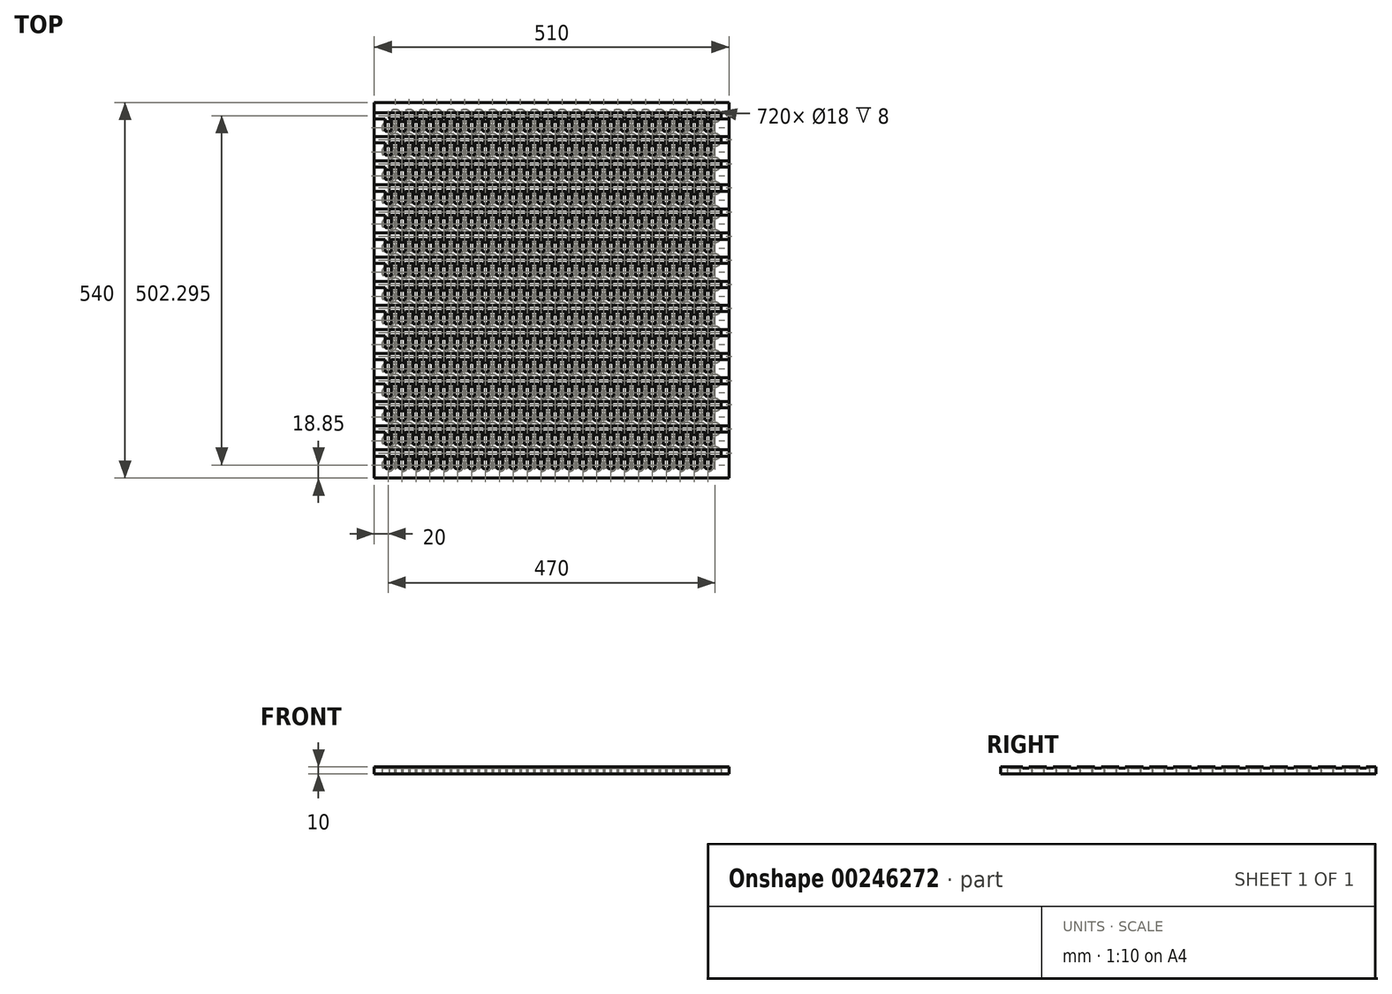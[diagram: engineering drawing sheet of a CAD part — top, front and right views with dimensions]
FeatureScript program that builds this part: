
annotation { "Feature Type Name" : "Feature", "Feature Type Description" : "" }
export const myFeature = defineFeature(function(context is Context, id is Id, definition is map)
    precondition{}
    {
        {
            var Q0;
            Q0=qCreatedBy(makeId("Top.planeOp"),FACE);
            var sketch = newSketch(context, id + "F0", { "sketchPlane" : qUnion([Q0])});
            skCircle(sketch, "E0", {"center": v(0, 0) * mm, "radius": 9 * mm});
            skCircle(sketch, "E1.1.0.0", {"center": v(20, 0) * mm, "radius": 9 * mm});
            skCircle(sketch, "E1.2.0.0", {"center": v(40, 0) * mm, "radius": 9 * mm});
            skCircle(sketch, "E1.3.0.0", {"center": v(60, 0) * mm, "radius": 9 * mm});
            skCircle(sketch, "E1.4.0.0", {"center": v(80, 0) * mm, "radius": 9 * mm});
            skCircle(sketch, "E1.5.0.0", {"center": v(100, 0) * mm, "radius": 9 * mm});
            skCircle(sketch, "E1.6.0.0", {"center": v(120, 0) * mm, "radius": 9 * mm});
            skCircle(sketch, "E1.7.0.0", {"center": v(140, 0) * mm, "radius": 9 * mm});
            skCircle(sketch, "E1.8.0.0", {"center": v(160, 0) * mm, "radius": 9 * mm});
            skCircle(sketch, "E1.9.0.0", {"center": v(180, 0) * mm, "radius": 9 * mm});
            skCircle(sketch, "E1.10.0.0", {"center": v(200, 0) * mm, "radius": 9 * mm});
            skCircle(sketch, "E1.11.0.0", {"center": v(220, 0) * mm, "radius": 9 * mm});
            skCircle(sketch, "E1.12.0.0", {"center": v(240, 0) * mm, "radius": 9 * mm});
            skCircle(sketch, "E1.13.0.0", {"center": v(260, 0) * mm, "radius": 9 * mm});
            skCircle(sketch, "E1.14.0.0", {"center": v(280, 0) * mm, "radius": 9 * mm});
            skCircle(sketch, "E1.15.0.0", {"center": v(300, 0) * mm, "radius": 9 * mm});
            skCircle(sketch, "E1.16.0.0", {"center": v(320, 0) * mm, "radius": 9 * mm});
            skCircle(sketch, "E1.17.0.0", {"center": v(340, 0) * mm, "radius": 9 * mm});
            skCircle(sketch, "E1.18.0.0", {"center": v(360, 0) * mm, "radius": 9 * mm});
            skCircle(sketch, "E1.19.0.0", {"center": v(380, 0) * mm, "radius": 9 * mm});
            skCircle(sketch, "E1.20.0.0", {"center": v(400, 0) * mm, "radius": 9 * mm});
            skCircle(sketch, "E1.21.0.0", {"center": v(420, 0) * mm, "radius": 9 * mm});
            skCircle(sketch, "E1.22.0.0", {"center": v(440, 0) * mm, "radius": 9 * mm});
            skCircle(sketch, "E1.23.0.0", {"center": v(460, 0) * mm, "radius": 9 * mm});
            skLineSegment(sketch, "E1.direction1", {"start": v(0, 0) * mm, "end": v(20, 0) * mm, "construction": true});
            skCircle(sketch, "E2", {"center": v(10, 17.32) * mm, "radius": 9 * mm});
            skCircle(sketch, "E3.1.0.0", {"center": v(30, 17.32) * mm, "radius": 9 * mm});
            skCircle(sketch, "E3.2.0.0", {"center": v(50, 17.32) * mm, "radius": 9 * mm});
            skCircle(sketch, "E3.3.0.0", {"center": v(70, 17.32) * mm, "radius": 9 * mm});
            skCircle(sketch, "E3.4.0.0", {"center": v(90, 17.32) * mm, "radius": 9 * mm});
            skCircle(sketch, "E3.5.0.0", {"center": v(110, 17.32) * mm, "radius": 9 * mm});
            skCircle(sketch, "E3.6.0.0", {"center": v(130, 17.32) * mm, "radius": 9 * mm});
            skCircle(sketch, "E3.7.0.0", {"center": v(150, 17.32) * mm, "radius": 9 * mm});
            skCircle(sketch, "E3.8.0.0", {"center": v(170, 17.32) * mm, "radius": 9 * mm});
            skCircle(sketch, "E3.9.0.0", {"center": v(190, 17.32) * mm, "radius": 9 * mm});
            skCircle(sketch, "E3.10.0.0", {"center": v(210, 17.32) * mm, "radius": 9 * mm});
            skCircle(sketch, "E3.11.0.0", {"center": v(230, 17.32) * mm, "radius": 9 * mm});
            skCircle(sketch, "E3.12.0.0", {"center": v(250, 17.32) * mm, "radius": 9 * mm});
            skCircle(sketch, "E3.13.0.0", {"center": v(270, 17.32) * mm, "radius": 9 * mm});
            skCircle(sketch, "E3.14.0.0", {"center": v(290, 17.32) * mm, "radius": 9 * mm});
            skCircle(sketch, "E3.15.0.0", {"center": v(310, 17.32) * mm, "radius": 9 * mm});
            skCircle(sketch, "E3.16.0.0", {"center": v(330, 17.32) * mm, "radius": 9 * mm});
            skCircle(sketch, "E3.17.0.0", {"center": v(350, 17.32) * mm, "radius": 9 * mm});
            skCircle(sketch, "E3.18.0.0", {"center": v(370, 17.32) * mm, "radius": 9 * mm});
            skCircle(sketch, "E3.19.0.0", {"center": v(390, 17.32) * mm, "radius": 9 * mm});
            skCircle(sketch, "E3.20.0.0", {"center": v(410, 17.32) * mm, "radius": 9 * mm});
            skCircle(sketch, "E3.21.0.0", {"center": v(430, 17.32) * mm, "radius": 9 * mm});
            skCircle(sketch, "E3.22.0.0", {"center": v(450, 17.32) * mm, "radius": 9 * mm});
            skCircle(sketch, "E3.23.0.0", {"center": v(470, 17.32) * mm, "radius": 9 * mm});
            skLineSegment(sketch, "E3.direction1", {"start": v(10, 17.32) * mm, "end": v(30, 17.32) * mm, "construction": true});
            skCircle(sketch, "E4.0.1.0", {"center": v(280, 34.64) * mm, "radius": 9 * mm});
            skCircle(sketch, "E4.0.1.1", {"center": v(260, 34.64) * mm, "radius": 9 * mm});
            skCircle(sketch, "E4.0.1.2", {"center": v(130, 51.96) * mm, "radius": 9 * mm});
            skCircle(sketch, "E4.0.1.3", {"center": v(60, 34.64) * mm, "radius": 9 * mm});
            skCircle(sketch, "E4.0.1.4", {"center": v(80, 34.64) * mm, "radius": 9 * mm});
            skCircle(sketch, "E4.0.1.5", {"center": v(100, 34.64) * mm, "radius": 9 * mm});
            skCircle(sketch, "E4.0.1.6", {"center": v(350, 51.96) * mm, "radius": 9 * mm});
            skCircle(sketch, "E4.0.1.7", {"center": v(0, 34.64) * mm, "radius": 9 * mm});
            skCircle(sketch, "E4.0.1.8", {"center": v(120, 34.64) * mm, "radius": 9 * mm});
            skCircle(sketch, "E4.0.1.9", {"center": v(30, 51.96) * mm, "radius": 9 * mm});
            skCircle(sketch, "E4.0.1.10", {"center": v(380, 34.64) * mm, "radius": 9 * mm});
            skCircle(sketch, "E4.0.1.11", {"center": v(140, 34.64) * mm, "radius": 9 * mm});
            skCircle(sketch, "E4.0.1.12", {"center": v(450, 51.96) * mm, "radius": 9 * mm});
            skCircle(sketch, "E4.0.1.13", {"center": v(160, 34.64) * mm, "radius": 9 * mm});
            skCircle(sketch, "E4.0.1.14", {"center": v(300, 34.64) * mm, "radius": 9 * mm});
            skCircle(sketch, "E4.0.1.15", {"center": v(40, 34.64) * mm, "radius": 9 * mm});
            skCircle(sketch, "E4.0.1.16", {"center": v(210, 51.96) * mm, "radius": 9 * mm});
            skCircle(sketch, "E4.0.1.17", {"center": v(330, 51.96) * mm, "radius": 9 * mm});
            skCircle(sketch, "E4.0.1.18", {"center": v(270, 51.96) * mm, "radius": 9 * mm});
            skCircle(sketch, "E4.0.1.19", {"center": v(440, 34.64) * mm, "radius": 9 * mm});
            skCircle(sketch, "E4.0.1.20", {"center": v(110, 51.96) * mm, "radius": 9 * mm});
            skCircle(sketch, "E4.0.1.21", {"center": v(250, 51.96) * mm, "radius": 9 * mm});
            skCircle(sketch, "E4.0.1.22", {"center": v(180, 34.64) * mm, "radius": 9 * mm});
            skCircle(sketch, "E4.0.1.23", {"center": v(430, 51.96) * mm, "radius": 9 * mm});
            skCircle(sketch, "E4.0.1.24", {"center": v(200, 34.64) * mm, "radius": 9 * mm});
            skCircle(sketch, "E4.0.1.25", {"center": v(420, 34.64) * mm, "radius": 9 * mm});
            skCircle(sketch, "E4.0.1.26", {"center": v(70, 51.96) * mm, "radius": 9 * mm});
            skCircle(sketch, "E4.0.1.27", {"center": v(390, 51.96) * mm, "radius": 9 * mm});
            skCircle(sketch, "E4.0.1.28", {"center": v(220, 34.64) * mm, "radius": 9 * mm});
            skCircle(sketch, "E4.0.1.29", {"center": v(190, 51.96) * mm, "radius": 9 * mm});
            skCircle(sketch, "E4.0.1.30", {"center": v(90, 51.96) * mm, "radius": 9 * mm});
            skCircle(sketch, "E4.0.1.31", {"center": v(230, 51.96) * mm, "radius": 9 * mm});
            skCircle(sketch, "E4.0.1.32", {"center": v(150, 51.96) * mm, "radius": 9 * mm});
            skCircle(sketch, "E4.0.1.33", {"center": v(470, 51.96) * mm, "radius": 9 * mm});
            skCircle(sketch, "E4.0.1.34", {"center": v(410, 51.96) * mm, "radius": 9 * mm});
            skCircle(sketch, "E4.0.1.35", {"center": v(50, 51.96) * mm, "radius": 9 * mm});
            skCircle(sketch, "E4.0.1.36", {"center": v(400, 34.64) * mm, "radius": 9 * mm});
            skCircle(sketch, "E4.0.1.37", {"center": v(240, 34.64) * mm, "radius": 9 * mm});
            skCircle(sketch, "E4.0.1.38", {"center": v(320, 34.64) * mm, "radius": 9 * mm});
            skCircle(sketch, "E4.0.1.39", {"center": v(370, 51.96) * mm, "radius": 9 * mm});
            skCircle(sketch, "E4.0.1.40", {"center": v(10, 51.96) * mm, "radius": 9 * mm});
            skCircle(sketch, "E4.0.1.41", {"center": v(290, 51.96) * mm, "radius": 9 * mm});
            skCircle(sketch, "E4.0.1.42", {"center": v(360, 34.64) * mm, "radius": 9 * mm});
            skCircle(sketch, "E4.0.1.43", {"center": v(460, 34.64) * mm, "radius": 9 * mm});
            skCircle(sketch, "E4.0.1.44", {"center": v(310, 51.96) * mm, "radius": 9 * mm});
            skCircle(sketch, "E4.0.1.45", {"center": v(340, 34.64) * mm, "radius": 9 * mm});
            skCircle(sketch, "E4.0.1.46", {"center": v(170, 51.96) * mm, "radius": 9 * mm});
            skCircle(sketch, "E4.0.1.47", {"center": v(20, 34.64) * mm, "radius": 9 * mm});
            skLineSegment(sketch, "E4.0.1.48", {"start": v(0, 34.64) * mm, "end": v(20, 34.64) * mm, "construction": true});
            skLineSegment(sketch, "E4.0.1.49", {"start": v(10, 51.96) * mm, "end": v(30, 51.96) * mm, "construction": true});
            skCircle(sketch, "E4.0.2.0", {"center": v(280, 69.28) * mm, "radius": 9 * mm});
            skCircle(sketch, "E4.0.2.1", {"center": v(260, 69.28) * mm, "radius": 9 * mm});
            skCircle(sketch, "E4.0.2.2", {"center": v(130, 86.6) * mm, "radius": 9 * mm});
            skCircle(sketch, "E4.0.2.3", {"center": v(60, 69.28) * mm, "radius": 9 * mm});
            skCircle(sketch, "E4.0.2.4", {"center": v(80, 69.28) * mm, "radius": 9 * mm});
            skCircle(sketch, "E4.0.2.5", {"center": v(100, 69.28) * mm, "radius": 9 * mm});
            skCircle(sketch, "E4.0.2.6", {"center": v(350, 86.6) * mm, "radius": 9 * mm});
            skCircle(sketch, "E4.0.2.7", {"center": v(0, 69.28) * mm, "radius": 9 * mm});
            skCircle(sketch, "E4.0.2.8", {"center": v(120, 69.28) * mm, "radius": 9 * mm});
            skCircle(sketch, "E4.0.2.9", {"center": v(30, 86.6) * mm, "radius": 9 * mm});
            skCircle(sketch, "E4.0.2.10", {"center": v(380, 69.28) * mm, "radius": 9 * mm});
            skCircle(sketch, "E4.0.2.11", {"center": v(140, 69.28) * mm, "radius": 9 * mm});
            skCircle(sketch, "E4.0.2.12", {"center": v(450, 86.6) * mm, "radius": 9 * mm});
            skCircle(sketch, "E4.0.2.13", {"center": v(160, 69.28) * mm, "radius": 9 * mm});
            skCircle(sketch, "E4.0.2.14", {"center": v(300, 69.28) * mm, "radius": 9 * mm});
            skCircle(sketch, "E4.0.2.15", {"center": v(40, 69.28) * mm, "radius": 9 * mm});
            skCircle(sketch, "E4.0.2.16", {"center": v(210, 86.6) * mm, "radius": 9 * mm});
            skCircle(sketch, "E4.0.2.17", {"center": v(330, 86.6) * mm, "radius": 9 * mm});
            skCircle(sketch, "E4.0.2.18", {"center": v(270, 86.6) * mm, "radius": 9 * mm});
            skCircle(sketch, "E4.0.2.19", {"center": v(440, 69.28) * mm, "radius": 9 * mm});
            skCircle(sketch, "E4.0.2.20", {"center": v(110, 86.6) * mm, "radius": 9 * mm});
            skCircle(sketch, "E4.0.2.21", {"center": v(250, 86.6) * mm, "radius": 9 * mm});
            skCircle(sketch, "E4.0.2.22", {"center": v(180, 69.28) * mm, "radius": 9 * mm});
            skCircle(sketch, "E4.0.2.23", {"center": v(430, 86.6) * mm, "radius": 9 * mm});
            skCircle(sketch, "E4.0.2.24", {"center": v(200, 69.28) * mm, "radius": 9 * mm});
            skCircle(sketch, "E4.0.2.25", {"center": v(420, 69.28) * mm, "radius": 9 * mm});
            skCircle(sketch, "E4.0.2.26", {"center": v(70, 86.6) * mm, "radius": 9 * mm});
            skCircle(sketch, "E4.0.2.27", {"center": v(390, 86.6) * mm, "radius": 9 * mm});
            skCircle(sketch, "E4.0.2.28", {"center": v(220, 69.28) * mm, "radius": 9 * mm});
            skCircle(sketch, "E4.0.2.29", {"center": v(190, 86.6) * mm, "radius": 9 * mm});
            skCircle(sketch, "E4.0.2.30", {"center": v(90, 86.6) * mm, "radius": 9 * mm});
            skCircle(sketch, "E4.0.2.31", {"center": v(230, 86.6) * mm, "radius": 9 * mm});
            skCircle(sketch, "E4.0.2.32", {"center": v(150, 86.6) * mm, "radius": 9 * mm});
            skCircle(sketch, "E4.0.2.33", {"center": v(470, 86.6) * mm, "radius": 9 * mm});
            skCircle(sketch, "E4.0.2.34", {"center": v(410, 86.6) * mm, "radius": 9 * mm});
            skCircle(sketch, "E4.0.2.35", {"center": v(50, 86.6) * mm, "radius": 9 * mm});
            skCircle(sketch, "E4.0.2.36", {"center": v(400, 69.28) * mm, "radius": 9 * mm});
            skCircle(sketch, "E4.0.2.37", {"center": v(240, 69.28) * mm, "radius": 9 * mm});
            skCircle(sketch, "E4.0.2.38", {"center": v(320, 69.28) * mm, "radius": 9 * mm});
            skCircle(sketch, "E4.0.2.39", {"center": v(370, 86.6) * mm, "radius": 9 * mm});
            skCircle(sketch, "E4.0.2.40", {"center": v(10, 86.6) * mm, "radius": 9 * mm});
            skCircle(sketch, "E4.0.2.41", {"center": v(290, 86.6) * mm, "radius": 9 * mm});
            skCircle(sketch, "E4.0.2.42", {"center": v(360, 69.28) * mm, "radius": 9 * mm});
            skCircle(sketch, "E4.0.2.43", {"center": v(460, 69.28) * mm, "radius": 9 * mm});
            skCircle(sketch, "E4.0.2.44", {"center": v(310, 86.6) * mm, "radius": 9 * mm});
            skCircle(sketch, "E4.0.2.45", {"center": v(340, 69.28) * mm, "radius": 9 * mm});
            skCircle(sketch, "E4.0.2.46", {"center": v(170, 86.6) * mm, "radius": 9 * mm});
            skCircle(sketch, "E4.0.2.47", {"center": v(20, 69.28) * mm, "radius": 9 * mm});
            skLineSegment(sketch, "E4.0.2.48", {"start": v(0, 69.28) * mm, "end": v(20, 69.28) * mm, "construction": true});
            skLineSegment(sketch, "E4.0.2.49", {"start": v(10, 86.6) * mm, "end": v(30, 86.6) * mm, "construction": true});
            skCircle(sketch, "E4.0.3.0", {"center": v(280, 103.92) * mm, "radius": 9 * mm});
            skCircle(sketch, "E4.0.3.1", {"center": v(260, 103.92) * mm, "radius": 9 * mm});
            skCircle(sketch, "E4.0.3.2", {"center": v(130, 121.24) * mm, "radius": 9 * mm});
            skCircle(sketch, "E4.0.3.3", {"center": v(60, 103.92) * mm, "radius": 9 * mm});
            skCircle(sketch, "E4.0.3.4", {"center": v(80, 103.92) * mm, "radius": 9 * mm});
            skCircle(sketch, "E4.0.3.5", {"center": v(100, 103.92) * mm, "radius": 9 * mm});
            skCircle(sketch, "E4.0.3.6", {"center": v(350, 121.24) * mm, "radius": 9 * mm});
            skCircle(sketch, "E4.0.3.7", {"center": v(0, 103.92) * mm, "radius": 9 * mm});
            skCircle(sketch, "E4.0.3.8", {"center": v(120, 103.92) * mm, "radius": 9 * mm});
            skCircle(sketch, "E4.0.3.9", {"center": v(30, 121.24) * mm, "radius": 9 * mm});
            skCircle(sketch, "E4.0.3.10", {"center": v(380, 103.92) * mm, "radius": 9 * mm});
            skCircle(sketch, "E4.0.3.11", {"center": v(140, 103.92) * mm, "radius": 9 * mm});
            skCircle(sketch, "E4.0.3.12", {"center": v(450, 121.24) * mm, "radius": 9 * mm});
            skCircle(sketch, "E4.0.3.13", {"center": v(160, 103.92) * mm, "radius": 9 * mm});
            skCircle(sketch, "E4.0.3.14", {"center": v(300, 103.92) * mm, "radius": 9 * mm});
            skCircle(sketch, "E4.0.3.15", {"center": v(40, 103.92) * mm, "radius": 9 * mm});
            skCircle(sketch, "E4.0.3.16", {"center": v(210, 121.24) * mm, "radius": 9 * mm});
            skCircle(sketch, "E4.0.3.17", {"center": v(330, 121.24) * mm, "radius": 9 * mm});
            skCircle(sketch, "E4.0.3.18", {"center": v(270, 121.24) * mm, "radius": 9 * mm});
            skCircle(sketch, "E4.0.3.19", {"center": v(440, 103.92) * mm, "radius": 9 * mm});
            skCircle(sketch, "E4.0.3.20", {"center": v(110, 121.24) * mm, "radius": 9 * mm});
            skCircle(sketch, "E4.0.3.21", {"center": v(250, 121.24) * mm, "radius": 9 * mm});
            skCircle(sketch, "E4.0.3.22", {"center": v(180, 103.92) * mm, "radius": 9 * mm});
            skCircle(sketch, "E4.0.3.23", {"center": v(430, 121.24) * mm, "radius": 9 * mm});
            skCircle(sketch, "E4.0.3.24", {"center": v(200, 103.92) * mm, "radius": 9 * mm});
            skCircle(sketch, "E4.0.3.25", {"center": v(420, 103.92) * mm, "radius": 9 * mm});
            skCircle(sketch, "E4.0.3.26", {"center": v(70, 121.24) * mm, "radius": 9 * mm});
            skCircle(sketch, "E4.0.3.27", {"center": v(390, 121.24) * mm, "radius": 9 * mm});
            skCircle(sketch, "E4.0.3.28", {"center": v(220, 103.92) * mm, "radius": 9 * mm});
            skCircle(sketch, "E4.0.3.29", {"center": v(190, 121.24) * mm, "radius": 9 * mm});
            skCircle(sketch, "E4.0.3.30", {"center": v(90, 121.24) * mm, "radius": 9 * mm});
            skCircle(sketch, "E4.0.3.31", {"center": v(230, 121.24) * mm, "radius": 9 * mm});
            skCircle(sketch, "E4.0.3.32", {"center": v(150, 121.24) * mm, "radius": 9 * mm});
            skCircle(sketch, "E4.0.3.33", {"center": v(470, 121.24) * mm, "radius": 9 * mm});
            skCircle(sketch, "E4.0.3.34", {"center": v(410, 121.24) * mm, "radius": 9 * mm});
            skCircle(sketch, "E4.0.3.35", {"center": v(50, 121.24) * mm, "radius": 9 * mm});
            skCircle(sketch, "E4.0.3.36", {"center": v(400, 103.92) * mm, "radius": 9 * mm});
            skCircle(sketch, "E4.0.3.37", {"center": v(240, 103.92) * mm, "radius": 9 * mm});
            skCircle(sketch, "E4.0.3.38", {"center": v(320, 103.92) * mm, "radius": 9 * mm});
            skCircle(sketch, "E4.0.3.39", {"center": v(370, 121.24) * mm, "radius": 9 * mm});
            skCircle(sketch, "E4.0.3.40", {"center": v(10, 121.24) * mm, "radius": 9 * mm});
            skCircle(sketch, "E4.0.3.41", {"center": v(290, 121.24) * mm, "radius": 9 * mm});
            skCircle(sketch, "E4.0.3.42", {"center": v(360, 103.92) * mm, "radius": 9 * mm});
            skCircle(sketch, "E4.0.3.43", {"center": v(460, 103.92) * mm, "radius": 9 * mm});
            skCircle(sketch, "E4.0.3.44", {"center": v(310, 121.24) * mm, "radius": 9 * mm});
            skCircle(sketch, "E4.0.3.45", {"center": v(340, 103.92) * mm, "radius": 9 * mm});
            skCircle(sketch, "E4.0.3.46", {"center": v(170, 121.24) * mm, "radius": 9 * mm});
            skCircle(sketch, "E4.0.3.47", {"center": v(20, 103.92) * mm, "radius": 9 * mm});
            skLineSegment(sketch, "E4.0.3.48", {"start": v(0, 103.92) * mm, "end": v(20, 103.92) * mm, "construction": true});
            skLineSegment(sketch, "E4.0.3.49", {"start": v(10, 121.24) * mm, "end": v(30, 121.24) * mm, "construction": true});
            skCircle(sketch, "E4.0.4.0", {"center": v(280, 138.56) * mm, "radius": 9 * mm});
            skCircle(sketch, "E4.0.4.1", {"center": v(260, 138.56) * mm, "radius": 9 * mm});
            skCircle(sketch, "E4.0.4.2", {"center": v(130, 155.88) * mm, "radius": 9 * mm});
            skCircle(sketch, "E4.0.4.3", {"center": v(60, 138.56) * mm, "radius": 9 * mm});
            skCircle(sketch, "E4.0.4.4", {"center": v(80, 138.56) * mm, "radius": 9 * mm});
            skCircle(sketch, "E4.0.4.5", {"center": v(100, 138.56) * mm, "radius": 9 * mm});
            skCircle(sketch, "E4.0.4.6", {"center": v(350, 155.88) * mm, "radius": 9 * mm});
            skCircle(sketch, "E4.0.4.7", {"center": v(0, 138.56) * mm, "radius": 9 * mm});
            skCircle(sketch, "E4.0.4.8", {"center": v(120, 138.56) * mm, "radius": 9 * mm});
            skCircle(sketch, "E4.0.4.9", {"center": v(30, 155.88) * mm, "radius": 9 * mm});
            skCircle(sketch, "E4.0.4.10", {"center": v(380, 138.56) * mm, "radius": 9 * mm});
            skCircle(sketch, "E4.0.4.11", {"center": v(140, 138.56) * mm, "radius": 9 * mm});
            skCircle(sketch, "E4.0.4.12", {"center": v(450, 155.88) * mm, "radius": 9 * mm});
            skCircle(sketch, "E4.0.4.13", {"center": v(160, 138.56) * mm, "radius": 9 * mm});
            skCircle(sketch, "E4.0.4.14", {"center": v(300, 138.56) * mm, "radius": 9 * mm});
            skCircle(sketch, "E4.0.4.15", {"center": v(40, 138.56) * mm, "radius": 9 * mm});
            skCircle(sketch, "E4.0.4.16", {"center": v(210, 155.88) * mm, "radius": 9 * mm});
            skCircle(sketch, "E4.0.4.17", {"center": v(330, 155.88) * mm, "radius": 9 * mm});
            skCircle(sketch, "E4.0.4.18", {"center": v(270, 155.88) * mm, "radius": 9 * mm});
            skCircle(sketch, "E4.0.4.19", {"center": v(440, 138.56) * mm, "radius": 9 * mm});
            skCircle(sketch, "E4.0.4.20", {"center": v(110, 155.88) * mm, "radius": 9 * mm});
            skCircle(sketch, "E4.0.4.21", {"center": v(250, 155.88) * mm, "radius": 9 * mm});
            skCircle(sketch, "E4.0.4.22", {"center": v(180, 138.56) * mm, "radius": 9 * mm});
            skCircle(sketch, "E4.0.4.23", {"center": v(430, 155.88) * mm, "radius": 9 * mm});
            skCircle(sketch, "E4.0.4.24", {"center": v(200, 138.56) * mm, "radius": 9 * mm});
            skCircle(sketch, "E4.0.4.25", {"center": v(420, 138.56) * mm, "radius": 9 * mm});
            skCircle(sketch, "E4.0.4.26", {"center": v(70, 155.88) * mm, "radius": 9 * mm});
            skCircle(sketch, "E4.0.4.27", {"center": v(390, 155.88) * mm, "radius": 9 * mm});
            skCircle(sketch, "E4.0.4.28", {"center": v(220, 138.56) * mm, "radius": 9 * mm});
            skCircle(sketch, "E4.0.4.29", {"center": v(190, 155.88) * mm, "radius": 9 * mm});
            skCircle(sketch, "E4.0.4.30", {"center": v(90, 155.88) * mm, "radius": 9 * mm});
            skCircle(sketch, "E4.0.4.31", {"center": v(230, 155.88) * mm, "radius": 9 * mm});
            skCircle(sketch, "E4.0.4.32", {"center": v(150, 155.88) * mm, "radius": 9 * mm});
            skCircle(sketch, "E4.0.4.33", {"center": v(470, 155.88) * mm, "radius": 9 * mm});
            skCircle(sketch, "E4.0.4.34", {"center": v(410, 155.88) * mm, "radius": 9 * mm});
            skCircle(sketch, "E4.0.4.35", {"center": v(50, 155.88) * mm, "radius": 9 * mm});
            skCircle(sketch, "E4.0.4.36", {"center": v(400, 138.56) * mm, "radius": 9 * mm});
            skCircle(sketch, "E4.0.4.37", {"center": v(240, 138.56) * mm, "radius": 9 * mm});
            skCircle(sketch, "E4.0.4.38", {"center": v(320, 138.56) * mm, "radius": 9 * mm});
            skCircle(sketch, "E4.0.4.39", {"center": v(370, 155.88) * mm, "radius": 9 * mm});
            skCircle(sketch, "E4.0.4.40", {"center": v(10, 155.88) * mm, "radius": 9 * mm});
            skCircle(sketch, "E4.0.4.41", {"center": v(290, 155.88) * mm, "radius": 9 * mm});
            skCircle(sketch, "E4.0.4.42", {"center": v(360, 138.56) * mm, "radius": 9 * mm});
            skCircle(sketch, "E4.0.4.43", {"center": v(460, 138.56) * mm, "radius": 9 * mm});
            skCircle(sketch, "E4.0.4.44", {"center": v(310, 155.88) * mm, "radius": 9 * mm});
            skCircle(sketch, "E4.0.4.45", {"center": v(340, 138.56) * mm, "radius": 9 * mm});
            skCircle(sketch, "E4.0.4.46", {"center": v(170, 155.88) * mm, "radius": 9 * mm});
            skCircle(sketch, "E4.0.4.47", {"center": v(20, 138.56) * mm, "radius": 9 * mm});
            skLineSegment(sketch, "E4.0.4.48", {"start": v(0, 138.56) * mm, "end": v(20, 138.56) * mm, "construction": true});
            skLineSegment(sketch, "E4.0.4.49", {"start": v(10, 155.88) * mm, "end": v(30, 155.88) * mm, "construction": true});
            skCircle(sketch, "E4.0.5.0", {"center": v(280, 173.2) * mm, "radius": 9 * mm});
            skCircle(sketch, "E4.0.5.1", {"center": v(260, 173.2) * mm, "radius": 9 * mm});
            skCircle(sketch, "E4.0.5.2", {"center": v(130, 190.53) * mm, "radius": 9 * mm});
            skCircle(sketch, "E4.0.5.3", {"center": v(60, 173.2) * mm, "radius": 9 * mm});
            skCircle(sketch, "E4.0.5.4", {"center": v(80, 173.2) * mm, "radius": 9 * mm});
            skCircle(sketch, "E4.0.5.5", {"center": v(100, 173.2) * mm, "radius": 9 * mm});
            skCircle(sketch, "E4.0.5.6", {"center": v(350, 190.53) * mm, "radius": 9 * mm});
            skCircle(sketch, "E4.0.5.7", {"center": v(0, 173.2) * mm, "radius": 9 * mm});
            skCircle(sketch, "E4.0.5.8", {"center": v(120, 173.2) * mm, "radius": 9 * mm});
            skCircle(sketch, "E4.0.5.9", {"center": v(30, 190.53) * mm, "radius": 9 * mm});
            skCircle(sketch, "E4.0.5.10", {"center": v(380, 173.2) * mm, "radius": 9 * mm});
            skCircle(sketch, "E4.0.5.11", {"center": v(140, 173.2) * mm, "radius": 9 * mm});
            skCircle(sketch, "E4.0.5.12", {"center": v(450, 190.53) * mm, "radius": 9 * mm});
            skCircle(sketch, "E4.0.5.13", {"center": v(160, 173.2) * mm, "radius": 9 * mm});
            skCircle(sketch, "E4.0.5.14", {"center": v(300, 173.2) * mm, "radius": 9 * mm});
            skCircle(sketch, "E4.0.5.15", {"center": v(40, 173.2) * mm, "radius": 9 * mm});
            skCircle(sketch, "E4.0.5.16", {"center": v(210, 190.53) * mm, "radius": 9 * mm});
            skCircle(sketch, "E4.0.5.17", {"center": v(330, 190.53) * mm, "radius": 9 * mm});
            skCircle(sketch, "E4.0.5.18", {"center": v(270, 190.53) * mm, "radius": 9 * mm});
            skCircle(sketch, "E4.0.5.19", {"center": v(440, 173.2) * mm, "radius": 9 * mm});
            skCircle(sketch, "E4.0.5.20", {"center": v(110, 190.53) * mm, "radius": 9 * mm});
            skCircle(sketch, "E4.0.5.21", {"center": v(250, 190.53) * mm, "radius": 9 * mm});
            skCircle(sketch, "E4.0.5.22", {"center": v(180, 173.2) * mm, "radius": 9 * mm});
            skCircle(sketch, "E4.0.5.23", {"center": v(430, 190.53) * mm, "radius": 9 * mm});
            skCircle(sketch, "E4.0.5.24", {"center": v(200, 173.2) * mm, "radius": 9 * mm});
            skCircle(sketch, "E4.0.5.25", {"center": v(420, 173.2) * mm, "radius": 9 * mm});
            skCircle(sketch, "E4.0.5.26", {"center": v(70, 190.53) * mm, "radius": 9 * mm});
            skCircle(sketch, "E4.0.5.27", {"center": v(390, 190.53) * mm, "radius": 9 * mm});
            skCircle(sketch, "E4.0.5.28", {"center": v(220, 173.2) * mm, "radius": 9 * mm});
            skCircle(sketch, "E4.0.5.29", {"center": v(190, 190.53) * mm, "radius": 9 * mm});
            skCircle(sketch, "E4.0.5.30", {"center": v(90, 190.53) * mm, "radius": 9 * mm});
            skCircle(sketch, "E4.0.5.31", {"center": v(230, 190.53) * mm, "radius": 9 * mm});
            skCircle(sketch, "E4.0.5.32", {"center": v(150, 190.53) * mm, "radius": 9 * mm});
            skCircle(sketch, "E4.0.5.33", {"center": v(470, 190.53) * mm, "radius": 9 * mm});
            skCircle(sketch, "E4.0.5.34", {"center": v(410, 190.53) * mm, "radius": 9 * mm});
            skCircle(sketch, "E4.0.5.35", {"center": v(50, 190.53) * mm, "radius": 9 * mm});
            skCircle(sketch, "E4.0.5.36", {"center": v(400, 173.2) * mm, "radius": 9 * mm});
            skCircle(sketch, "E4.0.5.37", {"center": v(240, 173.2) * mm, "radius": 9 * mm});
            skCircle(sketch, "E4.0.5.38", {"center": v(320, 173.2) * mm, "radius": 9 * mm});
            skCircle(sketch, "E4.0.5.39", {"center": v(370, 190.53) * mm, "radius": 9 * mm});
            skCircle(sketch, "E4.0.5.40", {"center": v(10, 190.53) * mm, "radius": 9 * mm});
            skCircle(sketch, "E4.0.5.41", {"center": v(290, 190.53) * mm, "radius": 9 * mm});
            skCircle(sketch, "E4.0.5.42", {"center": v(360, 173.2) * mm, "radius": 9 * mm});
            skCircle(sketch, "E4.0.5.43", {"center": v(460, 173.2) * mm, "radius": 9 * mm});
            skCircle(sketch, "E4.0.5.44", {"center": v(310, 190.53) * mm, "radius": 9 * mm});
            skCircle(sketch, "E4.0.5.45", {"center": v(340, 173.2) * mm, "radius": 9 * mm});
            skCircle(sketch, "E4.0.5.46", {"center": v(170, 190.53) * mm, "radius": 9 * mm});
            skCircle(sketch, "E4.0.5.47", {"center": v(20, 173.2) * mm, "radius": 9 * mm});
            skLineSegment(sketch, "E4.0.5.48", {"start": v(0, 173.2) * mm, "end": v(20, 173.2) * mm, "construction": true});
            skLineSegment(sketch, "E4.0.5.49", {"start": v(10, 190.53) * mm, "end": v(30, 190.53) * mm, "construction": true});
            skCircle(sketch, "E4.0.6.0", {"center": v(280, 207.85) * mm, "radius": 9 * mm});
            skCircle(sketch, "E4.0.6.1", {"center": v(260, 207.85) * mm, "radius": 9 * mm});
            skCircle(sketch, "E4.0.6.2", {"center": v(130, 225.17) * mm, "radius": 9 * mm});
            skCircle(sketch, "E4.0.6.3", {"center": v(60, 207.85) * mm, "radius": 9 * mm});
            skCircle(sketch, "E4.0.6.4", {"center": v(80, 207.85) * mm, "radius": 9 * mm});
            skCircle(sketch, "E4.0.6.5", {"center": v(100, 207.85) * mm, "radius": 9 * mm});
            skCircle(sketch, "E4.0.6.6", {"center": v(350, 225.17) * mm, "radius": 9 * mm});
            skCircle(sketch, "E4.0.6.7", {"center": v(0, 207.85) * mm, "radius": 9 * mm});
            skCircle(sketch, "E4.0.6.8", {"center": v(120, 207.85) * mm, "radius": 9 * mm});
            skCircle(sketch, "E4.0.6.9", {"center": v(30, 225.17) * mm, "radius": 9 * mm});
            skCircle(sketch, "E4.0.6.10", {"center": v(380, 207.85) * mm, "radius": 9 * mm});
            skCircle(sketch, "E4.0.6.11", {"center": v(140, 207.85) * mm, "radius": 9 * mm});
            skCircle(sketch, "E4.0.6.12", {"center": v(450, 225.17) * mm, "radius": 9 * mm});
            skCircle(sketch, "E4.0.6.13", {"center": v(160, 207.85) * mm, "radius": 9 * mm});
            skCircle(sketch, "E4.0.6.14", {"center": v(300, 207.85) * mm, "radius": 9 * mm});
            skCircle(sketch, "E4.0.6.15", {"center": v(40, 207.85) * mm, "radius": 9 * mm});
            skCircle(sketch, "E4.0.6.16", {"center": v(210, 225.17) * mm, "radius": 9 * mm});
            skCircle(sketch, "E4.0.6.17", {"center": v(330, 225.17) * mm, "radius": 9 * mm});
            skCircle(sketch, "E4.0.6.18", {"center": v(270, 225.17) * mm, "radius": 9 * mm});
            skCircle(sketch, "E4.0.6.19", {"center": v(440, 207.85) * mm, "radius": 9 * mm});
            skCircle(sketch, "E4.0.6.20", {"center": v(110, 225.17) * mm, "radius": 9 * mm});
            skCircle(sketch, "E4.0.6.21", {"center": v(250, 225.17) * mm, "radius": 9 * mm});
            skCircle(sketch, "E4.0.6.22", {"center": v(180, 207.85) * mm, "radius": 9 * mm});
            skCircle(sketch, "E4.0.6.23", {"center": v(430, 225.17) * mm, "radius": 9 * mm});
            skCircle(sketch, "E4.0.6.24", {"center": v(200, 207.85) * mm, "radius": 9 * mm});
            skCircle(sketch, "E4.0.6.25", {"center": v(420, 207.85) * mm, "radius": 9 * mm});
            skCircle(sketch, "E4.0.6.26", {"center": v(70, 225.17) * mm, "radius": 9 * mm});
            skCircle(sketch, "E4.0.6.27", {"center": v(390, 225.17) * mm, "radius": 9 * mm});
            skCircle(sketch, "E4.0.6.28", {"center": v(220, 207.85) * mm, "radius": 9 * mm});
            skCircle(sketch, "E4.0.6.29", {"center": v(190, 225.17) * mm, "radius": 9 * mm});
            skCircle(sketch, "E4.0.6.30", {"center": v(90, 225.17) * mm, "radius": 9 * mm});
            skCircle(sketch, "E4.0.6.31", {"center": v(230, 225.17) * mm, "radius": 9 * mm});
            skCircle(sketch, "E4.0.6.32", {"center": v(150, 225.17) * mm, "radius": 9 * mm});
            skCircle(sketch, "E4.0.6.33", {"center": v(470, 225.17) * mm, "radius": 9 * mm});
            skCircle(sketch, "E4.0.6.34", {"center": v(410, 225.17) * mm, "radius": 9 * mm});
            skCircle(sketch, "E4.0.6.35", {"center": v(50, 225.17) * mm, "radius": 9 * mm});
            skCircle(sketch, "E4.0.6.36", {"center": v(400, 207.85) * mm, "radius": 9 * mm});
            skCircle(sketch, "E4.0.6.37", {"center": v(240, 207.85) * mm, "radius": 9 * mm});
            skCircle(sketch, "E4.0.6.38", {"center": v(320, 207.85) * mm, "radius": 9 * mm});
            skCircle(sketch, "E4.0.6.39", {"center": v(370, 225.17) * mm, "radius": 9 * mm});
            skCircle(sketch, "E4.0.6.40", {"center": v(10, 225.17) * mm, "radius": 9 * mm});
            skCircle(sketch, "E4.0.6.41", {"center": v(290, 225.17) * mm, "radius": 9 * mm});
            skCircle(sketch, "E4.0.6.42", {"center": v(360, 207.85) * mm, "radius": 9 * mm});
            skCircle(sketch, "E4.0.6.43", {"center": v(460, 207.85) * mm, "radius": 9 * mm});
            skCircle(sketch, "E4.0.6.44", {"center": v(310, 225.17) * mm, "radius": 9 * mm});
            skCircle(sketch, "E4.0.6.45", {"center": v(340, 207.85) * mm, "radius": 9 * mm});
            skCircle(sketch, "E4.0.6.46", {"center": v(170, 225.17) * mm, "radius": 9 * mm});
            skCircle(sketch, "E4.0.6.47", {"center": v(20, 207.85) * mm, "radius": 9 * mm});
            skLineSegment(sketch, "E4.0.6.48", {"start": v(0, 207.85) * mm, "end": v(20, 207.85) * mm, "construction": true});
            skLineSegment(sketch, "E4.0.6.49", {"start": v(10, 225.17) * mm, "end": v(30, 225.17) * mm, "construction": true});
            skCircle(sketch, "E4.0.7.0", {"center": v(280, 242.49) * mm, "radius": 9 * mm});
            skCircle(sketch, "E4.0.7.1", {"center": v(260, 242.49) * mm, "radius": 9 * mm});
            skCircle(sketch, "E4.0.7.2", {"center": v(130, 259.8) * mm, "radius": 9 * mm});
            skCircle(sketch, "E4.0.7.3", {"center": v(60, 242.49) * mm, "radius": 9 * mm});
            skCircle(sketch, "E4.0.7.4", {"center": v(80, 242.49) * mm, "radius": 9 * mm});
            skCircle(sketch, "E4.0.7.5", {"center": v(100, 242.49) * mm, "radius": 9 * mm});
            skCircle(sketch, "E4.0.7.6", {"center": v(350, 259.8) * mm, "radius": 9 * mm});
            skCircle(sketch, "E4.0.7.7", {"center": v(0, 242.49) * mm, "radius": 9 * mm});
            skCircle(sketch, "E4.0.7.8", {"center": v(120, 242.49) * mm, "radius": 9 * mm});
            skCircle(sketch, "E4.0.7.9", {"center": v(30, 259.8) * mm, "radius": 9 * mm});
            skCircle(sketch, "E4.0.7.10", {"center": v(380, 242.49) * mm, "radius": 9 * mm});
            skCircle(sketch, "E4.0.7.11", {"center": v(140, 242.49) * mm, "radius": 9 * mm});
            skCircle(sketch, "E4.0.7.12", {"center": v(450, 259.8) * mm, "radius": 9 * mm});
            skCircle(sketch, "E4.0.7.13", {"center": v(160, 242.49) * mm, "radius": 9 * mm});
            skCircle(sketch, "E4.0.7.14", {"center": v(300, 242.49) * mm, "radius": 9 * mm});
            skCircle(sketch, "E4.0.7.15", {"center": v(40, 242.49) * mm, "radius": 9 * mm});
            skCircle(sketch, "E4.0.7.16", {"center": v(210, 259.8) * mm, "radius": 9 * mm});
            skCircle(sketch, "E4.0.7.17", {"center": v(330, 259.8) * mm, "radius": 9 * mm});
            skCircle(sketch, "E4.0.7.18", {"center": v(270, 259.8) * mm, "radius": 9 * mm});
            skCircle(sketch, "E4.0.7.19", {"center": v(440, 242.49) * mm, "radius": 9 * mm});
            skCircle(sketch, "E4.0.7.20", {"center": v(110, 259.8) * mm, "radius": 9 * mm});
            skCircle(sketch, "E4.0.7.21", {"center": v(250, 259.8) * mm, "radius": 9 * mm});
            skCircle(sketch, "E4.0.7.22", {"center": v(180, 242.49) * mm, "radius": 9 * mm});
            skCircle(sketch, "E4.0.7.23", {"center": v(430, 259.8) * mm, "radius": 9 * mm});
            skCircle(sketch, "E4.0.7.24", {"center": v(200, 242.49) * mm, "radius": 9 * mm});
            skCircle(sketch, "E4.0.7.25", {"center": v(420, 242.49) * mm, "radius": 9 * mm});
            skCircle(sketch, "E4.0.7.26", {"center": v(70, 259.8) * mm, "radius": 9 * mm});
            skCircle(sketch, "E4.0.7.27", {"center": v(390, 259.8) * mm, "radius": 9 * mm});
            skCircle(sketch, "E4.0.7.28", {"center": v(220, 242.49) * mm, "radius": 9 * mm});
            skCircle(sketch, "E4.0.7.29", {"center": v(190, 259.8) * mm, "radius": 9 * mm});
            skCircle(sketch, "E4.0.7.30", {"center": v(90, 259.8) * mm, "radius": 9 * mm});
            skCircle(sketch, "E4.0.7.31", {"center": v(230, 259.8) * mm, "radius": 9 * mm});
            skCircle(sketch, "E4.0.7.32", {"center": v(150, 259.8) * mm, "radius": 9 * mm});
            skCircle(sketch, "E4.0.7.33", {"center": v(470, 259.8) * mm, "radius": 9 * mm});
            skCircle(sketch, "E4.0.7.34", {"center": v(410, 259.8) * mm, "radius": 9 * mm});
            skCircle(sketch, "E4.0.7.35", {"center": v(50, 259.8) * mm, "radius": 9 * mm});
            skCircle(sketch, "E4.0.7.36", {"center": v(400, 242.49) * mm, "radius": 9 * mm});
            skCircle(sketch, "E4.0.7.37", {"center": v(240, 242.49) * mm, "radius": 9 * mm});
            skCircle(sketch, "E4.0.7.38", {"center": v(320, 242.49) * mm, "radius": 9 * mm});
            skCircle(sketch, "E4.0.7.39", {"center": v(370, 259.8) * mm, "radius": 9 * mm});
            skCircle(sketch, "E4.0.7.40", {"center": v(10, 259.8) * mm, "radius": 9 * mm});
            skCircle(sketch, "E4.0.7.41", {"center": v(290, 259.8) * mm, "radius": 9 * mm});
            skCircle(sketch, "E4.0.7.42", {"center": v(360, 242.49) * mm, "radius": 9 * mm});
            skCircle(sketch, "E4.0.7.43", {"center": v(460, 242.49) * mm, "radius": 9 * mm});
            skCircle(sketch, "E4.0.7.44", {"center": v(310, 259.8) * mm, "radius": 9 * mm});
            skCircle(sketch, "E4.0.7.45", {"center": v(340, 242.49) * mm, "radius": 9 * mm});
            skCircle(sketch, "E4.0.7.46", {"center": v(170, 259.8) * mm, "radius": 9 * mm});
            skCircle(sketch, "E4.0.7.47", {"center": v(20, 242.49) * mm, "radius": 9 * mm});
            skLineSegment(sketch, "E4.0.7.48", {"start": v(0, 242.49) * mm, "end": v(20, 242.49) * mm, "construction": true});
            skLineSegment(sketch, "E4.0.7.49", {"start": v(10, 259.8) * mm, "end": v(30, 259.8) * mm, "construction": true});
            skCircle(sketch, "E4.0.8.0", {"center": v(280, 277.13) * mm, "radius": 9 * mm});
            skCircle(sketch, "E4.0.8.1", {"center": v(260, 277.13) * mm, "radius": 9 * mm});
            skCircle(sketch, "E4.0.8.2", {"center": v(130, 294.45) * mm, "radius": 9 * mm});
            skCircle(sketch, "E4.0.8.3", {"center": v(60, 277.13) * mm, "radius": 9 * mm});
            skCircle(sketch, "E4.0.8.4", {"center": v(80, 277.13) * mm, "radius": 9 * mm});
            skCircle(sketch, "E4.0.8.5", {"center": v(100, 277.13) * mm, "radius": 9 * mm});
            skCircle(sketch, "E4.0.8.6", {"center": v(350, 294.45) * mm, "radius": 9 * mm});
            skCircle(sketch, "E4.0.8.7", {"center": v(0, 277.13) * mm, "radius": 9 * mm});
            skCircle(sketch, "E4.0.8.8", {"center": v(120, 277.13) * mm, "radius": 9 * mm});
            skCircle(sketch, "E4.0.8.9", {"center": v(30, 294.45) * mm, "radius": 9 * mm});
            skCircle(sketch, "E4.0.8.10", {"center": v(380, 277.13) * mm, "radius": 9 * mm});
            skCircle(sketch, "E4.0.8.11", {"center": v(140, 277.13) * mm, "radius": 9 * mm});
            skCircle(sketch, "E4.0.8.12", {"center": v(450, 294.45) * mm, "radius": 9 * mm});
            skCircle(sketch, "E4.0.8.13", {"center": v(160, 277.13) * mm, "radius": 9 * mm});
            skCircle(sketch, "E4.0.8.14", {"center": v(300, 277.13) * mm, "radius": 9 * mm});
            skCircle(sketch, "E4.0.8.15", {"center": v(40, 277.13) * mm, "radius": 9 * mm});
            skCircle(sketch, "E4.0.8.16", {"center": v(210, 294.45) * mm, "radius": 9 * mm});
            skCircle(sketch, "E4.0.8.17", {"center": v(330, 294.45) * mm, "radius": 9 * mm});
            skCircle(sketch, "E4.0.8.18", {"center": v(270, 294.45) * mm, "radius": 9 * mm});
            skCircle(sketch, "E4.0.8.19", {"center": v(440, 277.13) * mm, "radius": 9 * mm});
            skCircle(sketch, "E4.0.8.20", {"center": v(110, 294.45) * mm, "radius": 9 * mm});
            skCircle(sketch, "E4.0.8.21", {"center": v(250, 294.45) * mm, "radius": 9 * mm});
            skCircle(sketch, "E4.0.8.22", {"center": v(180, 277.13) * mm, "radius": 9 * mm});
            skCircle(sketch, "E4.0.8.23", {"center": v(430, 294.45) * mm, "radius": 9 * mm});
            skCircle(sketch, "E4.0.8.24", {"center": v(200, 277.13) * mm, "radius": 9 * mm});
            skCircle(sketch, "E4.0.8.25", {"center": v(420, 277.13) * mm, "radius": 9 * mm});
            skCircle(sketch, "E4.0.8.26", {"center": v(70, 294.45) * mm, "radius": 9 * mm});
            skCircle(sketch, "E4.0.8.27", {"center": v(390, 294.45) * mm, "radius": 9 * mm});
            skCircle(sketch, "E4.0.8.28", {"center": v(220, 277.13) * mm, "radius": 9 * mm});
            skCircle(sketch, "E4.0.8.29", {"center": v(190, 294.45) * mm, "radius": 9 * mm});
            skCircle(sketch, "E4.0.8.30", {"center": v(90, 294.45) * mm, "radius": 9 * mm});
            skCircle(sketch, "E4.0.8.31", {"center": v(230, 294.45) * mm, "radius": 9 * mm});
            skCircle(sketch, "E4.0.8.32", {"center": v(150, 294.45) * mm, "radius": 9 * mm});
            skCircle(sketch, "E4.0.8.33", {"center": v(470, 294.45) * mm, "radius": 9 * mm});
            skCircle(sketch, "E4.0.8.34", {"center": v(410, 294.45) * mm, "radius": 9 * mm});
            skCircle(sketch, "E4.0.8.35", {"center": v(50, 294.45) * mm, "radius": 9 * mm});
            skCircle(sketch, "E4.0.8.36", {"center": v(400, 277.13) * mm, "radius": 9 * mm});
            skCircle(sketch, "E4.0.8.37", {"center": v(240, 277.13) * mm, "radius": 9 * mm});
            skCircle(sketch, "E4.0.8.38", {"center": v(320, 277.13) * mm, "radius": 9 * mm});
            skCircle(sketch, "E4.0.8.39", {"center": v(370, 294.45) * mm, "radius": 9 * mm});
            skCircle(sketch, "E4.0.8.40", {"center": v(10, 294.45) * mm, "radius": 9 * mm});
            skCircle(sketch, "E4.0.8.41", {"center": v(290, 294.45) * mm, "radius": 9 * mm});
            skCircle(sketch, "E4.0.8.42", {"center": v(360, 277.13) * mm, "radius": 9 * mm});
            skCircle(sketch, "E4.0.8.43", {"center": v(460, 277.13) * mm, "radius": 9 * mm});
            skCircle(sketch, "E4.0.8.44", {"center": v(310, 294.45) * mm, "radius": 9 * mm});
            skCircle(sketch, "E4.0.8.45", {"center": v(340, 277.13) * mm, "radius": 9 * mm});
            skCircle(sketch, "E4.0.8.46", {"center": v(170, 294.45) * mm, "radius": 9 * mm});
            skCircle(sketch, "E4.0.8.47", {"center": v(20, 277.13) * mm, "radius": 9 * mm});
            skLineSegment(sketch, "E4.0.8.48", {"start": v(0, 277.13) * mm, "end": v(20, 277.13) * mm, "construction": true});
            skLineSegment(sketch, "E4.0.8.49", {"start": v(10, 294.45) * mm, "end": v(30, 294.45) * mm, "construction": true});
            skCircle(sketch, "E4.0.9.0", {"center": v(280, 311.77) * mm, "radius": 9 * mm});
            skCircle(sketch, "E4.0.9.1", {"center": v(260, 311.77) * mm, "radius": 9 * mm});
            skCircle(sketch, "E4.0.9.2", {"center": v(130, 329.09) * mm, "radius": 9 * mm});
            skCircle(sketch, "E4.0.9.3", {"center": v(60, 311.77) * mm, "radius": 9 * mm});
            skCircle(sketch, "E4.0.9.4", {"center": v(80, 311.77) * mm, "radius": 9 * mm});
            skCircle(sketch, "E4.0.9.5", {"center": v(100, 311.77) * mm, "radius": 9 * mm});
            skCircle(sketch, "E4.0.9.6", {"center": v(350, 329.09) * mm, "radius": 9 * mm});
            skCircle(sketch, "E4.0.9.7", {"center": v(0, 311.77) * mm, "radius": 9 * mm});
            skCircle(sketch, "E4.0.9.8", {"center": v(120, 311.77) * mm, "radius": 9 * mm});
            skCircle(sketch, "E4.0.9.9", {"center": v(30, 329.09) * mm, "radius": 9 * mm});
            skCircle(sketch, "E4.0.9.10", {"center": v(380, 311.77) * mm, "radius": 9 * mm});
            skCircle(sketch, "E4.0.9.11", {"center": v(140, 311.77) * mm, "radius": 9 * mm});
            skCircle(sketch, "E4.0.9.12", {"center": v(450, 329.09) * mm, "radius": 9 * mm});
            skCircle(sketch, "E4.0.9.13", {"center": v(160, 311.77) * mm, "radius": 9 * mm});
            skCircle(sketch, "E4.0.9.14", {"center": v(300, 311.77) * mm, "radius": 9 * mm});
            skCircle(sketch, "E4.0.9.15", {"center": v(40, 311.77) * mm, "radius": 9 * mm});
            skCircle(sketch, "E4.0.9.16", {"center": v(210, 329.09) * mm, "radius": 9 * mm});
            skCircle(sketch, "E4.0.9.17", {"center": v(330, 329.09) * mm, "radius": 9 * mm});
            skCircle(sketch, "E4.0.9.18", {"center": v(270, 329.09) * mm, "radius": 9 * mm});
            skCircle(sketch, "E4.0.9.19", {"center": v(440, 311.77) * mm, "radius": 9 * mm});
            skCircle(sketch, "E4.0.9.20", {"center": v(110, 329.09) * mm, "radius": 9 * mm});
            skCircle(sketch, "E4.0.9.21", {"center": v(250, 329.09) * mm, "radius": 9 * mm});
            skCircle(sketch, "E4.0.9.22", {"center": v(180, 311.77) * mm, "radius": 9 * mm});
            skCircle(sketch, "E4.0.9.23", {"center": v(430, 329.09) * mm, "radius": 9 * mm});
            skCircle(sketch, "E4.0.9.24", {"center": v(200, 311.77) * mm, "radius": 9 * mm});
            skCircle(sketch, "E4.0.9.25", {"center": v(420, 311.77) * mm, "radius": 9 * mm});
            skCircle(sketch, "E4.0.9.26", {"center": v(70, 329.09) * mm, "radius": 9 * mm});
            skCircle(sketch, "E4.0.9.27", {"center": v(390, 329.09) * mm, "radius": 9 * mm});
            skCircle(sketch, "E4.0.9.28", {"center": v(220, 311.77) * mm, "radius": 9 * mm});
            skCircle(sketch, "E4.0.9.29", {"center": v(190, 329.09) * mm, "radius": 9 * mm});
            skCircle(sketch, "E4.0.9.30", {"center": v(90, 329.09) * mm, "radius": 9 * mm});
            skCircle(sketch, "E4.0.9.31", {"center": v(230, 329.09) * mm, "radius": 9 * mm});
            skCircle(sketch, "E4.0.9.32", {"center": v(150, 329.09) * mm, "radius": 9 * mm});
            skCircle(sketch, "E4.0.9.33", {"center": v(470, 329.09) * mm, "radius": 9 * mm});
            skCircle(sketch, "E4.0.9.34", {"center": v(410, 329.09) * mm, "radius": 9 * mm});
            skCircle(sketch, "E4.0.9.35", {"center": v(50, 329.09) * mm, "radius": 9 * mm});
            skCircle(sketch, "E4.0.9.36", {"center": v(400, 311.77) * mm, "radius": 9 * mm});
            skCircle(sketch, "E4.0.9.37", {"center": v(240, 311.77) * mm, "radius": 9 * mm});
            skCircle(sketch, "E4.0.9.38", {"center": v(320, 311.77) * mm, "radius": 9 * mm});
            skCircle(sketch, "E4.0.9.39", {"center": v(370, 329.09) * mm, "radius": 9 * mm});
            skCircle(sketch, "E4.0.9.40", {"center": v(10, 329.09) * mm, "radius": 9 * mm});
            skCircle(sketch, "E4.0.9.41", {"center": v(290, 329.09) * mm, "radius": 9 * mm});
            skCircle(sketch, "E4.0.9.42", {"center": v(360, 311.77) * mm, "radius": 9 * mm});
            skCircle(sketch, "E4.0.9.43", {"center": v(460, 311.77) * mm, "radius": 9 * mm});
            skCircle(sketch, "E4.0.9.44", {"center": v(310, 329.09) * mm, "radius": 9 * mm});
            skCircle(sketch, "E4.0.9.45", {"center": v(340, 311.77) * mm, "radius": 9 * mm});
            skCircle(sketch, "E4.0.9.46", {"center": v(170, 329.09) * mm, "radius": 9 * mm});
            skCircle(sketch, "E4.0.9.47", {"center": v(20, 311.77) * mm, "radius": 9 * mm});
            skLineSegment(sketch, "E4.0.9.48", {"start": v(0, 311.77) * mm, "end": v(20, 311.77) * mm, "construction": true});
            skLineSegment(sketch, "E4.0.9.49", {"start": v(10, 329.09) * mm, "end": v(30, 329.09) * mm, "construction": true});
            skCircle(sketch, "E4.0.10.0", {"center": v(280, 346.41) * mm, "radius": 9 * mm});
            skCircle(sketch, "E4.0.10.1", {"center": v(260, 346.41) * mm, "radius": 9 * mm});
            skCircle(sketch, "E4.0.10.2", {"center": v(130, 363.73) * mm, "radius": 9 * mm});
            skCircle(sketch, "E4.0.10.3", {"center": v(60, 346.41) * mm, "radius": 9 * mm});
            skCircle(sketch, "E4.0.10.4", {"center": v(80, 346.41) * mm, "radius": 9 * mm});
            skCircle(sketch, "E4.0.10.5", {"center": v(100, 346.41) * mm, "radius": 9 * mm});
            skCircle(sketch, "E4.0.10.6", {"center": v(350, 363.73) * mm, "radius": 9 * mm});
            skCircle(sketch, "E4.0.10.7", {"center": v(0, 346.41) * mm, "radius": 9 * mm});
            skCircle(sketch, "E4.0.10.8", {"center": v(120, 346.41) * mm, "radius": 9 * mm});
            skCircle(sketch, "E4.0.10.9", {"center": v(30, 363.73) * mm, "radius": 9 * mm});
            skCircle(sketch, "E4.0.10.10", {"center": v(380, 346.41) * mm, "radius": 9 * mm});
            skCircle(sketch, "E4.0.10.11", {"center": v(140, 346.41) * mm, "radius": 9 * mm});
            skCircle(sketch, "E4.0.10.12", {"center": v(450, 363.73) * mm, "radius": 9 * mm});
            skCircle(sketch, "E4.0.10.13", {"center": v(160, 346.41) * mm, "radius": 9 * mm});
            skCircle(sketch, "E4.0.10.14", {"center": v(300, 346.41) * mm, "radius": 9 * mm});
            skCircle(sketch, "E4.0.10.15", {"center": v(40, 346.41) * mm, "radius": 9 * mm});
            skCircle(sketch, "E4.0.10.16", {"center": v(210, 363.73) * mm, "radius": 9 * mm});
            skCircle(sketch, "E4.0.10.17", {"center": v(330, 363.73) * mm, "radius": 9 * mm});
            skCircle(sketch, "E4.0.10.18", {"center": v(270, 363.73) * mm, "radius": 9 * mm});
            skCircle(sketch, "E4.0.10.19", {"center": v(440, 346.41) * mm, "radius": 9 * mm});
            skCircle(sketch, "E4.0.10.20", {"center": v(110, 363.73) * mm, "radius": 9 * mm});
            skCircle(sketch, "E4.0.10.21", {"center": v(250, 363.73) * mm, "radius": 9 * mm});
            skCircle(sketch, "E4.0.10.22", {"center": v(180, 346.41) * mm, "radius": 9 * mm});
            skCircle(sketch, "E4.0.10.23", {"center": v(430, 363.73) * mm, "radius": 9 * mm});
            skCircle(sketch, "E4.0.10.24", {"center": v(200, 346.41) * mm, "radius": 9 * mm});
            skCircle(sketch, "E4.0.10.25", {"center": v(420, 346.41) * mm, "radius": 9 * mm});
            skCircle(sketch, "E4.0.10.26", {"center": v(70, 363.73) * mm, "radius": 9 * mm});
            skCircle(sketch, "E4.0.10.27", {"center": v(390, 363.73) * mm, "radius": 9 * mm});
            skCircle(sketch, "E4.0.10.28", {"center": v(220, 346.41) * mm, "radius": 9 * mm});
            skCircle(sketch, "E4.0.10.29", {"center": v(190, 363.73) * mm, "radius": 9 * mm});
            skCircle(sketch, "E4.0.10.30", {"center": v(90, 363.73) * mm, "radius": 9 * mm});
            skCircle(sketch, "E4.0.10.31", {"center": v(230, 363.73) * mm, "radius": 9 * mm});
            skCircle(sketch, "E4.0.10.32", {"center": v(150, 363.73) * mm, "radius": 9 * mm});
            skCircle(sketch, "E4.0.10.33", {"center": v(470, 363.73) * mm, "radius": 9 * mm});
            skCircle(sketch, "E4.0.10.34", {"center": v(410, 363.73) * mm, "radius": 9 * mm});
            skCircle(sketch, "E4.0.10.35", {"center": v(50, 363.73) * mm, "radius": 9 * mm});
            skCircle(sketch, "E4.0.10.36", {"center": v(400, 346.41) * mm, "radius": 9 * mm});
            skCircle(sketch, "E4.0.10.37", {"center": v(240, 346.41) * mm, "radius": 9 * mm});
            skCircle(sketch, "E4.0.10.38", {"center": v(320, 346.41) * mm, "radius": 9 * mm});
            skCircle(sketch, "E4.0.10.39", {"center": v(370, 363.73) * mm, "radius": 9 * mm});
            skCircle(sketch, "E4.0.10.40", {"center": v(10, 363.73) * mm, "radius": 9 * mm});
            skCircle(sketch, "E4.0.10.41", {"center": v(290, 363.73) * mm, "radius": 9 * mm});
            skCircle(sketch, "E4.0.10.42", {"center": v(360, 346.41) * mm, "radius": 9 * mm});
            skCircle(sketch, "E4.0.10.43", {"center": v(460, 346.41) * mm, "radius": 9 * mm});
            skCircle(sketch, "E4.0.10.44", {"center": v(310, 363.73) * mm, "radius": 9 * mm});
            skCircle(sketch, "E4.0.10.45", {"center": v(340, 346.41) * mm, "radius": 9 * mm});
            skCircle(sketch, "E4.0.10.46", {"center": v(170, 363.73) * mm, "radius": 9 * mm});
            skCircle(sketch, "E4.0.10.47", {"center": v(20, 346.41) * mm, "radius": 9 * mm});
            skLineSegment(sketch, "E4.0.10.48", {"start": v(0, 346.41) * mm, "end": v(20, 346.41) * mm, "construction": true});
            skLineSegment(sketch, "E4.0.10.49", {"start": v(10, 363.73) * mm, "end": v(30, 363.73) * mm, "construction": true});
            skCircle(sketch, "E4.0.11.0", {"center": v(280, 381.05) * mm, "radius": 9 * mm});
            skCircle(sketch, "E4.0.11.1", {"center": v(260, 381.05) * mm, "radius": 9 * mm});
            skCircle(sketch, "E4.0.11.2", {"center": v(130, 398.37) * mm, "radius": 9 * mm});
            skCircle(sketch, "E4.0.11.3", {"center": v(60, 381.05) * mm, "radius": 9 * mm});
            skCircle(sketch, "E4.0.11.4", {"center": v(80, 381.05) * mm, "radius": 9 * mm});
            skCircle(sketch, "E4.0.11.5", {"center": v(100, 381.05) * mm, "radius": 9 * mm});
            skCircle(sketch, "E4.0.11.6", {"center": v(350, 398.37) * mm, "radius": 9 * mm});
            skCircle(sketch, "E4.0.11.7", {"center": v(0, 381.05) * mm, "radius": 9 * mm});
            skCircle(sketch, "E4.0.11.8", {"center": v(120, 381.05) * mm, "radius": 9 * mm});
            skCircle(sketch, "E4.0.11.9", {"center": v(30, 398.37) * mm, "radius": 9 * mm});
            skCircle(sketch, "E4.0.11.10", {"center": v(380, 381.05) * mm, "radius": 9 * mm});
            skCircle(sketch, "E4.0.11.11", {"center": v(140, 381.05) * mm, "radius": 9 * mm});
            skCircle(sketch, "E4.0.11.12", {"center": v(450, 398.37) * mm, "radius": 9 * mm});
            skCircle(sketch, "E4.0.11.13", {"center": v(160, 381.05) * mm, "radius": 9 * mm});
            skCircle(sketch, "E4.0.11.14", {"center": v(300, 381.05) * mm, "radius": 9 * mm});
            skCircle(sketch, "E4.0.11.15", {"center": v(40, 381.05) * mm, "radius": 9 * mm});
            skCircle(sketch, "E4.0.11.16", {"center": v(210, 398.37) * mm, "radius": 9 * mm});
            skCircle(sketch, "E4.0.11.17", {"center": v(330, 398.37) * mm, "radius": 9 * mm});
            skCircle(sketch, "E4.0.11.18", {"center": v(270, 398.37) * mm, "radius": 9 * mm});
            skCircle(sketch, "E4.0.11.19", {"center": v(440, 381.05) * mm, "radius": 9 * mm});
            skCircle(sketch, "E4.0.11.20", {"center": v(110, 398.37) * mm, "radius": 9 * mm});
            skCircle(sketch, "E4.0.11.21", {"center": v(250, 398.37) * mm, "radius": 9 * mm});
            skCircle(sketch, "E4.0.11.22", {"center": v(180, 381.05) * mm, "radius": 9 * mm});
            skCircle(sketch, "E4.0.11.23", {"center": v(430, 398.37) * mm, "radius": 9 * mm});
            skCircle(sketch, "E4.0.11.24", {"center": v(200, 381.05) * mm, "radius": 9 * mm});
            skCircle(sketch, "E4.0.11.25", {"center": v(420, 381.05) * mm, "radius": 9 * mm});
            skCircle(sketch, "E4.0.11.26", {"center": v(70, 398.37) * mm, "radius": 9 * mm});
            skCircle(sketch, "E4.0.11.27", {"center": v(390, 398.37) * mm, "radius": 9 * mm});
            skCircle(sketch, "E4.0.11.28", {"center": v(220, 381.05) * mm, "radius": 9 * mm});
            skCircle(sketch, "E4.0.11.29", {"center": v(190, 398.37) * mm, "radius": 9 * mm});
            skCircle(sketch, "E4.0.11.30", {"center": v(90, 398.37) * mm, "radius": 9 * mm});
            skCircle(sketch, "E4.0.11.31", {"center": v(230, 398.37) * mm, "radius": 9 * mm});
            skCircle(sketch, "E4.0.11.32", {"center": v(150, 398.37) * mm, "radius": 9 * mm});
            skCircle(sketch, "E4.0.11.33", {"center": v(470, 398.37) * mm, "radius": 9 * mm});
            skCircle(sketch, "E4.0.11.34", {"center": v(410, 398.37) * mm, "radius": 9 * mm});
            skCircle(sketch, "E4.0.11.35", {"center": v(50, 398.37) * mm, "radius": 9 * mm});
            skCircle(sketch, "E4.0.11.36", {"center": v(400, 381.05) * mm, "radius": 9 * mm});
            skCircle(sketch, "E4.0.11.37", {"center": v(240, 381.05) * mm, "radius": 9 * mm});
            skCircle(sketch, "E4.0.11.38", {"center": v(320, 381.05) * mm, "radius": 9 * mm});
            skCircle(sketch, "E4.0.11.39", {"center": v(370, 398.37) * mm, "radius": 9 * mm});
            skCircle(sketch, "E4.0.11.40", {"center": v(10, 398.37) * mm, "radius": 9 * mm});
            skCircle(sketch, "E4.0.11.41", {"center": v(290, 398.37) * mm, "radius": 9 * mm});
            skCircle(sketch, "E4.0.11.42", {"center": v(360, 381.05) * mm, "radius": 9 * mm});
            skCircle(sketch, "E4.0.11.43", {"center": v(460, 381.05) * mm, "radius": 9 * mm});
            skCircle(sketch, "E4.0.11.44", {"center": v(310, 398.37) * mm, "radius": 9 * mm});
            skCircle(sketch, "E4.0.11.45", {"center": v(340, 381.05) * mm, "radius": 9 * mm});
            skCircle(sketch, "E4.0.11.46", {"center": v(170, 398.37) * mm, "radius": 9 * mm});
            skCircle(sketch, "E4.0.11.47", {"center": v(20, 381.05) * mm, "radius": 9 * mm});
            skLineSegment(sketch, "E4.0.11.48", {"start": v(0, 381.05) * mm, "end": v(20, 381.05) * mm, "construction": true});
            skLineSegment(sketch, "E4.0.11.49", {"start": v(10, 398.37) * mm, "end": v(30, 398.37) * mm, "construction": true});
            skCircle(sketch, "E4.0.12.0", {"center": v(280, 415.7) * mm, "radius": 9 * mm});
            skCircle(sketch, "E4.0.12.1", {"center": v(260, 415.7) * mm, "radius": 9 * mm});
            skCircle(sketch, "E4.0.12.2", {"center": v(130, 433.01) * mm, "radius": 9 * mm});
            skCircle(sketch, "E4.0.12.3", {"center": v(60, 415.7) * mm, "radius": 9 * mm});
            skCircle(sketch, "E4.0.12.4", {"center": v(80, 415.7) * mm, "radius": 9 * mm});
            skCircle(sketch, "E4.0.12.5", {"center": v(100, 415.7) * mm, "radius": 9 * mm});
            skCircle(sketch, "E4.0.12.6", {"center": v(350, 433.01) * mm, "radius": 9 * mm});
            skCircle(sketch, "E4.0.12.7", {"center": v(0, 415.7) * mm, "radius": 9 * mm});
            skCircle(sketch, "E4.0.12.8", {"center": v(120, 415.7) * mm, "radius": 9 * mm});
            skCircle(sketch, "E4.0.12.9", {"center": v(30, 433.01) * mm, "radius": 9 * mm});
            skCircle(sketch, "E4.0.12.10", {"center": v(380, 415.7) * mm, "radius": 9 * mm});
            skCircle(sketch, "E4.0.12.11", {"center": v(140, 415.7) * mm, "radius": 9 * mm});
            skCircle(sketch, "E4.0.12.12", {"center": v(450, 433.01) * mm, "radius": 9 * mm});
            skCircle(sketch, "E4.0.12.13", {"center": v(160, 415.7) * mm, "radius": 9 * mm});
            skCircle(sketch, "E4.0.12.14", {"center": v(300, 415.7) * mm, "radius": 9 * mm});
            skCircle(sketch, "E4.0.12.15", {"center": v(40, 415.7) * mm, "radius": 9 * mm});
            skCircle(sketch, "E4.0.12.16", {"center": v(210, 433.01) * mm, "radius": 9 * mm});
            skCircle(sketch, "E4.0.12.17", {"center": v(330, 433.01) * mm, "radius": 9 * mm});
            skCircle(sketch, "E4.0.12.18", {"center": v(270, 433.01) * mm, "radius": 9 * mm});
            skCircle(sketch, "E4.0.12.19", {"center": v(440, 415.7) * mm, "radius": 9 * mm});
            skCircle(sketch, "E4.0.12.20", {"center": v(110, 433.01) * mm, "radius": 9 * mm});
            skCircle(sketch, "E4.0.12.21", {"center": v(250, 433.01) * mm, "radius": 9 * mm});
            skCircle(sketch, "E4.0.12.22", {"center": v(180, 415.7) * mm, "radius": 9 * mm});
            skCircle(sketch, "E4.0.12.23", {"center": v(430, 433.01) * mm, "radius": 9 * mm});
            skCircle(sketch, "E4.0.12.24", {"center": v(200, 415.7) * mm, "radius": 9 * mm});
            skCircle(sketch, "E4.0.12.25", {"center": v(420, 415.7) * mm, "radius": 9 * mm});
            skCircle(sketch, "E4.0.12.26", {"center": v(70, 433.01) * mm, "radius": 9 * mm});
            skCircle(sketch, "E4.0.12.27", {"center": v(390, 433.01) * mm, "radius": 9 * mm});
            skCircle(sketch, "E4.0.12.28", {"center": v(220, 415.7) * mm, "radius": 9 * mm});
            skCircle(sketch, "E4.0.12.29", {"center": v(190, 433.01) * mm, "radius": 9 * mm});
            skCircle(sketch, "E4.0.12.30", {"center": v(90, 433.01) * mm, "radius": 9 * mm});
            skCircle(sketch, "E4.0.12.31", {"center": v(230, 433.01) * mm, "radius": 9 * mm});
            skCircle(sketch, "E4.0.12.32", {"center": v(150, 433.01) * mm, "radius": 9 * mm});
            skCircle(sketch, "E4.0.12.33", {"center": v(470, 433.01) * mm, "radius": 9 * mm});
            skCircle(sketch, "E4.0.12.34", {"center": v(410, 433.01) * mm, "radius": 9 * mm});
            skCircle(sketch, "E4.0.12.35", {"center": v(50, 433.01) * mm, "radius": 9 * mm});
            skCircle(sketch, "E4.0.12.36", {"center": v(400, 415.7) * mm, "radius": 9 * mm});
            skCircle(sketch, "E4.0.12.37", {"center": v(240, 415.7) * mm, "radius": 9 * mm});
            skCircle(sketch, "E4.0.12.38", {"center": v(320, 415.7) * mm, "radius": 9 * mm});
            skCircle(sketch, "E4.0.12.39", {"center": v(370, 433.01) * mm, "radius": 9 * mm});
            skCircle(sketch, "E4.0.12.40", {"center": v(10, 433.01) * mm, "radius": 9 * mm});
            skCircle(sketch, "E4.0.12.41", {"center": v(290, 433.01) * mm, "radius": 9 * mm});
            skCircle(sketch, "E4.0.12.42", {"center": v(360, 415.7) * mm, "radius": 9 * mm});
            skCircle(sketch, "E4.0.12.43", {"center": v(460, 415.7) * mm, "radius": 9 * mm});
            skCircle(sketch, "E4.0.12.44", {"center": v(310, 433.01) * mm, "radius": 9 * mm});
            skCircle(sketch, "E4.0.12.45", {"center": v(340, 415.7) * mm, "radius": 9 * mm});
            skCircle(sketch, "E4.0.12.46", {"center": v(170, 433.01) * mm, "radius": 9 * mm});
            skCircle(sketch, "E4.0.12.47", {"center": v(20, 415.7) * mm, "radius": 9 * mm});
            skLineSegment(sketch, "E4.0.12.48", {"start": v(0, 415.7) * mm, "end": v(20, 415.7) * mm, "construction": true});
            skLineSegment(sketch, "E4.0.12.49", {"start": v(10, 433.01) * mm, "end": v(30, 433.01) * mm, "construction": true});
            skCircle(sketch, "E4.0.13.0", {"center": v(280, 450.33) * mm, "radius": 9 * mm});
            skCircle(sketch, "E4.0.13.1", {"center": v(260, 450.33) * mm, "radius": 9 * mm});
            skCircle(sketch, "E4.0.13.2", {"center": v(130, 467.65) * mm, "radius": 9 * mm});
            skCircle(sketch, "E4.0.13.3", {"center": v(60, 450.33) * mm, "radius": 9 * mm});
            skCircle(sketch, "E4.0.13.4", {"center": v(80, 450.33) * mm, "radius": 9 * mm});
            skCircle(sketch, "E4.0.13.5", {"center": v(100, 450.33) * mm, "radius": 9 * mm});
            skCircle(sketch, "E4.0.13.6", {"center": v(350, 467.65) * mm, "radius": 9 * mm});
            skCircle(sketch, "E4.0.13.7", {"center": v(0, 450.33) * mm, "radius": 9 * mm});
            skCircle(sketch, "E4.0.13.8", {"center": v(120, 450.33) * mm, "radius": 9 * mm});
            skCircle(sketch, "E4.0.13.9", {"center": v(30, 467.65) * mm, "radius": 9 * mm});
            skCircle(sketch, "E4.0.13.10", {"center": v(380, 450.33) * mm, "radius": 9 * mm});
            skCircle(sketch, "E4.0.13.11", {"center": v(140, 450.33) * mm, "radius": 9 * mm});
            skCircle(sketch, "E4.0.13.12", {"center": v(450, 467.65) * mm, "radius": 9 * mm});
            skCircle(sketch, "E4.0.13.13", {"center": v(160, 450.33) * mm, "radius": 9 * mm});
            skCircle(sketch, "E4.0.13.14", {"center": v(300, 450.33) * mm, "radius": 9 * mm});
            skCircle(sketch, "E4.0.13.15", {"center": v(40, 450.33) * mm, "radius": 9 * mm});
            skCircle(sketch, "E4.0.13.16", {"center": v(210, 467.65) * mm, "radius": 9 * mm});
            skCircle(sketch, "E4.0.13.17", {"center": v(330, 467.65) * mm, "radius": 9 * mm});
            skCircle(sketch, "E4.0.13.18", {"center": v(270, 467.65) * mm, "radius": 9 * mm});
            skCircle(sketch, "E4.0.13.19", {"center": v(440, 450.33) * mm, "radius": 9 * mm});
            skCircle(sketch, "E4.0.13.20", {"center": v(110, 467.65) * mm, "radius": 9 * mm});
            skCircle(sketch, "E4.0.13.21", {"center": v(250, 467.65) * mm, "radius": 9 * mm});
            skCircle(sketch, "E4.0.13.22", {"center": v(180, 450.33) * mm, "radius": 9 * mm});
            skCircle(sketch, "E4.0.13.23", {"center": v(430, 467.65) * mm, "radius": 9 * mm});
            skCircle(sketch, "E4.0.13.24", {"center": v(200, 450.33) * mm, "radius": 9 * mm});
            skCircle(sketch, "E4.0.13.25", {"center": v(420, 450.33) * mm, "radius": 9 * mm});
            skCircle(sketch, "E4.0.13.26", {"center": v(70, 467.65) * mm, "radius": 9 * mm});
            skCircle(sketch, "E4.0.13.27", {"center": v(390, 467.65) * mm, "radius": 9 * mm});
            skCircle(sketch, "E4.0.13.28", {"center": v(220, 450.33) * mm, "radius": 9 * mm});
            skCircle(sketch, "E4.0.13.29", {"center": v(190, 467.65) * mm, "radius": 9 * mm});
            skCircle(sketch, "E4.0.13.30", {"center": v(90, 467.65) * mm, "radius": 9 * mm});
            skCircle(sketch, "E4.0.13.31", {"center": v(230, 467.65) * mm, "radius": 9 * mm});
            skCircle(sketch, "E4.0.13.32", {"center": v(150, 467.65) * mm, "radius": 9 * mm});
            skCircle(sketch, "E4.0.13.33", {"center": v(470, 467.65) * mm, "radius": 9 * mm});
            skCircle(sketch, "E4.0.13.34", {"center": v(410, 467.65) * mm, "radius": 9 * mm});
            skCircle(sketch, "E4.0.13.35", {"center": v(50, 467.65) * mm, "radius": 9 * mm});
            skCircle(sketch, "E4.0.13.36", {"center": v(400, 450.33) * mm, "radius": 9 * mm});
            skCircle(sketch, "E4.0.13.37", {"center": v(240, 450.33) * mm, "radius": 9 * mm});
            skCircle(sketch, "E4.0.13.38", {"center": v(320, 450.33) * mm, "radius": 9 * mm});
            skCircle(sketch, "E4.0.13.39", {"center": v(370, 467.65) * mm, "radius": 9 * mm});
            skCircle(sketch, "E4.0.13.40", {"center": v(10, 467.65) * mm, "radius": 9 * mm});
            skCircle(sketch, "E4.0.13.41", {"center": v(290, 467.65) * mm, "radius": 9 * mm});
            skCircle(sketch, "E4.0.13.42", {"center": v(360, 450.33) * mm, "radius": 9 * mm});
            skCircle(sketch, "E4.0.13.43", {"center": v(460, 450.33) * mm, "radius": 9 * mm});
            skCircle(sketch, "E4.0.13.44", {"center": v(310, 467.65) * mm, "radius": 9 * mm});
            skCircle(sketch, "E4.0.13.45", {"center": v(340, 450.33) * mm, "radius": 9 * mm});
            skCircle(sketch, "E4.0.13.46", {"center": v(170, 467.65) * mm, "radius": 9 * mm});
            skCircle(sketch, "E4.0.13.47", {"center": v(20, 450.33) * mm, "radius": 9 * mm});
            skLineSegment(sketch, "E4.0.13.48", {"start": v(0, 450.33) * mm, "end": v(20, 450.33) * mm, "construction": true});
            skLineSegment(sketch, "E4.0.13.49", {"start": v(10, 467.65) * mm, "end": v(30, 467.65) * mm, "construction": true});
            skCircle(sketch, "E4.0.14.0", {"center": v(280, 484.97) * mm, "radius": 9 * mm});
            skCircle(sketch, "E4.0.14.1", {"center": v(260, 484.97) * mm, "radius": 9 * mm});
            skCircle(sketch, "E4.0.14.2", {"center": v(130, 502.3) * mm, "radius": 9 * mm});
            skCircle(sketch, "E4.0.14.3", {"center": v(60, 484.97) * mm, "radius": 9 * mm});
            skCircle(sketch, "E4.0.14.4", {"center": v(80, 484.97) * mm, "radius": 9 * mm});
            skCircle(sketch, "E4.0.14.5", {"center": v(100, 484.97) * mm, "radius": 9 * mm});
            skCircle(sketch, "E4.0.14.6", {"center": v(350, 502.3) * mm, "radius": 9 * mm});
            skCircle(sketch, "E4.0.14.7", {"center": v(0, 484.97) * mm, "radius": 9 * mm});
            skCircle(sketch, "E4.0.14.8", {"center": v(120, 484.97) * mm, "radius": 9 * mm});
            skCircle(sketch, "E4.0.14.9", {"center": v(30, 502.3) * mm, "radius": 9 * mm});
            skCircle(sketch, "E4.0.14.10", {"center": v(380, 484.97) * mm, "radius": 9 * mm});
            skCircle(sketch, "E4.0.14.11", {"center": v(140, 484.97) * mm, "radius": 9 * mm});
            skCircle(sketch, "E4.0.14.12", {"center": v(450, 502.3) * mm, "radius": 9 * mm});
            skCircle(sketch, "E4.0.14.13", {"center": v(160, 484.97) * mm, "radius": 9 * mm});
            skCircle(sketch, "E4.0.14.14", {"center": v(300, 484.97) * mm, "radius": 9 * mm});
            skCircle(sketch, "E4.0.14.15", {"center": v(40, 484.97) * mm, "radius": 9 * mm});
            skCircle(sketch, "E4.0.14.16", {"center": v(210, 502.3) * mm, "radius": 9 * mm});
            skCircle(sketch, "E4.0.14.17", {"center": v(330, 502.3) * mm, "radius": 9 * mm});
            skCircle(sketch, "E4.0.14.18", {"center": v(270, 502.3) * mm, "radius": 9 * mm});
            skCircle(sketch, "E4.0.14.19", {"center": v(440, 484.97) * mm, "radius": 9 * mm});
            skCircle(sketch, "E4.0.14.20", {"center": v(110, 502.3) * mm, "radius": 9 * mm});
            skCircle(sketch, "E4.0.14.21", {"center": v(250, 502.3) * mm, "radius": 9 * mm});
            skCircle(sketch, "E4.0.14.22", {"center": v(180, 484.97) * mm, "radius": 9 * mm});
            skCircle(sketch, "E4.0.14.23", {"center": v(430, 502.3) * mm, "radius": 9 * mm});
            skCircle(sketch, "E4.0.14.24", {"center": v(200, 484.97) * mm, "radius": 9 * mm});
            skCircle(sketch, "E4.0.14.25", {"center": v(420, 484.97) * mm, "radius": 9 * mm});
            skCircle(sketch, "E4.0.14.26", {"center": v(70, 502.3) * mm, "radius": 9 * mm});
            skCircle(sketch, "E4.0.14.27", {"center": v(390, 502.3) * mm, "radius": 9 * mm});
            skCircle(sketch, "E4.0.14.28", {"center": v(220, 484.97) * mm, "radius": 9 * mm});
            skCircle(sketch, "E4.0.14.29", {"center": v(190, 502.3) * mm, "radius": 9 * mm});
            skCircle(sketch, "E4.0.14.30", {"center": v(90, 502.3) * mm, "radius": 9 * mm});
            skCircle(sketch, "E4.0.14.31", {"center": v(230, 502.3) * mm, "radius": 9 * mm});
            skCircle(sketch, "E4.0.14.32", {"center": v(150, 502.3) * mm, "radius": 9 * mm});
            skCircle(sketch, "E4.0.14.33", {"center": v(470, 502.3) * mm, "radius": 9 * mm});
            skCircle(sketch, "E4.0.14.34", {"center": v(410, 502.3) * mm, "radius": 9 * mm});
            skCircle(sketch, "E4.0.14.35", {"center": v(50, 502.3) * mm, "radius": 9 * mm});
            skCircle(sketch, "E4.0.14.36", {"center": v(400, 484.97) * mm, "radius": 9 * mm});
            skCircle(sketch, "E4.0.14.37", {"center": v(240, 484.97) * mm, "radius": 9 * mm});
            skCircle(sketch, "E4.0.14.38", {"center": v(320, 484.97) * mm, "radius": 9 * mm});
            skCircle(sketch, "E4.0.14.39", {"center": v(370, 502.3) * mm, "radius": 9 * mm});
            skCircle(sketch, "E4.0.14.40", {"center": v(10, 502.3) * mm, "radius": 9 * mm});
            skCircle(sketch, "E4.0.14.41", {"center": v(290, 502.3) * mm, "radius": 9 * mm});
            skCircle(sketch, "E4.0.14.42", {"center": v(360, 484.97) * mm, "radius": 9 * mm});
            skCircle(sketch, "E4.0.14.43", {"center": v(460, 484.97) * mm, "radius": 9 * mm});
            skCircle(sketch, "E4.0.14.44", {"center": v(310, 502.3) * mm, "radius": 9 * mm});
            skCircle(sketch, "E4.0.14.45", {"center": v(340, 484.97) * mm, "radius": 9 * mm});
            skCircle(sketch, "E4.0.14.46", {"center": v(170, 502.3) * mm, "radius": 9 * mm});
            skCircle(sketch, "E4.0.14.47", {"center": v(20, 484.97) * mm, "radius": 9 * mm});
            skLineSegment(sketch, "E4.0.14.48", {"start": v(0, 484.97) * mm, "end": v(20, 484.97) * mm, "construction": true});
            skLineSegment(sketch, "E4.0.14.49", {"start": v(10, 502.3) * mm, "end": v(30, 502.3) * mm, "construction": true});
            skLineSegment(sketch, "E4.direction1", {"start": v(0, 0) * mm, "end": v(25, 0) * mm, "construction": true});
            skLineSegment(sketch, "E4.direction2", {"start": v(0, 0) * mm, "end": v(0, 34.64) * mm, "construction": true});
            skLineSegment(sketch, "E5.bottom", {"start": v(470, 502.3) * mm, "end": v(0, 502.3) * mm, "construction": true});
            skLineSegment(sketch, "E5.top", {"start": v(470, 0) * mm, "end": v(0, 0) * mm, "construction": true});
            skLineSegment(sketch, "E5.left", {"start": v(470, 502.3) * mm, "end": v(470, 0) * mm, "construction": true});
            skLineSegment(sketch, "E5.right", {"start": v(0, 502.3) * mm, "end": v(0, 0) * mm, "construction": true});
            skLineSegment(sketch, "E6", {"start": v(0, 0) * mm, "end": v(470, 502.3) * mm, "construction": true});
            skLineSegment(sketch, "E7", {"start": v(0, 502.3) * mm, "end": v(470, 0) * mm, "construction": true});
            skPoint(sketch, "E8", {"position": v(235, 251.15) * mm});
            skSolve(sketch);
        }
        {
            var Q0;
            Q0=qCreatedBy(makeId("Top.planeOp"),FACE);
            var sketch = newSketch(context, id + "F1", { "sketchPlane" : qUnion([Q0])});
            skLineSegment(sketch, "E9.bottom", {"start": v(-20, 521.15) * mm, "end": v(490, 521.15) * mm});
            skLineSegment(sketch, "E9.top", {"start": v(-20, -18.85) * mm, "end": v(490, -18.85) * mm});
            skLineSegment(sketch, "E9.left", {"start": v(-20, 521.15) * mm, "end": v(-20, -18.85) * mm});
            skLineSegment(sketch, "E9.right", {"start": v(490, 521.15) * mm, "end": v(490, -18.85) * mm});
            skLineSegment(sketch, "E10", {"start": v(-20, 521.15) * mm, "end": v(490, -18.85) * mm, "construction": true});
            skLineSegment(sketch, "E11", {"start": v(490, 521.15) * mm, "end": v(-20, -18.85) * mm, "construction": true});
            skPoint(sketch, "E12", {"position": v(235, 251.15) * mm});
            skSolve(sketch);
        }
        {
            var Q0;
            Q0 = qSketchRegion(id + "F1", true);
            extrude(context, id + "F2", {"entities" : qUnion([Q0]), "depth" : 10 * mm});
        }
        {
            var Q0;
            Q0 = qSketchRegion(id + "F0", true);
            extrude(context, id + "F3", {"entities" : qUnion([Q0]), "operationType" : NewBodyOperationType.REMOVE, "depth" : 8 * mm});
        }
        {
            var Q0;
            Q0=makeQuery(id+"F2.opExtrude","CAP_FACE",FACE,{"disambiguationData":[OSD([sQuery(id+"F1.wireOp",EDGE,"E9.bottom"),sQuery(id+"F1.wireOp",EDGE,"E9.top"),sQuery(id+"F1.wireOp",EDGE,"E9.left"),sQuery(id+"F1.wireOp",EDGE,"E9.right")])],"isStart":false});
            var sketch = newSketch(context, id + "F4", { "sketchPlane" : qUnion([Q0])});
            skLineSegment(sketch, "E13.bottom", {"start": v(490, 506.8) * mm, "end": v(-20, 506.8) * mm});
            skLineSegment(sketch, "E13.top", {"start": v(490, 497.8) * mm, "end": v(-20, 497.8) * mm});
            skLineSegment(sketch, "E13.left", {"start": v(490, 506.8) * mm, "end": v(490, 497.8) * mm});
            skLineSegment(sketch, "E13.right", {"start": v(-20, 506.8) * mm, "end": v(-20, 497.8) * mm});
            skLineSegment(sketch, "E14.0.1.0", {"start": v(490, 472.15) * mm, "end": v(-20, 472.15) * mm});
            skLineSegment(sketch, "E14.0.1.1", {"start": v(490, 463.15) * mm, "end": v(-20, 463.15) * mm});
            skLineSegment(sketch, "E14.0.1.2", {"start": v(490, 472.15) * mm, "end": v(490, 463.15) * mm});
            skLineSegment(sketch, "E14.0.1.3", {"start": v(-20, 472.15) * mm, "end": v(-20, 463.15) * mm});
            skLineSegment(sketch, "E14.0.2.0", {"start": v(490, 437.51) * mm, "end": v(-20, 437.51) * mm});
            skLineSegment(sketch, "E14.0.2.1", {"start": v(490, 428.51) * mm, "end": v(-20, 428.51) * mm});
            skLineSegment(sketch, "E14.0.2.2", {"start": v(490, 437.51) * mm, "end": v(490, 428.51) * mm});
            skLineSegment(sketch, "E14.0.2.3", {"start": v(-20, 437.51) * mm, "end": v(-20, 428.51) * mm});
            skLineSegment(sketch, "E14.0.3.0", {"start": v(490, 402.87) * mm, "end": v(-20, 402.87) * mm});
            skLineSegment(sketch, "E14.0.3.1", {"start": v(490, 393.87) * mm, "end": v(-20, 393.87) * mm});
            skLineSegment(sketch, "E14.0.3.2", {"start": v(490, 402.87) * mm, "end": v(490, 393.87) * mm});
            skLineSegment(sketch, "E14.0.3.3", {"start": v(-20, 402.87) * mm, "end": v(-20, 393.87) * mm});
            skLineSegment(sketch, "E14.0.4.0", {"start": v(490, 368.23) * mm, "end": v(-20, 368.23) * mm});
            skLineSegment(sketch, "E14.0.4.1", {"start": v(490, 359.23) * mm, "end": v(-20, 359.23) * mm});
            skLineSegment(sketch, "E14.0.4.2", {"start": v(490, 368.23) * mm, "end": v(490, 359.23) * mm});
            skLineSegment(sketch, "E14.0.4.3", {"start": v(-20, 368.23) * mm, "end": v(-20, 359.23) * mm});
            skLineSegment(sketch, "E14.0.5.0", {"start": v(490, 333.59) * mm, "end": v(-20, 333.59) * mm});
            skLineSegment(sketch, "E14.0.5.1", {"start": v(490, 324.59) * mm, "end": v(-20, 324.59) * mm});
            skLineSegment(sketch, "E14.0.5.2", {"start": v(490, 333.59) * mm, "end": v(490, 324.59) * mm});
            skLineSegment(sketch, "E14.0.5.3", {"start": v(-20, 333.59) * mm, "end": v(-20, 324.59) * mm});
            skLineSegment(sketch, "E14.0.6.0", {"start": v(490, 298.95) * mm, "end": v(-20, 298.95) * mm});
            skLineSegment(sketch, "E14.0.6.1", {"start": v(490, 289.95) * mm, "end": v(-20, 289.95) * mm});
            skLineSegment(sketch, "E14.0.6.2", {"start": v(490, 298.95) * mm, "end": v(490, 289.95) * mm});
            skLineSegment(sketch, "E14.0.6.3", {"start": v(-20, 298.95) * mm, "end": v(-20, 289.95) * mm});
            skLineSegment(sketch, "E14.0.7.0", {"start": v(490, 264.3) * mm, "end": v(-20, 264.3) * mm});
            skLineSegment(sketch, "E14.0.7.1", {"start": v(490, 255.3) * mm, "end": v(-20, 255.3) * mm});
            skLineSegment(sketch, "E14.0.7.2", {"start": v(490, 264.3) * mm, "end": v(490, 255.3) * mm});
            skLineSegment(sketch, "E14.0.7.3", {"start": v(-20, 264.3) * mm, "end": v(-20, 255.3) * mm});
            skLineSegment(sketch, "E14.0.8.0", {"start": v(490, 229.67) * mm, "end": v(-20, 229.67) * mm});
            skLineSegment(sketch, "E14.0.8.1", {"start": v(490, 220.67) * mm, "end": v(-20, 220.67) * mm});
            skLineSegment(sketch, "E14.0.8.2", {"start": v(490, 229.67) * mm, "end": v(490, 220.67) * mm});
            skLineSegment(sketch, "E14.0.8.3", {"start": v(-20, 229.67) * mm, "end": v(-20, 220.67) * mm});
            skLineSegment(sketch, "E14.0.9.0", {"start": v(490, 195.03) * mm, "end": v(-20, 195.03) * mm});
            skLineSegment(sketch, "E14.0.9.1", {"start": v(490, 186.03) * mm, "end": v(-20, 186.03) * mm});
            skLineSegment(sketch, "E14.0.9.2", {"start": v(490, 195.03) * mm, "end": v(490, 186.03) * mm});
            skLineSegment(sketch, "E14.0.9.3", {"start": v(-20, 195.03) * mm, "end": v(-20, 186.03) * mm});
            skLineSegment(sketch, "E14.0.10.0", {"start": v(490, 160.38) * mm, "end": v(-20, 160.38) * mm});
            skLineSegment(sketch, "E14.0.10.1", {"start": v(490, 151.38) * mm, "end": v(-20, 151.38) * mm});
            skLineSegment(sketch, "E14.0.10.2", {"start": v(490, 160.38) * mm, "end": v(490, 151.38) * mm});
            skLineSegment(sketch, "E14.0.10.3", {"start": v(-20, 160.38) * mm, "end": v(-20, 151.38) * mm});
            skLineSegment(sketch, "E14.0.11.0", {"start": v(490, 125.74) * mm, "end": v(-20, 125.74) * mm});
            skLineSegment(sketch, "E14.0.11.1", {"start": v(490, 116.74) * mm, "end": v(-20, 116.74) * mm});
            skLineSegment(sketch, "E14.0.11.2", {"start": v(490, 125.74) * mm, "end": v(490, 116.74) * mm});
            skLineSegment(sketch, "E14.0.11.3", {"start": v(-20, 125.74) * mm, "end": v(-20, 116.74) * mm});
            skLineSegment(sketch, "E14.0.12.0", {"start": v(490, 91.1) * mm, "end": v(-20, 91.1) * mm});
            skLineSegment(sketch, "E14.0.12.1", {"start": v(490, 82.1) * mm, "end": v(-20, 82.1) * mm});
            skLineSegment(sketch, "E14.0.12.2", {"start": v(490, 91.1) * mm, "end": v(490, 82.1) * mm});
            skLineSegment(sketch, "E14.0.12.3", {"start": v(-20, 91.1) * mm, "end": v(-20, 82.1) * mm});
            skLineSegment(sketch, "E14.0.13.0", {"start": v(490, 56.46) * mm, "end": v(-20, 56.46) * mm});
            skLineSegment(sketch, "E14.0.13.1", {"start": v(490, 47.46) * mm, "end": v(-20, 47.46) * mm});
            skLineSegment(sketch, "E14.0.13.2", {"start": v(490, 56.46) * mm, "end": v(490, 47.46) * mm});
            skLineSegment(sketch, "E14.0.13.3", {"start": v(-20, 56.46) * mm, "end": v(-20, 47.46) * mm});
            skLineSegment(sketch, "E14.0.14.0", {"start": v(490, 21.82) * mm, "end": v(-20, 21.82) * mm});
            skLineSegment(sketch, "E14.0.14.1", {"start": v(490, 12.82) * mm, "end": v(-20, 12.82) * mm});
            skLineSegment(sketch, "E14.0.14.2", {"start": v(490, 21.82) * mm, "end": v(490, 12.82) * mm});
            skLineSegment(sketch, "E14.0.14.3", {"start": v(-20, 21.82) * mm, "end": v(-20, 12.82) * mm});
            skLineSegment(sketch, "E14.direction1", {"start": v(-20, 497.8) * mm, "end": v(5, 497.8) * mm, "construction": true});
            skLineSegment(sketch, "E14.direction2", {"start": v(-20, 497.8) * mm, "end": v(-20, 463.15) * mm, "construction": true});
            skSolve(sketch);
        }
        {
            var Q0;
            Q0 = qSketchRegion(id + "F4", true);
            extrude(context, id + "F5", {"entities" : qUnion([Q0]), "operationType" : NewBodyOperationType.REMOVE, "oppositeDirection" : true, "depth" : 2 * mm});
        }
        {
            var Q0;
            {var subQ0=sQuery(id+"F1.wireOp",EDGE,"E9.left");var subQ1=sQuery(id+"F1.wireOp",EDGE,"E9.right");Q0=makeQuery(id+"F5.boolean.opBoolean","SPLIT",FACE,{"disambiguationData":[TD([makeQuery(id+"F5.opExtrude","SWEPT_FACE",FACE,{"disambiguationData":[OSD([sQuery(id+"F4.wireOp",EDGE,"E13.top")])]})])],"derivedFrom":makeQuery(id+"F2.opExtrude","CAP_FACE",FACE,{"disambiguationData":[OSD([sQuery(id+"F1.wireOp",EDGE,"E9.bottom"),sQuery(id+"F1.wireOp",EDGE,"E9.top"),subQ0,subQ1])],"isStart":false})});}
            var sketch = newSketch(context, id + "F6", { "sketchPlane" : qUnion([Q0])});
            skLineSegment(sketch, "E15.bottom", {"start": v(-2.5, 479.97) * mm, "end": v(2.5, 479.97) * mm});
            skLineSegment(sketch, "E15.top", {"start": v(-4.5, 497.8) * mm, "end": v(4.5, 497.8) * mm});
            skLineSegment(sketch, "E15.left", {"start": v(-4.5, 481.97) * mm, "end": v(-4.5, 497.8) * mm});
            skLineSegment(sketch, "E15.right", {"start": v(4.5, 481.97) * mm, "end": v(4.5, 497.8) * mm});
            skPoint(sketch, "E16.visualSharp", {"position": v(-4.5, 479.97) * mm});
            skArc(sketch, "E16.filletArc", {"start": v(-4.5, 481.97) * mm, "mid": v(-3.91, 480.56) * mm, "end": v(-2.5, 479.97) * mm});
            skPoint(sketch, "E17.visualSharp", {"position": v(4.5, 479.97) * mm});
            skArc(sketch, "E17.filletArc", {"start": v(2.5, 479.97) * mm, "mid": v(3.91, 480.56) * mm, "end": v(4.5, 481.97) * mm});
            skLineSegment(sketch, "E18.0.1.0", {"start": v(-4.5, 447.33) * mm, "end": v(-4.5, 463.15) * mm});
            skLineSegment(sketch, "E18.0.1.1", {"start": v(4.5, 447.33) * mm, "end": v(4.5, 463.15) * mm});
            skPoint(sketch, "E18.0.1.2", {"position": v(4.5, 445.33) * mm});
            skPoint(sketch, "E18.0.1.3", {"position": v(-4.5, 445.33) * mm});
            skLineSegment(sketch, "E18.0.1.4", {"start": v(-4.5, 463.15) * mm, "end": v(4.5, 463.15) * mm});
            skArc(sketch, "E18.0.1.5", {"start": v(-4.5, 447.33) * mm, "mid": v(-3.91, 445.92) * mm, "end": v(-2.5, 445.33) * mm});
            skLineSegment(sketch, "E18.0.1.6", {"start": v(-2.5, 445.33) * mm, "end": v(2.5, 445.33) * mm});
            skArc(sketch, "E18.0.1.7", {"start": v(2.5, 445.33) * mm, "mid": v(3.91, 445.92) * mm, "end": v(4.5, 447.33) * mm});
            skLineSegment(sketch, "E18.0.2.0", {"start": v(-4.5, 412.7) * mm, "end": v(-4.5, 428.51) * mm});
            skLineSegment(sketch, "E18.0.2.1", {"start": v(4.5, 412.7) * mm, "end": v(4.5, 428.51) * mm});
            skPoint(sketch, "E18.0.2.2", {"position": v(4.5, 410.7) * mm});
            skPoint(sketch, "E18.0.2.3", {"position": v(-4.5, 410.7) * mm});
            skLineSegment(sketch, "E18.0.2.4", {"start": v(-4.5, 428.51) * mm, "end": v(4.5, 428.51) * mm});
            skArc(sketch, "E18.0.2.5", {"start": v(-4.5, 412.7) * mm, "mid": v(-3.91, 411.28) * mm, "end": v(-2.5, 410.7) * mm});
            skLineSegment(sketch, "E18.0.2.6", {"start": v(-2.5, 410.7) * mm, "end": v(2.5, 410.7) * mm});
            skArc(sketch, "E18.0.2.7", {"start": v(2.5, 410.7) * mm, "mid": v(3.91, 411.28) * mm, "end": v(4.5, 412.7) * mm});
            skLineSegment(sketch, "E18.0.3.0", {"start": v(-4.5, 378.05) * mm, "end": v(-4.5, 393.87) * mm});
            skLineSegment(sketch, "E18.0.3.1", {"start": v(4.5, 378.05) * mm, "end": v(4.5, 393.87) * mm});
            skPoint(sketch, "E18.0.3.2", {"position": v(4.5, 376.05) * mm});
            skPoint(sketch, "E18.0.3.3", {"position": v(-4.5, 376.05) * mm});
            skLineSegment(sketch, "E18.0.3.4", {"start": v(-4.5, 393.87) * mm, "end": v(4.5, 393.87) * mm});
            skArc(sketch, "E18.0.3.5", {"start": v(-4.5, 378.05) * mm, "mid": v(-3.91, 376.64) * mm, "end": v(-2.5, 376.05) * mm});
            skLineSegment(sketch, "E18.0.3.6", {"start": v(-2.5, 376.05) * mm, "end": v(2.5, 376.05) * mm});
            skArc(sketch, "E18.0.3.7", {"start": v(2.5, 376.05) * mm, "mid": v(3.91, 376.64) * mm, "end": v(4.5, 378.05) * mm});
            skLineSegment(sketch, "E18.0.4.0", {"start": v(-4.5, 343.41) * mm, "end": v(-4.5, 359.23) * mm});
            skLineSegment(sketch, "E18.0.4.1", {"start": v(4.5, 343.41) * mm, "end": v(4.5, 359.23) * mm});
            skPoint(sketch, "E18.0.4.2", {"position": v(4.5, 341.41) * mm});
            skPoint(sketch, "E18.0.4.3", {"position": v(-4.5, 341.41) * mm});
            skLineSegment(sketch, "E18.0.4.4", {"start": v(-4.5, 359.23) * mm, "end": v(4.5, 359.23) * mm});
            skArc(sketch, "E18.0.4.5", {"start": v(-4.5, 343.41) * mm, "mid": v(-3.91, 342) * mm, "end": v(-2.5, 341.41) * mm});
            skLineSegment(sketch, "E18.0.4.6", {"start": v(-2.5, 341.41) * mm, "end": v(2.5, 341.41) * mm});
            skArc(sketch, "E18.0.4.7", {"start": v(2.5, 341.41) * mm, "mid": v(3.91, 342) * mm, "end": v(4.5, 343.41) * mm});
            skLineSegment(sketch, "E18.0.5.0", {"start": v(-4.5, 308.77) * mm, "end": v(-4.5, 324.59) * mm});
            skLineSegment(sketch, "E18.0.5.1", {"start": v(4.5, 308.77) * mm, "end": v(4.5, 324.59) * mm});
            skPoint(sketch, "E18.0.5.2", {"position": v(4.5, 306.77) * mm});
            skPoint(sketch, "E18.0.5.3", {"position": v(-4.5, 306.77) * mm});
            skLineSegment(sketch, "E18.0.5.4", {"start": v(-4.5, 324.59) * mm, "end": v(4.5, 324.59) * mm});
            skArc(sketch, "E18.0.5.5", {"start": v(-4.5, 308.77) * mm, "mid": v(-3.91, 307.35) * mm, "end": v(-2.5, 306.77) * mm});
            skLineSegment(sketch, "E18.0.5.6", {"start": v(-2.5, 306.77) * mm, "end": v(2.5, 306.77) * mm});
            skArc(sketch, "E18.0.5.7", {"start": v(2.5, 306.77) * mm, "mid": v(3.91, 307.35) * mm, "end": v(4.5, 308.77) * mm});
            skLineSegment(sketch, "E18.0.6.0", {"start": v(-4.5, 274.13) * mm, "end": v(-4.5, 289.95) * mm});
            skLineSegment(sketch, "E18.0.6.1", {"start": v(4.5, 274.13) * mm, "end": v(4.5, 289.95) * mm});
            skPoint(sketch, "E18.0.6.2", {"position": v(4.5, 272.13) * mm});
            skPoint(sketch, "E18.0.6.3", {"position": v(-4.5, 272.13) * mm});
            skLineSegment(sketch, "E18.0.6.4", {"start": v(-4.5, 289.95) * mm, "end": v(4.5, 289.95) * mm});
            skArc(sketch, "E18.0.6.5", {"start": v(-4.5, 274.13) * mm, "mid": v(-3.91, 272.71) * mm, "end": v(-2.5, 272.13) * mm});
            skLineSegment(sketch, "E18.0.6.6", {"start": v(-2.5, 272.13) * mm, "end": v(2.5, 272.13) * mm});
            skArc(sketch, "E18.0.6.7", {"start": v(2.5, 272.13) * mm, "mid": v(3.91, 272.71) * mm, "end": v(4.5, 274.13) * mm});
            skLineSegment(sketch, "E18.0.7.0", {"start": v(-4.5, 239.49) * mm, "end": v(-4.5, 255.3) * mm});
            skLineSegment(sketch, "E18.0.7.1", {"start": v(4.5, 239.49) * mm, "end": v(4.5, 255.3) * mm});
            skPoint(sketch, "E18.0.7.2", {"position": v(4.5, 237.49) * mm});
            skPoint(sketch, "E18.0.7.3", {"position": v(-4.5, 237.49) * mm});
            skLineSegment(sketch, "E18.0.7.4", {"start": v(-4.5, 255.3) * mm, "end": v(4.5, 255.3) * mm});
            skArc(sketch, "E18.0.7.5", {"start": v(-4.5, 239.49) * mm, "mid": v(-3.91, 238.07) * mm, "end": v(-2.5, 237.49) * mm});
            skLineSegment(sketch, "E18.0.7.6", {"start": v(-2.5, 237.49) * mm, "end": v(2.5, 237.49) * mm});
            skArc(sketch, "E18.0.7.7", {"start": v(2.5, 237.49) * mm, "mid": v(3.91, 238.07) * mm, "end": v(4.5, 239.49) * mm});
            skLineSegment(sketch, "E18.0.8.0", {"start": v(-4.5, 204.85) * mm, "end": v(-4.5, 220.67) * mm});
            skLineSegment(sketch, "E18.0.8.1", {"start": v(4.5, 204.85) * mm, "end": v(4.5, 220.67) * mm});
            skPoint(sketch, "E18.0.8.2", {"position": v(4.5, 202.85) * mm});
            skPoint(sketch, "E18.0.8.3", {"position": v(-4.5, 202.85) * mm});
            skLineSegment(sketch, "E18.0.8.4", {"start": v(-4.5, 220.67) * mm, "end": v(4.5, 220.67) * mm});
            skArc(sketch, "E18.0.8.5", {"start": v(-4.5, 204.85) * mm, "mid": v(-3.91, 203.43) * mm, "end": v(-2.5, 202.85) * mm});
            skLineSegment(sketch, "E18.0.8.6", {"start": v(-2.5, 202.85) * mm, "end": v(2.5, 202.85) * mm});
            skArc(sketch, "E18.0.8.7", {"start": v(2.5, 202.85) * mm, "mid": v(3.91, 203.43) * mm, "end": v(4.5, 204.85) * mm});
            skLineSegment(sketch, "E18.0.9.0", {"start": v(-4.5, 170.2) * mm, "end": v(-4.5, 186.03) * mm});
            skLineSegment(sketch, "E18.0.9.1", {"start": v(4.5, 170.2) * mm, "end": v(4.5, 186.03) * mm});
            skPoint(sketch, "E18.0.9.2", {"position": v(4.5, 168.2) * mm});
            skPoint(sketch, "E18.0.9.3", {"position": v(-4.5, 168.2) * mm});
            skLineSegment(sketch, "E18.0.9.4", {"start": v(-4.5, 186.03) * mm, "end": v(4.5, 186.03) * mm});
            skArc(sketch, "E18.0.9.5", {"start": v(-4.5, 170.2) * mm, "mid": v(-3.91, 168.8) * mm, "end": v(-2.5, 168.2) * mm});
            skLineSegment(sketch, "E18.0.9.6", {"start": v(-2.5, 168.2) * mm, "end": v(2.5, 168.2) * mm});
            skArc(sketch, "E18.0.9.7", {"start": v(2.5, 168.2) * mm, "mid": v(3.91, 168.8) * mm, "end": v(4.5, 170.2) * mm});
            skLineSegment(sketch, "E18.0.10.0", {"start": v(-4.5, 135.56) * mm, "end": v(-4.5, 151.38) * mm});
            skLineSegment(sketch, "E18.0.10.1", {"start": v(4.5, 135.56) * mm, "end": v(4.5, 151.38) * mm});
            skPoint(sketch, "E18.0.10.2", {"position": v(4.5, 133.56) * mm});
            skPoint(sketch, "E18.0.10.3", {"position": v(-4.5, 133.56) * mm});
            skLineSegment(sketch, "E18.0.10.4", {"start": v(-4.5, 151.38) * mm, "end": v(4.5, 151.38) * mm});
            skArc(sketch, "E18.0.10.5", {"start": v(-4.5, 135.56) * mm, "mid": v(-3.91, 134.15) * mm, "end": v(-2.5, 133.56) * mm});
            skLineSegment(sketch, "E18.0.10.6", {"start": v(-2.5, 133.56) * mm, "end": v(2.5, 133.56) * mm});
            skArc(sketch, "E18.0.10.7", {"start": v(2.5, 133.56) * mm, "mid": v(3.91, 134.15) * mm, "end": v(4.5, 135.56) * mm});
            skLineSegment(sketch, "E18.0.11.0", {"start": v(-4.5, 100.92) * mm, "end": v(-4.5, 116.74) * mm});
            skLineSegment(sketch, "E18.0.11.1", {"start": v(4.5, 100.92) * mm, "end": v(4.5, 116.74) * mm});
            skPoint(sketch, "E18.0.11.2", {"position": v(4.5, 98.92) * mm});
            skPoint(sketch, "E18.0.11.3", {"position": v(-4.5, 98.92) * mm});
            skLineSegment(sketch, "E18.0.11.4", {"start": v(-4.5, 116.74) * mm, "end": v(4.5, 116.74) * mm});
            skArc(sketch, "E18.0.11.5", {"start": v(-4.5, 100.92) * mm, "mid": v(-3.91, 99.5) * mm, "end": v(-2.5, 98.92) * mm});
            skLineSegment(sketch, "E18.0.11.6", {"start": v(-2.5, 98.92) * mm, "end": v(2.5, 98.92) * mm});
            skArc(sketch, "E18.0.11.7", {"start": v(2.5, 98.92) * mm, "mid": v(3.91, 99.5) * mm, "end": v(4.5, 100.92) * mm});
            skLineSegment(sketch, "E18.0.12.0", {"start": v(-4.5, 66.28) * mm, "end": v(-4.5, 82.1) * mm});
            skLineSegment(sketch, "E18.0.12.1", {"start": v(4.5, 66.28) * mm, "end": v(4.5, 82.1) * mm});
            skPoint(sketch, "E18.0.12.2", {"position": v(4.5, 64.28) * mm});
            skPoint(sketch, "E18.0.12.3", {"position": v(-4.5, 64.28) * mm});
            skLineSegment(sketch, "E18.0.12.4", {"start": v(-4.5, 82.1) * mm, "end": v(4.5, 82.1) * mm});
            skArc(sketch, "E18.0.12.5", {"start": v(-4.5, 66.28) * mm, "mid": v(-3.91, 64.87) * mm, "end": v(-2.5, 64.28) * mm});
            skLineSegment(sketch, "E18.0.12.6", {"start": v(-2.5, 64.28) * mm, "end": v(2.5, 64.28) * mm});
            skArc(sketch, "E18.0.12.7", {"start": v(2.5, 64.28) * mm, "mid": v(3.91, 64.87) * mm, "end": v(4.5, 66.28) * mm});
            skLineSegment(sketch, "E18.0.13.0", {"start": v(-4.5, 31.64) * mm, "end": v(-4.5, 47.46) * mm});
            skLineSegment(sketch, "E18.0.13.1", {"start": v(4.5, 31.64) * mm, "end": v(4.5, 47.46) * mm});
            skPoint(sketch, "E18.0.13.2", {"position": v(4.5, 29.64) * mm});
            skPoint(sketch, "E18.0.13.3", {"position": v(-4.5, 29.64) * mm});
            skLineSegment(sketch, "E18.0.13.4", {"start": v(-4.5, 47.46) * mm, "end": v(4.5, 47.46) * mm});
            skArc(sketch, "E18.0.13.5", {"start": v(-4.5, 31.64) * mm, "mid": v(-3.91, 30.23) * mm, "end": v(-2.5, 29.64) * mm});
            skLineSegment(sketch, "E18.0.13.6", {"start": v(-2.5, 29.64) * mm, "end": v(2.5, 29.64) * mm});
            skArc(sketch, "E18.0.13.7", {"start": v(2.5, 29.64) * mm, "mid": v(3.91, 30.23) * mm, "end": v(4.5, 31.64) * mm});
            skLineSegment(sketch, "E18.0.14.0", {"start": v(-4.5, -3) * mm, "end": v(-4.5, 12.82) * mm});
            skLineSegment(sketch, "E18.0.14.1", {"start": v(4.5, -3) * mm, "end": v(4.5, 12.82) * mm});
            skPoint(sketch, "E18.0.14.2", {"position": v(4.5, -5) * mm});
            skPoint(sketch, "E18.0.14.3", {"position": v(-4.5, -5) * mm});
            skLineSegment(sketch, "E18.0.14.4", {"start": v(-4.5, 12.82) * mm, "end": v(4.5, 12.82) * mm});
            skArc(sketch, "E18.0.14.5", {"start": v(-4.5, -3) * mm, "mid": v(-3.91, -4.41) * mm, "end": v(-2.5, -5) * mm});
            skLineSegment(sketch, "E18.0.14.6", {"start": v(-2.5, -5) * mm, "end": v(2.5, -5) * mm});
            skArc(sketch, "E18.0.14.7", {"start": v(2.5, -5) * mm, "mid": v(3.91, -4.41) * mm, "end": v(4.5, -3) * mm});
            skLineSegment(sketch, "E18.1.0.0", {"start": v(15.5, 481.97) * mm, "end": v(15.5, 497.8) * mm});
            skLineSegment(sketch, "E18.1.0.1", {"start": v(24.5, 481.97) * mm, "end": v(24.5, 497.8) * mm});
            skPoint(sketch, "E18.1.0.2", {"position": v(24.5, 479.97) * mm});
            skPoint(sketch, "E18.1.0.3", {"position": v(15.5, 479.97) * mm});
            skLineSegment(sketch, "E18.1.0.4", {"start": v(15.5, 497.8) * mm, "end": v(24.5, 497.8) * mm});
            skArc(sketch, "E18.1.0.5", {"start": v(15.5, 481.97) * mm, "mid": v(16.09, 480.56) * mm, "end": v(17.5, 479.97) * mm});
            skLineSegment(sketch, "E18.1.0.6", {"start": v(17.5, 479.97) * mm, "end": v(22.5, 479.97) * mm});
            skArc(sketch, "E18.1.0.7", {"start": v(22.5, 479.97) * mm, "mid": v(23.91, 480.56) * mm, "end": v(24.5, 481.97) * mm});
            skLineSegment(sketch, "E18.1.1.0", {"start": v(15.5, 447.33) * mm, "end": v(15.5, 463.15) * mm});
            skLineSegment(sketch, "E18.1.1.1", {"start": v(24.5, 447.33) * mm, "end": v(24.5, 463.15) * mm});
            skPoint(sketch, "E18.1.1.2", {"position": v(24.5, 445.33) * mm});
            skPoint(sketch, "E18.1.1.3", {"position": v(15.5, 445.33) * mm});
            skLineSegment(sketch, "E18.1.1.4", {"start": v(15.5, 463.15) * mm, "end": v(24.5, 463.15) * mm});
            skArc(sketch, "E18.1.1.5", {"start": v(15.5, 447.33) * mm, "mid": v(16.09, 445.92) * mm, "end": v(17.5, 445.33) * mm});
            skLineSegment(sketch, "E18.1.1.6", {"start": v(17.5, 445.33) * mm, "end": v(22.5, 445.33) * mm});
            skArc(sketch, "E18.1.1.7", {"start": v(22.5, 445.33) * mm, "mid": v(23.91, 445.92) * mm, "end": v(24.5, 447.33) * mm});
            skLineSegment(sketch, "E18.1.2.0", {"start": v(15.5, 412.7) * mm, "end": v(15.5, 428.51) * mm});
            skLineSegment(sketch, "E18.1.2.1", {"start": v(24.5, 412.7) * mm, "end": v(24.5, 428.51) * mm});
            skPoint(sketch, "E18.1.2.2", {"position": v(24.5, 410.7) * mm});
            skPoint(sketch, "E18.1.2.3", {"position": v(15.5, 410.7) * mm});
            skLineSegment(sketch, "E18.1.2.4", {"start": v(15.5, 428.51) * mm, "end": v(24.5, 428.51) * mm});
            skArc(sketch, "E18.1.2.5", {"start": v(15.5, 412.7) * mm, "mid": v(16.09, 411.28) * mm, "end": v(17.5, 410.7) * mm});
            skLineSegment(sketch, "E18.1.2.6", {"start": v(17.5, 410.7) * mm, "end": v(22.5, 410.7) * mm});
            skArc(sketch, "E18.1.2.7", {"start": v(22.5, 410.7) * mm, "mid": v(23.91, 411.28) * mm, "end": v(24.5, 412.7) * mm});
            skLineSegment(sketch, "E18.1.3.0", {"start": v(15.5, 378.05) * mm, "end": v(15.5, 393.87) * mm});
            skLineSegment(sketch, "E18.1.3.1", {"start": v(24.5, 378.05) * mm, "end": v(24.5, 393.87) * mm});
            skPoint(sketch, "E18.1.3.2", {"position": v(24.5, 376.05) * mm});
            skPoint(sketch, "E18.1.3.3", {"position": v(15.5, 376.05) * mm});
            skLineSegment(sketch, "E18.1.3.4", {"start": v(15.5, 393.87) * mm, "end": v(24.5, 393.87) * mm});
            skArc(sketch, "E18.1.3.5", {"start": v(15.5, 378.05) * mm, "mid": v(16.09, 376.64) * mm, "end": v(17.5, 376.05) * mm});
            skLineSegment(sketch, "E18.1.3.6", {"start": v(17.5, 376.05) * mm, "end": v(22.5, 376.05) * mm});
            skArc(sketch, "E18.1.3.7", {"start": v(22.5, 376.05) * mm, "mid": v(23.91, 376.64) * mm, "end": v(24.5, 378.05) * mm});
            skLineSegment(sketch, "E18.1.4.0", {"start": v(15.5, 343.41) * mm, "end": v(15.5, 359.23) * mm});
            skLineSegment(sketch, "E18.1.4.1", {"start": v(24.5, 343.41) * mm, "end": v(24.5, 359.23) * mm});
            skPoint(sketch, "E18.1.4.2", {"position": v(24.5, 341.41) * mm});
            skPoint(sketch, "E18.1.4.3", {"position": v(15.5, 341.41) * mm});
            skLineSegment(sketch, "E18.1.4.4", {"start": v(15.5, 359.23) * mm, "end": v(24.5, 359.23) * mm});
            skArc(sketch, "E18.1.4.5", {"start": v(15.5, 343.41) * mm, "mid": v(16.09, 342) * mm, "end": v(17.5, 341.41) * mm});
            skLineSegment(sketch, "E18.1.4.6", {"start": v(17.5, 341.41) * mm, "end": v(22.5, 341.41) * mm});
            skArc(sketch, "E18.1.4.7", {"start": v(22.5, 341.41) * mm, "mid": v(23.91, 342) * mm, "end": v(24.5, 343.41) * mm});
            skLineSegment(sketch, "E18.1.5.0", {"start": v(15.5, 308.77) * mm, "end": v(15.5, 324.59) * mm});
            skLineSegment(sketch, "E18.1.5.1", {"start": v(24.5, 308.77) * mm, "end": v(24.5, 324.59) * mm});
            skPoint(sketch, "E18.1.5.2", {"position": v(24.5, 306.77) * mm});
            skPoint(sketch, "E18.1.5.3", {"position": v(15.5, 306.77) * mm});
            skLineSegment(sketch, "E18.1.5.4", {"start": v(15.5, 324.59) * mm, "end": v(24.5, 324.59) * mm});
            skArc(sketch, "E18.1.5.5", {"start": v(15.5, 308.77) * mm, "mid": v(16.09, 307.35) * mm, "end": v(17.5, 306.77) * mm});
            skLineSegment(sketch, "E18.1.5.6", {"start": v(17.5, 306.77) * mm, "end": v(22.5, 306.77) * mm});
            skArc(sketch, "E18.1.5.7", {"start": v(22.5, 306.77) * mm, "mid": v(23.91, 307.35) * mm, "end": v(24.5, 308.77) * mm});
            skLineSegment(sketch, "E18.1.6.0", {"start": v(15.5, 274.13) * mm, "end": v(15.5, 289.95) * mm});
            skLineSegment(sketch, "E18.1.6.1", {"start": v(24.5, 274.13) * mm, "end": v(24.5, 289.95) * mm});
            skPoint(sketch, "E18.1.6.2", {"position": v(24.5, 272.13) * mm});
            skPoint(sketch, "E18.1.6.3", {"position": v(15.5, 272.13) * mm});
            skLineSegment(sketch, "E18.1.6.4", {"start": v(15.5, 289.95) * mm, "end": v(24.5, 289.95) * mm});
            skArc(sketch, "E18.1.6.5", {"start": v(15.5, 274.13) * mm, "mid": v(16.09, 272.71) * mm, "end": v(17.5, 272.13) * mm});
            skLineSegment(sketch, "E18.1.6.6", {"start": v(17.5, 272.13) * mm, "end": v(22.5, 272.13) * mm});
            skArc(sketch, "E18.1.6.7", {"start": v(22.5, 272.13) * mm, "mid": v(23.91, 272.71) * mm, "end": v(24.5, 274.13) * mm});
            skLineSegment(sketch, "E18.1.7.0", {"start": v(15.5, 239.49) * mm, "end": v(15.5, 255.3) * mm});
            skLineSegment(sketch, "E18.1.7.1", {"start": v(24.5, 239.49) * mm, "end": v(24.5, 255.3) * mm});
            skPoint(sketch, "E18.1.7.2", {"position": v(24.5, 237.49) * mm});
            skPoint(sketch, "E18.1.7.3", {"position": v(15.5, 237.49) * mm});
            skLineSegment(sketch, "E18.1.7.4", {"start": v(15.5, 255.3) * mm, "end": v(24.5, 255.3) * mm});
            skArc(sketch, "E18.1.7.5", {"start": v(15.5, 239.49) * mm, "mid": v(16.09, 238.07) * mm, "end": v(17.5, 237.49) * mm});
            skLineSegment(sketch, "E18.1.7.6", {"start": v(17.5, 237.49) * mm, "end": v(22.5, 237.49) * mm});
            skArc(sketch, "E18.1.7.7", {"start": v(22.5, 237.49) * mm, "mid": v(23.91, 238.07) * mm, "end": v(24.5, 239.49) * mm});
            skLineSegment(sketch, "E18.1.8.0", {"start": v(15.5, 204.85) * mm, "end": v(15.5, 220.67) * mm});
            skLineSegment(sketch, "E18.1.8.1", {"start": v(24.5, 204.85) * mm, "end": v(24.5, 220.67) * mm});
            skPoint(sketch, "E18.1.8.2", {"position": v(24.5, 202.85) * mm});
            skPoint(sketch, "E18.1.8.3", {"position": v(15.5, 202.85) * mm});
            skLineSegment(sketch, "E18.1.8.4", {"start": v(15.5, 220.67) * mm, "end": v(24.5, 220.67) * mm});
            skArc(sketch, "E18.1.8.5", {"start": v(15.5, 204.85) * mm, "mid": v(16.09, 203.43) * mm, "end": v(17.5, 202.85) * mm});
            skLineSegment(sketch, "E18.1.8.6", {"start": v(17.5, 202.85) * mm, "end": v(22.5, 202.85) * mm});
            skArc(sketch, "E18.1.8.7", {"start": v(22.5, 202.85) * mm, "mid": v(23.91, 203.43) * mm, "end": v(24.5, 204.85) * mm});
            skLineSegment(sketch, "E18.1.9.0", {"start": v(15.5, 170.2) * mm, "end": v(15.5, 186.03) * mm});
            skLineSegment(sketch, "E18.1.9.1", {"start": v(24.5, 170.2) * mm, "end": v(24.5, 186.03) * mm});
            skPoint(sketch, "E18.1.9.2", {"position": v(24.5, 168.2) * mm});
            skPoint(sketch, "E18.1.9.3", {"position": v(15.5, 168.2) * mm});
            skLineSegment(sketch, "E18.1.9.4", {"start": v(15.5, 186.03) * mm, "end": v(24.5, 186.03) * mm});
            skArc(sketch, "E18.1.9.5", {"start": v(15.5, 170.2) * mm, "mid": v(16.09, 168.8) * mm, "end": v(17.5, 168.2) * mm});
            skLineSegment(sketch, "E18.1.9.6", {"start": v(17.5, 168.2) * mm, "end": v(22.5, 168.2) * mm});
            skArc(sketch, "E18.1.9.7", {"start": v(22.5, 168.2) * mm, "mid": v(23.91, 168.8) * mm, "end": v(24.5, 170.2) * mm});
            skLineSegment(sketch, "E18.1.10.0", {"start": v(15.5, 135.56) * mm, "end": v(15.5, 151.38) * mm});
            skLineSegment(sketch, "E18.1.10.1", {"start": v(24.5, 135.56) * mm, "end": v(24.5, 151.38) * mm});
            skPoint(sketch, "E18.1.10.2", {"position": v(24.5, 133.56) * mm});
            skPoint(sketch, "E18.1.10.3", {"position": v(15.5, 133.56) * mm});
            skLineSegment(sketch, "E18.1.10.4", {"start": v(15.5, 151.38) * mm, "end": v(24.5, 151.38) * mm});
            skArc(sketch, "E18.1.10.5", {"start": v(15.5, 135.56) * mm, "mid": v(16.09, 134.15) * mm, "end": v(17.5, 133.56) * mm});
            skLineSegment(sketch, "E18.1.10.6", {"start": v(17.5, 133.56) * mm, "end": v(22.5, 133.56) * mm});
            skArc(sketch, "E18.1.10.7", {"start": v(22.5, 133.56) * mm, "mid": v(23.91, 134.15) * mm, "end": v(24.5, 135.56) * mm});
            skLineSegment(sketch, "E18.1.11.0", {"start": v(15.5, 100.92) * mm, "end": v(15.5, 116.74) * mm});
            skLineSegment(sketch, "E18.1.11.1", {"start": v(24.5, 100.92) * mm, "end": v(24.5, 116.74) * mm});
            skPoint(sketch, "E18.1.11.2", {"position": v(24.5, 98.92) * mm});
            skPoint(sketch, "E18.1.11.3", {"position": v(15.5, 98.92) * mm});
            skLineSegment(sketch, "E18.1.11.4", {"start": v(15.5, 116.74) * mm, "end": v(24.5, 116.74) * mm});
            skArc(sketch, "E18.1.11.5", {"start": v(15.5, 100.92) * mm, "mid": v(16.09, 99.5) * mm, "end": v(17.5, 98.92) * mm});
            skLineSegment(sketch, "E18.1.11.6", {"start": v(17.5, 98.92) * mm, "end": v(22.5, 98.92) * mm});
            skArc(sketch, "E18.1.11.7", {"start": v(22.5, 98.92) * mm, "mid": v(23.91, 99.5) * mm, "end": v(24.5, 100.92) * mm});
            skLineSegment(sketch, "E18.1.12.0", {"start": v(15.5, 66.28) * mm, "end": v(15.5, 82.1) * mm});
            skLineSegment(sketch, "E18.1.12.1", {"start": v(24.5, 66.28) * mm, "end": v(24.5, 82.1) * mm});
            skPoint(sketch, "E18.1.12.2", {"position": v(24.5, 64.28) * mm});
            skPoint(sketch, "E18.1.12.3", {"position": v(15.5, 64.28) * mm});
            skLineSegment(sketch, "E18.1.12.4", {"start": v(15.5, 82.1) * mm, "end": v(24.5, 82.1) * mm});
            skArc(sketch, "E18.1.12.5", {"start": v(15.5, 66.28) * mm, "mid": v(16.09, 64.87) * mm, "end": v(17.5, 64.28) * mm});
            skLineSegment(sketch, "E18.1.12.6", {"start": v(17.5, 64.28) * mm, "end": v(22.5, 64.28) * mm});
            skArc(sketch, "E18.1.12.7", {"start": v(22.5, 64.28) * mm, "mid": v(23.91, 64.87) * mm, "end": v(24.5, 66.28) * mm});
            skLineSegment(sketch, "E18.1.13.0", {"start": v(15.5, 31.64) * mm, "end": v(15.5, 47.46) * mm});
            skLineSegment(sketch, "E18.1.13.1", {"start": v(24.5, 31.64) * mm, "end": v(24.5, 47.46) * mm});
            skPoint(sketch, "E18.1.13.2", {"position": v(24.5, 29.64) * mm});
            skPoint(sketch, "E18.1.13.3", {"position": v(15.5, 29.64) * mm});
            skLineSegment(sketch, "E18.1.13.4", {"start": v(15.5, 47.46) * mm, "end": v(24.5, 47.46) * mm});
            skArc(sketch, "E18.1.13.5", {"start": v(15.5, 31.64) * mm, "mid": v(16.09, 30.23) * mm, "end": v(17.5, 29.64) * mm});
            skLineSegment(sketch, "E18.1.13.6", {"start": v(17.5, 29.64) * mm, "end": v(22.5, 29.64) * mm});
            skArc(sketch, "E18.1.13.7", {"start": v(22.5, 29.64) * mm, "mid": v(23.91, 30.23) * mm, "end": v(24.5, 31.64) * mm});
            skLineSegment(sketch, "E18.1.14.0", {"start": v(15.5, -3) * mm, "end": v(15.5, 12.82) * mm});
            skLineSegment(sketch, "E18.1.14.1", {"start": v(24.5, -3) * mm, "end": v(24.5, 12.82) * mm});
            skPoint(sketch, "E18.1.14.2", {"position": v(24.5, -5) * mm});
            skPoint(sketch, "E18.1.14.3", {"position": v(15.5, -5) * mm});
            skLineSegment(sketch, "E18.1.14.4", {"start": v(15.5, 12.82) * mm, "end": v(24.5, 12.82) * mm});
            skArc(sketch, "E18.1.14.5", {"start": v(15.5, -3) * mm, "mid": v(16.09, -4.41) * mm, "end": v(17.5, -5) * mm});
            skLineSegment(sketch, "E18.1.14.6", {"start": v(17.5, -5) * mm, "end": v(22.5, -5) * mm});
            skArc(sketch, "E18.1.14.7", {"start": v(22.5, -5) * mm, "mid": v(23.91, -4.41) * mm, "end": v(24.5, -3) * mm});
            skLineSegment(sketch, "E18.2.0.0", {"start": v(35.5, 481.97) * mm, "end": v(35.5, 497.8) * mm});
            skLineSegment(sketch, "E18.2.0.1", {"start": v(44.5, 481.97) * mm, "end": v(44.5, 497.8) * mm});
            skPoint(sketch, "E18.2.0.2", {"position": v(44.5, 479.97) * mm});
            skPoint(sketch, "E18.2.0.3", {"position": v(35.5, 479.97) * mm});
            skLineSegment(sketch, "E18.2.0.4", {"start": v(35.5, 497.8) * mm, "end": v(44.5, 497.8) * mm});
            skArc(sketch, "E18.2.0.5", {"start": v(35.5, 481.97) * mm, "mid": v(36.09, 480.56) * mm, "end": v(37.5, 479.97) * mm});
            skLineSegment(sketch, "E18.2.0.6", {"start": v(37.5, 479.97) * mm, "end": v(42.5, 479.97) * mm});
            skArc(sketch, "E18.2.0.7", {"start": v(42.5, 479.97) * mm, "mid": v(43.91, 480.56) * mm, "end": v(44.5, 481.97) * mm});
            skLineSegment(sketch, "E18.2.1.0", {"start": v(35.5, 447.33) * mm, "end": v(35.5, 463.15) * mm});
            skLineSegment(sketch, "E18.2.1.1", {"start": v(44.5, 447.33) * mm, "end": v(44.5, 463.15) * mm});
            skPoint(sketch, "E18.2.1.2", {"position": v(44.5, 445.33) * mm});
            skPoint(sketch, "E18.2.1.3", {"position": v(35.5, 445.33) * mm});
            skLineSegment(sketch, "E18.2.1.4", {"start": v(35.5, 463.15) * mm, "end": v(44.5, 463.15) * mm});
            skArc(sketch, "E18.2.1.5", {"start": v(35.5, 447.33) * mm, "mid": v(36.09, 445.92) * mm, "end": v(37.5, 445.33) * mm});
            skLineSegment(sketch, "E18.2.1.6", {"start": v(37.5, 445.33) * mm, "end": v(42.5, 445.33) * mm});
            skArc(sketch, "E18.2.1.7", {"start": v(42.5, 445.33) * mm, "mid": v(43.91, 445.92) * mm, "end": v(44.5, 447.33) * mm});
            skLineSegment(sketch, "E18.2.2.0", {"start": v(35.5, 412.7) * mm, "end": v(35.5, 428.51) * mm});
            skLineSegment(sketch, "E18.2.2.1", {"start": v(44.5, 412.7) * mm, "end": v(44.5, 428.51) * mm});
            skPoint(sketch, "E18.2.2.2", {"position": v(44.5, 410.7) * mm});
            skPoint(sketch, "E18.2.2.3", {"position": v(35.5, 410.7) * mm});
            skLineSegment(sketch, "E18.2.2.4", {"start": v(35.5, 428.51) * mm, "end": v(44.5, 428.51) * mm});
            skArc(sketch, "E18.2.2.5", {"start": v(35.5, 412.7) * mm, "mid": v(36.09, 411.28) * mm, "end": v(37.5, 410.7) * mm});
            skLineSegment(sketch, "E18.2.2.6", {"start": v(37.5, 410.7) * mm, "end": v(42.5, 410.7) * mm});
            skArc(sketch, "E18.2.2.7", {"start": v(42.5, 410.7) * mm, "mid": v(43.91, 411.28) * mm, "end": v(44.5, 412.7) * mm});
            skLineSegment(sketch, "E18.2.3.0", {"start": v(35.5, 378.05) * mm, "end": v(35.5, 393.87) * mm});
            skLineSegment(sketch, "E18.2.3.1", {"start": v(44.5, 378.05) * mm, "end": v(44.5, 393.87) * mm});
            skPoint(sketch, "E18.2.3.2", {"position": v(44.5, 376.05) * mm});
            skPoint(sketch, "E18.2.3.3", {"position": v(35.5, 376.05) * mm});
            skLineSegment(sketch, "E18.2.3.4", {"start": v(35.5, 393.87) * mm, "end": v(44.5, 393.87) * mm});
            skArc(sketch, "E18.2.3.5", {"start": v(35.5, 378.05) * mm, "mid": v(36.09, 376.64) * mm, "end": v(37.5, 376.05) * mm});
            skLineSegment(sketch, "E18.2.3.6", {"start": v(37.5, 376.05) * mm, "end": v(42.5, 376.05) * mm});
            skArc(sketch, "E18.2.3.7", {"start": v(42.5, 376.05) * mm, "mid": v(43.91, 376.64) * mm, "end": v(44.5, 378.05) * mm});
            skLineSegment(sketch, "E18.2.4.0", {"start": v(35.5, 343.41) * mm, "end": v(35.5, 359.23) * mm});
            skLineSegment(sketch, "E18.2.4.1", {"start": v(44.5, 343.41) * mm, "end": v(44.5, 359.23) * mm});
            skPoint(sketch, "E18.2.4.2", {"position": v(44.5, 341.41) * mm});
            skPoint(sketch, "E18.2.4.3", {"position": v(35.5, 341.41) * mm});
            skLineSegment(sketch, "E18.2.4.4", {"start": v(35.5, 359.23) * mm, "end": v(44.5, 359.23) * mm});
            skArc(sketch, "E18.2.4.5", {"start": v(35.5, 343.41) * mm, "mid": v(36.09, 342) * mm, "end": v(37.5, 341.41) * mm});
            skLineSegment(sketch, "E18.2.4.6", {"start": v(37.5, 341.41) * mm, "end": v(42.5, 341.41) * mm});
            skArc(sketch, "E18.2.4.7", {"start": v(42.5, 341.41) * mm, "mid": v(43.91, 342) * mm, "end": v(44.5, 343.41) * mm});
            skLineSegment(sketch, "E18.2.5.0", {"start": v(35.5, 308.77) * mm, "end": v(35.5, 324.59) * mm});
            skLineSegment(sketch, "E18.2.5.1", {"start": v(44.5, 308.77) * mm, "end": v(44.5, 324.59) * mm});
            skPoint(sketch, "E18.2.5.2", {"position": v(44.5, 306.77) * mm});
            skPoint(sketch, "E18.2.5.3", {"position": v(35.5, 306.77) * mm});
            skLineSegment(sketch, "E18.2.5.4", {"start": v(35.5, 324.59) * mm, "end": v(44.5, 324.59) * mm});
            skArc(sketch, "E18.2.5.5", {"start": v(35.5, 308.77) * mm, "mid": v(36.09, 307.35) * mm, "end": v(37.5, 306.77) * mm});
            skLineSegment(sketch, "E18.2.5.6", {"start": v(37.5, 306.77) * mm, "end": v(42.5, 306.77) * mm});
            skArc(sketch, "E18.2.5.7", {"start": v(42.5, 306.77) * mm, "mid": v(43.91, 307.35) * mm, "end": v(44.5, 308.77) * mm});
            skLineSegment(sketch, "E18.2.6.0", {"start": v(35.5, 274.13) * mm, "end": v(35.5, 289.95) * mm});
            skLineSegment(sketch, "E18.2.6.1", {"start": v(44.5, 274.13) * mm, "end": v(44.5, 289.95) * mm});
            skPoint(sketch, "E18.2.6.2", {"position": v(44.5, 272.13) * mm});
            skPoint(sketch, "E18.2.6.3", {"position": v(35.5, 272.13) * mm});
            skLineSegment(sketch, "E18.2.6.4", {"start": v(35.5, 289.95) * mm, "end": v(44.5, 289.95) * mm});
            skArc(sketch, "E18.2.6.5", {"start": v(35.5, 274.13) * mm, "mid": v(36.09, 272.71) * mm, "end": v(37.5, 272.13) * mm});
            skLineSegment(sketch, "E18.2.6.6", {"start": v(37.5, 272.13) * mm, "end": v(42.5, 272.13) * mm});
            skArc(sketch, "E18.2.6.7", {"start": v(42.5, 272.13) * mm, "mid": v(43.91, 272.71) * mm, "end": v(44.5, 274.13) * mm});
            skLineSegment(sketch, "E18.2.7.0", {"start": v(35.5, 239.49) * mm, "end": v(35.5, 255.3) * mm});
            skLineSegment(sketch, "E18.2.7.1", {"start": v(44.5, 239.49) * mm, "end": v(44.5, 255.3) * mm});
            skPoint(sketch, "E18.2.7.2", {"position": v(44.5, 237.49) * mm});
            skPoint(sketch, "E18.2.7.3", {"position": v(35.5, 237.49) * mm});
            skLineSegment(sketch, "E18.2.7.4", {"start": v(35.5, 255.3) * mm, "end": v(44.5, 255.3) * mm});
            skArc(sketch, "E18.2.7.5", {"start": v(35.5, 239.49) * mm, "mid": v(36.09, 238.07) * mm, "end": v(37.5, 237.49) * mm});
            skLineSegment(sketch, "E18.2.7.6", {"start": v(37.5, 237.49) * mm, "end": v(42.5, 237.49) * mm});
            skArc(sketch, "E18.2.7.7", {"start": v(42.5, 237.49) * mm, "mid": v(43.91, 238.07) * mm, "end": v(44.5, 239.49) * mm});
            skLineSegment(sketch, "E18.2.8.0", {"start": v(35.5, 204.85) * mm, "end": v(35.5, 220.67) * mm});
            skLineSegment(sketch, "E18.2.8.1", {"start": v(44.5, 204.85) * mm, "end": v(44.5, 220.67) * mm});
            skPoint(sketch, "E18.2.8.2", {"position": v(44.5, 202.85) * mm});
            skPoint(sketch, "E18.2.8.3", {"position": v(35.5, 202.85) * mm});
            skLineSegment(sketch, "E18.2.8.4", {"start": v(35.5, 220.67) * mm, "end": v(44.5, 220.67) * mm});
            skArc(sketch, "E18.2.8.5", {"start": v(35.5, 204.85) * mm, "mid": v(36.09, 203.43) * mm, "end": v(37.5, 202.85) * mm});
            skLineSegment(sketch, "E18.2.8.6", {"start": v(37.5, 202.85) * mm, "end": v(42.5, 202.85) * mm});
            skArc(sketch, "E18.2.8.7", {"start": v(42.5, 202.85) * mm, "mid": v(43.91, 203.43) * mm, "end": v(44.5, 204.85) * mm});
            skLineSegment(sketch, "E18.2.9.0", {"start": v(35.5, 170.2) * mm, "end": v(35.5, 186.03) * mm});
            skLineSegment(sketch, "E18.2.9.1", {"start": v(44.5, 170.2) * mm, "end": v(44.5, 186.03) * mm});
            skPoint(sketch, "E18.2.9.2", {"position": v(44.5, 168.2) * mm});
            skPoint(sketch, "E18.2.9.3", {"position": v(35.5, 168.2) * mm});
            skLineSegment(sketch, "E18.2.9.4", {"start": v(35.5, 186.03) * mm, "end": v(44.5, 186.03) * mm});
            skArc(sketch, "E18.2.9.5", {"start": v(35.5, 170.2) * mm, "mid": v(36.09, 168.8) * mm, "end": v(37.5, 168.2) * mm});
            skLineSegment(sketch, "E18.2.9.6", {"start": v(37.5, 168.2) * mm, "end": v(42.5, 168.2) * mm});
            skArc(sketch, "E18.2.9.7", {"start": v(42.5, 168.2) * mm, "mid": v(43.91, 168.8) * mm, "end": v(44.5, 170.2) * mm});
            skLineSegment(sketch, "E18.2.10.0", {"start": v(35.5, 135.56) * mm, "end": v(35.5, 151.38) * mm});
            skLineSegment(sketch, "E18.2.10.1", {"start": v(44.5, 135.56) * mm, "end": v(44.5, 151.38) * mm});
            skPoint(sketch, "E18.2.10.2", {"position": v(44.5, 133.56) * mm});
            skPoint(sketch, "E18.2.10.3", {"position": v(35.5, 133.56) * mm});
            skLineSegment(sketch, "E18.2.10.4", {"start": v(35.5, 151.38) * mm, "end": v(44.5, 151.38) * mm});
            skArc(sketch, "E18.2.10.5", {"start": v(35.5, 135.56) * mm, "mid": v(36.09, 134.15) * mm, "end": v(37.5, 133.56) * mm});
            skLineSegment(sketch, "E18.2.10.6", {"start": v(37.5, 133.56) * mm, "end": v(42.5, 133.56) * mm});
            skArc(sketch, "E18.2.10.7", {"start": v(42.5, 133.56) * mm, "mid": v(43.91, 134.15) * mm, "end": v(44.5, 135.56) * mm});
            skLineSegment(sketch, "E18.2.11.0", {"start": v(35.5, 100.92) * mm, "end": v(35.5, 116.74) * mm});
            skLineSegment(sketch, "E18.2.11.1", {"start": v(44.5, 100.92) * mm, "end": v(44.5, 116.74) * mm});
            skPoint(sketch, "E18.2.11.2", {"position": v(44.5, 98.92) * mm});
            skPoint(sketch, "E18.2.11.3", {"position": v(35.5, 98.92) * mm});
            skLineSegment(sketch, "E18.2.11.4", {"start": v(35.5, 116.74) * mm, "end": v(44.5, 116.74) * mm});
            skArc(sketch, "E18.2.11.5", {"start": v(35.5, 100.92) * mm, "mid": v(36.09, 99.5) * mm, "end": v(37.5, 98.92) * mm});
            skLineSegment(sketch, "E18.2.11.6", {"start": v(37.5, 98.92) * mm, "end": v(42.5, 98.92) * mm});
            skArc(sketch, "E18.2.11.7", {"start": v(42.5, 98.92) * mm, "mid": v(43.91, 99.5) * mm, "end": v(44.5, 100.92) * mm});
            skLineSegment(sketch, "E18.2.12.0", {"start": v(35.5, 66.28) * mm, "end": v(35.5, 82.1) * mm});
            skLineSegment(sketch, "E18.2.12.1", {"start": v(44.5, 66.28) * mm, "end": v(44.5, 82.1) * mm});
            skPoint(sketch, "E18.2.12.2", {"position": v(44.5, 64.28) * mm});
            skPoint(sketch, "E18.2.12.3", {"position": v(35.5, 64.28) * mm});
            skLineSegment(sketch, "E18.2.12.4", {"start": v(35.5, 82.1) * mm, "end": v(44.5, 82.1) * mm});
            skArc(sketch, "E18.2.12.5", {"start": v(35.5, 66.28) * mm, "mid": v(36.09, 64.87) * mm, "end": v(37.5, 64.28) * mm});
            skLineSegment(sketch, "E18.2.12.6", {"start": v(37.5, 64.28) * mm, "end": v(42.5, 64.28) * mm});
            skArc(sketch, "E18.2.12.7", {"start": v(42.5, 64.28) * mm, "mid": v(43.91, 64.87) * mm, "end": v(44.5, 66.28) * mm});
            skLineSegment(sketch, "E18.2.13.0", {"start": v(35.5, 31.64) * mm, "end": v(35.5, 47.46) * mm});
            skLineSegment(sketch, "E18.2.13.1", {"start": v(44.5, 31.64) * mm, "end": v(44.5, 47.46) * mm});
            skPoint(sketch, "E18.2.13.2", {"position": v(44.5, 29.64) * mm});
            skPoint(sketch, "E18.2.13.3", {"position": v(35.5, 29.64) * mm});
            skLineSegment(sketch, "E18.2.13.4", {"start": v(35.5, 47.46) * mm, "end": v(44.5, 47.46) * mm});
            skArc(sketch, "E18.2.13.5", {"start": v(35.5, 31.64) * mm, "mid": v(36.09, 30.23) * mm, "end": v(37.5, 29.64) * mm});
            skLineSegment(sketch, "E18.2.13.6", {"start": v(37.5, 29.64) * mm, "end": v(42.5, 29.64) * mm});
            skArc(sketch, "E18.2.13.7", {"start": v(42.5, 29.64) * mm, "mid": v(43.91, 30.23) * mm, "end": v(44.5, 31.64) * mm});
            skLineSegment(sketch, "E18.2.14.0", {"start": v(35.5, -3) * mm, "end": v(35.5, 12.82) * mm});
            skLineSegment(sketch, "E18.2.14.1", {"start": v(44.5, -3) * mm, "end": v(44.5, 12.82) * mm});
            skPoint(sketch, "E18.2.14.2", {"position": v(44.5, -5) * mm});
            skPoint(sketch, "E18.2.14.3", {"position": v(35.5, -5) * mm});
            skLineSegment(sketch, "E18.2.14.4", {"start": v(35.5, 12.82) * mm, "end": v(44.5, 12.82) * mm});
            skArc(sketch, "E18.2.14.5", {"start": v(35.5, -3) * mm, "mid": v(36.09, -4.41) * mm, "end": v(37.5, -5) * mm});
            skLineSegment(sketch, "E18.2.14.6", {"start": v(37.5, -5) * mm, "end": v(42.5, -5) * mm});
            skArc(sketch, "E18.2.14.7", {"start": v(42.5, -5) * mm, "mid": v(43.91, -4.41) * mm, "end": v(44.5, -3) * mm});
            skLineSegment(sketch, "E18.3.0.0", {"start": v(55.5, 481.97) * mm, "end": v(55.5, 497.8) * mm});
            skLineSegment(sketch, "E18.3.0.1", {"start": v(64.5, 481.97) * mm, "end": v(64.5, 497.8) * mm});
            skPoint(sketch, "E18.3.0.2", {"position": v(64.5, 479.97) * mm});
            skPoint(sketch, "E18.3.0.3", {"position": v(55.5, 479.97) * mm});
            skLineSegment(sketch, "E18.3.0.4", {"start": v(55.5, 497.8) * mm, "end": v(64.5, 497.8) * mm});
            skArc(sketch, "E18.3.0.5", {"start": v(55.5, 481.97) * mm, "mid": v(56.09, 480.56) * mm, "end": v(57.5, 479.97) * mm});
            skLineSegment(sketch, "E18.3.0.6", {"start": v(57.5, 479.97) * mm, "end": v(62.5, 479.97) * mm});
            skArc(sketch, "E18.3.0.7", {"start": v(62.5, 479.97) * mm, "mid": v(63.91, 480.56) * mm, "end": v(64.5, 481.97) * mm});
            skLineSegment(sketch, "E18.3.1.0", {"start": v(55.5, 447.33) * mm, "end": v(55.5, 463.15) * mm});
            skLineSegment(sketch, "E18.3.1.1", {"start": v(64.5, 447.33) * mm, "end": v(64.5, 463.15) * mm});
            skPoint(sketch, "E18.3.1.2", {"position": v(64.5, 445.33) * mm});
            skPoint(sketch, "E18.3.1.3", {"position": v(55.5, 445.33) * mm});
            skLineSegment(sketch, "E18.3.1.4", {"start": v(55.5, 463.15) * mm, "end": v(64.5, 463.15) * mm});
            skArc(sketch, "E18.3.1.5", {"start": v(55.5, 447.33) * mm, "mid": v(56.09, 445.92) * mm, "end": v(57.5, 445.33) * mm});
            skLineSegment(sketch, "E18.3.1.6", {"start": v(57.5, 445.33) * mm, "end": v(62.5, 445.33) * mm});
            skArc(sketch, "E18.3.1.7", {"start": v(62.5, 445.33) * mm, "mid": v(63.91, 445.92) * mm, "end": v(64.5, 447.33) * mm});
            skLineSegment(sketch, "E18.3.2.0", {"start": v(55.5, 412.7) * mm, "end": v(55.5, 428.51) * mm});
            skLineSegment(sketch, "E18.3.2.1", {"start": v(64.5, 412.7) * mm, "end": v(64.5, 428.51) * mm});
            skPoint(sketch, "E18.3.2.2", {"position": v(64.5, 410.7) * mm});
            skPoint(sketch, "E18.3.2.3", {"position": v(55.5, 410.7) * mm});
            skLineSegment(sketch, "E18.3.2.4", {"start": v(55.5, 428.51) * mm, "end": v(64.5, 428.51) * mm});
            skArc(sketch, "E18.3.2.5", {"start": v(55.5, 412.7) * mm, "mid": v(56.09, 411.28) * mm, "end": v(57.5, 410.7) * mm});
            skLineSegment(sketch, "E18.3.2.6", {"start": v(57.5, 410.7) * mm, "end": v(62.5, 410.7) * mm});
            skArc(sketch, "E18.3.2.7", {"start": v(62.5, 410.7) * mm, "mid": v(63.91, 411.28) * mm, "end": v(64.5, 412.7) * mm});
            skLineSegment(sketch, "E18.3.3.0", {"start": v(55.5, 378.05) * mm, "end": v(55.5, 393.87) * mm});
            skLineSegment(sketch, "E18.3.3.1", {"start": v(64.5, 378.05) * mm, "end": v(64.5, 393.87) * mm});
            skPoint(sketch, "E18.3.3.2", {"position": v(64.5, 376.05) * mm});
            skPoint(sketch, "E18.3.3.3", {"position": v(55.5, 376.05) * mm});
            skLineSegment(sketch, "E18.3.3.4", {"start": v(55.5, 393.87) * mm, "end": v(64.5, 393.87) * mm});
            skArc(sketch, "E18.3.3.5", {"start": v(55.5, 378.05) * mm, "mid": v(56.09, 376.64) * mm, "end": v(57.5, 376.05) * mm});
            skLineSegment(sketch, "E18.3.3.6", {"start": v(57.5, 376.05) * mm, "end": v(62.5, 376.05) * mm});
            skArc(sketch, "E18.3.3.7", {"start": v(62.5, 376.05) * mm, "mid": v(63.91, 376.64) * mm, "end": v(64.5, 378.05) * mm});
            skLineSegment(sketch, "E18.3.4.0", {"start": v(55.5, 343.41) * mm, "end": v(55.5, 359.23) * mm});
            skLineSegment(sketch, "E18.3.4.1", {"start": v(64.5, 343.41) * mm, "end": v(64.5, 359.23) * mm});
            skPoint(sketch, "E18.3.4.2", {"position": v(64.5, 341.41) * mm});
            skPoint(sketch, "E18.3.4.3", {"position": v(55.5, 341.41) * mm});
            skLineSegment(sketch, "E18.3.4.4", {"start": v(55.5, 359.23) * mm, "end": v(64.5, 359.23) * mm});
            skArc(sketch, "E18.3.4.5", {"start": v(55.5, 343.41) * mm, "mid": v(56.09, 342) * mm, "end": v(57.5, 341.41) * mm});
            skLineSegment(sketch, "E18.3.4.6", {"start": v(57.5, 341.41) * mm, "end": v(62.5, 341.41) * mm});
            skArc(sketch, "E18.3.4.7", {"start": v(62.5, 341.41) * mm, "mid": v(63.91, 342) * mm, "end": v(64.5, 343.41) * mm});
            skLineSegment(sketch, "E18.3.5.0", {"start": v(55.5, 308.77) * mm, "end": v(55.5, 324.59) * mm});
            skLineSegment(sketch, "E18.3.5.1", {"start": v(64.5, 308.77) * mm, "end": v(64.5, 324.59) * mm});
            skPoint(sketch, "E18.3.5.2", {"position": v(64.5, 306.77) * mm});
            skPoint(sketch, "E18.3.5.3", {"position": v(55.5, 306.77) * mm});
            skLineSegment(sketch, "E18.3.5.4", {"start": v(55.5, 324.59) * mm, "end": v(64.5, 324.59) * mm});
            skArc(sketch, "E18.3.5.5", {"start": v(55.5, 308.77) * mm, "mid": v(56.09, 307.35) * mm, "end": v(57.5, 306.77) * mm});
            skLineSegment(sketch, "E18.3.5.6", {"start": v(57.5, 306.77) * mm, "end": v(62.5, 306.77) * mm});
            skArc(sketch, "E18.3.5.7", {"start": v(62.5, 306.77) * mm, "mid": v(63.91, 307.35) * mm, "end": v(64.5, 308.77) * mm});
            skLineSegment(sketch, "E18.3.6.0", {"start": v(55.5, 274.13) * mm, "end": v(55.5, 289.95) * mm});
            skLineSegment(sketch, "E18.3.6.1", {"start": v(64.5, 274.13) * mm, "end": v(64.5, 289.95) * mm});
            skPoint(sketch, "E18.3.6.2", {"position": v(64.5, 272.13) * mm});
            skPoint(sketch, "E18.3.6.3", {"position": v(55.5, 272.13) * mm});
            skLineSegment(sketch, "E18.3.6.4", {"start": v(55.5, 289.95) * mm, "end": v(64.5, 289.95) * mm});
            skArc(sketch, "E18.3.6.5", {"start": v(55.5, 274.13) * mm, "mid": v(56.09, 272.71) * mm, "end": v(57.5, 272.13) * mm});
            skLineSegment(sketch, "E18.3.6.6", {"start": v(57.5, 272.13) * mm, "end": v(62.5, 272.13) * mm});
            skArc(sketch, "E18.3.6.7", {"start": v(62.5, 272.13) * mm, "mid": v(63.91, 272.71) * mm, "end": v(64.5, 274.13) * mm});
            skLineSegment(sketch, "E18.3.7.0", {"start": v(55.5, 239.49) * mm, "end": v(55.5, 255.3) * mm});
            skLineSegment(sketch, "E18.3.7.1", {"start": v(64.5, 239.49) * mm, "end": v(64.5, 255.3) * mm});
            skPoint(sketch, "E18.3.7.2", {"position": v(64.5, 237.49) * mm});
            skPoint(sketch, "E18.3.7.3", {"position": v(55.5, 237.49) * mm});
            skLineSegment(sketch, "E18.3.7.4", {"start": v(55.5, 255.3) * mm, "end": v(64.5, 255.3) * mm});
            skArc(sketch, "E18.3.7.5", {"start": v(55.5, 239.49) * mm, "mid": v(56.09, 238.07) * mm, "end": v(57.5, 237.49) * mm});
            skLineSegment(sketch, "E18.3.7.6", {"start": v(57.5, 237.49) * mm, "end": v(62.5, 237.49) * mm});
            skArc(sketch, "E18.3.7.7", {"start": v(62.5, 237.49) * mm, "mid": v(63.91, 238.07) * mm, "end": v(64.5, 239.49) * mm});
            skLineSegment(sketch, "E18.3.8.0", {"start": v(55.5, 204.85) * mm, "end": v(55.5, 220.67) * mm});
            skLineSegment(sketch, "E18.3.8.1", {"start": v(64.5, 204.85) * mm, "end": v(64.5, 220.67) * mm});
            skPoint(sketch, "E18.3.8.2", {"position": v(64.5, 202.85) * mm});
            skPoint(sketch, "E18.3.8.3", {"position": v(55.5, 202.85) * mm});
            skLineSegment(sketch, "E18.3.8.4", {"start": v(55.5, 220.67) * mm, "end": v(64.5, 220.67) * mm});
            skArc(sketch, "E18.3.8.5", {"start": v(55.5, 204.85) * mm, "mid": v(56.09, 203.43) * mm, "end": v(57.5, 202.85) * mm});
            skLineSegment(sketch, "E18.3.8.6", {"start": v(57.5, 202.85) * mm, "end": v(62.5, 202.85) * mm});
            skArc(sketch, "E18.3.8.7", {"start": v(62.5, 202.85) * mm, "mid": v(63.91, 203.43) * mm, "end": v(64.5, 204.85) * mm});
            skLineSegment(sketch, "E18.3.9.0", {"start": v(55.5, 170.2) * mm, "end": v(55.5, 186.03) * mm});
            skLineSegment(sketch, "E18.3.9.1", {"start": v(64.5, 170.2) * mm, "end": v(64.5, 186.03) * mm});
            skPoint(sketch, "E18.3.9.2", {"position": v(64.5, 168.2) * mm});
            skPoint(sketch, "E18.3.9.3", {"position": v(55.5, 168.2) * mm});
            skLineSegment(sketch, "E18.3.9.4", {"start": v(55.5, 186.03) * mm, "end": v(64.5, 186.03) * mm});
            skArc(sketch, "E18.3.9.5", {"start": v(55.5, 170.2) * mm, "mid": v(56.09, 168.8) * mm, "end": v(57.5, 168.2) * mm});
            skLineSegment(sketch, "E18.3.9.6", {"start": v(57.5, 168.2) * mm, "end": v(62.5, 168.2) * mm});
            skArc(sketch, "E18.3.9.7", {"start": v(62.5, 168.2) * mm, "mid": v(63.91, 168.8) * mm, "end": v(64.5, 170.2) * mm});
            skLineSegment(sketch, "E18.3.10.0", {"start": v(55.5, 135.56) * mm, "end": v(55.5, 151.38) * mm});
            skLineSegment(sketch, "E18.3.10.1", {"start": v(64.5, 135.56) * mm, "end": v(64.5, 151.38) * mm});
            skPoint(sketch, "E18.3.10.2", {"position": v(64.5, 133.56) * mm});
            skPoint(sketch, "E18.3.10.3", {"position": v(55.5, 133.56) * mm});
            skLineSegment(sketch, "E18.3.10.4", {"start": v(55.5, 151.38) * mm, "end": v(64.5, 151.38) * mm});
            skArc(sketch, "E18.3.10.5", {"start": v(55.5, 135.56) * mm, "mid": v(56.09, 134.15) * mm, "end": v(57.5, 133.56) * mm});
            skLineSegment(sketch, "E18.3.10.6", {"start": v(57.5, 133.56) * mm, "end": v(62.5, 133.56) * mm});
            skArc(sketch, "E18.3.10.7", {"start": v(62.5, 133.56) * mm, "mid": v(63.91, 134.15) * mm, "end": v(64.5, 135.56) * mm});
            skLineSegment(sketch, "E18.3.11.0", {"start": v(55.5, 100.92) * mm, "end": v(55.5, 116.74) * mm});
            skLineSegment(sketch, "E18.3.11.1", {"start": v(64.5, 100.92) * mm, "end": v(64.5, 116.74) * mm});
            skPoint(sketch, "E18.3.11.2", {"position": v(64.5, 98.92) * mm});
            skPoint(sketch, "E18.3.11.3", {"position": v(55.5, 98.92) * mm});
            skLineSegment(sketch, "E18.3.11.4", {"start": v(55.5, 116.74) * mm, "end": v(64.5, 116.74) * mm});
            skArc(sketch, "E18.3.11.5", {"start": v(55.5, 100.92) * mm, "mid": v(56.09, 99.5) * mm, "end": v(57.5, 98.92) * mm});
            skLineSegment(sketch, "E18.3.11.6", {"start": v(57.5, 98.92) * mm, "end": v(62.5, 98.92) * mm});
            skArc(sketch, "E18.3.11.7", {"start": v(62.5, 98.92) * mm, "mid": v(63.91, 99.5) * mm, "end": v(64.5, 100.92) * mm});
            skLineSegment(sketch, "E18.3.12.0", {"start": v(55.5, 66.28) * mm, "end": v(55.5, 82.1) * mm});
            skLineSegment(sketch, "E18.3.12.1", {"start": v(64.5, 66.28) * mm, "end": v(64.5, 82.1) * mm});
            skPoint(sketch, "E18.3.12.2", {"position": v(64.5, 64.28) * mm});
            skPoint(sketch, "E18.3.12.3", {"position": v(55.5, 64.28) * mm});
            skLineSegment(sketch, "E18.3.12.4", {"start": v(55.5, 82.1) * mm, "end": v(64.5, 82.1) * mm});
            skArc(sketch, "E18.3.12.5", {"start": v(55.5, 66.28) * mm, "mid": v(56.09, 64.87) * mm, "end": v(57.5, 64.28) * mm});
            skLineSegment(sketch, "E18.3.12.6", {"start": v(57.5, 64.28) * mm, "end": v(62.5, 64.28) * mm});
            skArc(sketch, "E18.3.12.7", {"start": v(62.5, 64.28) * mm, "mid": v(63.91, 64.87) * mm, "end": v(64.5, 66.28) * mm});
            skLineSegment(sketch, "E18.3.13.0", {"start": v(55.5, 31.64) * mm, "end": v(55.5, 47.46) * mm});
            skLineSegment(sketch, "E18.3.13.1", {"start": v(64.5, 31.64) * mm, "end": v(64.5, 47.46) * mm});
            skPoint(sketch, "E18.3.13.2", {"position": v(64.5, 29.64) * mm});
            skPoint(sketch, "E18.3.13.3", {"position": v(55.5, 29.64) * mm});
            skLineSegment(sketch, "E18.3.13.4", {"start": v(55.5, 47.46) * mm, "end": v(64.5, 47.46) * mm});
            skArc(sketch, "E18.3.13.5", {"start": v(55.5, 31.64) * mm, "mid": v(56.09, 30.23) * mm, "end": v(57.5, 29.64) * mm});
            skLineSegment(sketch, "E18.3.13.6", {"start": v(57.5, 29.64) * mm, "end": v(62.5, 29.64) * mm});
            skArc(sketch, "E18.3.13.7", {"start": v(62.5, 29.64) * mm, "mid": v(63.91, 30.23) * mm, "end": v(64.5, 31.64) * mm});
            skLineSegment(sketch, "E18.3.14.0", {"start": v(55.5, -3) * mm, "end": v(55.5, 12.82) * mm});
            skLineSegment(sketch, "E18.3.14.1", {"start": v(64.5, -3) * mm, "end": v(64.5, 12.82) * mm});
            skPoint(sketch, "E18.3.14.2", {"position": v(64.5, -5) * mm});
            skPoint(sketch, "E18.3.14.3", {"position": v(55.5, -5) * mm});
            skLineSegment(sketch, "E18.3.14.4", {"start": v(55.5, 12.82) * mm, "end": v(64.5, 12.82) * mm});
            skArc(sketch, "E18.3.14.5", {"start": v(55.5, -3) * mm, "mid": v(56.09, -4.41) * mm, "end": v(57.5, -5) * mm});
            skLineSegment(sketch, "E18.3.14.6", {"start": v(57.5, -5) * mm, "end": v(62.5, -5) * mm});
            skArc(sketch, "E18.3.14.7", {"start": v(62.5, -5) * mm, "mid": v(63.91, -4.41) * mm, "end": v(64.5, -3) * mm});
            skLineSegment(sketch, "E18.4.0.0", {"start": v(75.5, 481.97) * mm, "end": v(75.5, 497.8) * mm});
            skLineSegment(sketch, "E18.4.0.1", {"start": v(84.5, 481.97) * mm, "end": v(84.5, 497.8) * mm});
            skPoint(sketch, "E18.4.0.2", {"position": v(84.5, 479.97) * mm});
            skPoint(sketch, "E18.4.0.3", {"position": v(75.5, 479.97) * mm});
            skLineSegment(sketch, "E18.4.0.4", {"start": v(75.5, 497.8) * mm, "end": v(84.5, 497.8) * mm});
            skArc(sketch, "E18.4.0.5", {"start": v(75.5, 481.97) * mm, "mid": v(76.09, 480.56) * mm, "end": v(77.5, 479.97) * mm});
            skLineSegment(sketch, "E18.4.0.6", {"start": v(77.5, 479.97) * mm, "end": v(82.5, 479.97) * mm});
            skArc(sketch, "E18.4.0.7", {"start": v(82.5, 479.97) * mm, "mid": v(83.91, 480.56) * mm, "end": v(84.5, 481.97) * mm});
            skLineSegment(sketch, "E18.4.1.0", {"start": v(75.5, 447.33) * mm, "end": v(75.5, 463.15) * mm});
            skLineSegment(sketch, "E18.4.1.1", {"start": v(84.5, 447.33) * mm, "end": v(84.5, 463.15) * mm});
            skPoint(sketch, "E18.4.1.2", {"position": v(84.5, 445.33) * mm});
            skPoint(sketch, "E18.4.1.3", {"position": v(75.5, 445.33) * mm});
            skLineSegment(sketch, "E18.4.1.4", {"start": v(75.5, 463.15) * mm, "end": v(84.5, 463.15) * mm});
            skArc(sketch, "E18.4.1.5", {"start": v(75.5, 447.33) * mm, "mid": v(76.09, 445.92) * mm, "end": v(77.5, 445.33) * mm});
            skLineSegment(sketch, "E18.4.1.6", {"start": v(77.5, 445.33) * mm, "end": v(82.5, 445.33) * mm});
            skArc(sketch, "E18.4.1.7", {"start": v(82.5, 445.33) * mm, "mid": v(83.91, 445.92) * mm, "end": v(84.5, 447.33) * mm});
            skLineSegment(sketch, "E18.4.2.0", {"start": v(75.5, 412.7) * mm, "end": v(75.5, 428.51) * mm});
            skLineSegment(sketch, "E18.4.2.1", {"start": v(84.5, 412.7) * mm, "end": v(84.5, 428.51) * mm});
            skPoint(sketch, "E18.4.2.2", {"position": v(84.5, 410.7) * mm});
            skPoint(sketch, "E18.4.2.3", {"position": v(75.5, 410.7) * mm});
            skLineSegment(sketch, "E18.4.2.4", {"start": v(75.5, 428.51) * mm, "end": v(84.5, 428.51) * mm});
            skArc(sketch, "E18.4.2.5", {"start": v(75.5, 412.7) * mm, "mid": v(76.09, 411.28) * mm, "end": v(77.5, 410.7) * mm});
            skLineSegment(sketch, "E18.4.2.6", {"start": v(77.5, 410.7) * mm, "end": v(82.5, 410.7) * mm});
            skArc(sketch, "E18.4.2.7", {"start": v(82.5, 410.7) * mm, "mid": v(83.91, 411.28) * mm, "end": v(84.5, 412.7) * mm});
            skLineSegment(sketch, "E18.4.3.0", {"start": v(75.5, 378.05) * mm, "end": v(75.5, 393.87) * mm});
            skLineSegment(sketch, "E18.4.3.1", {"start": v(84.5, 378.05) * mm, "end": v(84.5, 393.87) * mm});
            skPoint(sketch, "E18.4.3.2", {"position": v(84.5, 376.05) * mm});
            skPoint(sketch, "E18.4.3.3", {"position": v(75.5, 376.05) * mm});
            skLineSegment(sketch, "E18.4.3.4", {"start": v(75.5, 393.87) * mm, "end": v(84.5, 393.87) * mm});
            skArc(sketch, "E18.4.3.5", {"start": v(75.5, 378.05) * mm, "mid": v(76.09, 376.64) * mm, "end": v(77.5, 376.05) * mm});
            skLineSegment(sketch, "E18.4.3.6", {"start": v(77.5, 376.05) * mm, "end": v(82.5, 376.05) * mm});
            skArc(sketch, "E18.4.3.7", {"start": v(82.5, 376.05) * mm, "mid": v(83.91, 376.64) * mm, "end": v(84.5, 378.05) * mm});
            skLineSegment(sketch, "E18.4.4.0", {"start": v(75.5, 343.41) * mm, "end": v(75.5, 359.23) * mm});
            skLineSegment(sketch, "E18.4.4.1", {"start": v(84.5, 343.41) * mm, "end": v(84.5, 359.23) * mm});
            skPoint(sketch, "E18.4.4.2", {"position": v(84.5, 341.41) * mm});
            skPoint(sketch, "E18.4.4.3", {"position": v(75.5, 341.41) * mm});
            skLineSegment(sketch, "E18.4.4.4", {"start": v(75.5, 359.23) * mm, "end": v(84.5, 359.23) * mm});
            skArc(sketch, "E18.4.4.5", {"start": v(75.5, 343.41) * mm, "mid": v(76.09, 342) * mm, "end": v(77.5, 341.41) * mm});
            skLineSegment(sketch, "E18.4.4.6", {"start": v(77.5, 341.41) * mm, "end": v(82.5, 341.41) * mm});
            skArc(sketch, "E18.4.4.7", {"start": v(82.5, 341.41) * mm, "mid": v(83.91, 342) * mm, "end": v(84.5, 343.41) * mm});
            skLineSegment(sketch, "E18.4.5.0", {"start": v(75.5, 308.77) * mm, "end": v(75.5, 324.59) * mm});
            skLineSegment(sketch, "E18.4.5.1", {"start": v(84.5, 308.77) * mm, "end": v(84.5, 324.59) * mm});
            skPoint(sketch, "E18.4.5.2", {"position": v(84.5, 306.77) * mm});
            skPoint(sketch, "E18.4.5.3", {"position": v(75.5, 306.77) * mm});
            skLineSegment(sketch, "E18.4.5.4", {"start": v(75.5, 324.59) * mm, "end": v(84.5, 324.59) * mm});
            skArc(sketch, "E18.4.5.5", {"start": v(75.5, 308.77) * mm, "mid": v(76.09, 307.35) * mm, "end": v(77.5, 306.77) * mm});
            skLineSegment(sketch, "E18.4.5.6", {"start": v(77.5, 306.77) * mm, "end": v(82.5, 306.77) * mm});
            skArc(sketch, "E18.4.5.7", {"start": v(82.5, 306.77) * mm, "mid": v(83.91, 307.35) * mm, "end": v(84.5, 308.77) * mm});
            skLineSegment(sketch, "E18.4.6.0", {"start": v(75.5, 274.13) * mm, "end": v(75.5, 289.95) * mm});
            skLineSegment(sketch, "E18.4.6.1", {"start": v(84.5, 274.13) * mm, "end": v(84.5, 289.95) * mm});
            skPoint(sketch, "E18.4.6.2", {"position": v(84.5, 272.13) * mm});
            skPoint(sketch, "E18.4.6.3", {"position": v(75.5, 272.13) * mm});
            skLineSegment(sketch, "E18.4.6.4", {"start": v(75.5, 289.95) * mm, "end": v(84.5, 289.95) * mm});
            skArc(sketch, "E18.4.6.5", {"start": v(75.5, 274.13) * mm, "mid": v(76.09, 272.71) * mm, "end": v(77.5, 272.13) * mm});
            skLineSegment(sketch, "E18.4.6.6", {"start": v(77.5, 272.13) * mm, "end": v(82.5, 272.13) * mm});
            skArc(sketch, "E18.4.6.7", {"start": v(82.5, 272.13) * mm, "mid": v(83.91, 272.71) * mm, "end": v(84.5, 274.13) * mm});
            skLineSegment(sketch, "E18.4.7.0", {"start": v(75.5, 239.49) * mm, "end": v(75.5, 255.3) * mm});
            skLineSegment(sketch, "E18.4.7.1", {"start": v(84.5, 239.49) * mm, "end": v(84.5, 255.3) * mm});
            skPoint(sketch, "E18.4.7.2", {"position": v(84.5, 237.49) * mm});
            skPoint(sketch, "E18.4.7.3", {"position": v(75.5, 237.49) * mm});
            skLineSegment(sketch, "E18.4.7.4", {"start": v(75.5, 255.3) * mm, "end": v(84.5, 255.3) * mm});
            skArc(sketch, "E18.4.7.5", {"start": v(75.5, 239.49) * mm, "mid": v(76.09, 238.07) * mm, "end": v(77.5, 237.49) * mm});
            skLineSegment(sketch, "E18.4.7.6", {"start": v(77.5, 237.49) * mm, "end": v(82.5, 237.49) * mm});
            skArc(sketch, "E18.4.7.7", {"start": v(82.5, 237.49) * mm, "mid": v(83.91, 238.07) * mm, "end": v(84.5, 239.49) * mm});
            skLineSegment(sketch, "E18.4.8.0", {"start": v(75.5, 204.85) * mm, "end": v(75.5, 220.67) * mm});
            skLineSegment(sketch, "E18.4.8.1", {"start": v(84.5, 204.85) * mm, "end": v(84.5, 220.67) * mm});
            skPoint(sketch, "E18.4.8.2", {"position": v(84.5, 202.85) * mm});
            skPoint(sketch, "E18.4.8.3", {"position": v(75.5, 202.85) * mm});
            skLineSegment(sketch, "E18.4.8.4", {"start": v(75.5, 220.67) * mm, "end": v(84.5, 220.67) * mm});
            skArc(sketch, "E18.4.8.5", {"start": v(75.5, 204.85) * mm, "mid": v(76.09, 203.43) * mm, "end": v(77.5, 202.85) * mm});
            skLineSegment(sketch, "E18.4.8.6", {"start": v(77.5, 202.85) * mm, "end": v(82.5, 202.85) * mm});
            skArc(sketch, "E18.4.8.7", {"start": v(82.5, 202.85) * mm, "mid": v(83.91, 203.43) * mm, "end": v(84.5, 204.85) * mm});
            skLineSegment(sketch, "E18.4.9.0", {"start": v(75.5, 170.2) * mm, "end": v(75.5, 186.03) * mm});
            skLineSegment(sketch, "E18.4.9.1", {"start": v(84.5, 170.2) * mm, "end": v(84.5, 186.03) * mm});
            skPoint(sketch, "E18.4.9.2", {"position": v(84.5, 168.2) * mm});
            skPoint(sketch, "E18.4.9.3", {"position": v(75.5, 168.2) * mm});
            skLineSegment(sketch, "E18.4.9.4", {"start": v(75.5, 186.03) * mm, "end": v(84.5, 186.03) * mm});
            skArc(sketch, "E18.4.9.5", {"start": v(75.5, 170.2) * mm, "mid": v(76.09, 168.8) * mm, "end": v(77.5, 168.2) * mm});
            skLineSegment(sketch, "E18.4.9.6", {"start": v(77.5, 168.2) * mm, "end": v(82.5, 168.2) * mm});
            skArc(sketch, "E18.4.9.7", {"start": v(82.5, 168.2) * mm, "mid": v(83.91, 168.8) * mm, "end": v(84.5, 170.2) * mm});
            skLineSegment(sketch, "E18.4.10.0", {"start": v(75.5, 135.56) * mm, "end": v(75.5, 151.38) * mm});
            skLineSegment(sketch, "E18.4.10.1", {"start": v(84.5, 135.56) * mm, "end": v(84.5, 151.38) * mm});
            skPoint(sketch, "E18.4.10.2", {"position": v(84.5, 133.56) * mm});
            skPoint(sketch, "E18.4.10.3", {"position": v(75.5, 133.56) * mm});
            skLineSegment(sketch, "E18.4.10.4", {"start": v(75.5, 151.38) * mm, "end": v(84.5, 151.38) * mm});
            skArc(sketch, "E18.4.10.5", {"start": v(75.5, 135.56) * mm, "mid": v(76.09, 134.15) * mm, "end": v(77.5, 133.56) * mm});
            skLineSegment(sketch, "E18.4.10.6", {"start": v(77.5, 133.56) * mm, "end": v(82.5, 133.56) * mm});
            skArc(sketch, "E18.4.10.7", {"start": v(82.5, 133.56) * mm, "mid": v(83.91, 134.15) * mm, "end": v(84.5, 135.56) * mm});
            skLineSegment(sketch, "E18.4.11.0", {"start": v(75.5, 100.92) * mm, "end": v(75.5, 116.74) * mm});
            skLineSegment(sketch, "E18.4.11.1", {"start": v(84.5, 100.92) * mm, "end": v(84.5, 116.74) * mm});
            skPoint(sketch, "E18.4.11.2", {"position": v(84.5, 98.92) * mm});
            skPoint(sketch, "E18.4.11.3", {"position": v(75.5, 98.92) * mm});
            skLineSegment(sketch, "E18.4.11.4", {"start": v(75.5, 116.74) * mm, "end": v(84.5, 116.74) * mm});
            skArc(sketch, "E18.4.11.5", {"start": v(75.5, 100.92) * mm, "mid": v(76.09, 99.5) * mm, "end": v(77.5, 98.92) * mm});
            skLineSegment(sketch, "E18.4.11.6", {"start": v(77.5, 98.92) * mm, "end": v(82.5, 98.92) * mm});
            skArc(sketch, "E18.4.11.7", {"start": v(82.5, 98.92) * mm, "mid": v(83.91, 99.5) * mm, "end": v(84.5, 100.92) * mm});
            skLineSegment(sketch, "E18.4.12.0", {"start": v(75.5, 66.28) * mm, "end": v(75.5, 82.1) * mm});
            skLineSegment(sketch, "E18.4.12.1", {"start": v(84.5, 66.28) * mm, "end": v(84.5, 82.1) * mm});
            skPoint(sketch, "E18.4.12.2", {"position": v(84.5, 64.28) * mm});
            skPoint(sketch, "E18.4.12.3", {"position": v(75.5, 64.28) * mm});
            skLineSegment(sketch, "E18.4.12.4", {"start": v(75.5, 82.1) * mm, "end": v(84.5, 82.1) * mm});
            skArc(sketch, "E18.4.12.5", {"start": v(75.5, 66.28) * mm, "mid": v(76.09, 64.87) * mm, "end": v(77.5, 64.28) * mm});
            skLineSegment(sketch, "E18.4.12.6", {"start": v(77.5, 64.28) * mm, "end": v(82.5, 64.28) * mm});
            skArc(sketch, "E18.4.12.7", {"start": v(82.5, 64.28) * mm, "mid": v(83.91, 64.87) * mm, "end": v(84.5, 66.28) * mm});
            skLineSegment(sketch, "E18.4.13.0", {"start": v(75.5, 31.64) * mm, "end": v(75.5, 47.46) * mm});
            skLineSegment(sketch, "E18.4.13.1", {"start": v(84.5, 31.64) * mm, "end": v(84.5, 47.46) * mm});
            skPoint(sketch, "E18.4.13.2", {"position": v(84.5, 29.64) * mm});
            skPoint(sketch, "E18.4.13.3", {"position": v(75.5, 29.64) * mm});
            skLineSegment(sketch, "E18.4.13.4", {"start": v(75.5, 47.46) * mm, "end": v(84.5, 47.46) * mm});
            skArc(sketch, "E18.4.13.5", {"start": v(75.5, 31.64) * mm, "mid": v(76.09, 30.23) * mm, "end": v(77.5, 29.64) * mm});
            skLineSegment(sketch, "E18.4.13.6", {"start": v(77.5, 29.64) * mm, "end": v(82.5, 29.64) * mm});
            skArc(sketch, "E18.4.13.7", {"start": v(82.5, 29.64) * mm, "mid": v(83.91, 30.23) * mm, "end": v(84.5, 31.64) * mm});
            skLineSegment(sketch, "E18.4.14.0", {"start": v(75.5, -3) * mm, "end": v(75.5, 12.82) * mm});
            skLineSegment(sketch, "E18.4.14.1", {"start": v(84.5, -3) * mm, "end": v(84.5, 12.82) * mm});
            skPoint(sketch, "E18.4.14.2", {"position": v(84.5, -5) * mm});
            skPoint(sketch, "E18.4.14.3", {"position": v(75.5, -5) * mm});
            skLineSegment(sketch, "E18.4.14.4", {"start": v(75.5, 12.82) * mm, "end": v(84.5, 12.82) * mm});
            skArc(sketch, "E18.4.14.5", {"start": v(75.5, -3) * mm, "mid": v(76.09, -4.41) * mm, "end": v(77.5, -5) * mm});
            skLineSegment(sketch, "E18.4.14.6", {"start": v(77.5, -5) * mm, "end": v(82.5, -5) * mm});
            skArc(sketch, "E18.4.14.7", {"start": v(82.5, -5) * mm, "mid": v(83.91, -4.41) * mm, "end": v(84.5, -3) * mm});
            skLineSegment(sketch, "E18.5.0.0", {"start": v(95.5, 481.97) * mm, "end": v(95.5, 497.8) * mm});
            skLineSegment(sketch, "E18.5.0.1", {"start": v(104.5, 481.97) * mm, "end": v(104.5, 497.8) * mm});
            skPoint(sketch, "E18.5.0.2", {"position": v(104.5, 479.97) * mm});
            skPoint(sketch, "E18.5.0.3", {"position": v(95.5, 479.97) * mm});
            skLineSegment(sketch, "E18.5.0.4", {"start": v(95.5, 497.8) * mm, "end": v(104.5, 497.8) * mm});
            skArc(sketch, "E18.5.0.5", {"start": v(95.5, 481.97) * mm, "mid": v(96.09, 480.56) * mm, "end": v(97.5, 479.97) * mm});
            skLineSegment(sketch, "E18.5.0.6", {"start": v(97.5, 479.97) * mm, "end": v(102.5, 479.97) * mm});
            skArc(sketch, "E18.5.0.7", {"start": v(102.5, 479.97) * mm, "mid": v(103.91, 480.56) * mm, "end": v(104.5, 481.97) * mm});
            skLineSegment(sketch, "E18.5.1.0", {"start": v(95.5, 447.33) * mm, "end": v(95.5, 463.15) * mm});
            skLineSegment(sketch, "E18.5.1.1", {"start": v(104.5, 447.33) * mm, "end": v(104.5, 463.15) * mm});
            skPoint(sketch, "E18.5.1.2", {"position": v(104.5, 445.33) * mm});
            skPoint(sketch, "E18.5.1.3", {"position": v(95.5, 445.33) * mm});
            skLineSegment(sketch, "E18.5.1.4", {"start": v(95.5, 463.15) * mm, "end": v(104.5, 463.15) * mm});
            skArc(sketch, "E18.5.1.5", {"start": v(95.5, 447.33) * mm, "mid": v(96.09, 445.92) * mm, "end": v(97.5, 445.33) * mm});
            skLineSegment(sketch, "E18.5.1.6", {"start": v(97.5, 445.33) * mm, "end": v(102.5, 445.33) * mm});
            skArc(sketch, "E18.5.1.7", {"start": v(102.5, 445.33) * mm, "mid": v(103.91, 445.92) * mm, "end": v(104.5, 447.33) * mm});
            skLineSegment(sketch, "E18.5.2.0", {"start": v(95.5, 412.7) * mm, "end": v(95.5, 428.51) * mm});
            skLineSegment(sketch, "E18.5.2.1", {"start": v(104.5, 412.7) * mm, "end": v(104.5, 428.51) * mm});
            skPoint(sketch, "E18.5.2.2", {"position": v(104.5, 410.7) * mm});
            skPoint(sketch, "E18.5.2.3", {"position": v(95.5, 410.7) * mm});
            skLineSegment(sketch, "E18.5.2.4", {"start": v(95.5, 428.51) * mm, "end": v(104.5, 428.51) * mm});
            skArc(sketch, "E18.5.2.5", {"start": v(95.5, 412.7) * mm, "mid": v(96.09, 411.28) * mm, "end": v(97.5, 410.7) * mm});
            skLineSegment(sketch, "E18.5.2.6", {"start": v(97.5, 410.7) * mm, "end": v(102.5, 410.7) * mm});
            skArc(sketch, "E18.5.2.7", {"start": v(102.5, 410.7) * mm, "mid": v(103.91, 411.28) * mm, "end": v(104.5, 412.7) * mm});
            skLineSegment(sketch, "E18.5.3.0", {"start": v(95.5, 378.05) * mm, "end": v(95.5, 393.87) * mm});
            skLineSegment(sketch, "E18.5.3.1", {"start": v(104.5, 378.05) * mm, "end": v(104.5, 393.87) * mm});
            skPoint(sketch, "E18.5.3.2", {"position": v(104.5, 376.05) * mm});
            skPoint(sketch, "E18.5.3.3", {"position": v(95.5, 376.05) * mm});
            skLineSegment(sketch, "E18.5.3.4", {"start": v(95.5, 393.87) * mm, "end": v(104.5, 393.87) * mm});
            skArc(sketch, "E18.5.3.5", {"start": v(95.5, 378.05) * mm, "mid": v(96.09, 376.64) * mm, "end": v(97.5, 376.05) * mm});
            skLineSegment(sketch, "E18.5.3.6", {"start": v(97.5, 376.05) * mm, "end": v(102.5, 376.05) * mm});
            skArc(sketch, "E18.5.3.7", {"start": v(102.5, 376.05) * mm, "mid": v(103.91, 376.64) * mm, "end": v(104.5, 378.05) * mm});
            skLineSegment(sketch, "E18.5.4.0", {"start": v(95.5, 343.41) * mm, "end": v(95.5, 359.23) * mm});
            skLineSegment(sketch, "E18.5.4.1", {"start": v(104.5, 343.41) * mm, "end": v(104.5, 359.23) * mm});
            skPoint(sketch, "E18.5.4.2", {"position": v(104.5, 341.41) * mm});
            skPoint(sketch, "E18.5.4.3", {"position": v(95.5, 341.41) * mm});
            skLineSegment(sketch, "E18.5.4.4", {"start": v(95.5, 359.23) * mm, "end": v(104.5, 359.23) * mm});
            skArc(sketch, "E18.5.4.5", {"start": v(95.5, 343.41) * mm, "mid": v(96.09, 342) * mm, "end": v(97.5, 341.41) * mm});
            skLineSegment(sketch, "E18.5.4.6", {"start": v(97.5, 341.41) * mm, "end": v(102.5, 341.41) * mm});
            skArc(sketch, "E18.5.4.7", {"start": v(102.5, 341.41) * mm, "mid": v(103.91, 342) * mm, "end": v(104.5, 343.41) * mm});
            skLineSegment(sketch, "E18.5.5.0", {"start": v(95.5, 308.77) * mm, "end": v(95.5, 324.59) * mm});
            skLineSegment(sketch, "E18.5.5.1", {"start": v(104.5, 308.77) * mm, "end": v(104.5, 324.59) * mm});
            skPoint(sketch, "E18.5.5.2", {"position": v(104.5, 306.77) * mm});
            skPoint(sketch, "E18.5.5.3", {"position": v(95.5, 306.77) * mm});
            skLineSegment(sketch, "E18.5.5.4", {"start": v(95.5, 324.59) * mm, "end": v(104.5, 324.59) * mm});
            skArc(sketch, "E18.5.5.5", {"start": v(95.5, 308.77) * mm, "mid": v(96.09, 307.35) * mm, "end": v(97.5, 306.77) * mm});
            skLineSegment(sketch, "E18.5.5.6", {"start": v(97.5, 306.77) * mm, "end": v(102.5, 306.77) * mm});
            skArc(sketch, "E18.5.5.7", {"start": v(102.5, 306.77) * mm, "mid": v(103.91, 307.35) * mm, "end": v(104.5, 308.77) * mm});
            skLineSegment(sketch, "E18.5.6.0", {"start": v(95.5, 274.13) * mm, "end": v(95.5, 289.95) * mm});
            skLineSegment(sketch, "E18.5.6.1", {"start": v(104.5, 274.13) * mm, "end": v(104.5, 289.95) * mm});
            skPoint(sketch, "E18.5.6.2", {"position": v(104.5, 272.13) * mm});
            skPoint(sketch, "E18.5.6.3", {"position": v(95.5, 272.13) * mm});
            skLineSegment(sketch, "E18.5.6.4", {"start": v(95.5, 289.95) * mm, "end": v(104.5, 289.95) * mm});
            skArc(sketch, "E18.5.6.5", {"start": v(95.5, 274.13) * mm, "mid": v(96.09, 272.71) * mm, "end": v(97.5, 272.13) * mm});
            skLineSegment(sketch, "E18.5.6.6", {"start": v(97.5, 272.13) * mm, "end": v(102.5, 272.13) * mm});
            skArc(sketch, "E18.5.6.7", {"start": v(102.5, 272.13) * mm, "mid": v(103.91, 272.71) * mm, "end": v(104.5, 274.13) * mm});
            skLineSegment(sketch, "E18.5.7.0", {"start": v(95.5, 239.49) * mm, "end": v(95.5, 255.3) * mm});
            skLineSegment(sketch, "E18.5.7.1", {"start": v(104.5, 239.49) * mm, "end": v(104.5, 255.3) * mm});
            skPoint(sketch, "E18.5.7.2", {"position": v(104.5, 237.49) * mm});
            skPoint(sketch, "E18.5.7.3", {"position": v(95.5, 237.49) * mm});
            skLineSegment(sketch, "E18.5.7.4", {"start": v(95.5, 255.3) * mm, "end": v(104.5, 255.3) * mm});
            skArc(sketch, "E18.5.7.5", {"start": v(95.5, 239.49) * mm, "mid": v(96.09, 238.07) * mm, "end": v(97.5, 237.49) * mm});
            skLineSegment(sketch, "E18.5.7.6", {"start": v(97.5, 237.49) * mm, "end": v(102.5, 237.49) * mm});
            skArc(sketch, "E18.5.7.7", {"start": v(102.5, 237.49) * mm, "mid": v(103.91, 238.07) * mm, "end": v(104.5, 239.49) * mm});
            skLineSegment(sketch, "E18.5.8.0", {"start": v(95.5, 204.85) * mm, "end": v(95.5, 220.67) * mm});
            skLineSegment(sketch, "E18.5.8.1", {"start": v(104.5, 204.85) * mm, "end": v(104.5, 220.67) * mm});
            skPoint(sketch, "E18.5.8.2", {"position": v(104.5, 202.85) * mm});
            skPoint(sketch, "E18.5.8.3", {"position": v(95.5, 202.85) * mm});
            skLineSegment(sketch, "E18.5.8.4", {"start": v(95.5, 220.67) * mm, "end": v(104.5, 220.67) * mm});
            skArc(sketch, "E18.5.8.5", {"start": v(95.5, 204.85) * mm, "mid": v(96.09, 203.43) * mm, "end": v(97.5, 202.85) * mm});
            skLineSegment(sketch, "E18.5.8.6", {"start": v(97.5, 202.85) * mm, "end": v(102.5, 202.85) * mm});
            skArc(sketch, "E18.5.8.7", {"start": v(102.5, 202.85) * mm, "mid": v(103.91, 203.43) * mm, "end": v(104.5, 204.85) * mm});
            skLineSegment(sketch, "E18.5.9.0", {"start": v(95.5, 170.2) * mm, "end": v(95.5, 186.03) * mm});
            skLineSegment(sketch, "E18.5.9.1", {"start": v(104.5, 170.2) * mm, "end": v(104.5, 186.03) * mm});
            skPoint(sketch, "E18.5.9.2", {"position": v(104.5, 168.2) * mm});
            skPoint(sketch, "E18.5.9.3", {"position": v(95.5, 168.2) * mm});
            skLineSegment(sketch, "E18.5.9.4", {"start": v(95.5, 186.03) * mm, "end": v(104.5, 186.03) * mm});
            skArc(sketch, "E18.5.9.5", {"start": v(95.5, 170.2) * mm, "mid": v(96.09, 168.8) * mm, "end": v(97.5, 168.2) * mm});
            skLineSegment(sketch, "E18.5.9.6", {"start": v(97.5, 168.2) * mm, "end": v(102.5, 168.2) * mm});
            skArc(sketch, "E18.5.9.7", {"start": v(102.5, 168.2) * mm, "mid": v(103.91, 168.8) * mm, "end": v(104.5, 170.2) * mm});
            skLineSegment(sketch, "E18.5.10.0", {"start": v(95.5, 135.56) * mm, "end": v(95.5, 151.38) * mm});
            skLineSegment(sketch, "E18.5.10.1", {"start": v(104.5, 135.56) * mm, "end": v(104.5, 151.38) * mm});
            skPoint(sketch, "E18.5.10.2", {"position": v(104.5, 133.56) * mm});
            skPoint(sketch, "E18.5.10.3", {"position": v(95.5, 133.56) * mm});
            skLineSegment(sketch, "E18.5.10.4", {"start": v(95.5, 151.38) * mm, "end": v(104.5, 151.38) * mm});
            skArc(sketch, "E18.5.10.5", {"start": v(95.5, 135.56) * mm, "mid": v(96.09, 134.15) * mm, "end": v(97.5, 133.56) * mm});
            skLineSegment(sketch, "E18.5.10.6", {"start": v(97.5, 133.56) * mm, "end": v(102.5, 133.56) * mm});
            skArc(sketch, "E18.5.10.7", {"start": v(102.5, 133.56) * mm, "mid": v(103.91, 134.15) * mm, "end": v(104.5, 135.56) * mm});
            skLineSegment(sketch, "E18.5.11.0", {"start": v(95.5, 100.92) * mm, "end": v(95.5, 116.74) * mm});
            skLineSegment(sketch, "E18.5.11.1", {"start": v(104.5, 100.92) * mm, "end": v(104.5, 116.74) * mm});
            skPoint(sketch, "E18.5.11.2", {"position": v(104.5, 98.92) * mm});
            skPoint(sketch, "E18.5.11.3", {"position": v(95.5, 98.92) * mm});
            skLineSegment(sketch, "E18.5.11.4", {"start": v(95.5, 116.74) * mm, "end": v(104.5, 116.74) * mm});
            skArc(sketch, "E18.5.11.5", {"start": v(95.5, 100.92) * mm, "mid": v(96.09, 99.5) * mm, "end": v(97.5, 98.92) * mm});
            skLineSegment(sketch, "E18.5.11.6", {"start": v(97.5, 98.92) * mm, "end": v(102.5, 98.92) * mm});
            skArc(sketch, "E18.5.11.7", {"start": v(102.5, 98.92) * mm, "mid": v(103.91, 99.5) * mm, "end": v(104.5, 100.92) * mm});
            skLineSegment(sketch, "E18.5.12.0", {"start": v(95.5, 66.28) * mm, "end": v(95.5, 82.1) * mm});
            skLineSegment(sketch, "E18.5.12.1", {"start": v(104.5, 66.28) * mm, "end": v(104.5, 82.1) * mm});
            skPoint(sketch, "E18.5.12.2", {"position": v(104.5, 64.28) * mm});
            skPoint(sketch, "E18.5.12.3", {"position": v(95.5, 64.28) * mm});
            skLineSegment(sketch, "E18.5.12.4", {"start": v(95.5, 82.1) * mm, "end": v(104.5, 82.1) * mm});
            skArc(sketch, "E18.5.12.5", {"start": v(95.5, 66.28) * mm, "mid": v(96.09, 64.87) * mm, "end": v(97.5, 64.28) * mm});
            skLineSegment(sketch, "E18.5.12.6", {"start": v(97.5, 64.28) * mm, "end": v(102.5, 64.28) * mm});
            skArc(sketch, "E18.5.12.7", {"start": v(102.5, 64.28) * mm, "mid": v(103.91, 64.87) * mm, "end": v(104.5, 66.28) * mm});
            skLineSegment(sketch, "E18.5.13.0", {"start": v(95.5, 31.64) * mm, "end": v(95.5, 47.46) * mm});
            skLineSegment(sketch, "E18.5.13.1", {"start": v(104.5, 31.64) * mm, "end": v(104.5, 47.46) * mm});
            skPoint(sketch, "E18.5.13.2", {"position": v(104.5, 29.64) * mm});
            skPoint(sketch, "E18.5.13.3", {"position": v(95.5, 29.64) * mm});
            skLineSegment(sketch, "E18.5.13.4", {"start": v(95.5, 47.46) * mm, "end": v(104.5, 47.46) * mm});
            skArc(sketch, "E18.5.13.5", {"start": v(95.5, 31.64) * mm, "mid": v(96.09, 30.23) * mm, "end": v(97.5, 29.64) * mm});
            skLineSegment(sketch, "E18.5.13.6", {"start": v(97.5, 29.64) * mm, "end": v(102.5, 29.64) * mm});
            skArc(sketch, "E18.5.13.7", {"start": v(102.5, 29.64) * mm, "mid": v(103.91, 30.23) * mm, "end": v(104.5, 31.64) * mm});
            skLineSegment(sketch, "E18.5.14.0", {"start": v(95.5, -3) * mm, "end": v(95.5, 12.82) * mm});
            skLineSegment(sketch, "E18.5.14.1", {"start": v(104.5, -3) * mm, "end": v(104.5, 12.82) * mm});
            skPoint(sketch, "E18.5.14.2", {"position": v(104.5, -5) * mm});
            skPoint(sketch, "E18.5.14.3", {"position": v(95.5, -5) * mm});
            skLineSegment(sketch, "E18.5.14.4", {"start": v(95.5, 12.82) * mm, "end": v(104.5, 12.82) * mm});
            skArc(sketch, "E18.5.14.5", {"start": v(95.5, -3) * mm, "mid": v(96.09, -4.41) * mm, "end": v(97.5, -5) * mm});
            skLineSegment(sketch, "E18.5.14.6", {"start": v(97.5, -5) * mm, "end": v(102.5, -5) * mm});
            skArc(sketch, "E18.5.14.7", {"start": v(102.5, -5) * mm, "mid": v(103.91, -4.41) * mm, "end": v(104.5, -3) * mm});
            skLineSegment(sketch, "E18.6.0.0", {"start": v(115.5, 481.97) * mm, "end": v(115.5, 497.8) * mm});
            skLineSegment(sketch, "E18.6.0.1", {"start": v(124.5, 481.97) * mm, "end": v(124.5, 497.8) * mm});
            skPoint(sketch, "E18.6.0.2", {"position": v(124.5, 479.97) * mm});
            skPoint(sketch, "E18.6.0.3", {"position": v(115.5, 479.97) * mm});
            skLineSegment(sketch, "E18.6.0.4", {"start": v(115.5, 497.8) * mm, "end": v(124.5, 497.8) * mm});
            skArc(sketch, "E18.6.0.5", {"start": v(115.5, 481.97) * mm, "mid": v(116.09, 480.56) * mm, "end": v(117.5, 479.97) * mm});
            skLineSegment(sketch, "E18.6.0.6", {"start": v(117.5, 479.97) * mm, "end": v(122.5, 479.97) * mm});
            skArc(sketch, "E18.6.0.7", {"start": v(122.5, 479.97) * mm, "mid": v(123.91, 480.56) * mm, "end": v(124.5, 481.97) * mm});
            skLineSegment(sketch, "E18.6.1.0", {"start": v(115.5, 447.33) * mm, "end": v(115.5, 463.15) * mm});
            skLineSegment(sketch, "E18.6.1.1", {"start": v(124.5, 447.33) * mm, "end": v(124.5, 463.15) * mm});
            skPoint(sketch, "E18.6.1.2", {"position": v(124.5, 445.33) * mm});
            skPoint(sketch, "E18.6.1.3", {"position": v(115.5, 445.33) * mm});
            skLineSegment(sketch, "E18.6.1.4", {"start": v(115.5, 463.15) * mm, "end": v(124.5, 463.15) * mm});
            skArc(sketch, "E18.6.1.5", {"start": v(115.5, 447.33) * mm, "mid": v(116.09, 445.92) * mm, "end": v(117.5, 445.33) * mm});
            skLineSegment(sketch, "E18.6.1.6", {"start": v(117.5, 445.33) * mm, "end": v(122.5, 445.33) * mm});
            skArc(sketch, "E18.6.1.7", {"start": v(122.5, 445.33) * mm, "mid": v(123.91, 445.92) * mm, "end": v(124.5, 447.33) * mm});
            skLineSegment(sketch, "E18.6.2.0", {"start": v(115.5, 412.7) * mm, "end": v(115.5, 428.51) * mm});
            skLineSegment(sketch, "E18.6.2.1", {"start": v(124.5, 412.7) * mm, "end": v(124.5, 428.51) * mm});
            skPoint(sketch, "E18.6.2.2", {"position": v(124.5, 410.7) * mm});
            skPoint(sketch, "E18.6.2.3", {"position": v(115.5, 410.7) * mm});
            skLineSegment(sketch, "E18.6.2.4", {"start": v(115.5, 428.51) * mm, "end": v(124.5, 428.51) * mm});
            skArc(sketch, "E18.6.2.5", {"start": v(115.5, 412.7) * mm, "mid": v(116.09, 411.28) * mm, "end": v(117.5, 410.7) * mm});
            skLineSegment(sketch, "E18.6.2.6", {"start": v(117.5, 410.7) * mm, "end": v(122.5, 410.7) * mm});
            skArc(sketch, "E18.6.2.7", {"start": v(122.5, 410.7) * mm, "mid": v(123.91, 411.28) * mm, "end": v(124.5, 412.7) * mm});
            skLineSegment(sketch, "E18.6.3.0", {"start": v(115.5, 378.05) * mm, "end": v(115.5, 393.87) * mm});
            skLineSegment(sketch, "E18.6.3.1", {"start": v(124.5, 378.05) * mm, "end": v(124.5, 393.87) * mm});
            skPoint(sketch, "E18.6.3.2", {"position": v(124.5, 376.05) * mm});
            skPoint(sketch, "E18.6.3.3", {"position": v(115.5, 376.05) * mm});
            skLineSegment(sketch, "E18.6.3.4", {"start": v(115.5, 393.87) * mm, "end": v(124.5, 393.87) * mm});
            skArc(sketch, "E18.6.3.5", {"start": v(115.5, 378.05) * mm, "mid": v(116.09, 376.64) * mm, "end": v(117.5, 376.05) * mm});
            skLineSegment(sketch, "E18.6.3.6", {"start": v(117.5, 376.05) * mm, "end": v(122.5, 376.05) * mm});
            skArc(sketch, "E18.6.3.7", {"start": v(122.5, 376.05) * mm, "mid": v(123.91, 376.64) * mm, "end": v(124.5, 378.05) * mm});
            skLineSegment(sketch, "E18.6.4.0", {"start": v(115.5, 343.41) * mm, "end": v(115.5, 359.23) * mm});
            skLineSegment(sketch, "E18.6.4.1", {"start": v(124.5, 343.41) * mm, "end": v(124.5, 359.23) * mm});
            skPoint(sketch, "E18.6.4.2", {"position": v(124.5, 341.41) * mm});
            skPoint(sketch, "E18.6.4.3", {"position": v(115.5, 341.41) * mm});
            skLineSegment(sketch, "E18.6.4.4", {"start": v(115.5, 359.23) * mm, "end": v(124.5, 359.23) * mm});
            skArc(sketch, "E18.6.4.5", {"start": v(115.5, 343.41) * mm, "mid": v(116.09, 342) * mm, "end": v(117.5, 341.41) * mm});
            skLineSegment(sketch, "E18.6.4.6", {"start": v(117.5, 341.41) * mm, "end": v(122.5, 341.41) * mm});
            skArc(sketch, "E18.6.4.7", {"start": v(122.5, 341.41) * mm, "mid": v(123.91, 342) * mm, "end": v(124.5, 343.41) * mm});
            skLineSegment(sketch, "E18.6.5.0", {"start": v(115.5, 308.77) * mm, "end": v(115.5, 324.59) * mm});
            skLineSegment(sketch, "E18.6.5.1", {"start": v(124.5, 308.77) * mm, "end": v(124.5, 324.59) * mm});
            skPoint(sketch, "E18.6.5.2", {"position": v(124.5, 306.77) * mm});
            skPoint(sketch, "E18.6.5.3", {"position": v(115.5, 306.77) * mm});
            skLineSegment(sketch, "E18.6.5.4", {"start": v(115.5, 324.59) * mm, "end": v(124.5, 324.59) * mm});
            skArc(sketch, "E18.6.5.5", {"start": v(115.5, 308.77) * mm, "mid": v(116.09, 307.35) * mm, "end": v(117.5, 306.77) * mm});
            skLineSegment(sketch, "E18.6.5.6", {"start": v(117.5, 306.77) * mm, "end": v(122.5, 306.77) * mm});
            skArc(sketch, "E18.6.5.7", {"start": v(122.5, 306.77) * mm, "mid": v(123.91, 307.35) * mm, "end": v(124.5, 308.77) * mm});
            skLineSegment(sketch, "E18.6.6.0", {"start": v(115.5, 274.13) * mm, "end": v(115.5, 289.95) * mm});
            skLineSegment(sketch, "E18.6.6.1", {"start": v(124.5, 274.13) * mm, "end": v(124.5, 289.95) * mm});
            skPoint(sketch, "E18.6.6.2", {"position": v(124.5, 272.13) * mm});
            skPoint(sketch, "E18.6.6.3", {"position": v(115.5, 272.13) * mm});
            skLineSegment(sketch, "E18.6.6.4", {"start": v(115.5, 289.95) * mm, "end": v(124.5, 289.95) * mm});
            skArc(sketch, "E18.6.6.5", {"start": v(115.5, 274.13) * mm, "mid": v(116.09, 272.71) * mm, "end": v(117.5, 272.13) * mm});
            skLineSegment(sketch, "E18.6.6.6", {"start": v(117.5, 272.13) * mm, "end": v(122.5, 272.13) * mm});
            skArc(sketch, "E18.6.6.7", {"start": v(122.5, 272.13) * mm, "mid": v(123.91, 272.71) * mm, "end": v(124.5, 274.13) * mm});
            skLineSegment(sketch, "E18.6.7.0", {"start": v(115.5, 239.49) * mm, "end": v(115.5, 255.3) * mm});
            skLineSegment(sketch, "E18.6.7.1", {"start": v(124.5, 239.49) * mm, "end": v(124.5, 255.3) * mm});
            skPoint(sketch, "E18.6.7.2", {"position": v(124.5, 237.49) * mm});
            skPoint(sketch, "E18.6.7.3", {"position": v(115.5, 237.49) * mm});
            skLineSegment(sketch, "E18.6.7.4", {"start": v(115.5, 255.3) * mm, "end": v(124.5, 255.3) * mm});
            skArc(sketch, "E18.6.7.5", {"start": v(115.5, 239.49) * mm, "mid": v(116.09, 238.07) * mm, "end": v(117.5, 237.49) * mm});
            skLineSegment(sketch, "E18.6.7.6", {"start": v(117.5, 237.49) * mm, "end": v(122.5, 237.49) * mm});
            skArc(sketch, "E18.6.7.7", {"start": v(122.5, 237.49) * mm, "mid": v(123.91, 238.07) * mm, "end": v(124.5, 239.49) * mm});
            skLineSegment(sketch, "E18.6.8.0", {"start": v(115.5, 204.85) * mm, "end": v(115.5, 220.67) * mm});
            skLineSegment(sketch, "E18.6.8.1", {"start": v(124.5, 204.85) * mm, "end": v(124.5, 220.67) * mm});
            skPoint(sketch, "E18.6.8.2", {"position": v(124.5, 202.85) * mm});
            skPoint(sketch, "E18.6.8.3", {"position": v(115.5, 202.85) * mm});
            skLineSegment(sketch, "E18.6.8.4", {"start": v(115.5, 220.67) * mm, "end": v(124.5, 220.67) * mm});
            skArc(sketch, "E18.6.8.5", {"start": v(115.5, 204.85) * mm, "mid": v(116.09, 203.43) * mm, "end": v(117.5, 202.85) * mm});
            skLineSegment(sketch, "E18.6.8.6", {"start": v(117.5, 202.85) * mm, "end": v(122.5, 202.85) * mm});
            skArc(sketch, "E18.6.8.7", {"start": v(122.5, 202.85) * mm, "mid": v(123.91, 203.43) * mm, "end": v(124.5, 204.85) * mm});
            skLineSegment(sketch, "E18.6.9.0", {"start": v(115.5, 170.2) * mm, "end": v(115.5, 186.03) * mm});
            skLineSegment(sketch, "E18.6.9.1", {"start": v(124.5, 170.2) * mm, "end": v(124.5, 186.03) * mm});
            skPoint(sketch, "E18.6.9.2", {"position": v(124.5, 168.2) * mm});
            skPoint(sketch, "E18.6.9.3", {"position": v(115.5, 168.2) * mm});
            skLineSegment(sketch, "E18.6.9.4", {"start": v(115.5, 186.03) * mm, "end": v(124.5, 186.03) * mm});
            skArc(sketch, "E18.6.9.5", {"start": v(115.5, 170.2) * mm, "mid": v(116.09, 168.8) * mm, "end": v(117.5, 168.2) * mm});
            skLineSegment(sketch, "E18.6.9.6", {"start": v(117.5, 168.2) * mm, "end": v(122.5, 168.2) * mm});
            skArc(sketch, "E18.6.9.7", {"start": v(122.5, 168.2) * mm, "mid": v(123.91, 168.8) * mm, "end": v(124.5, 170.2) * mm});
            skLineSegment(sketch, "E18.6.10.0", {"start": v(115.5, 135.56) * mm, "end": v(115.5, 151.38) * mm});
            skLineSegment(sketch, "E18.6.10.1", {"start": v(124.5, 135.56) * mm, "end": v(124.5, 151.38) * mm});
            skPoint(sketch, "E18.6.10.2", {"position": v(124.5, 133.56) * mm});
            skPoint(sketch, "E18.6.10.3", {"position": v(115.5, 133.56) * mm});
            skLineSegment(sketch, "E18.6.10.4", {"start": v(115.5, 151.38) * mm, "end": v(124.5, 151.38) * mm});
            skArc(sketch, "E18.6.10.5", {"start": v(115.5, 135.56) * mm, "mid": v(116.09, 134.15) * mm, "end": v(117.5, 133.56) * mm});
            skLineSegment(sketch, "E18.6.10.6", {"start": v(117.5, 133.56) * mm, "end": v(122.5, 133.56) * mm});
            skArc(sketch, "E18.6.10.7", {"start": v(122.5, 133.56) * mm, "mid": v(123.91, 134.15) * mm, "end": v(124.5, 135.56) * mm});
            skLineSegment(sketch, "E18.6.11.0", {"start": v(115.5, 100.92) * mm, "end": v(115.5, 116.74) * mm});
            skLineSegment(sketch, "E18.6.11.1", {"start": v(124.5, 100.92) * mm, "end": v(124.5, 116.74) * mm});
            skPoint(sketch, "E18.6.11.2", {"position": v(124.5, 98.92) * mm});
            skPoint(sketch, "E18.6.11.3", {"position": v(115.5, 98.92) * mm});
            skLineSegment(sketch, "E18.6.11.4", {"start": v(115.5, 116.74) * mm, "end": v(124.5, 116.74) * mm});
            skArc(sketch, "E18.6.11.5", {"start": v(115.5, 100.92) * mm, "mid": v(116.09, 99.5) * mm, "end": v(117.5, 98.92) * mm});
            skLineSegment(sketch, "E18.6.11.6", {"start": v(117.5, 98.92) * mm, "end": v(122.5, 98.92) * mm});
            skArc(sketch, "E18.6.11.7", {"start": v(122.5, 98.92) * mm, "mid": v(123.91, 99.5) * mm, "end": v(124.5, 100.92) * mm});
            skLineSegment(sketch, "E18.6.12.0", {"start": v(115.5, 66.28) * mm, "end": v(115.5, 82.1) * mm});
            skLineSegment(sketch, "E18.6.12.1", {"start": v(124.5, 66.28) * mm, "end": v(124.5, 82.1) * mm});
            skPoint(sketch, "E18.6.12.2", {"position": v(124.5, 64.28) * mm});
            skPoint(sketch, "E18.6.12.3", {"position": v(115.5, 64.28) * mm});
            skLineSegment(sketch, "E18.6.12.4", {"start": v(115.5, 82.1) * mm, "end": v(124.5, 82.1) * mm});
            skArc(sketch, "E18.6.12.5", {"start": v(115.5, 66.28) * mm, "mid": v(116.09, 64.87) * mm, "end": v(117.5, 64.28) * mm});
            skLineSegment(sketch, "E18.6.12.6", {"start": v(117.5, 64.28) * mm, "end": v(122.5, 64.28) * mm});
            skArc(sketch, "E18.6.12.7", {"start": v(122.5, 64.28) * mm, "mid": v(123.91, 64.87) * mm, "end": v(124.5, 66.28) * mm});
            skLineSegment(sketch, "E18.6.13.0", {"start": v(115.5, 31.64) * mm, "end": v(115.5, 47.46) * mm});
            skLineSegment(sketch, "E18.6.13.1", {"start": v(124.5, 31.64) * mm, "end": v(124.5, 47.46) * mm});
            skPoint(sketch, "E18.6.13.2", {"position": v(124.5, 29.64) * mm});
            skPoint(sketch, "E18.6.13.3", {"position": v(115.5, 29.64) * mm});
            skLineSegment(sketch, "E18.6.13.4", {"start": v(115.5, 47.46) * mm, "end": v(124.5, 47.46) * mm});
            skArc(sketch, "E18.6.13.5", {"start": v(115.5, 31.64) * mm, "mid": v(116.09, 30.23) * mm, "end": v(117.5, 29.64) * mm});
            skLineSegment(sketch, "E18.6.13.6", {"start": v(117.5, 29.64) * mm, "end": v(122.5, 29.64) * mm});
            skArc(sketch, "E18.6.13.7", {"start": v(122.5, 29.64) * mm, "mid": v(123.91, 30.23) * mm, "end": v(124.5, 31.64) * mm});
            skLineSegment(sketch, "E18.6.14.0", {"start": v(115.5, -3) * mm, "end": v(115.5, 12.82) * mm});
            skLineSegment(sketch, "E18.6.14.1", {"start": v(124.5, -3) * mm, "end": v(124.5, 12.82) * mm});
            skPoint(sketch, "E18.6.14.2", {"position": v(124.5, -5) * mm});
            skPoint(sketch, "E18.6.14.3", {"position": v(115.5, -5) * mm});
            skLineSegment(sketch, "E18.6.14.4", {"start": v(115.5, 12.82) * mm, "end": v(124.5, 12.82) * mm});
            skArc(sketch, "E18.6.14.5", {"start": v(115.5, -3) * mm, "mid": v(116.09, -4.41) * mm, "end": v(117.5, -5) * mm});
            skLineSegment(sketch, "E18.6.14.6", {"start": v(117.5, -5) * mm, "end": v(122.5, -5) * mm});
            skArc(sketch, "E18.6.14.7", {"start": v(122.5, -5) * mm, "mid": v(123.91, -4.41) * mm, "end": v(124.5, -3) * mm});
            skLineSegment(sketch, "E18.7.0.0", {"start": v(135.5, 481.97) * mm, "end": v(135.5, 497.8) * mm});
            skLineSegment(sketch, "E18.7.0.1", {"start": v(144.5, 481.97) * mm, "end": v(144.5, 497.8) * mm});
            skPoint(sketch, "E18.7.0.2", {"position": v(144.5, 479.97) * mm});
            skPoint(sketch, "E18.7.0.3", {"position": v(135.5, 479.97) * mm});
            skLineSegment(sketch, "E18.7.0.4", {"start": v(135.5, 497.8) * mm, "end": v(144.5, 497.8) * mm});
            skArc(sketch, "E18.7.0.5", {"start": v(135.5, 481.97) * mm, "mid": v(136.09, 480.56) * mm, "end": v(137.5, 479.97) * mm});
            skLineSegment(sketch, "E18.7.0.6", {"start": v(137.5, 479.97) * mm, "end": v(142.5, 479.97) * mm});
            skArc(sketch, "E18.7.0.7", {"start": v(142.5, 479.97) * mm, "mid": v(143.91, 480.56) * mm, "end": v(144.5, 481.97) * mm});
            skLineSegment(sketch, "E18.7.1.0", {"start": v(135.5, 447.33) * mm, "end": v(135.5, 463.15) * mm});
            skLineSegment(sketch, "E18.7.1.1", {"start": v(144.5, 447.33) * mm, "end": v(144.5, 463.15) * mm});
            skPoint(sketch, "E18.7.1.2", {"position": v(144.5, 445.33) * mm});
            skPoint(sketch, "E18.7.1.3", {"position": v(135.5, 445.33) * mm});
            skLineSegment(sketch, "E18.7.1.4", {"start": v(135.5, 463.15) * mm, "end": v(144.5, 463.15) * mm});
            skArc(sketch, "E18.7.1.5", {"start": v(135.5, 447.33) * mm, "mid": v(136.09, 445.92) * mm, "end": v(137.5, 445.33) * mm});
            skLineSegment(sketch, "E18.7.1.6", {"start": v(137.5, 445.33) * mm, "end": v(142.5, 445.33) * mm});
            skArc(sketch, "E18.7.1.7", {"start": v(142.5, 445.33) * mm, "mid": v(143.91, 445.92) * mm, "end": v(144.5, 447.33) * mm});
            skLineSegment(sketch, "E18.7.2.0", {"start": v(135.5, 412.7) * mm, "end": v(135.5, 428.51) * mm});
            skLineSegment(sketch, "E18.7.2.1", {"start": v(144.5, 412.7) * mm, "end": v(144.5, 428.51) * mm});
            skPoint(sketch, "E18.7.2.2", {"position": v(144.5, 410.7) * mm});
            skPoint(sketch, "E18.7.2.3", {"position": v(135.5, 410.7) * mm});
            skLineSegment(sketch, "E18.7.2.4", {"start": v(135.5, 428.51) * mm, "end": v(144.5, 428.51) * mm});
            skArc(sketch, "E18.7.2.5", {"start": v(135.5, 412.7) * mm, "mid": v(136.09, 411.28) * mm, "end": v(137.5, 410.7) * mm});
            skLineSegment(sketch, "E18.7.2.6", {"start": v(137.5, 410.7) * mm, "end": v(142.5, 410.7) * mm});
            skArc(sketch, "E18.7.2.7", {"start": v(142.5, 410.7) * mm, "mid": v(143.91, 411.28) * mm, "end": v(144.5, 412.7) * mm});
            skLineSegment(sketch, "E18.7.3.0", {"start": v(135.5, 378.05) * mm, "end": v(135.5, 393.87) * mm});
            skLineSegment(sketch, "E18.7.3.1", {"start": v(144.5, 378.05) * mm, "end": v(144.5, 393.87) * mm});
            skPoint(sketch, "E18.7.3.2", {"position": v(144.5, 376.05) * mm});
            skPoint(sketch, "E18.7.3.3", {"position": v(135.5, 376.05) * mm});
            skLineSegment(sketch, "E18.7.3.4", {"start": v(135.5, 393.87) * mm, "end": v(144.5, 393.87) * mm});
            skArc(sketch, "E18.7.3.5", {"start": v(135.5, 378.05) * mm, "mid": v(136.09, 376.64) * mm, "end": v(137.5, 376.05) * mm});
            skLineSegment(sketch, "E18.7.3.6", {"start": v(137.5, 376.05) * mm, "end": v(142.5, 376.05) * mm});
            skArc(sketch, "E18.7.3.7", {"start": v(142.5, 376.05) * mm, "mid": v(143.91, 376.64) * mm, "end": v(144.5, 378.05) * mm});
            skLineSegment(sketch, "E18.7.4.0", {"start": v(135.5, 343.41) * mm, "end": v(135.5, 359.23) * mm});
            skLineSegment(sketch, "E18.7.4.1", {"start": v(144.5, 343.41) * mm, "end": v(144.5, 359.23) * mm});
            skPoint(sketch, "E18.7.4.2", {"position": v(144.5, 341.41) * mm});
            skPoint(sketch, "E18.7.4.3", {"position": v(135.5, 341.41) * mm});
            skLineSegment(sketch, "E18.7.4.4", {"start": v(135.5, 359.23) * mm, "end": v(144.5, 359.23) * mm});
            skArc(sketch, "E18.7.4.5", {"start": v(135.5, 343.41) * mm, "mid": v(136.09, 342) * mm, "end": v(137.5, 341.41) * mm});
            skLineSegment(sketch, "E18.7.4.6", {"start": v(137.5, 341.41) * mm, "end": v(142.5, 341.41) * mm});
            skArc(sketch, "E18.7.4.7", {"start": v(142.5, 341.41) * mm, "mid": v(143.91, 342) * mm, "end": v(144.5, 343.41) * mm});
            skLineSegment(sketch, "E18.7.5.0", {"start": v(135.5, 308.77) * mm, "end": v(135.5, 324.59) * mm});
            skLineSegment(sketch, "E18.7.5.1", {"start": v(144.5, 308.77) * mm, "end": v(144.5, 324.59) * mm});
            skPoint(sketch, "E18.7.5.2", {"position": v(144.5, 306.77) * mm});
            skPoint(sketch, "E18.7.5.3", {"position": v(135.5, 306.77) * mm});
            skLineSegment(sketch, "E18.7.5.4", {"start": v(135.5, 324.59) * mm, "end": v(144.5, 324.59) * mm});
            skArc(sketch, "E18.7.5.5", {"start": v(135.5, 308.77) * mm, "mid": v(136.09, 307.35) * mm, "end": v(137.5, 306.77) * mm});
            skLineSegment(sketch, "E18.7.5.6", {"start": v(137.5, 306.77) * mm, "end": v(142.5, 306.77) * mm});
            skArc(sketch, "E18.7.5.7", {"start": v(142.5, 306.77) * mm, "mid": v(143.91, 307.35) * mm, "end": v(144.5, 308.77) * mm});
            skLineSegment(sketch, "E18.7.6.0", {"start": v(135.5, 274.13) * mm, "end": v(135.5, 289.95) * mm});
            skLineSegment(sketch, "E18.7.6.1", {"start": v(144.5, 274.13) * mm, "end": v(144.5, 289.95) * mm});
            skPoint(sketch, "E18.7.6.2", {"position": v(144.5, 272.13) * mm});
            skPoint(sketch, "E18.7.6.3", {"position": v(135.5, 272.13) * mm});
            skLineSegment(sketch, "E18.7.6.4", {"start": v(135.5, 289.95) * mm, "end": v(144.5, 289.95) * mm});
            skArc(sketch, "E18.7.6.5", {"start": v(135.5, 274.13) * mm, "mid": v(136.09, 272.71) * mm, "end": v(137.5, 272.13) * mm});
            skLineSegment(sketch, "E18.7.6.6", {"start": v(137.5, 272.13) * mm, "end": v(142.5, 272.13) * mm});
            skArc(sketch, "E18.7.6.7", {"start": v(142.5, 272.13) * mm, "mid": v(143.91, 272.71) * mm, "end": v(144.5, 274.13) * mm});
            skLineSegment(sketch, "E18.7.7.0", {"start": v(135.5, 239.49) * mm, "end": v(135.5, 255.3) * mm});
            skLineSegment(sketch, "E18.7.7.1", {"start": v(144.5, 239.49) * mm, "end": v(144.5, 255.3) * mm});
            skPoint(sketch, "E18.7.7.2", {"position": v(144.5, 237.49) * mm});
            skPoint(sketch, "E18.7.7.3", {"position": v(135.5, 237.49) * mm});
            skLineSegment(sketch, "E18.7.7.4", {"start": v(135.5, 255.3) * mm, "end": v(144.5, 255.3) * mm});
            skArc(sketch, "E18.7.7.5", {"start": v(135.5, 239.49) * mm, "mid": v(136.09, 238.07) * mm, "end": v(137.5, 237.49) * mm});
            skLineSegment(sketch, "E18.7.7.6", {"start": v(137.5, 237.49) * mm, "end": v(142.5, 237.49) * mm});
            skArc(sketch, "E18.7.7.7", {"start": v(142.5, 237.49) * mm, "mid": v(143.91, 238.07) * mm, "end": v(144.5, 239.49) * mm});
            skLineSegment(sketch, "E18.7.8.0", {"start": v(135.5, 204.85) * mm, "end": v(135.5, 220.67) * mm});
            skLineSegment(sketch, "E18.7.8.1", {"start": v(144.5, 204.85) * mm, "end": v(144.5, 220.67) * mm});
            skPoint(sketch, "E18.7.8.2", {"position": v(144.5, 202.85) * mm});
            skPoint(sketch, "E18.7.8.3", {"position": v(135.5, 202.85) * mm});
            skLineSegment(sketch, "E18.7.8.4", {"start": v(135.5, 220.67) * mm, "end": v(144.5, 220.67) * mm});
            skArc(sketch, "E18.7.8.5", {"start": v(135.5, 204.85) * mm, "mid": v(136.09, 203.43) * mm, "end": v(137.5, 202.85) * mm});
            skLineSegment(sketch, "E18.7.8.6", {"start": v(137.5, 202.85) * mm, "end": v(142.5, 202.85) * mm});
            skArc(sketch, "E18.7.8.7", {"start": v(142.5, 202.85) * mm, "mid": v(143.91, 203.43) * mm, "end": v(144.5, 204.85) * mm});
            skLineSegment(sketch, "E18.7.9.0", {"start": v(135.5, 170.2) * mm, "end": v(135.5, 186.03) * mm});
            skLineSegment(sketch, "E18.7.9.1", {"start": v(144.5, 170.2) * mm, "end": v(144.5, 186.03) * mm});
            skPoint(sketch, "E18.7.9.2", {"position": v(144.5, 168.2) * mm});
            skPoint(sketch, "E18.7.9.3", {"position": v(135.5, 168.2) * mm});
            skLineSegment(sketch, "E18.7.9.4", {"start": v(135.5, 186.03) * mm, "end": v(144.5, 186.03) * mm});
            skArc(sketch, "E18.7.9.5", {"start": v(135.5, 170.2) * mm, "mid": v(136.09, 168.8) * mm, "end": v(137.5, 168.2) * mm});
            skLineSegment(sketch, "E18.7.9.6", {"start": v(137.5, 168.2) * mm, "end": v(142.5, 168.2) * mm});
            skArc(sketch, "E18.7.9.7", {"start": v(142.5, 168.2) * mm, "mid": v(143.91, 168.8) * mm, "end": v(144.5, 170.2) * mm});
            skLineSegment(sketch, "E18.7.10.0", {"start": v(135.5, 135.56) * mm, "end": v(135.5, 151.38) * mm});
            skLineSegment(sketch, "E18.7.10.1", {"start": v(144.5, 135.56) * mm, "end": v(144.5, 151.38) * mm});
            skPoint(sketch, "E18.7.10.2", {"position": v(144.5, 133.56) * mm});
            skPoint(sketch, "E18.7.10.3", {"position": v(135.5, 133.56) * mm});
            skLineSegment(sketch, "E18.7.10.4", {"start": v(135.5, 151.38) * mm, "end": v(144.5, 151.38) * mm});
            skArc(sketch, "E18.7.10.5", {"start": v(135.5, 135.56) * mm, "mid": v(136.09, 134.15) * mm, "end": v(137.5, 133.56) * mm});
            skLineSegment(sketch, "E18.7.10.6", {"start": v(137.5, 133.56) * mm, "end": v(142.5, 133.56) * mm});
            skArc(sketch, "E18.7.10.7", {"start": v(142.5, 133.56) * mm, "mid": v(143.91, 134.15) * mm, "end": v(144.5, 135.56) * mm});
            skLineSegment(sketch, "E18.7.11.0", {"start": v(135.5, 100.92) * mm, "end": v(135.5, 116.74) * mm});
            skLineSegment(sketch, "E18.7.11.1", {"start": v(144.5, 100.92) * mm, "end": v(144.5, 116.74) * mm});
            skPoint(sketch, "E18.7.11.2", {"position": v(144.5, 98.92) * mm});
            skPoint(sketch, "E18.7.11.3", {"position": v(135.5, 98.92) * mm});
            skLineSegment(sketch, "E18.7.11.4", {"start": v(135.5, 116.74) * mm, "end": v(144.5, 116.74) * mm});
            skArc(sketch, "E18.7.11.5", {"start": v(135.5, 100.92) * mm, "mid": v(136.09, 99.5) * mm, "end": v(137.5, 98.92) * mm});
            skLineSegment(sketch, "E18.7.11.6", {"start": v(137.5, 98.92) * mm, "end": v(142.5, 98.92) * mm});
            skArc(sketch, "E18.7.11.7", {"start": v(142.5, 98.92) * mm, "mid": v(143.91, 99.5) * mm, "end": v(144.5, 100.92) * mm});
            skLineSegment(sketch, "E18.7.12.0", {"start": v(135.5, 66.28) * mm, "end": v(135.5, 82.1) * mm});
            skLineSegment(sketch, "E18.7.12.1", {"start": v(144.5, 66.28) * mm, "end": v(144.5, 82.1) * mm});
            skPoint(sketch, "E18.7.12.2", {"position": v(144.5, 64.28) * mm});
            skPoint(sketch, "E18.7.12.3", {"position": v(135.5, 64.28) * mm});
            skLineSegment(sketch, "E18.7.12.4", {"start": v(135.5, 82.1) * mm, "end": v(144.5, 82.1) * mm});
            skArc(sketch, "E18.7.12.5", {"start": v(135.5, 66.28) * mm, "mid": v(136.09, 64.87) * mm, "end": v(137.5, 64.28) * mm});
            skLineSegment(sketch, "E18.7.12.6", {"start": v(137.5, 64.28) * mm, "end": v(142.5, 64.28) * mm});
            skArc(sketch, "E18.7.12.7", {"start": v(142.5, 64.28) * mm, "mid": v(143.91, 64.87) * mm, "end": v(144.5, 66.28) * mm});
            skLineSegment(sketch, "E18.7.13.0", {"start": v(135.5, 31.64) * mm, "end": v(135.5, 47.46) * mm});
            skLineSegment(sketch, "E18.7.13.1", {"start": v(144.5, 31.64) * mm, "end": v(144.5, 47.46) * mm});
            skPoint(sketch, "E18.7.13.2", {"position": v(144.5, 29.64) * mm});
            skPoint(sketch, "E18.7.13.3", {"position": v(135.5, 29.64) * mm});
            skLineSegment(sketch, "E18.7.13.4", {"start": v(135.5, 47.46) * mm, "end": v(144.5, 47.46) * mm});
            skArc(sketch, "E18.7.13.5", {"start": v(135.5, 31.64) * mm, "mid": v(136.09, 30.23) * mm, "end": v(137.5, 29.64) * mm});
            skLineSegment(sketch, "E18.7.13.6", {"start": v(137.5, 29.64) * mm, "end": v(142.5, 29.64) * mm});
            skArc(sketch, "E18.7.13.7", {"start": v(142.5, 29.64) * mm, "mid": v(143.91, 30.23) * mm, "end": v(144.5, 31.64) * mm});
            skLineSegment(sketch, "E18.7.14.0", {"start": v(135.5, -3) * mm, "end": v(135.5, 12.82) * mm});
            skLineSegment(sketch, "E18.7.14.1", {"start": v(144.5, -3) * mm, "end": v(144.5, 12.82) * mm});
            skPoint(sketch, "E18.7.14.2", {"position": v(144.5, -5) * mm});
            skPoint(sketch, "E18.7.14.3", {"position": v(135.5, -5) * mm});
            skLineSegment(sketch, "E18.7.14.4", {"start": v(135.5, 12.82) * mm, "end": v(144.5, 12.82) * mm});
            skArc(sketch, "E18.7.14.5", {"start": v(135.5, -3) * mm, "mid": v(136.09, -4.41) * mm, "end": v(137.5, -5) * mm});
            skLineSegment(sketch, "E18.7.14.6", {"start": v(137.5, -5) * mm, "end": v(142.5, -5) * mm});
            skArc(sketch, "E18.7.14.7", {"start": v(142.5, -5) * mm, "mid": v(143.91, -4.41) * mm, "end": v(144.5, -3) * mm});
            skLineSegment(sketch, "E18.8.0.0", {"start": v(155.5, 481.97) * mm, "end": v(155.5, 497.8) * mm});
            skLineSegment(sketch, "E18.8.0.1", {"start": v(164.5, 481.97) * mm, "end": v(164.5, 497.8) * mm});
            skPoint(sketch, "E18.8.0.2", {"position": v(164.5, 479.97) * mm});
            skPoint(sketch, "E18.8.0.3", {"position": v(155.5, 479.97) * mm});
            skLineSegment(sketch, "E18.8.0.4", {"start": v(155.5, 497.8) * mm, "end": v(164.5, 497.8) * mm});
            skArc(sketch, "E18.8.0.5", {"start": v(155.5, 481.97) * mm, "mid": v(156.09, 480.56) * mm, "end": v(157.5, 479.97) * mm});
            skLineSegment(sketch, "E18.8.0.6", {"start": v(157.5, 479.97) * mm, "end": v(162.5, 479.97) * mm});
            skArc(sketch, "E18.8.0.7", {"start": v(162.5, 479.97) * mm, "mid": v(163.91, 480.56) * mm, "end": v(164.5, 481.97) * mm});
            skLineSegment(sketch, "E18.8.1.0", {"start": v(155.5, 447.33) * mm, "end": v(155.5, 463.15) * mm});
            skLineSegment(sketch, "E18.8.1.1", {"start": v(164.5, 447.33) * mm, "end": v(164.5, 463.15) * mm});
            skPoint(sketch, "E18.8.1.2", {"position": v(164.5, 445.33) * mm});
            skPoint(sketch, "E18.8.1.3", {"position": v(155.5, 445.33) * mm});
            skLineSegment(sketch, "E18.8.1.4", {"start": v(155.5, 463.15) * mm, "end": v(164.5, 463.15) * mm});
            skArc(sketch, "E18.8.1.5", {"start": v(155.5, 447.33) * mm, "mid": v(156.09, 445.92) * mm, "end": v(157.5, 445.33) * mm});
            skLineSegment(sketch, "E18.8.1.6", {"start": v(157.5, 445.33) * mm, "end": v(162.5, 445.33) * mm});
            skArc(sketch, "E18.8.1.7", {"start": v(162.5, 445.33) * mm, "mid": v(163.91, 445.92) * mm, "end": v(164.5, 447.33) * mm});
            skLineSegment(sketch, "E18.8.2.0", {"start": v(155.5, 412.7) * mm, "end": v(155.5, 428.51) * mm});
            skLineSegment(sketch, "E18.8.2.1", {"start": v(164.5, 412.7) * mm, "end": v(164.5, 428.51) * mm});
            skPoint(sketch, "E18.8.2.2", {"position": v(164.5, 410.7) * mm});
            skPoint(sketch, "E18.8.2.3", {"position": v(155.5, 410.7) * mm});
            skLineSegment(sketch, "E18.8.2.4", {"start": v(155.5, 428.51) * mm, "end": v(164.5, 428.51) * mm});
            skArc(sketch, "E18.8.2.5", {"start": v(155.5, 412.7) * mm, "mid": v(156.09, 411.28) * mm, "end": v(157.5, 410.7) * mm});
            skLineSegment(sketch, "E18.8.2.6", {"start": v(157.5, 410.7) * mm, "end": v(162.5, 410.7) * mm});
            skArc(sketch, "E18.8.2.7", {"start": v(162.5, 410.7) * mm, "mid": v(163.91, 411.28) * mm, "end": v(164.5, 412.7) * mm});
            skLineSegment(sketch, "E18.8.3.0", {"start": v(155.5, 378.05) * mm, "end": v(155.5, 393.87) * mm});
            skLineSegment(sketch, "E18.8.3.1", {"start": v(164.5, 378.05) * mm, "end": v(164.5, 393.87) * mm});
            skPoint(sketch, "E18.8.3.2", {"position": v(164.5, 376.05) * mm});
            skPoint(sketch, "E18.8.3.3", {"position": v(155.5, 376.05) * mm});
            skLineSegment(sketch, "E18.8.3.4", {"start": v(155.5, 393.87) * mm, "end": v(164.5, 393.87) * mm});
            skArc(sketch, "E18.8.3.5", {"start": v(155.5, 378.05) * mm, "mid": v(156.09, 376.64) * mm, "end": v(157.5, 376.05) * mm});
            skLineSegment(sketch, "E18.8.3.6", {"start": v(157.5, 376.05) * mm, "end": v(162.5, 376.05) * mm});
            skArc(sketch, "E18.8.3.7", {"start": v(162.5, 376.05) * mm, "mid": v(163.91, 376.64) * mm, "end": v(164.5, 378.05) * mm});
            skLineSegment(sketch, "E18.8.4.0", {"start": v(155.5, 343.41) * mm, "end": v(155.5, 359.23) * mm});
            skLineSegment(sketch, "E18.8.4.1", {"start": v(164.5, 343.41) * mm, "end": v(164.5, 359.23) * mm});
            skPoint(sketch, "E18.8.4.2", {"position": v(164.5, 341.41) * mm});
            skPoint(sketch, "E18.8.4.3", {"position": v(155.5, 341.41) * mm});
            skLineSegment(sketch, "E18.8.4.4", {"start": v(155.5, 359.23) * mm, "end": v(164.5, 359.23) * mm});
            skArc(sketch, "E18.8.4.5", {"start": v(155.5, 343.41) * mm, "mid": v(156.09, 342) * mm, "end": v(157.5, 341.41) * mm});
            skLineSegment(sketch, "E18.8.4.6", {"start": v(157.5, 341.41) * mm, "end": v(162.5, 341.41) * mm});
            skArc(sketch, "E18.8.4.7", {"start": v(162.5, 341.41) * mm, "mid": v(163.91, 342) * mm, "end": v(164.5, 343.41) * mm});
            skLineSegment(sketch, "E18.8.5.0", {"start": v(155.5, 308.77) * mm, "end": v(155.5, 324.59) * mm});
            skLineSegment(sketch, "E18.8.5.1", {"start": v(164.5, 308.77) * mm, "end": v(164.5, 324.59) * mm});
            skPoint(sketch, "E18.8.5.2", {"position": v(164.5, 306.77) * mm});
            skPoint(sketch, "E18.8.5.3", {"position": v(155.5, 306.77) * mm});
            skLineSegment(sketch, "E18.8.5.4", {"start": v(155.5, 324.59) * mm, "end": v(164.5, 324.59) * mm});
            skArc(sketch, "E18.8.5.5", {"start": v(155.5, 308.77) * mm, "mid": v(156.09, 307.35) * mm, "end": v(157.5, 306.77) * mm});
            skLineSegment(sketch, "E18.8.5.6", {"start": v(157.5, 306.77) * mm, "end": v(162.5, 306.77) * mm});
            skArc(sketch, "E18.8.5.7", {"start": v(162.5, 306.77) * mm, "mid": v(163.91, 307.35) * mm, "end": v(164.5, 308.77) * mm});
            skLineSegment(sketch, "E18.8.6.0", {"start": v(155.5, 274.13) * mm, "end": v(155.5, 289.95) * mm});
            skLineSegment(sketch, "E18.8.6.1", {"start": v(164.5, 274.13) * mm, "end": v(164.5, 289.95) * mm});
            skPoint(sketch, "E18.8.6.2", {"position": v(164.5, 272.13) * mm});
            skPoint(sketch, "E18.8.6.3", {"position": v(155.5, 272.13) * mm});
            skLineSegment(sketch, "E18.8.6.4", {"start": v(155.5, 289.95) * mm, "end": v(164.5, 289.95) * mm});
            skArc(sketch, "E18.8.6.5", {"start": v(155.5, 274.13) * mm, "mid": v(156.09, 272.71) * mm, "end": v(157.5, 272.13) * mm});
            skLineSegment(sketch, "E18.8.6.6", {"start": v(157.5, 272.13) * mm, "end": v(162.5, 272.13) * mm});
            skArc(sketch, "E18.8.6.7", {"start": v(162.5, 272.13) * mm, "mid": v(163.91, 272.71) * mm, "end": v(164.5, 274.13) * mm});
            skLineSegment(sketch, "E18.8.7.0", {"start": v(155.5, 239.49) * mm, "end": v(155.5, 255.3) * mm});
            skLineSegment(sketch, "E18.8.7.1", {"start": v(164.5, 239.49) * mm, "end": v(164.5, 255.3) * mm});
            skPoint(sketch, "E18.8.7.2", {"position": v(164.5, 237.49) * mm});
            skPoint(sketch, "E18.8.7.3", {"position": v(155.5, 237.49) * mm});
            skLineSegment(sketch, "E18.8.7.4", {"start": v(155.5, 255.3) * mm, "end": v(164.5, 255.3) * mm});
            skArc(sketch, "E18.8.7.5", {"start": v(155.5, 239.49) * mm, "mid": v(156.09, 238.07) * mm, "end": v(157.5, 237.49) * mm});
            skLineSegment(sketch, "E18.8.7.6", {"start": v(157.5, 237.49) * mm, "end": v(162.5, 237.49) * mm});
            skArc(sketch, "E18.8.7.7", {"start": v(162.5, 237.49) * mm, "mid": v(163.91, 238.07) * mm, "end": v(164.5, 239.49) * mm});
            skLineSegment(sketch, "E18.8.8.0", {"start": v(155.5, 204.85) * mm, "end": v(155.5, 220.67) * mm});
            skLineSegment(sketch, "E18.8.8.1", {"start": v(164.5, 204.85) * mm, "end": v(164.5, 220.67) * mm});
            skPoint(sketch, "E18.8.8.2", {"position": v(164.5, 202.85) * mm});
            skPoint(sketch, "E18.8.8.3", {"position": v(155.5, 202.85) * mm});
            skLineSegment(sketch, "E18.8.8.4", {"start": v(155.5, 220.67) * mm, "end": v(164.5, 220.67) * mm});
            skArc(sketch, "E18.8.8.5", {"start": v(155.5, 204.85) * mm, "mid": v(156.09, 203.43) * mm, "end": v(157.5, 202.85) * mm});
            skLineSegment(sketch, "E18.8.8.6", {"start": v(157.5, 202.85) * mm, "end": v(162.5, 202.85) * mm});
            skArc(sketch, "E18.8.8.7", {"start": v(162.5, 202.85) * mm, "mid": v(163.91, 203.43) * mm, "end": v(164.5, 204.85) * mm});
            skLineSegment(sketch, "E18.8.9.0", {"start": v(155.5, 170.2) * mm, "end": v(155.5, 186.03) * mm});
            skLineSegment(sketch, "E18.8.9.1", {"start": v(164.5, 170.2) * mm, "end": v(164.5, 186.03) * mm});
            skPoint(sketch, "E18.8.9.2", {"position": v(164.5, 168.2) * mm});
            skPoint(sketch, "E18.8.9.3", {"position": v(155.5, 168.2) * mm});
            skLineSegment(sketch, "E18.8.9.4", {"start": v(155.5, 186.03) * mm, "end": v(164.5, 186.03) * mm});
            skArc(sketch, "E18.8.9.5", {"start": v(155.5, 170.2) * mm, "mid": v(156.09, 168.8) * mm, "end": v(157.5, 168.2) * mm});
            skLineSegment(sketch, "E18.8.9.6", {"start": v(157.5, 168.2) * mm, "end": v(162.5, 168.2) * mm});
            skArc(sketch, "E18.8.9.7", {"start": v(162.5, 168.2) * mm, "mid": v(163.91, 168.8) * mm, "end": v(164.5, 170.2) * mm});
            skLineSegment(sketch, "E18.8.10.0", {"start": v(155.5, 135.56) * mm, "end": v(155.5, 151.38) * mm});
            skLineSegment(sketch, "E18.8.10.1", {"start": v(164.5, 135.56) * mm, "end": v(164.5, 151.38) * mm});
            skPoint(sketch, "E18.8.10.2", {"position": v(164.5, 133.56) * mm});
            skPoint(sketch, "E18.8.10.3", {"position": v(155.5, 133.56) * mm});
            skLineSegment(sketch, "E18.8.10.4", {"start": v(155.5, 151.38) * mm, "end": v(164.5, 151.38) * mm});
            skArc(sketch, "E18.8.10.5", {"start": v(155.5, 135.56) * mm, "mid": v(156.09, 134.15) * mm, "end": v(157.5, 133.56) * mm});
            skLineSegment(sketch, "E18.8.10.6", {"start": v(157.5, 133.56) * mm, "end": v(162.5, 133.56) * mm});
            skArc(sketch, "E18.8.10.7", {"start": v(162.5, 133.56) * mm, "mid": v(163.91, 134.15) * mm, "end": v(164.5, 135.56) * mm});
            skLineSegment(sketch, "E18.8.11.0", {"start": v(155.5, 100.92) * mm, "end": v(155.5, 116.74) * mm});
            skLineSegment(sketch, "E18.8.11.1", {"start": v(164.5, 100.92) * mm, "end": v(164.5, 116.74) * mm});
            skPoint(sketch, "E18.8.11.2", {"position": v(164.5, 98.92) * mm});
            skPoint(sketch, "E18.8.11.3", {"position": v(155.5, 98.92) * mm});
            skLineSegment(sketch, "E18.8.11.4", {"start": v(155.5, 116.74) * mm, "end": v(164.5, 116.74) * mm});
            skArc(sketch, "E18.8.11.5", {"start": v(155.5, 100.92) * mm, "mid": v(156.09, 99.5) * mm, "end": v(157.5, 98.92) * mm});
            skLineSegment(sketch, "E18.8.11.6", {"start": v(157.5, 98.92) * mm, "end": v(162.5, 98.92) * mm});
            skArc(sketch, "E18.8.11.7", {"start": v(162.5, 98.92) * mm, "mid": v(163.91, 99.5) * mm, "end": v(164.5, 100.92) * mm});
            skLineSegment(sketch, "E18.8.12.0", {"start": v(155.5, 66.28) * mm, "end": v(155.5, 82.1) * mm});
            skLineSegment(sketch, "E18.8.12.1", {"start": v(164.5, 66.28) * mm, "end": v(164.5, 82.1) * mm});
            skPoint(sketch, "E18.8.12.2", {"position": v(164.5, 64.28) * mm});
            skPoint(sketch, "E18.8.12.3", {"position": v(155.5, 64.28) * mm});
            skLineSegment(sketch, "E18.8.12.4", {"start": v(155.5, 82.1) * mm, "end": v(164.5, 82.1) * mm});
            skArc(sketch, "E18.8.12.5", {"start": v(155.5, 66.28) * mm, "mid": v(156.09, 64.87) * mm, "end": v(157.5, 64.28) * mm});
            skLineSegment(sketch, "E18.8.12.6", {"start": v(157.5, 64.28) * mm, "end": v(162.5, 64.28) * mm});
            skArc(sketch, "E18.8.12.7", {"start": v(162.5, 64.28) * mm, "mid": v(163.91, 64.87) * mm, "end": v(164.5, 66.28) * mm});
            skLineSegment(sketch, "E18.8.13.0", {"start": v(155.5, 31.64) * mm, "end": v(155.5, 47.46) * mm});
            skLineSegment(sketch, "E18.8.13.1", {"start": v(164.5, 31.64) * mm, "end": v(164.5, 47.46) * mm});
            skPoint(sketch, "E18.8.13.2", {"position": v(164.5, 29.64) * mm});
            skPoint(sketch, "E18.8.13.3", {"position": v(155.5, 29.64) * mm});
            skLineSegment(sketch, "E18.8.13.4", {"start": v(155.5, 47.46) * mm, "end": v(164.5, 47.46) * mm});
            skArc(sketch, "E18.8.13.5", {"start": v(155.5, 31.64) * mm, "mid": v(156.09, 30.23) * mm, "end": v(157.5, 29.64) * mm});
            skLineSegment(sketch, "E18.8.13.6", {"start": v(157.5, 29.64) * mm, "end": v(162.5, 29.64) * mm});
            skArc(sketch, "E18.8.13.7", {"start": v(162.5, 29.64) * mm, "mid": v(163.91, 30.23) * mm, "end": v(164.5, 31.64) * mm});
            skLineSegment(sketch, "E18.8.14.0", {"start": v(155.5, -3) * mm, "end": v(155.5, 12.82) * mm});
            skLineSegment(sketch, "E18.8.14.1", {"start": v(164.5, -3) * mm, "end": v(164.5, 12.82) * mm});
            skPoint(sketch, "E18.8.14.2", {"position": v(164.5, -5) * mm});
            skPoint(sketch, "E18.8.14.3", {"position": v(155.5, -5) * mm});
            skLineSegment(sketch, "E18.8.14.4", {"start": v(155.5, 12.82) * mm, "end": v(164.5, 12.82) * mm});
            skArc(sketch, "E18.8.14.5", {"start": v(155.5, -3) * mm, "mid": v(156.09, -4.41) * mm, "end": v(157.5, -5) * mm});
            skLineSegment(sketch, "E18.8.14.6", {"start": v(157.5, -5) * mm, "end": v(162.5, -5) * mm});
            skArc(sketch, "E18.8.14.7", {"start": v(162.5, -5) * mm, "mid": v(163.91, -4.41) * mm, "end": v(164.5, -3) * mm});
            skLineSegment(sketch, "E18.9.0.0", {"start": v(175.5, 481.97) * mm, "end": v(175.5, 497.8) * mm});
            skLineSegment(sketch, "E18.9.0.1", {"start": v(184.5, 481.97) * mm, "end": v(184.5, 497.8) * mm});
            skPoint(sketch, "E18.9.0.2", {"position": v(184.5, 479.97) * mm});
            skPoint(sketch, "E18.9.0.3", {"position": v(175.5, 479.97) * mm});
            skLineSegment(sketch, "E18.9.0.4", {"start": v(175.5, 497.8) * mm, "end": v(184.5, 497.8) * mm});
            skArc(sketch, "E18.9.0.5", {"start": v(175.5, 481.97) * mm, "mid": v(176.09, 480.56) * mm, "end": v(177.5, 479.97) * mm});
            skLineSegment(sketch, "E18.9.0.6", {"start": v(177.5, 479.97) * mm, "end": v(182.5, 479.97) * mm});
            skArc(sketch, "E18.9.0.7", {"start": v(182.5, 479.97) * mm, "mid": v(183.91, 480.56) * mm, "end": v(184.5, 481.97) * mm});
            skLineSegment(sketch, "E18.9.1.0", {"start": v(175.5, 447.33) * mm, "end": v(175.5, 463.15) * mm});
            skLineSegment(sketch, "E18.9.1.1", {"start": v(184.5, 447.33) * mm, "end": v(184.5, 463.15) * mm});
            skPoint(sketch, "E18.9.1.2", {"position": v(184.5, 445.33) * mm});
            skPoint(sketch, "E18.9.1.3", {"position": v(175.5, 445.33) * mm});
            skLineSegment(sketch, "E18.9.1.4", {"start": v(175.5, 463.15) * mm, "end": v(184.5, 463.15) * mm});
            skArc(sketch, "E18.9.1.5", {"start": v(175.5, 447.33) * mm, "mid": v(176.09, 445.92) * mm, "end": v(177.5, 445.33) * mm});
            skLineSegment(sketch, "E18.9.1.6", {"start": v(177.5, 445.33) * mm, "end": v(182.5, 445.33) * mm});
            skArc(sketch, "E18.9.1.7", {"start": v(182.5, 445.33) * mm, "mid": v(183.91, 445.92) * mm, "end": v(184.5, 447.33) * mm});
            skLineSegment(sketch, "E18.9.2.0", {"start": v(175.5, 412.7) * mm, "end": v(175.5, 428.51) * mm});
            skLineSegment(sketch, "E18.9.2.1", {"start": v(184.5, 412.7) * mm, "end": v(184.5, 428.51) * mm});
            skPoint(sketch, "E18.9.2.2", {"position": v(184.5, 410.7) * mm});
            skPoint(sketch, "E18.9.2.3", {"position": v(175.5, 410.7) * mm});
            skLineSegment(sketch, "E18.9.2.4", {"start": v(175.5, 428.51) * mm, "end": v(184.5, 428.51) * mm});
            skArc(sketch, "E18.9.2.5", {"start": v(175.5, 412.7) * mm, "mid": v(176.09, 411.28) * mm, "end": v(177.5, 410.7) * mm});
            skLineSegment(sketch, "E18.9.2.6", {"start": v(177.5, 410.7) * mm, "end": v(182.5, 410.7) * mm});
            skArc(sketch, "E18.9.2.7", {"start": v(182.5, 410.7) * mm, "mid": v(183.91, 411.28) * mm, "end": v(184.5, 412.7) * mm});
            skLineSegment(sketch, "E18.9.3.0", {"start": v(175.5, 378.05) * mm, "end": v(175.5, 393.87) * mm});
            skLineSegment(sketch, "E18.9.3.1", {"start": v(184.5, 378.05) * mm, "end": v(184.5, 393.87) * mm});
            skPoint(sketch, "E18.9.3.2", {"position": v(184.5, 376.05) * mm});
            skPoint(sketch, "E18.9.3.3", {"position": v(175.5, 376.05) * mm});
            skLineSegment(sketch, "E18.9.3.4", {"start": v(175.5, 393.87) * mm, "end": v(184.5, 393.87) * mm});
            skArc(sketch, "E18.9.3.5", {"start": v(175.5, 378.05) * mm, "mid": v(176.09, 376.64) * mm, "end": v(177.5, 376.05) * mm});
            skLineSegment(sketch, "E18.9.3.6", {"start": v(177.5, 376.05) * mm, "end": v(182.5, 376.05) * mm});
            skArc(sketch, "E18.9.3.7", {"start": v(182.5, 376.05) * mm, "mid": v(183.91, 376.64) * mm, "end": v(184.5, 378.05) * mm});
            skLineSegment(sketch, "E18.9.4.0", {"start": v(175.5, 343.41) * mm, "end": v(175.5, 359.23) * mm});
            skLineSegment(sketch, "E18.9.4.1", {"start": v(184.5, 343.41) * mm, "end": v(184.5, 359.23) * mm});
            skPoint(sketch, "E18.9.4.2", {"position": v(184.5, 341.41) * mm});
            skPoint(sketch, "E18.9.4.3", {"position": v(175.5, 341.41) * mm});
            skLineSegment(sketch, "E18.9.4.4", {"start": v(175.5, 359.23) * mm, "end": v(184.5, 359.23) * mm});
            skArc(sketch, "E18.9.4.5", {"start": v(175.5, 343.41) * mm, "mid": v(176.09, 342) * mm, "end": v(177.5, 341.41) * mm});
            skLineSegment(sketch, "E18.9.4.6", {"start": v(177.5, 341.41) * mm, "end": v(182.5, 341.41) * mm});
            skArc(sketch, "E18.9.4.7", {"start": v(182.5, 341.41) * mm, "mid": v(183.91, 342) * mm, "end": v(184.5, 343.41) * mm});
            skLineSegment(sketch, "E18.9.5.0", {"start": v(175.5, 308.77) * mm, "end": v(175.5, 324.59) * mm});
            skLineSegment(sketch, "E18.9.5.1", {"start": v(184.5, 308.77) * mm, "end": v(184.5, 324.59) * mm});
            skPoint(sketch, "E18.9.5.2", {"position": v(184.5, 306.77) * mm});
            skPoint(sketch, "E18.9.5.3", {"position": v(175.5, 306.77) * mm});
            skLineSegment(sketch, "E18.9.5.4", {"start": v(175.5, 324.59) * mm, "end": v(184.5, 324.59) * mm});
            skArc(sketch, "E18.9.5.5", {"start": v(175.5, 308.77) * mm, "mid": v(176.09, 307.35) * mm, "end": v(177.5, 306.77) * mm});
            skLineSegment(sketch, "E18.9.5.6", {"start": v(177.5, 306.77) * mm, "end": v(182.5, 306.77) * mm});
            skArc(sketch, "E18.9.5.7", {"start": v(182.5, 306.77) * mm, "mid": v(183.91, 307.35) * mm, "end": v(184.5, 308.77) * mm});
            skLineSegment(sketch, "E18.9.6.0", {"start": v(175.5, 274.13) * mm, "end": v(175.5, 289.95) * mm});
            skLineSegment(sketch, "E18.9.6.1", {"start": v(184.5, 274.13) * mm, "end": v(184.5, 289.95) * mm});
            skPoint(sketch, "E18.9.6.2", {"position": v(184.5, 272.13) * mm});
            skPoint(sketch, "E18.9.6.3", {"position": v(175.5, 272.13) * mm});
            skLineSegment(sketch, "E18.9.6.4", {"start": v(175.5, 289.95) * mm, "end": v(184.5, 289.95) * mm});
            skArc(sketch, "E18.9.6.5", {"start": v(175.5, 274.13) * mm, "mid": v(176.09, 272.71) * mm, "end": v(177.5, 272.13) * mm});
            skLineSegment(sketch, "E18.9.6.6", {"start": v(177.5, 272.13) * mm, "end": v(182.5, 272.13) * mm});
            skArc(sketch, "E18.9.6.7", {"start": v(182.5, 272.13) * mm, "mid": v(183.91, 272.71) * mm, "end": v(184.5, 274.13) * mm});
            skLineSegment(sketch, "E18.9.7.0", {"start": v(175.5, 239.49) * mm, "end": v(175.5, 255.3) * mm});
            skLineSegment(sketch, "E18.9.7.1", {"start": v(184.5, 239.49) * mm, "end": v(184.5, 255.3) * mm});
            skPoint(sketch, "E18.9.7.2", {"position": v(184.5, 237.49) * mm});
            skPoint(sketch, "E18.9.7.3", {"position": v(175.5, 237.49) * mm});
            skLineSegment(sketch, "E18.9.7.4", {"start": v(175.5, 255.3) * mm, "end": v(184.5, 255.3) * mm});
            skArc(sketch, "E18.9.7.5", {"start": v(175.5, 239.49) * mm, "mid": v(176.09, 238.07) * mm, "end": v(177.5, 237.49) * mm});
            skLineSegment(sketch, "E18.9.7.6", {"start": v(177.5, 237.49) * mm, "end": v(182.5, 237.49) * mm});
            skArc(sketch, "E18.9.7.7", {"start": v(182.5, 237.49) * mm, "mid": v(183.91, 238.07) * mm, "end": v(184.5, 239.49) * mm});
            skLineSegment(sketch, "E18.9.8.0", {"start": v(175.5, 204.85) * mm, "end": v(175.5, 220.67) * mm});
            skLineSegment(sketch, "E18.9.8.1", {"start": v(184.5, 204.85) * mm, "end": v(184.5, 220.67) * mm});
            skPoint(sketch, "E18.9.8.2", {"position": v(184.5, 202.85) * mm});
            skPoint(sketch, "E18.9.8.3", {"position": v(175.5, 202.85) * mm});
            skLineSegment(sketch, "E18.9.8.4", {"start": v(175.5, 220.67) * mm, "end": v(184.5, 220.67) * mm});
            skArc(sketch, "E18.9.8.5", {"start": v(175.5, 204.85) * mm, "mid": v(176.09, 203.43) * mm, "end": v(177.5, 202.85) * mm});
            skLineSegment(sketch, "E18.9.8.6", {"start": v(177.5, 202.85) * mm, "end": v(182.5, 202.85) * mm});
            skArc(sketch, "E18.9.8.7", {"start": v(182.5, 202.85) * mm, "mid": v(183.91, 203.43) * mm, "end": v(184.5, 204.85) * mm});
            skLineSegment(sketch, "E18.9.9.0", {"start": v(175.5, 170.2) * mm, "end": v(175.5, 186.03) * mm});
            skLineSegment(sketch, "E18.9.9.1", {"start": v(184.5, 170.2) * mm, "end": v(184.5, 186.03) * mm});
            skPoint(sketch, "E18.9.9.2", {"position": v(184.5, 168.2) * mm});
            skPoint(sketch, "E18.9.9.3", {"position": v(175.5, 168.2) * mm});
            skLineSegment(sketch, "E18.9.9.4", {"start": v(175.5, 186.03) * mm, "end": v(184.5, 186.03) * mm});
            skArc(sketch, "E18.9.9.5", {"start": v(175.5, 170.2) * mm, "mid": v(176.09, 168.8) * mm, "end": v(177.5, 168.2) * mm});
            skLineSegment(sketch, "E18.9.9.6", {"start": v(177.5, 168.2) * mm, "end": v(182.5, 168.2) * mm});
            skArc(sketch, "E18.9.9.7", {"start": v(182.5, 168.2) * mm, "mid": v(183.91, 168.8) * mm, "end": v(184.5, 170.2) * mm});
            skLineSegment(sketch, "E18.9.10.0", {"start": v(175.5, 135.56) * mm, "end": v(175.5, 151.38) * mm});
            skLineSegment(sketch, "E18.9.10.1", {"start": v(184.5, 135.56) * mm, "end": v(184.5, 151.38) * mm});
            skPoint(sketch, "E18.9.10.2", {"position": v(184.5, 133.56) * mm});
            skPoint(sketch, "E18.9.10.3", {"position": v(175.5, 133.56) * mm});
            skLineSegment(sketch, "E18.9.10.4", {"start": v(175.5, 151.38) * mm, "end": v(184.5, 151.38) * mm});
            skArc(sketch, "E18.9.10.5", {"start": v(175.5, 135.56) * mm, "mid": v(176.09, 134.15) * mm, "end": v(177.5, 133.56) * mm});
            skLineSegment(sketch, "E18.9.10.6", {"start": v(177.5, 133.56) * mm, "end": v(182.5, 133.56) * mm});
            skArc(sketch, "E18.9.10.7", {"start": v(182.5, 133.56) * mm, "mid": v(183.91, 134.15) * mm, "end": v(184.5, 135.56) * mm});
            skLineSegment(sketch, "E18.9.11.0", {"start": v(175.5, 100.92) * mm, "end": v(175.5, 116.74) * mm});
            skLineSegment(sketch, "E18.9.11.1", {"start": v(184.5, 100.92) * mm, "end": v(184.5, 116.74) * mm});
            skPoint(sketch, "E18.9.11.2", {"position": v(184.5, 98.92) * mm});
            skPoint(sketch, "E18.9.11.3", {"position": v(175.5, 98.92) * mm});
            skLineSegment(sketch, "E18.9.11.4", {"start": v(175.5, 116.74) * mm, "end": v(184.5, 116.74) * mm});
            skArc(sketch, "E18.9.11.5", {"start": v(175.5, 100.92) * mm, "mid": v(176.09, 99.5) * mm, "end": v(177.5, 98.92) * mm});
            skLineSegment(sketch, "E18.9.11.6", {"start": v(177.5, 98.92) * mm, "end": v(182.5, 98.92) * mm});
            skArc(sketch, "E18.9.11.7", {"start": v(182.5, 98.92) * mm, "mid": v(183.91, 99.5) * mm, "end": v(184.5, 100.92) * mm});
            skLineSegment(sketch, "E18.9.12.0", {"start": v(175.5, 66.28) * mm, "end": v(175.5, 82.1) * mm});
            skLineSegment(sketch, "E18.9.12.1", {"start": v(184.5, 66.28) * mm, "end": v(184.5, 82.1) * mm});
            skPoint(sketch, "E18.9.12.2", {"position": v(184.5, 64.28) * mm});
            skPoint(sketch, "E18.9.12.3", {"position": v(175.5, 64.28) * mm});
            skLineSegment(sketch, "E18.9.12.4", {"start": v(175.5, 82.1) * mm, "end": v(184.5, 82.1) * mm});
            skArc(sketch, "E18.9.12.5", {"start": v(175.5, 66.28) * mm, "mid": v(176.09, 64.87) * mm, "end": v(177.5, 64.28) * mm});
            skLineSegment(sketch, "E18.9.12.6", {"start": v(177.5, 64.28) * mm, "end": v(182.5, 64.28) * mm});
            skArc(sketch, "E18.9.12.7", {"start": v(182.5, 64.28) * mm, "mid": v(183.91, 64.87) * mm, "end": v(184.5, 66.28) * mm});
            skLineSegment(sketch, "E18.9.13.0", {"start": v(175.5, 31.64) * mm, "end": v(175.5, 47.46) * mm});
            skLineSegment(sketch, "E18.9.13.1", {"start": v(184.5, 31.64) * mm, "end": v(184.5, 47.46) * mm});
            skPoint(sketch, "E18.9.13.2", {"position": v(184.5, 29.64) * mm});
            skPoint(sketch, "E18.9.13.3", {"position": v(175.5, 29.64) * mm});
            skLineSegment(sketch, "E18.9.13.4", {"start": v(175.5, 47.46) * mm, "end": v(184.5, 47.46) * mm});
            skArc(sketch, "E18.9.13.5", {"start": v(175.5, 31.64) * mm, "mid": v(176.09, 30.23) * mm, "end": v(177.5, 29.64) * mm});
            skLineSegment(sketch, "E18.9.13.6", {"start": v(177.5, 29.64) * mm, "end": v(182.5, 29.64) * mm});
            skArc(sketch, "E18.9.13.7", {"start": v(182.5, 29.64) * mm, "mid": v(183.91, 30.23) * mm, "end": v(184.5, 31.64) * mm});
            skLineSegment(sketch, "E18.9.14.0", {"start": v(175.5, -3) * mm, "end": v(175.5, 12.82) * mm});
            skLineSegment(sketch, "E18.9.14.1", {"start": v(184.5, -3) * mm, "end": v(184.5, 12.82) * mm});
            skPoint(sketch, "E18.9.14.2", {"position": v(184.5, -5) * mm});
            skPoint(sketch, "E18.9.14.3", {"position": v(175.5, -5) * mm});
            skLineSegment(sketch, "E18.9.14.4", {"start": v(175.5, 12.82) * mm, "end": v(184.5, 12.82) * mm});
            skArc(sketch, "E18.9.14.5", {"start": v(175.5, -3) * mm, "mid": v(176.09, -4.41) * mm, "end": v(177.5, -5) * mm});
            skLineSegment(sketch, "E18.9.14.6", {"start": v(177.5, -5) * mm, "end": v(182.5, -5) * mm});
            skArc(sketch, "E18.9.14.7", {"start": v(182.5, -5) * mm, "mid": v(183.91, -4.41) * mm, "end": v(184.5, -3) * mm});
            skLineSegment(sketch, "E18.10.0.0", {"start": v(195.5, 481.97) * mm, "end": v(195.5, 497.8) * mm});
            skLineSegment(sketch, "E18.10.0.1", {"start": v(204.5, 481.97) * mm, "end": v(204.5, 497.8) * mm});
            skPoint(sketch, "E18.10.0.2", {"position": v(204.5, 479.97) * mm});
            skPoint(sketch, "E18.10.0.3", {"position": v(195.5, 479.97) * mm});
            skLineSegment(sketch, "E18.10.0.4", {"start": v(195.5, 497.8) * mm, "end": v(204.5, 497.8) * mm});
            skArc(sketch, "E18.10.0.5", {"start": v(195.5, 481.97) * mm, "mid": v(196.09, 480.56) * mm, "end": v(197.5, 479.97) * mm});
            skLineSegment(sketch, "E18.10.0.6", {"start": v(197.5, 479.97) * mm, "end": v(202.5, 479.97) * mm});
            skArc(sketch, "E18.10.0.7", {"start": v(202.5, 479.97) * mm, "mid": v(203.91, 480.56) * mm, "end": v(204.5, 481.97) * mm});
            skLineSegment(sketch, "E18.10.1.0", {"start": v(195.5, 447.33) * mm, "end": v(195.5, 463.15) * mm});
            skLineSegment(sketch, "E18.10.1.1", {"start": v(204.5, 447.33) * mm, "end": v(204.5, 463.15) * mm});
            skPoint(sketch, "E18.10.1.2", {"position": v(204.5, 445.33) * mm});
            skPoint(sketch, "E18.10.1.3", {"position": v(195.5, 445.33) * mm});
            skLineSegment(sketch, "E18.10.1.4", {"start": v(195.5, 463.15) * mm, "end": v(204.5, 463.15) * mm});
            skArc(sketch, "E18.10.1.5", {"start": v(195.5, 447.33) * mm, "mid": v(196.09, 445.92) * mm, "end": v(197.5, 445.33) * mm});
            skLineSegment(sketch, "E18.10.1.6", {"start": v(197.5, 445.33) * mm, "end": v(202.5, 445.33) * mm});
            skArc(sketch, "E18.10.1.7", {"start": v(202.5, 445.33) * mm, "mid": v(203.91, 445.92) * mm, "end": v(204.5, 447.33) * mm});
            skLineSegment(sketch, "E18.10.2.0", {"start": v(195.5, 412.7) * mm, "end": v(195.5, 428.51) * mm});
            skLineSegment(sketch, "E18.10.2.1", {"start": v(204.5, 412.7) * mm, "end": v(204.5, 428.51) * mm});
            skPoint(sketch, "E18.10.2.2", {"position": v(204.5, 410.7) * mm});
            skPoint(sketch, "E18.10.2.3", {"position": v(195.5, 410.7) * mm});
            skLineSegment(sketch, "E18.10.2.4", {"start": v(195.5, 428.51) * mm, "end": v(204.5, 428.51) * mm});
            skArc(sketch, "E18.10.2.5", {"start": v(195.5, 412.7) * mm, "mid": v(196.09, 411.28) * mm, "end": v(197.5, 410.7) * mm});
            skLineSegment(sketch, "E18.10.2.6", {"start": v(197.5, 410.7) * mm, "end": v(202.5, 410.7) * mm});
            skArc(sketch, "E18.10.2.7", {"start": v(202.5, 410.7) * mm, "mid": v(203.91, 411.28) * mm, "end": v(204.5, 412.7) * mm});
            skLineSegment(sketch, "E18.10.3.0", {"start": v(195.5, 378.05) * mm, "end": v(195.5, 393.87) * mm});
            skLineSegment(sketch, "E18.10.3.1", {"start": v(204.5, 378.05) * mm, "end": v(204.5, 393.87) * mm});
            skPoint(sketch, "E18.10.3.2", {"position": v(204.5, 376.05) * mm});
            skPoint(sketch, "E18.10.3.3", {"position": v(195.5, 376.05) * mm});
            skLineSegment(sketch, "E18.10.3.4", {"start": v(195.5, 393.87) * mm, "end": v(204.5, 393.87) * mm});
            skArc(sketch, "E18.10.3.5", {"start": v(195.5, 378.05) * mm, "mid": v(196.09, 376.64) * mm, "end": v(197.5, 376.05) * mm});
            skLineSegment(sketch, "E18.10.3.6", {"start": v(197.5, 376.05) * mm, "end": v(202.5, 376.05) * mm});
            skArc(sketch, "E18.10.3.7", {"start": v(202.5, 376.05) * mm, "mid": v(203.91, 376.64) * mm, "end": v(204.5, 378.05) * mm});
            skLineSegment(sketch, "E18.10.4.0", {"start": v(195.5, 343.41) * mm, "end": v(195.5, 359.23) * mm});
            skLineSegment(sketch, "E18.10.4.1", {"start": v(204.5, 343.41) * mm, "end": v(204.5, 359.23) * mm});
            skPoint(sketch, "E18.10.4.2", {"position": v(204.5, 341.41) * mm});
            skPoint(sketch, "E18.10.4.3", {"position": v(195.5, 341.41) * mm});
            skLineSegment(sketch, "E18.10.4.4", {"start": v(195.5, 359.23) * mm, "end": v(204.5, 359.23) * mm});
            skArc(sketch, "E18.10.4.5", {"start": v(195.5, 343.41) * mm, "mid": v(196.09, 342) * mm, "end": v(197.5, 341.41) * mm});
            skLineSegment(sketch, "E18.10.4.6", {"start": v(197.5, 341.41) * mm, "end": v(202.5, 341.41) * mm});
            skArc(sketch, "E18.10.4.7", {"start": v(202.5, 341.41) * mm, "mid": v(203.91, 342) * mm, "end": v(204.5, 343.41) * mm});
            skLineSegment(sketch, "E18.10.5.0", {"start": v(195.5, 308.77) * mm, "end": v(195.5, 324.59) * mm});
            skLineSegment(sketch, "E18.10.5.1", {"start": v(204.5, 308.77) * mm, "end": v(204.5, 324.59) * mm});
            skPoint(sketch, "E18.10.5.2", {"position": v(204.5, 306.77) * mm});
            skPoint(sketch, "E18.10.5.3", {"position": v(195.5, 306.77) * mm});
            skLineSegment(sketch, "E18.10.5.4", {"start": v(195.5, 324.59) * mm, "end": v(204.5, 324.59) * mm});
            skArc(sketch, "E18.10.5.5", {"start": v(195.5, 308.77) * mm, "mid": v(196.09, 307.35) * mm, "end": v(197.5, 306.77) * mm});
            skLineSegment(sketch, "E18.10.5.6", {"start": v(197.5, 306.77) * mm, "end": v(202.5, 306.77) * mm});
            skArc(sketch, "E18.10.5.7", {"start": v(202.5, 306.77) * mm, "mid": v(203.91, 307.35) * mm, "end": v(204.5, 308.77) * mm});
            skLineSegment(sketch, "E18.10.6.0", {"start": v(195.5, 274.13) * mm, "end": v(195.5, 289.95) * mm});
            skLineSegment(sketch, "E18.10.6.1", {"start": v(204.5, 274.13) * mm, "end": v(204.5, 289.95) * mm});
            skPoint(sketch, "E18.10.6.2", {"position": v(204.5, 272.13) * mm});
            skPoint(sketch, "E18.10.6.3", {"position": v(195.5, 272.13) * mm});
            skLineSegment(sketch, "E18.10.6.4", {"start": v(195.5, 289.95) * mm, "end": v(204.5, 289.95) * mm});
            skArc(sketch, "E18.10.6.5", {"start": v(195.5, 274.13) * mm, "mid": v(196.09, 272.71) * mm, "end": v(197.5, 272.13) * mm});
            skLineSegment(sketch, "E18.10.6.6", {"start": v(197.5, 272.13) * mm, "end": v(202.5, 272.13) * mm});
            skArc(sketch, "E18.10.6.7", {"start": v(202.5, 272.13) * mm, "mid": v(203.91, 272.71) * mm, "end": v(204.5, 274.13) * mm});
            skLineSegment(sketch, "E18.10.7.0", {"start": v(195.5, 239.49) * mm, "end": v(195.5, 255.3) * mm});
            skLineSegment(sketch, "E18.10.7.1", {"start": v(204.5, 239.49) * mm, "end": v(204.5, 255.3) * mm});
            skPoint(sketch, "E18.10.7.2", {"position": v(204.5, 237.49) * mm});
            skPoint(sketch, "E18.10.7.3", {"position": v(195.5, 237.49) * mm});
            skLineSegment(sketch, "E18.10.7.4", {"start": v(195.5, 255.3) * mm, "end": v(204.5, 255.3) * mm});
            skArc(sketch, "E18.10.7.5", {"start": v(195.5, 239.49) * mm, "mid": v(196.09, 238.07) * mm, "end": v(197.5, 237.49) * mm});
            skLineSegment(sketch, "E18.10.7.6", {"start": v(197.5, 237.49) * mm, "end": v(202.5, 237.49) * mm});
            skArc(sketch, "E18.10.7.7", {"start": v(202.5, 237.49) * mm, "mid": v(203.91, 238.07) * mm, "end": v(204.5, 239.49) * mm});
            skLineSegment(sketch, "E18.10.8.0", {"start": v(195.5, 204.85) * mm, "end": v(195.5, 220.67) * mm});
            skLineSegment(sketch, "E18.10.8.1", {"start": v(204.5, 204.85) * mm, "end": v(204.5, 220.67) * mm});
            skPoint(sketch, "E18.10.8.2", {"position": v(204.5, 202.85) * mm});
            skPoint(sketch, "E18.10.8.3", {"position": v(195.5, 202.85) * mm});
            skLineSegment(sketch, "E18.10.8.4", {"start": v(195.5, 220.67) * mm, "end": v(204.5, 220.67) * mm});
            skArc(sketch, "E18.10.8.5", {"start": v(195.5, 204.85) * mm, "mid": v(196.09, 203.43) * mm, "end": v(197.5, 202.85) * mm});
            skLineSegment(sketch, "E18.10.8.6", {"start": v(197.5, 202.85) * mm, "end": v(202.5, 202.85) * mm});
            skArc(sketch, "E18.10.8.7", {"start": v(202.5, 202.85) * mm, "mid": v(203.91, 203.43) * mm, "end": v(204.5, 204.85) * mm});
            skLineSegment(sketch, "E18.10.9.0", {"start": v(195.5, 170.2) * mm, "end": v(195.5, 186.03) * mm});
            skLineSegment(sketch, "E18.10.9.1", {"start": v(204.5, 170.2) * mm, "end": v(204.5, 186.03) * mm});
            skPoint(sketch, "E18.10.9.2", {"position": v(204.5, 168.2) * mm});
            skPoint(sketch, "E18.10.9.3", {"position": v(195.5, 168.2) * mm});
            skLineSegment(sketch, "E18.10.9.4", {"start": v(195.5, 186.03) * mm, "end": v(204.5, 186.03) * mm});
            skArc(sketch, "E18.10.9.5", {"start": v(195.5, 170.2) * mm, "mid": v(196.09, 168.8) * mm, "end": v(197.5, 168.2) * mm});
            skLineSegment(sketch, "E18.10.9.6", {"start": v(197.5, 168.2) * mm, "end": v(202.5, 168.2) * mm});
            skArc(sketch, "E18.10.9.7", {"start": v(202.5, 168.2) * mm, "mid": v(203.91, 168.8) * mm, "end": v(204.5, 170.2) * mm});
            skLineSegment(sketch, "E18.10.10.0", {"start": v(195.5, 135.56) * mm, "end": v(195.5, 151.38) * mm});
            skLineSegment(sketch, "E18.10.10.1", {"start": v(204.5, 135.56) * mm, "end": v(204.5, 151.38) * mm});
            skPoint(sketch, "E18.10.10.2", {"position": v(204.5, 133.56) * mm});
            skPoint(sketch, "E18.10.10.3", {"position": v(195.5, 133.56) * mm});
            skLineSegment(sketch, "E18.10.10.4", {"start": v(195.5, 151.38) * mm, "end": v(204.5, 151.38) * mm});
            skArc(sketch, "E18.10.10.5", {"start": v(195.5, 135.56) * mm, "mid": v(196.09, 134.15) * mm, "end": v(197.5, 133.56) * mm});
            skLineSegment(sketch, "E18.10.10.6", {"start": v(197.5, 133.56) * mm, "end": v(202.5, 133.56) * mm});
            skArc(sketch, "E18.10.10.7", {"start": v(202.5, 133.56) * mm, "mid": v(203.91, 134.15) * mm, "end": v(204.5, 135.56) * mm});
            skLineSegment(sketch, "E18.10.11.0", {"start": v(195.5, 100.92) * mm, "end": v(195.5, 116.74) * mm});
            skLineSegment(sketch, "E18.10.11.1", {"start": v(204.5, 100.92) * mm, "end": v(204.5, 116.74) * mm});
            skPoint(sketch, "E18.10.11.2", {"position": v(204.5, 98.92) * mm});
            skPoint(sketch, "E18.10.11.3", {"position": v(195.5, 98.92) * mm});
            skLineSegment(sketch, "E18.10.11.4", {"start": v(195.5, 116.74) * mm, "end": v(204.5, 116.74) * mm});
            skArc(sketch, "E18.10.11.5", {"start": v(195.5, 100.92) * mm, "mid": v(196.09, 99.5) * mm, "end": v(197.5, 98.92) * mm});
            skLineSegment(sketch, "E18.10.11.6", {"start": v(197.5, 98.92) * mm, "end": v(202.5, 98.92) * mm});
            skArc(sketch, "E18.10.11.7", {"start": v(202.5, 98.92) * mm, "mid": v(203.91, 99.5) * mm, "end": v(204.5, 100.92) * mm});
            skLineSegment(sketch, "E18.10.12.0", {"start": v(195.5, 66.28) * mm, "end": v(195.5, 82.1) * mm});
            skLineSegment(sketch, "E18.10.12.1", {"start": v(204.5, 66.28) * mm, "end": v(204.5, 82.1) * mm});
            skPoint(sketch, "E18.10.12.2", {"position": v(204.5, 64.28) * mm});
            skPoint(sketch, "E18.10.12.3", {"position": v(195.5, 64.28) * mm});
            skLineSegment(sketch, "E18.10.12.4", {"start": v(195.5, 82.1) * mm, "end": v(204.5, 82.1) * mm});
            skArc(sketch, "E18.10.12.5", {"start": v(195.5, 66.28) * mm, "mid": v(196.09, 64.87) * mm, "end": v(197.5, 64.28) * mm});
            skLineSegment(sketch, "E18.10.12.6", {"start": v(197.5, 64.28) * mm, "end": v(202.5, 64.28) * mm});
            skArc(sketch, "E18.10.12.7", {"start": v(202.5, 64.28) * mm, "mid": v(203.91, 64.87) * mm, "end": v(204.5, 66.28) * mm});
            skLineSegment(sketch, "E18.10.13.0", {"start": v(195.5, 31.64) * mm, "end": v(195.5, 47.46) * mm});
            skLineSegment(sketch, "E18.10.13.1", {"start": v(204.5, 31.64) * mm, "end": v(204.5, 47.46) * mm});
            skPoint(sketch, "E18.10.13.2", {"position": v(204.5, 29.64) * mm});
            skPoint(sketch, "E18.10.13.3", {"position": v(195.5, 29.64) * mm});
            skLineSegment(sketch, "E18.10.13.4", {"start": v(195.5, 47.46) * mm, "end": v(204.5, 47.46) * mm});
            skArc(sketch, "E18.10.13.5", {"start": v(195.5, 31.64) * mm, "mid": v(196.09, 30.23) * mm, "end": v(197.5, 29.64) * mm});
            skLineSegment(sketch, "E18.10.13.6", {"start": v(197.5, 29.64) * mm, "end": v(202.5, 29.64) * mm});
            skArc(sketch, "E18.10.13.7", {"start": v(202.5, 29.64) * mm, "mid": v(203.91, 30.23) * mm, "end": v(204.5, 31.64) * mm});
            skLineSegment(sketch, "E18.10.14.0", {"start": v(195.5, -3) * mm, "end": v(195.5, 12.82) * mm});
            skLineSegment(sketch, "E18.10.14.1", {"start": v(204.5, -3) * mm, "end": v(204.5, 12.82) * mm});
            skPoint(sketch, "E18.10.14.2", {"position": v(204.5, -5) * mm});
            skPoint(sketch, "E18.10.14.3", {"position": v(195.5, -5) * mm});
            skLineSegment(sketch, "E18.10.14.4", {"start": v(195.5, 12.82) * mm, "end": v(204.5, 12.82) * mm});
            skArc(sketch, "E18.10.14.5", {"start": v(195.5, -3) * mm, "mid": v(196.09, -4.41) * mm, "end": v(197.5, -5) * mm});
            skLineSegment(sketch, "E18.10.14.6", {"start": v(197.5, -5) * mm, "end": v(202.5, -5) * mm});
            skArc(sketch, "E18.10.14.7", {"start": v(202.5, -5) * mm, "mid": v(203.91, -4.41) * mm, "end": v(204.5, -3) * mm});
            skLineSegment(sketch, "E18.11.0.0", {"start": v(215.5, 481.97) * mm, "end": v(215.5, 497.8) * mm});
            skLineSegment(sketch, "E18.11.0.1", {"start": v(224.5, 481.97) * mm, "end": v(224.5, 497.8) * mm});
            skPoint(sketch, "E18.11.0.2", {"position": v(224.5, 479.97) * mm});
            skPoint(sketch, "E18.11.0.3", {"position": v(215.5, 479.97) * mm});
            skLineSegment(sketch, "E18.11.0.4", {"start": v(215.5, 497.8) * mm, "end": v(224.5, 497.8) * mm});
            skArc(sketch, "E18.11.0.5", {"start": v(215.5, 481.97) * mm, "mid": v(216.09, 480.56) * mm, "end": v(217.5, 479.97) * mm});
            skLineSegment(sketch, "E18.11.0.6", {"start": v(217.5, 479.97) * mm, "end": v(222.5, 479.97) * mm});
            skArc(sketch, "E18.11.0.7", {"start": v(222.5, 479.97) * mm, "mid": v(223.91, 480.56) * mm, "end": v(224.5, 481.97) * mm});
            skLineSegment(sketch, "E18.11.1.0", {"start": v(215.5, 447.33) * mm, "end": v(215.5, 463.15) * mm});
            skLineSegment(sketch, "E18.11.1.1", {"start": v(224.5, 447.33) * mm, "end": v(224.5, 463.15) * mm});
            skPoint(sketch, "E18.11.1.2", {"position": v(224.5, 445.33) * mm});
            skPoint(sketch, "E18.11.1.3", {"position": v(215.5, 445.33) * mm});
            skLineSegment(sketch, "E18.11.1.4", {"start": v(215.5, 463.15) * mm, "end": v(224.5, 463.15) * mm});
            skArc(sketch, "E18.11.1.5", {"start": v(215.5, 447.33) * mm, "mid": v(216.09, 445.92) * mm, "end": v(217.5, 445.33) * mm});
            skLineSegment(sketch, "E18.11.1.6", {"start": v(217.5, 445.33) * mm, "end": v(222.5, 445.33) * mm});
            skArc(sketch, "E18.11.1.7", {"start": v(222.5, 445.33) * mm, "mid": v(223.91, 445.92) * mm, "end": v(224.5, 447.33) * mm});
            skLineSegment(sketch, "E18.11.2.0", {"start": v(215.5, 412.7) * mm, "end": v(215.5, 428.51) * mm});
            skLineSegment(sketch, "E18.11.2.1", {"start": v(224.5, 412.7) * mm, "end": v(224.5, 428.51) * mm});
            skPoint(sketch, "E18.11.2.2", {"position": v(224.5, 410.7) * mm});
            skPoint(sketch, "E18.11.2.3", {"position": v(215.5, 410.7) * mm});
            skLineSegment(sketch, "E18.11.2.4", {"start": v(215.5, 428.51) * mm, "end": v(224.5, 428.51) * mm});
            skArc(sketch, "E18.11.2.5", {"start": v(215.5, 412.7) * mm, "mid": v(216.09, 411.28) * mm, "end": v(217.5, 410.7) * mm});
            skLineSegment(sketch, "E18.11.2.6", {"start": v(217.5, 410.7) * mm, "end": v(222.5, 410.7) * mm});
            skArc(sketch, "E18.11.2.7", {"start": v(222.5, 410.7) * mm, "mid": v(223.91, 411.28) * mm, "end": v(224.5, 412.7) * mm});
            skLineSegment(sketch, "E18.11.3.0", {"start": v(215.5, 378.05) * mm, "end": v(215.5, 393.87) * mm});
            skLineSegment(sketch, "E18.11.3.1", {"start": v(224.5, 378.05) * mm, "end": v(224.5, 393.87) * mm});
            skPoint(sketch, "E18.11.3.2", {"position": v(224.5, 376.05) * mm});
            skPoint(sketch, "E18.11.3.3", {"position": v(215.5, 376.05) * mm});
            skLineSegment(sketch, "E18.11.3.4", {"start": v(215.5, 393.87) * mm, "end": v(224.5, 393.87) * mm});
            skArc(sketch, "E18.11.3.5", {"start": v(215.5, 378.05) * mm, "mid": v(216.09, 376.64) * mm, "end": v(217.5, 376.05) * mm});
            skLineSegment(sketch, "E18.11.3.6", {"start": v(217.5, 376.05) * mm, "end": v(222.5, 376.05) * mm});
            skArc(sketch, "E18.11.3.7", {"start": v(222.5, 376.05) * mm, "mid": v(223.91, 376.64) * mm, "end": v(224.5, 378.05) * mm});
            skLineSegment(sketch, "E18.11.4.0", {"start": v(215.5, 343.41) * mm, "end": v(215.5, 359.23) * mm});
            skLineSegment(sketch, "E18.11.4.1", {"start": v(224.5, 343.41) * mm, "end": v(224.5, 359.23) * mm});
            skPoint(sketch, "E18.11.4.2", {"position": v(224.5, 341.41) * mm});
            skPoint(sketch, "E18.11.4.3", {"position": v(215.5, 341.41) * mm});
            skLineSegment(sketch, "E18.11.4.4", {"start": v(215.5, 359.23) * mm, "end": v(224.5, 359.23) * mm});
            skArc(sketch, "E18.11.4.5", {"start": v(215.5, 343.41) * mm, "mid": v(216.09, 342) * mm, "end": v(217.5, 341.41) * mm});
            skLineSegment(sketch, "E18.11.4.6", {"start": v(217.5, 341.41) * mm, "end": v(222.5, 341.41) * mm});
            skArc(sketch, "E18.11.4.7", {"start": v(222.5, 341.41) * mm, "mid": v(223.91, 342) * mm, "end": v(224.5, 343.41) * mm});
            skLineSegment(sketch, "E18.11.5.0", {"start": v(215.5, 308.77) * mm, "end": v(215.5, 324.59) * mm});
            skLineSegment(sketch, "E18.11.5.1", {"start": v(224.5, 308.77) * mm, "end": v(224.5, 324.59) * mm});
            skPoint(sketch, "E18.11.5.2", {"position": v(224.5, 306.77) * mm});
            skPoint(sketch, "E18.11.5.3", {"position": v(215.5, 306.77) * mm});
            skLineSegment(sketch, "E18.11.5.4", {"start": v(215.5, 324.59) * mm, "end": v(224.5, 324.59) * mm});
            skArc(sketch, "E18.11.5.5", {"start": v(215.5, 308.77) * mm, "mid": v(216.09, 307.35) * mm, "end": v(217.5, 306.77) * mm});
            skLineSegment(sketch, "E18.11.5.6", {"start": v(217.5, 306.77) * mm, "end": v(222.5, 306.77) * mm});
            skArc(sketch, "E18.11.5.7", {"start": v(222.5, 306.77) * mm, "mid": v(223.91, 307.35) * mm, "end": v(224.5, 308.77) * mm});
            skLineSegment(sketch, "E18.11.6.0", {"start": v(215.5, 274.13) * mm, "end": v(215.5, 289.95) * mm});
            skLineSegment(sketch, "E18.11.6.1", {"start": v(224.5, 274.13) * mm, "end": v(224.5, 289.95) * mm});
            skPoint(sketch, "E18.11.6.2", {"position": v(224.5, 272.13) * mm});
            skPoint(sketch, "E18.11.6.3", {"position": v(215.5, 272.13) * mm});
            skLineSegment(sketch, "E18.11.6.4", {"start": v(215.5, 289.95) * mm, "end": v(224.5, 289.95) * mm});
            skArc(sketch, "E18.11.6.5", {"start": v(215.5, 274.13) * mm, "mid": v(216.09, 272.71) * mm, "end": v(217.5, 272.13) * mm});
            skLineSegment(sketch, "E18.11.6.6", {"start": v(217.5, 272.13) * mm, "end": v(222.5, 272.13) * mm});
            skArc(sketch, "E18.11.6.7", {"start": v(222.5, 272.13) * mm, "mid": v(223.91, 272.71) * mm, "end": v(224.5, 274.13) * mm});
            skLineSegment(sketch, "E18.11.7.0", {"start": v(215.5, 239.49) * mm, "end": v(215.5, 255.3) * mm});
            skLineSegment(sketch, "E18.11.7.1", {"start": v(224.5, 239.49) * mm, "end": v(224.5, 255.3) * mm});
            skPoint(sketch, "E18.11.7.2", {"position": v(224.5, 237.49) * mm});
            skPoint(sketch, "E18.11.7.3", {"position": v(215.5, 237.49) * mm});
            skLineSegment(sketch, "E18.11.7.4", {"start": v(215.5, 255.3) * mm, "end": v(224.5, 255.3) * mm});
            skArc(sketch, "E18.11.7.5", {"start": v(215.5, 239.49) * mm, "mid": v(216.09, 238.07) * mm, "end": v(217.5, 237.49) * mm});
            skLineSegment(sketch, "E18.11.7.6", {"start": v(217.5, 237.49) * mm, "end": v(222.5, 237.49) * mm});
            skArc(sketch, "E18.11.7.7", {"start": v(222.5, 237.49) * mm, "mid": v(223.91, 238.07) * mm, "end": v(224.5, 239.49) * mm});
            skLineSegment(sketch, "E18.11.8.0", {"start": v(215.5, 204.85) * mm, "end": v(215.5, 220.67) * mm});
            skLineSegment(sketch, "E18.11.8.1", {"start": v(224.5, 204.85) * mm, "end": v(224.5, 220.67) * mm});
            skPoint(sketch, "E18.11.8.2", {"position": v(224.5, 202.85) * mm});
            skPoint(sketch, "E18.11.8.3", {"position": v(215.5, 202.85) * mm});
            skLineSegment(sketch, "E18.11.8.4", {"start": v(215.5, 220.67) * mm, "end": v(224.5, 220.67) * mm});
            skArc(sketch, "E18.11.8.5", {"start": v(215.5, 204.85) * mm, "mid": v(216.09, 203.43) * mm, "end": v(217.5, 202.85) * mm});
            skLineSegment(sketch, "E18.11.8.6", {"start": v(217.5, 202.85) * mm, "end": v(222.5, 202.85) * mm});
            skArc(sketch, "E18.11.8.7", {"start": v(222.5, 202.85) * mm, "mid": v(223.91, 203.43) * mm, "end": v(224.5, 204.85) * mm});
            skLineSegment(sketch, "E18.11.9.0", {"start": v(215.5, 170.2) * mm, "end": v(215.5, 186.03) * mm});
            skLineSegment(sketch, "E18.11.9.1", {"start": v(224.5, 170.2) * mm, "end": v(224.5, 186.03) * mm});
            skPoint(sketch, "E18.11.9.2", {"position": v(224.5, 168.2) * mm});
            skPoint(sketch, "E18.11.9.3", {"position": v(215.5, 168.2) * mm});
            skLineSegment(sketch, "E18.11.9.4", {"start": v(215.5, 186.03) * mm, "end": v(224.5, 186.03) * mm});
            skArc(sketch, "E18.11.9.5", {"start": v(215.5, 170.2) * mm, "mid": v(216.09, 168.8) * mm, "end": v(217.5, 168.2) * mm});
            skLineSegment(sketch, "E18.11.9.6", {"start": v(217.5, 168.2) * mm, "end": v(222.5, 168.2) * mm});
            skArc(sketch, "E18.11.9.7", {"start": v(222.5, 168.2) * mm, "mid": v(223.91, 168.8) * mm, "end": v(224.5, 170.2) * mm});
            skLineSegment(sketch, "E18.11.10.0", {"start": v(215.5, 135.56) * mm, "end": v(215.5, 151.38) * mm});
            skLineSegment(sketch, "E18.11.10.1", {"start": v(224.5, 135.56) * mm, "end": v(224.5, 151.38) * mm});
            skPoint(sketch, "E18.11.10.2", {"position": v(224.5, 133.56) * mm});
            skPoint(sketch, "E18.11.10.3", {"position": v(215.5, 133.56) * mm});
            skLineSegment(sketch, "E18.11.10.4", {"start": v(215.5, 151.38) * mm, "end": v(224.5, 151.38) * mm});
            skArc(sketch, "E18.11.10.5", {"start": v(215.5, 135.56) * mm, "mid": v(216.09, 134.15) * mm, "end": v(217.5, 133.56) * mm});
            skLineSegment(sketch, "E18.11.10.6", {"start": v(217.5, 133.56) * mm, "end": v(222.5, 133.56) * mm});
            skArc(sketch, "E18.11.10.7", {"start": v(222.5, 133.56) * mm, "mid": v(223.91, 134.15) * mm, "end": v(224.5, 135.56) * mm});
            skLineSegment(sketch, "E18.11.11.0", {"start": v(215.5, 100.92) * mm, "end": v(215.5, 116.74) * mm});
            skLineSegment(sketch, "E18.11.11.1", {"start": v(224.5, 100.92) * mm, "end": v(224.5, 116.74) * mm});
            skPoint(sketch, "E18.11.11.2", {"position": v(224.5, 98.92) * mm});
            skPoint(sketch, "E18.11.11.3", {"position": v(215.5, 98.92) * mm});
            skLineSegment(sketch, "E18.11.11.4", {"start": v(215.5, 116.74) * mm, "end": v(224.5, 116.74) * mm});
            skArc(sketch, "E18.11.11.5", {"start": v(215.5, 100.92) * mm, "mid": v(216.09, 99.5) * mm, "end": v(217.5, 98.92) * mm});
            skLineSegment(sketch, "E18.11.11.6", {"start": v(217.5, 98.92) * mm, "end": v(222.5, 98.92) * mm});
            skArc(sketch, "E18.11.11.7", {"start": v(222.5, 98.92) * mm, "mid": v(223.91, 99.5) * mm, "end": v(224.5, 100.92) * mm});
            skLineSegment(sketch, "E18.11.12.0", {"start": v(215.5, 66.28) * mm, "end": v(215.5, 82.1) * mm});
            skLineSegment(sketch, "E18.11.12.1", {"start": v(224.5, 66.28) * mm, "end": v(224.5, 82.1) * mm});
            skPoint(sketch, "E18.11.12.2", {"position": v(224.5, 64.28) * mm});
            skPoint(sketch, "E18.11.12.3", {"position": v(215.5, 64.28) * mm});
            skLineSegment(sketch, "E18.11.12.4", {"start": v(215.5, 82.1) * mm, "end": v(224.5, 82.1) * mm});
            skArc(sketch, "E18.11.12.5", {"start": v(215.5, 66.28) * mm, "mid": v(216.09, 64.87) * mm, "end": v(217.5, 64.28) * mm});
            skLineSegment(sketch, "E18.11.12.6", {"start": v(217.5, 64.28) * mm, "end": v(222.5, 64.28) * mm});
            skArc(sketch, "E18.11.12.7", {"start": v(222.5, 64.28) * mm, "mid": v(223.91, 64.87) * mm, "end": v(224.5, 66.28) * mm});
            skLineSegment(sketch, "E18.11.13.0", {"start": v(215.5, 31.64) * mm, "end": v(215.5, 47.46) * mm});
            skLineSegment(sketch, "E18.11.13.1", {"start": v(224.5, 31.64) * mm, "end": v(224.5, 47.46) * mm});
            skPoint(sketch, "E18.11.13.2", {"position": v(224.5, 29.64) * mm});
            skPoint(sketch, "E18.11.13.3", {"position": v(215.5, 29.64) * mm});
            skLineSegment(sketch, "E18.11.13.4", {"start": v(215.5, 47.46) * mm, "end": v(224.5, 47.46) * mm});
            skArc(sketch, "E18.11.13.5", {"start": v(215.5, 31.64) * mm, "mid": v(216.09, 30.23) * mm, "end": v(217.5, 29.64) * mm});
            skLineSegment(sketch, "E18.11.13.6", {"start": v(217.5, 29.64) * mm, "end": v(222.5, 29.64) * mm});
            skArc(sketch, "E18.11.13.7", {"start": v(222.5, 29.64) * mm, "mid": v(223.91, 30.23) * mm, "end": v(224.5, 31.64) * mm});
            skLineSegment(sketch, "E18.11.14.0", {"start": v(215.5, -3) * mm, "end": v(215.5, 12.82) * mm});
            skLineSegment(sketch, "E18.11.14.1", {"start": v(224.5, -3) * mm, "end": v(224.5, 12.82) * mm});
            skPoint(sketch, "E18.11.14.2", {"position": v(224.5, -5) * mm});
            skPoint(sketch, "E18.11.14.3", {"position": v(215.5, -5) * mm});
            skLineSegment(sketch, "E18.11.14.4", {"start": v(215.5, 12.82) * mm, "end": v(224.5, 12.82) * mm});
            skArc(sketch, "E18.11.14.5", {"start": v(215.5, -3) * mm, "mid": v(216.09, -4.41) * mm, "end": v(217.5, -5) * mm});
            skLineSegment(sketch, "E18.11.14.6", {"start": v(217.5, -5) * mm, "end": v(222.5, -5) * mm});
            skArc(sketch, "E18.11.14.7", {"start": v(222.5, -5) * mm, "mid": v(223.91, -4.41) * mm, "end": v(224.5, -3) * mm});
            skLineSegment(sketch, "E18.12.0.0", {"start": v(235.5, 481.97) * mm, "end": v(235.5, 497.8) * mm});
            skLineSegment(sketch, "E18.12.0.1", {"start": v(244.5, 481.97) * mm, "end": v(244.5, 497.8) * mm});
            skPoint(sketch, "E18.12.0.2", {"position": v(244.5, 479.97) * mm});
            skPoint(sketch, "E18.12.0.3", {"position": v(235.5, 479.97) * mm});
            skLineSegment(sketch, "E18.12.0.4", {"start": v(235.5, 497.8) * mm, "end": v(244.5, 497.8) * mm});
            skArc(sketch, "E18.12.0.5", {"start": v(235.5, 481.97) * mm, "mid": v(236.09, 480.56) * mm, "end": v(237.5, 479.97) * mm});
            skLineSegment(sketch, "E18.12.0.6", {"start": v(237.5, 479.97) * mm, "end": v(242.5, 479.97) * mm});
            skArc(sketch, "E18.12.0.7", {"start": v(242.5, 479.97) * mm, "mid": v(243.91, 480.56) * mm, "end": v(244.5, 481.97) * mm});
            skLineSegment(sketch, "E18.12.1.0", {"start": v(235.5, 447.33) * mm, "end": v(235.5, 463.15) * mm});
            skLineSegment(sketch, "E18.12.1.1", {"start": v(244.5, 447.33) * mm, "end": v(244.5, 463.15) * mm});
            skPoint(sketch, "E18.12.1.2", {"position": v(244.5, 445.33) * mm});
            skPoint(sketch, "E18.12.1.3", {"position": v(235.5, 445.33) * mm});
            skLineSegment(sketch, "E18.12.1.4", {"start": v(235.5, 463.15) * mm, "end": v(244.5, 463.15) * mm});
            skArc(sketch, "E18.12.1.5", {"start": v(235.5, 447.33) * mm, "mid": v(236.09, 445.92) * mm, "end": v(237.5, 445.33) * mm});
            skLineSegment(sketch, "E18.12.1.6", {"start": v(237.5, 445.33) * mm, "end": v(242.5, 445.33) * mm});
            skArc(sketch, "E18.12.1.7", {"start": v(242.5, 445.33) * mm, "mid": v(243.91, 445.92) * mm, "end": v(244.5, 447.33) * mm});
            skLineSegment(sketch, "E18.12.2.0", {"start": v(235.5, 412.7) * mm, "end": v(235.5, 428.51) * mm});
            skLineSegment(sketch, "E18.12.2.1", {"start": v(244.5, 412.7) * mm, "end": v(244.5, 428.51) * mm});
            skPoint(sketch, "E18.12.2.2", {"position": v(244.5, 410.7) * mm});
            skPoint(sketch, "E18.12.2.3", {"position": v(235.5, 410.7) * mm});
            skLineSegment(sketch, "E18.12.2.4", {"start": v(235.5, 428.51) * mm, "end": v(244.5, 428.51) * mm});
            skArc(sketch, "E18.12.2.5", {"start": v(235.5, 412.7) * mm, "mid": v(236.09, 411.28) * mm, "end": v(237.5, 410.7) * mm});
            skLineSegment(sketch, "E18.12.2.6", {"start": v(237.5, 410.7) * mm, "end": v(242.5, 410.7) * mm});
            skArc(sketch, "E18.12.2.7", {"start": v(242.5, 410.7) * mm, "mid": v(243.91, 411.28) * mm, "end": v(244.5, 412.7) * mm});
            skLineSegment(sketch, "E18.12.3.0", {"start": v(235.5, 378.05) * mm, "end": v(235.5, 393.87) * mm});
            skLineSegment(sketch, "E18.12.3.1", {"start": v(244.5, 378.05) * mm, "end": v(244.5, 393.87) * mm});
            skPoint(sketch, "E18.12.3.2", {"position": v(244.5, 376.05) * mm});
            skPoint(sketch, "E18.12.3.3", {"position": v(235.5, 376.05) * mm});
            skLineSegment(sketch, "E18.12.3.4", {"start": v(235.5, 393.87) * mm, "end": v(244.5, 393.87) * mm});
            skArc(sketch, "E18.12.3.5", {"start": v(235.5, 378.05) * mm, "mid": v(236.09, 376.64) * mm, "end": v(237.5, 376.05) * mm});
            skLineSegment(sketch, "E18.12.3.6", {"start": v(237.5, 376.05) * mm, "end": v(242.5, 376.05) * mm});
            skArc(sketch, "E18.12.3.7", {"start": v(242.5, 376.05) * mm, "mid": v(243.91, 376.64) * mm, "end": v(244.5, 378.05) * mm});
            skLineSegment(sketch, "E18.12.4.0", {"start": v(235.5, 343.41) * mm, "end": v(235.5, 359.23) * mm});
            skLineSegment(sketch, "E18.12.4.1", {"start": v(244.5, 343.41) * mm, "end": v(244.5, 359.23) * mm});
            skPoint(sketch, "E18.12.4.2", {"position": v(244.5, 341.41) * mm});
            skPoint(sketch, "E18.12.4.3", {"position": v(235.5, 341.41) * mm});
            skLineSegment(sketch, "E18.12.4.4", {"start": v(235.5, 359.23) * mm, "end": v(244.5, 359.23) * mm});
            skArc(sketch, "E18.12.4.5", {"start": v(235.5, 343.41) * mm, "mid": v(236.09, 342) * mm, "end": v(237.5, 341.41) * mm});
            skLineSegment(sketch, "E18.12.4.6", {"start": v(237.5, 341.41) * mm, "end": v(242.5, 341.41) * mm});
            skArc(sketch, "E18.12.4.7", {"start": v(242.5, 341.41) * mm, "mid": v(243.91, 342) * mm, "end": v(244.5, 343.41) * mm});
            skLineSegment(sketch, "E18.12.5.0", {"start": v(235.5, 308.77) * mm, "end": v(235.5, 324.59) * mm});
            skLineSegment(sketch, "E18.12.5.1", {"start": v(244.5, 308.77) * mm, "end": v(244.5, 324.59) * mm});
            skPoint(sketch, "E18.12.5.2", {"position": v(244.5, 306.77) * mm});
            skPoint(sketch, "E18.12.5.3", {"position": v(235.5, 306.77) * mm});
            skLineSegment(sketch, "E18.12.5.4", {"start": v(235.5, 324.59) * mm, "end": v(244.5, 324.59) * mm});
            skArc(sketch, "E18.12.5.5", {"start": v(235.5, 308.77) * mm, "mid": v(236.09, 307.35) * mm, "end": v(237.5, 306.77) * mm});
            skLineSegment(sketch, "E18.12.5.6", {"start": v(237.5, 306.77) * mm, "end": v(242.5, 306.77) * mm});
            skArc(sketch, "E18.12.5.7", {"start": v(242.5, 306.77) * mm, "mid": v(243.91, 307.35) * mm, "end": v(244.5, 308.77) * mm});
            skLineSegment(sketch, "E18.12.6.0", {"start": v(235.5, 274.13) * mm, "end": v(235.5, 289.95) * mm});
            skLineSegment(sketch, "E18.12.6.1", {"start": v(244.5, 274.13) * mm, "end": v(244.5, 289.95) * mm});
            skPoint(sketch, "E18.12.6.2", {"position": v(244.5, 272.13) * mm});
            skPoint(sketch, "E18.12.6.3", {"position": v(235.5, 272.13) * mm});
            skLineSegment(sketch, "E18.12.6.4", {"start": v(235.5, 289.95) * mm, "end": v(244.5, 289.95) * mm});
            skArc(sketch, "E18.12.6.5", {"start": v(235.5, 274.13) * mm, "mid": v(236.09, 272.71) * mm, "end": v(237.5, 272.13) * mm});
            skLineSegment(sketch, "E18.12.6.6", {"start": v(237.5, 272.13) * mm, "end": v(242.5, 272.13) * mm});
            skArc(sketch, "E18.12.6.7", {"start": v(242.5, 272.13) * mm, "mid": v(243.91, 272.71) * mm, "end": v(244.5, 274.13) * mm});
            skLineSegment(sketch, "E18.12.7.0", {"start": v(235.5, 239.49) * mm, "end": v(235.5, 255.3) * mm});
            skLineSegment(sketch, "E18.12.7.1", {"start": v(244.5, 239.49) * mm, "end": v(244.5, 255.3) * mm});
            skPoint(sketch, "E18.12.7.2", {"position": v(244.5, 237.49) * mm});
            skPoint(sketch, "E18.12.7.3", {"position": v(235.5, 237.49) * mm});
            skLineSegment(sketch, "E18.12.7.4", {"start": v(235.5, 255.3) * mm, "end": v(244.5, 255.3) * mm});
            skArc(sketch, "E18.12.7.5", {"start": v(235.5, 239.49) * mm, "mid": v(236.09, 238.07) * mm, "end": v(237.5, 237.49) * mm});
            skLineSegment(sketch, "E18.12.7.6", {"start": v(237.5, 237.49) * mm, "end": v(242.5, 237.49) * mm});
            skArc(sketch, "E18.12.7.7", {"start": v(242.5, 237.49) * mm, "mid": v(243.91, 238.07) * mm, "end": v(244.5, 239.49) * mm});
            skLineSegment(sketch, "E18.12.8.0", {"start": v(235.5, 204.85) * mm, "end": v(235.5, 220.67) * mm});
            skLineSegment(sketch, "E18.12.8.1", {"start": v(244.5, 204.85) * mm, "end": v(244.5, 220.67) * mm});
            skPoint(sketch, "E18.12.8.2", {"position": v(244.5, 202.85) * mm});
            skPoint(sketch, "E18.12.8.3", {"position": v(235.5, 202.85) * mm});
            skLineSegment(sketch, "E18.12.8.4", {"start": v(235.5, 220.67) * mm, "end": v(244.5, 220.67) * mm});
            skArc(sketch, "E18.12.8.5", {"start": v(235.5, 204.85) * mm, "mid": v(236.09, 203.43) * mm, "end": v(237.5, 202.85) * mm});
            skLineSegment(sketch, "E18.12.8.6", {"start": v(237.5, 202.85) * mm, "end": v(242.5, 202.85) * mm});
            skArc(sketch, "E18.12.8.7", {"start": v(242.5, 202.85) * mm, "mid": v(243.91, 203.43) * mm, "end": v(244.5, 204.85) * mm});
            skLineSegment(sketch, "E18.12.9.0", {"start": v(235.5, 170.2) * mm, "end": v(235.5, 186.03) * mm});
            skLineSegment(sketch, "E18.12.9.1", {"start": v(244.5, 170.2) * mm, "end": v(244.5, 186.03) * mm});
            skPoint(sketch, "E18.12.9.2", {"position": v(244.5, 168.2) * mm});
            skPoint(sketch, "E18.12.9.3", {"position": v(235.5, 168.2) * mm});
            skLineSegment(sketch, "E18.12.9.4", {"start": v(235.5, 186.03) * mm, "end": v(244.5, 186.03) * mm});
            skArc(sketch, "E18.12.9.5", {"start": v(235.5, 170.2) * mm, "mid": v(236.09, 168.8) * mm, "end": v(237.5, 168.2) * mm});
            skLineSegment(sketch, "E18.12.9.6", {"start": v(237.5, 168.2) * mm, "end": v(242.5, 168.2) * mm});
            skArc(sketch, "E18.12.9.7", {"start": v(242.5, 168.2) * mm, "mid": v(243.91, 168.8) * mm, "end": v(244.5, 170.2) * mm});
            skLineSegment(sketch, "E18.12.10.0", {"start": v(235.5, 135.56) * mm, "end": v(235.5, 151.38) * mm});
            skLineSegment(sketch, "E18.12.10.1", {"start": v(244.5, 135.56) * mm, "end": v(244.5, 151.38) * mm});
            skPoint(sketch, "E18.12.10.2", {"position": v(244.5, 133.56) * mm});
            skPoint(sketch, "E18.12.10.3", {"position": v(235.5, 133.56) * mm});
            skLineSegment(sketch, "E18.12.10.4", {"start": v(235.5, 151.38) * mm, "end": v(244.5, 151.38) * mm});
            skArc(sketch, "E18.12.10.5", {"start": v(235.5, 135.56) * mm, "mid": v(236.09, 134.15) * mm, "end": v(237.5, 133.56) * mm});
            skLineSegment(sketch, "E18.12.10.6", {"start": v(237.5, 133.56) * mm, "end": v(242.5, 133.56) * mm});
            skArc(sketch, "E18.12.10.7", {"start": v(242.5, 133.56) * mm, "mid": v(243.91, 134.15) * mm, "end": v(244.5, 135.56) * mm});
            skLineSegment(sketch, "E18.12.11.0", {"start": v(235.5, 100.92) * mm, "end": v(235.5, 116.74) * mm});
            skLineSegment(sketch, "E18.12.11.1", {"start": v(244.5, 100.92) * mm, "end": v(244.5, 116.74) * mm});
            skPoint(sketch, "E18.12.11.2", {"position": v(244.5, 98.92) * mm});
            skPoint(sketch, "E18.12.11.3", {"position": v(235.5, 98.92) * mm});
            skLineSegment(sketch, "E18.12.11.4", {"start": v(235.5, 116.74) * mm, "end": v(244.5, 116.74) * mm});
            skArc(sketch, "E18.12.11.5", {"start": v(235.5, 100.92) * mm, "mid": v(236.09, 99.5) * mm, "end": v(237.5, 98.92) * mm});
            skLineSegment(sketch, "E18.12.11.6", {"start": v(237.5, 98.92) * mm, "end": v(242.5, 98.92) * mm});
            skArc(sketch, "E18.12.11.7", {"start": v(242.5, 98.92) * mm, "mid": v(243.91, 99.5) * mm, "end": v(244.5, 100.92) * mm});
            skLineSegment(sketch, "E18.12.12.0", {"start": v(235.5, 66.28) * mm, "end": v(235.5, 82.1) * mm});
            skLineSegment(sketch, "E18.12.12.1", {"start": v(244.5, 66.28) * mm, "end": v(244.5, 82.1) * mm});
            skPoint(sketch, "E18.12.12.2", {"position": v(244.5, 64.28) * mm});
            skPoint(sketch, "E18.12.12.3", {"position": v(235.5, 64.28) * mm});
            skLineSegment(sketch, "E18.12.12.4", {"start": v(235.5, 82.1) * mm, "end": v(244.5, 82.1) * mm});
            skArc(sketch, "E18.12.12.5", {"start": v(235.5, 66.28) * mm, "mid": v(236.09, 64.87) * mm, "end": v(237.5, 64.28) * mm});
            skLineSegment(sketch, "E18.12.12.6", {"start": v(237.5, 64.28) * mm, "end": v(242.5, 64.28) * mm});
            skArc(sketch, "E18.12.12.7", {"start": v(242.5, 64.28) * mm, "mid": v(243.91, 64.87) * mm, "end": v(244.5, 66.28) * mm});
            skLineSegment(sketch, "E18.12.13.0", {"start": v(235.5, 31.64) * mm, "end": v(235.5, 47.46) * mm});
            skLineSegment(sketch, "E18.12.13.1", {"start": v(244.5, 31.64) * mm, "end": v(244.5, 47.46) * mm});
            skPoint(sketch, "E18.12.13.2", {"position": v(244.5, 29.64) * mm});
            skPoint(sketch, "E18.12.13.3", {"position": v(235.5, 29.64) * mm});
            skLineSegment(sketch, "E18.12.13.4", {"start": v(235.5, 47.46) * mm, "end": v(244.5, 47.46) * mm});
            skArc(sketch, "E18.12.13.5", {"start": v(235.5, 31.64) * mm, "mid": v(236.09, 30.23) * mm, "end": v(237.5, 29.64) * mm});
            skLineSegment(sketch, "E18.12.13.6", {"start": v(237.5, 29.64) * mm, "end": v(242.5, 29.64) * mm});
            skArc(sketch, "E18.12.13.7", {"start": v(242.5, 29.64) * mm, "mid": v(243.91, 30.23) * mm, "end": v(244.5, 31.64) * mm});
            skLineSegment(sketch, "E18.12.14.0", {"start": v(235.5, -3) * mm, "end": v(235.5, 12.82) * mm});
            skLineSegment(sketch, "E18.12.14.1", {"start": v(244.5, -3) * mm, "end": v(244.5, 12.82) * mm});
            skPoint(sketch, "E18.12.14.2", {"position": v(244.5, -5) * mm});
            skPoint(sketch, "E18.12.14.3", {"position": v(235.5, -5) * mm});
            skLineSegment(sketch, "E18.12.14.4", {"start": v(235.5, 12.82) * mm, "end": v(244.5, 12.82) * mm});
            skArc(sketch, "E18.12.14.5", {"start": v(235.5, -3) * mm, "mid": v(236.09, -4.41) * mm, "end": v(237.5, -5) * mm});
            skLineSegment(sketch, "E18.12.14.6", {"start": v(237.5, -5) * mm, "end": v(242.5, -5) * mm});
            skArc(sketch, "E18.12.14.7", {"start": v(242.5, -5) * mm, "mid": v(243.91, -4.41) * mm, "end": v(244.5, -3) * mm});
            skLineSegment(sketch, "E18.13.0.0", {"start": v(255.5, 481.97) * mm, "end": v(255.5, 497.8) * mm});
            skLineSegment(sketch, "E18.13.0.1", {"start": v(264.5, 481.97) * mm, "end": v(264.5, 497.8) * mm});
            skPoint(sketch, "E18.13.0.2", {"position": v(264.5, 479.97) * mm});
            skPoint(sketch, "E18.13.0.3", {"position": v(255.5, 479.97) * mm});
            skLineSegment(sketch, "E18.13.0.4", {"start": v(255.5, 497.8) * mm, "end": v(264.5, 497.8) * mm});
            skArc(sketch, "E18.13.0.5", {"start": v(255.5, 481.97) * mm, "mid": v(256.09, 480.56) * mm, "end": v(257.5, 479.97) * mm});
            skLineSegment(sketch, "E18.13.0.6", {"start": v(257.5, 479.97) * mm, "end": v(262.5, 479.97) * mm});
            skArc(sketch, "E18.13.0.7", {"start": v(262.5, 479.97) * mm, "mid": v(263.91, 480.56) * mm, "end": v(264.5, 481.97) * mm});
            skLineSegment(sketch, "E18.13.1.0", {"start": v(255.5, 447.33) * mm, "end": v(255.5, 463.15) * mm});
            skLineSegment(sketch, "E18.13.1.1", {"start": v(264.5, 447.33) * mm, "end": v(264.5, 463.15) * mm});
            skPoint(sketch, "E18.13.1.2", {"position": v(264.5, 445.33) * mm});
            skPoint(sketch, "E18.13.1.3", {"position": v(255.5, 445.33) * mm});
            skLineSegment(sketch, "E18.13.1.4", {"start": v(255.5, 463.15) * mm, "end": v(264.5, 463.15) * mm});
            skArc(sketch, "E18.13.1.5", {"start": v(255.5, 447.33) * mm, "mid": v(256.09, 445.92) * mm, "end": v(257.5, 445.33) * mm});
            skLineSegment(sketch, "E18.13.1.6", {"start": v(257.5, 445.33) * mm, "end": v(262.5, 445.33) * mm});
            skArc(sketch, "E18.13.1.7", {"start": v(262.5, 445.33) * mm, "mid": v(263.91, 445.92) * mm, "end": v(264.5, 447.33) * mm});
            skLineSegment(sketch, "E18.13.2.0", {"start": v(255.5, 412.7) * mm, "end": v(255.5, 428.51) * mm});
            skLineSegment(sketch, "E18.13.2.1", {"start": v(264.5, 412.7) * mm, "end": v(264.5, 428.51) * mm});
            skPoint(sketch, "E18.13.2.2", {"position": v(264.5, 410.7) * mm});
            skPoint(sketch, "E18.13.2.3", {"position": v(255.5, 410.7) * mm});
            skLineSegment(sketch, "E18.13.2.4", {"start": v(255.5, 428.51) * mm, "end": v(264.5, 428.51) * mm});
            skArc(sketch, "E18.13.2.5", {"start": v(255.5, 412.7) * mm, "mid": v(256.09, 411.28) * mm, "end": v(257.5, 410.7) * mm});
            skLineSegment(sketch, "E18.13.2.6", {"start": v(257.5, 410.7) * mm, "end": v(262.5, 410.7) * mm});
            skArc(sketch, "E18.13.2.7", {"start": v(262.5, 410.7) * mm, "mid": v(263.91, 411.28) * mm, "end": v(264.5, 412.7) * mm});
            skLineSegment(sketch, "E18.13.3.0", {"start": v(255.5, 378.05) * mm, "end": v(255.5, 393.87) * mm});
            skLineSegment(sketch, "E18.13.3.1", {"start": v(264.5, 378.05) * mm, "end": v(264.5, 393.87) * mm});
            skPoint(sketch, "E18.13.3.2", {"position": v(264.5, 376.05) * mm});
            skPoint(sketch, "E18.13.3.3", {"position": v(255.5, 376.05) * mm});
            skLineSegment(sketch, "E18.13.3.4", {"start": v(255.5, 393.87) * mm, "end": v(264.5, 393.87) * mm});
            skArc(sketch, "E18.13.3.5", {"start": v(255.5, 378.05) * mm, "mid": v(256.09, 376.64) * mm, "end": v(257.5, 376.05) * mm});
            skLineSegment(sketch, "E18.13.3.6", {"start": v(257.5, 376.05) * mm, "end": v(262.5, 376.05) * mm});
            skArc(sketch, "E18.13.3.7", {"start": v(262.5, 376.05) * mm, "mid": v(263.91, 376.64) * mm, "end": v(264.5, 378.05) * mm});
            skLineSegment(sketch, "E18.13.4.0", {"start": v(255.5, 343.41) * mm, "end": v(255.5, 359.23) * mm});
            skLineSegment(sketch, "E18.13.4.1", {"start": v(264.5, 343.41) * mm, "end": v(264.5, 359.23) * mm});
            skPoint(sketch, "E18.13.4.2", {"position": v(264.5, 341.41) * mm});
            skPoint(sketch, "E18.13.4.3", {"position": v(255.5, 341.41) * mm});
            skLineSegment(sketch, "E18.13.4.4", {"start": v(255.5, 359.23) * mm, "end": v(264.5, 359.23) * mm});
            skArc(sketch, "E18.13.4.5", {"start": v(255.5, 343.41) * mm, "mid": v(256.09, 342) * mm, "end": v(257.5, 341.41) * mm});
            skLineSegment(sketch, "E18.13.4.6", {"start": v(257.5, 341.41) * mm, "end": v(262.5, 341.41) * mm});
            skArc(sketch, "E18.13.4.7", {"start": v(262.5, 341.41) * mm, "mid": v(263.91, 342) * mm, "end": v(264.5, 343.41) * mm});
            skLineSegment(sketch, "E18.13.5.0", {"start": v(255.5, 308.77) * mm, "end": v(255.5, 324.59) * mm});
            skLineSegment(sketch, "E18.13.5.1", {"start": v(264.5, 308.77) * mm, "end": v(264.5, 324.59) * mm});
            skPoint(sketch, "E18.13.5.2", {"position": v(264.5, 306.77) * mm});
            skPoint(sketch, "E18.13.5.3", {"position": v(255.5, 306.77) * mm});
            skLineSegment(sketch, "E18.13.5.4", {"start": v(255.5, 324.59) * mm, "end": v(264.5, 324.59) * mm});
            skArc(sketch, "E18.13.5.5", {"start": v(255.5, 308.77) * mm, "mid": v(256.09, 307.35) * mm, "end": v(257.5, 306.77) * mm});
            skLineSegment(sketch, "E18.13.5.6", {"start": v(257.5, 306.77) * mm, "end": v(262.5, 306.77) * mm});
            skArc(sketch, "E18.13.5.7", {"start": v(262.5, 306.77) * mm, "mid": v(263.91, 307.35) * mm, "end": v(264.5, 308.77) * mm});
            skLineSegment(sketch, "E18.13.6.0", {"start": v(255.5, 274.13) * mm, "end": v(255.5, 289.95) * mm});
            skLineSegment(sketch, "E18.13.6.1", {"start": v(264.5, 274.13) * mm, "end": v(264.5, 289.95) * mm});
            skPoint(sketch, "E18.13.6.2", {"position": v(264.5, 272.13) * mm});
            skPoint(sketch, "E18.13.6.3", {"position": v(255.5, 272.13) * mm});
            skLineSegment(sketch, "E18.13.6.4", {"start": v(255.5, 289.95) * mm, "end": v(264.5, 289.95) * mm});
            skArc(sketch, "E18.13.6.5", {"start": v(255.5, 274.13) * mm, "mid": v(256.09, 272.71) * mm, "end": v(257.5, 272.13) * mm});
            skLineSegment(sketch, "E18.13.6.6", {"start": v(257.5, 272.13) * mm, "end": v(262.5, 272.13) * mm});
            skArc(sketch, "E18.13.6.7", {"start": v(262.5, 272.13) * mm, "mid": v(263.91, 272.71) * mm, "end": v(264.5, 274.13) * mm});
            skLineSegment(sketch, "E18.13.7.0", {"start": v(255.5, 239.49) * mm, "end": v(255.5, 255.3) * mm});
            skLineSegment(sketch, "E18.13.7.1", {"start": v(264.5, 239.49) * mm, "end": v(264.5, 255.3) * mm});
            skPoint(sketch, "E18.13.7.2", {"position": v(264.5, 237.49) * mm});
            skPoint(sketch, "E18.13.7.3", {"position": v(255.5, 237.49) * mm});
            skLineSegment(sketch, "E18.13.7.4", {"start": v(255.5, 255.3) * mm, "end": v(264.5, 255.3) * mm});
            skArc(sketch, "E18.13.7.5", {"start": v(255.5, 239.49) * mm, "mid": v(256.09, 238.07) * mm, "end": v(257.5, 237.49) * mm});
            skLineSegment(sketch, "E18.13.7.6", {"start": v(257.5, 237.49) * mm, "end": v(262.5, 237.49) * mm});
            skArc(sketch, "E18.13.7.7", {"start": v(262.5, 237.49) * mm, "mid": v(263.91, 238.07) * mm, "end": v(264.5, 239.49) * mm});
            skLineSegment(sketch, "E18.13.8.0", {"start": v(255.5, 204.85) * mm, "end": v(255.5, 220.67) * mm});
            skLineSegment(sketch, "E18.13.8.1", {"start": v(264.5, 204.85) * mm, "end": v(264.5, 220.67) * mm});
            skPoint(sketch, "E18.13.8.2", {"position": v(264.5, 202.85) * mm});
            skPoint(sketch, "E18.13.8.3", {"position": v(255.5, 202.85) * mm});
            skLineSegment(sketch, "E18.13.8.4", {"start": v(255.5, 220.67) * mm, "end": v(264.5, 220.67) * mm});
            skArc(sketch, "E18.13.8.5", {"start": v(255.5, 204.85) * mm, "mid": v(256.09, 203.43) * mm, "end": v(257.5, 202.85) * mm});
            skLineSegment(sketch, "E18.13.8.6", {"start": v(257.5, 202.85) * mm, "end": v(262.5, 202.85) * mm});
            skArc(sketch, "E18.13.8.7", {"start": v(262.5, 202.85) * mm, "mid": v(263.91, 203.43) * mm, "end": v(264.5, 204.85) * mm});
            skLineSegment(sketch, "E18.13.9.0", {"start": v(255.5, 170.2) * mm, "end": v(255.5, 186.03) * mm});
            skLineSegment(sketch, "E18.13.9.1", {"start": v(264.5, 170.2) * mm, "end": v(264.5, 186.03) * mm});
            skPoint(sketch, "E18.13.9.2", {"position": v(264.5, 168.2) * mm});
            skPoint(sketch, "E18.13.9.3", {"position": v(255.5, 168.2) * mm});
            skLineSegment(sketch, "E18.13.9.4", {"start": v(255.5, 186.03) * mm, "end": v(264.5, 186.03) * mm});
            skArc(sketch, "E18.13.9.5", {"start": v(255.5, 170.2) * mm, "mid": v(256.09, 168.8) * mm, "end": v(257.5, 168.2) * mm});
            skLineSegment(sketch, "E18.13.9.6", {"start": v(257.5, 168.2) * mm, "end": v(262.5, 168.2) * mm});
            skArc(sketch, "E18.13.9.7", {"start": v(262.5, 168.2) * mm, "mid": v(263.91, 168.8) * mm, "end": v(264.5, 170.2) * mm});
            skLineSegment(sketch, "E18.13.10.0", {"start": v(255.5, 135.56) * mm, "end": v(255.5, 151.38) * mm});
            skLineSegment(sketch, "E18.13.10.1", {"start": v(264.5, 135.56) * mm, "end": v(264.5, 151.38) * mm});
            skPoint(sketch, "E18.13.10.2", {"position": v(264.5, 133.56) * mm});
            skPoint(sketch, "E18.13.10.3", {"position": v(255.5, 133.56) * mm});
            skLineSegment(sketch, "E18.13.10.4", {"start": v(255.5, 151.38) * mm, "end": v(264.5, 151.38) * mm});
            skArc(sketch, "E18.13.10.5", {"start": v(255.5, 135.56) * mm, "mid": v(256.09, 134.15) * mm, "end": v(257.5, 133.56) * mm});
            skLineSegment(sketch, "E18.13.10.6", {"start": v(257.5, 133.56) * mm, "end": v(262.5, 133.56) * mm});
            skArc(sketch, "E18.13.10.7", {"start": v(262.5, 133.56) * mm, "mid": v(263.91, 134.15) * mm, "end": v(264.5, 135.56) * mm});
            skLineSegment(sketch, "E18.13.11.0", {"start": v(255.5, 100.92) * mm, "end": v(255.5, 116.74) * mm});
            skLineSegment(sketch, "E18.13.11.1", {"start": v(264.5, 100.92) * mm, "end": v(264.5, 116.74) * mm});
            skPoint(sketch, "E18.13.11.2", {"position": v(264.5, 98.92) * mm});
            skPoint(sketch, "E18.13.11.3", {"position": v(255.5, 98.92) * mm});
            skLineSegment(sketch, "E18.13.11.4", {"start": v(255.5, 116.74) * mm, "end": v(264.5, 116.74) * mm});
            skArc(sketch, "E18.13.11.5", {"start": v(255.5, 100.92) * mm, "mid": v(256.09, 99.5) * mm, "end": v(257.5, 98.92) * mm});
            skLineSegment(sketch, "E18.13.11.6", {"start": v(257.5, 98.92) * mm, "end": v(262.5, 98.92) * mm});
            skArc(sketch, "E18.13.11.7", {"start": v(262.5, 98.92) * mm, "mid": v(263.91, 99.5) * mm, "end": v(264.5, 100.92) * mm});
            skLineSegment(sketch, "E18.13.12.0", {"start": v(255.5, 66.28) * mm, "end": v(255.5, 82.1) * mm});
            skLineSegment(sketch, "E18.13.12.1", {"start": v(264.5, 66.28) * mm, "end": v(264.5, 82.1) * mm});
            skPoint(sketch, "E18.13.12.2", {"position": v(264.5, 64.28) * mm});
            skPoint(sketch, "E18.13.12.3", {"position": v(255.5, 64.28) * mm});
            skLineSegment(sketch, "E18.13.12.4", {"start": v(255.5, 82.1) * mm, "end": v(264.5, 82.1) * mm});
            skArc(sketch, "E18.13.12.5", {"start": v(255.5, 66.28) * mm, "mid": v(256.09, 64.87) * mm, "end": v(257.5, 64.28) * mm});
            skLineSegment(sketch, "E18.13.12.6", {"start": v(257.5, 64.28) * mm, "end": v(262.5, 64.28) * mm});
            skArc(sketch, "E18.13.12.7", {"start": v(262.5, 64.28) * mm, "mid": v(263.91, 64.87) * mm, "end": v(264.5, 66.28) * mm});
            skLineSegment(sketch, "E18.13.13.0", {"start": v(255.5, 31.64) * mm, "end": v(255.5, 47.46) * mm});
            skLineSegment(sketch, "E18.13.13.1", {"start": v(264.5, 31.64) * mm, "end": v(264.5, 47.46) * mm});
            skPoint(sketch, "E18.13.13.2", {"position": v(264.5, 29.64) * mm});
            skPoint(sketch, "E18.13.13.3", {"position": v(255.5, 29.64) * mm});
            skLineSegment(sketch, "E18.13.13.4", {"start": v(255.5, 47.46) * mm, "end": v(264.5, 47.46) * mm});
            skArc(sketch, "E18.13.13.5", {"start": v(255.5, 31.64) * mm, "mid": v(256.09, 30.23) * mm, "end": v(257.5, 29.64) * mm});
            skLineSegment(sketch, "E18.13.13.6", {"start": v(257.5, 29.64) * mm, "end": v(262.5, 29.64) * mm});
            skArc(sketch, "E18.13.13.7", {"start": v(262.5, 29.64) * mm, "mid": v(263.91, 30.23) * mm, "end": v(264.5, 31.64) * mm});
            skLineSegment(sketch, "E18.13.14.0", {"start": v(255.5, -3) * mm, "end": v(255.5, 12.82) * mm});
            skLineSegment(sketch, "E18.13.14.1", {"start": v(264.5, -3) * mm, "end": v(264.5, 12.82) * mm});
            skPoint(sketch, "E18.13.14.2", {"position": v(264.5, -5) * mm});
            skPoint(sketch, "E18.13.14.3", {"position": v(255.5, -5) * mm});
            skLineSegment(sketch, "E18.13.14.4", {"start": v(255.5, 12.82) * mm, "end": v(264.5, 12.82) * mm});
            skArc(sketch, "E18.13.14.5", {"start": v(255.5, -3) * mm, "mid": v(256.09, -4.41) * mm, "end": v(257.5, -5) * mm});
            skLineSegment(sketch, "E18.13.14.6", {"start": v(257.5, -5) * mm, "end": v(262.5, -5) * mm});
            skArc(sketch, "E18.13.14.7", {"start": v(262.5, -5) * mm, "mid": v(263.91, -4.41) * mm, "end": v(264.5, -3) * mm});
            skLineSegment(sketch, "E18.14.0.0", {"start": v(275.5, 481.97) * mm, "end": v(275.5, 497.8) * mm});
            skLineSegment(sketch, "E18.14.0.1", {"start": v(284.5, 481.97) * mm, "end": v(284.5, 497.8) * mm});
            skPoint(sketch, "E18.14.0.2", {"position": v(284.5, 479.97) * mm});
            skPoint(sketch, "E18.14.0.3", {"position": v(275.5, 479.97) * mm});
            skLineSegment(sketch, "E18.14.0.4", {"start": v(275.5, 497.8) * mm, "end": v(284.5, 497.8) * mm});
            skArc(sketch, "E18.14.0.5", {"start": v(275.5, 481.97) * mm, "mid": v(276.09, 480.56) * mm, "end": v(277.5, 479.97) * mm});
            skLineSegment(sketch, "E18.14.0.6", {"start": v(277.5, 479.97) * mm, "end": v(282.5, 479.97) * mm});
            skArc(sketch, "E18.14.0.7", {"start": v(282.5, 479.97) * mm, "mid": v(283.91, 480.56) * mm, "end": v(284.5, 481.97) * mm});
            skLineSegment(sketch, "E18.14.1.0", {"start": v(275.5, 447.33) * mm, "end": v(275.5, 463.15) * mm});
            skLineSegment(sketch, "E18.14.1.1", {"start": v(284.5, 447.33) * mm, "end": v(284.5, 463.15) * mm});
            skPoint(sketch, "E18.14.1.2", {"position": v(284.5, 445.33) * mm});
            skPoint(sketch, "E18.14.1.3", {"position": v(275.5, 445.33) * mm});
            skLineSegment(sketch, "E18.14.1.4", {"start": v(275.5, 463.15) * mm, "end": v(284.5, 463.15) * mm});
            skArc(sketch, "E18.14.1.5", {"start": v(275.5, 447.33) * mm, "mid": v(276.09, 445.92) * mm, "end": v(277.5, 445.33) * mm});
            skLineSegment(sketch, "E18.14.1.6", {"start": v(277.5, 445.33) * mm, "end": v(282.5, 445.33) * mm});
            skArc(sketch, "E18.14.1.7", {"start": v(282.5, 445.33) * mm, "mid": v(283.91, 445.92) * mm, "end": v(284.5, 447.33) * mm});
            skLineSegment(sketch, "E18.14.2.0", {"start": v(275.5, 412.7) * mm, "end": v(275.5, 428.51) * mm});
            skLineSegment(sketch, "E18.14.2.1", {"start": v(284.5, 412.7) * mm, "end": v(284.5, 428.51) * mm});
            skPoint(sketch, "E18.14.2.2", {"position": v(284.5, 410.7) * mm});
            skPoint(sketch, "E18.14.2.3", {"position": v(275.5, 410.7) * mm});
            skLineSegment(sketch, "E18.14.2.4", {"start": v(275.5, 428.51) * mm, "end": v(284.5, 428.51) * mm});
            skArc(sketch, "E18.14.2.5", {"start": v(275.5, 412.7) * mm, "mid": v(276.09, 411.28) * mm, "end": v(277.5, 410.7) * mm});
            skLineSegment(sketch, "E18.14.2.6", {"start": v(277.5, 410.7) * mm, "end": v(282.5, 410.7) * mm});
            skArc(sketch, "E18.14.2.7", {"start": v(282.5, 410.7) * mm, "mid": v(283.91, 411.28) * mm, "end": v(284.5, 412.7) * mm});
            skLineSegment(sketch, "E18.14.3.0", {"start": v(275.5, 378.05) * mm, "end": v(275.5, 393.87) * mm});
            skLineSegment(sketch, "E18.14.3.1", {"start": v(284.5, 378.05) * mm, "end": v(284.5, 393.87) * mm});
            skPoint(sketch, "E18.14.3.2", {"position": v(284.5, 376.05) * mm});
            skPoint(sketch, "E18.14.3.3", {"position": v(275.5, 376.05) * mm});
            skLineSegment(sketch, "E18.14.3.4", {"start": v(275.5, 393.87) * mm, "end": v(284.5, 393.87) * mm});
            skArc(sketch, "E18.14.3.5", {"start": v(275.5, 378.05) * mm, "mid": v(276.09, 376.64) * mm, "end": v(277.5, 376.05) * mm});
            skLineSegment(sketch, "E18.14.3.6", {"start": v(277.5, 376.05) * mm, "end": v(282.5, 376.05) * mm});
            skArc(sketch, "E18.14.3.7", {"start": v(282.5, 376.05) * mm, "mid": v(283.91, 376.64) * mm, "end": v(284.5, 378.05) * mm});
            skLineSegment(sketch, "E18.14.4.0", {"start": v(275.5, 343.41) * mm, "end": v(275.5, 359.23) * mm});
            skLineSegment(sketch, "E18.14.4.1", {"start": v(284.5, 343.41) * mm, "end": v(284.5, 359.23) * mm});
            skPoint(sketch, "E18.14.4.2", {"position": v(284.5, 341.41) * mm});
            skPoint(sketch, "E18.14.4.3", {"position": v(275.5, 341.41) * mm});
            skLineSegment(sketch, "E18.14.4.4", {"start": v(275.5, 359.23) * mm, "end": v(284.5, 359.23) * mm});
            skArc(sketch, "E18.14.4.5", {"start": v(275.5, 343.41) * mm, "mid": v(276.09, 342) * mm, "end": v(277.5, 341.41) * mm});
            skLineSegment(sketch, "E18.14.4.6", {"start": v(277.5, 341.41) * mm, "end": v(282.5, 341.41) * mm});
            skArc(sketch, "E18.14.4.7", {"start": v(282.5, 341.41) * mm, "mid": v(283.91, 342) * mm, "end": v(284.5, 343.41) * mm});
            skLineSegment(sketch, "E18.14.5.0", {"start": v(275.5, 308.77) * mm, "end": v(275.5, 324.59) * mm});
            skLineSegment(sketch, "E18.14.5.1", {"start": v(284.5, 308.77) * mm, "end": v(284.5, 324.59) * mm});
            skPoint(sketch, "E18.14.5.2", {"position": v(284.5, 306.77) * mm});
            skPoint(sketch, "E18.14.5.3", {"position": v(275.5, 306.77) * mm});
            skLineSegment(sketch, "E18.14.5.4", {"start": v(275.5, 324.59) * mm, "end": v(284.5, 324.59) * mm});
            skArc(sketch, "E18.14.5.5", {"start": v(275.5, 308.77) * mm, "mid": v(276.09, 307.35) * mm, "end": v(277.5, 306.77) * mm});
            skLineSegment(sketch, "E18.14.5.6", {"start": v(277.5, 306.77) * mm, "end": v(282.5, 306.77) * mm});
            skArc(sketch, "E18.14.5.7", {"start": v(282.5, 306.77) * mm, "mid": v(283.91, 307.35) * mm, "end": v(284.5, 308.77) * mm});
            skLineSegment(sketch, "E18.14.6.0", {"start": v(275.5, 274.13) * mm, "end": v(275.5, 289.95) * mm});
            skLineSegment(sketch, "E18.14.6.1", {"start": v(284.5, 274.13) * mm, "end": v(284.5, 289.95) * mm});
            skPoint(sketch, "E18.14.6.2", {"position": v(284.5, 272.13) * mm});
            skPoint(sketch, "E18.14.6.3", {"position": v(275.5, 272.13) * mm});
            skLineSegment(sketch, "E18.14.6.4", {"start": v(275.5, 289.95) * mm, "end": v(284.5, 289.95) * mm});
            skArc(sketch, "E18.14.6.5", {"start": v(275.5, 274.13) * mm, "mid": v(276.09, 272.71) * mm, "end": v(277.5, 272.13) * mm});
            skLineSegment(sketch, "E18.14.6.6", {"start": v(277.5, 272.13) * mm, "end": v(282.5, 272.13) * mm});
            skArc(sketch, "E18.14.6.7", {"start": v(282.5, 272.13) * mm, "mid": v(283.91, 272.71) * mm, "end": v(284.5, 274.13) * mm});
            skLineSegment(sketch, "E18.14.7.0", {"start": v(275.5, 239.49) * mm, "end": v(275.5, 255.3) * mm});
            skLineSegment(sketch, "E18.14.7.1", {"start": v(284.5, 239.49) * mm, "end": v(284.5, 255.3) * mm});
            skPoint(sketch, "E18.14.7.2", {"position": v(284.5, 237.49) * mm});
            skPoint(sketch, "E18.14.7.3", {"position": v(275.5, 237.49) * mm});
            skLineSegment(sketch, "E18.14.7.4", {"start": v(275.5, 255.3) * mm, "end": v(284.5, 255.3) * mm});
            skArc(sketch, "E18.14.7.5", {"start": v(275.5, 239.49) * mm, "mid": v(276.09, 238.07) * mm, "end": v(277.5, 237.49) * mm});
            skLineSegment(sketch, "E18.14.7.6", {"start": v(277.5, 237.49) * mm, "end": v(282.5, 237.49) * mm});
            skArc(sketch, "E18.14.7.7", {"start": v(282.5, 237.49) * mm, "mid": v(283.91, 238.07) * mm, "end": v(284.5, 239.49) * mm});
            skLineSegment(sketch, "E18.14.8.0", {"start": v(275.5, 204.85) * mm, "end": v(275.5, 220.67) * mm});
            skLineSegment(sketch, "E18.14.8.1", {"start": v(284.5, 204.85) * mm, "end": v(284.5, 220.67) * mm});
            skPoint(sketch, "E18.14.8.2", {"position": v(284.5, 202.85) * mm});
            skPoint(sketch, "E18.14.8.3", {"position": v(275.5, 202.85) * mm});
            skLineSegment(sketch, "E18.14.8.4", {"start": v(275.5, 220.67) * mm, "end": v(284.5, 220.67) * mm});
            skArc(sketch, "E18.14.8.5", {"start": v(275.5, 204.85) * mm, "mid": v(276.09, 203.43) * mm, "end": v(277.5, 202.85) * mm});
            skLineSegment(sketch, "E18.14.8.6", {"start": v(277.5, 202.85) * mm, "end": v(282.5, 202.85) * mm});
            skArc(sketch, "E18.14.8.7", {"start": v(282.5, 202.85) * mm, "mid": v(283.91, 203.43) * mm, "end": v(284.5, 204.85) * mm});
            skLineSegment(sketch, "E18.14.9.0", {"start": v(275.5, 170.2) * mm, "end": v(275.5, 186.03) * mm});
            skLineSegment(sketch, "E18.14.9.1", {"start": v(284.5, 170.2) * mm, "end": v(284.5, 186.03) * mm});
            skPoint(sketch, "E18.14.9.2", {"position": v(284.5, 168.2) * mm});
            skPoint(sketch, "E18.14.9.3", {"position": v(275.5, 168.2) * mm});
            skLineSegment(sketch, "E18.14.9.4", {"start": v(275.5, 186.03) * mm, "end": v(284.5, 186.03) * mm});
            skArc(sketch, "E18.14.9.5", {"start": v(275.5, 170.2) * mm, "mid": v(276.09, 168.8) * mm, "end": v(277.5, 168.2) * mm});
            skLineSegment(sketch, "E18.14.9.6", {"start": v(277.5, 168.2) * mm, "end": v(282.5, 168.2) * mm});
            skArc(sketch, "E18.14.9.7", {"start": v(282.5, 168.2) * mm, "mid": v(283.91, 168.8) * mm, "end": v(284.5, 170.2) * mm});
            skLineSegment(sketch, "E18.14.10.0", {"start": v(275.5, 135.56) * mm, "end": v(275.5, 151.38) * mm});
            skLineSegment(sketch, "E18.14.10.1", {"start": v(284.5, 135.56) * mm, "end": v(284.5, 151.38) * mm});
            skPoint(sketch, "E18.14.10.2", {"position": v(284.5, 133.56) * mm});
            skPoint(sketch, "E18.14.10.3", {"position": v(275.5, 133.56) * mm});
            skLineSegment(sketch, "E18.14.10.4", {"start": v(275.5, 151.38) * mm, "end": v(284.5, 151.38) * mm});
            skArc(sketch, "E18.14.10.5", {"start": v(275.5, 135.56) * mm, "mid": v(276.09, 134.15) * mm, "end": v(277.5, 133.56) * mm});
            skLineSegment(sketch, "E18.14.10.6", {"start": v(277.5, 133.56) * mm, "end": v(282.5, 133.56) * mm});
            skArc(sketch, "E18.14.10.7", {"start": v(282.5, 133.56) * mm, "mid": v(283.91, 134.15) * mm, "end": v(284.5, 135.56) * mm});
            skLineSegment(sketch, "E18.14.11.0", {"start": v(275.5, 100.92) * mm, "end": v(275.5, 116.74) * mm});
            skLineSegment(sketch, "E18.14.11.1", {"start": v(284.5, 100.92) * mm, "end": v(284.5, 116.74) * mm});
            skPoint(sketch, "E18.14.11.2", {"position": v(284.5, 98.92) * mm});
            skPoint(sketch, "E18.14.11.3", {"position": v(275.5, 98.92) * mm});
            skLineSegment(sketch, "E18.14.11.4", {"start": v(275.5, 116.74) * mm, "end": v(284.5, 116.74) * mm});
            skArc(sketch, "E18.14.11.5", {"start": v(275.5, 100.92) * mm, "mid": v(276.09, 99.5) * mm, "end": v(277.5, 98.92) * mm});
            skLineSegment(sketch, "E18.14.11.6", {"start": v(277.5, 98.92) * mm, "end": v(282.5, 98.92) * mm});
            skArc(sketch, "E18.14.11.7", {"start": v(282.5, 98.92) * mm, "mid": v(283.91, 99.5) * mm, "end": v(284.5, 100.92) * mm});
            skLineSegment(sketch, "E18.14.12.0", {"start": v(275.5, 66.28) * mm, "end": v(275.5, 82.1) * mm});
            skLineSegment(sketch, "E18.14.12.1", {"start": v(284.5, 66.28) * mm, "end": v(284.5, 82.1) * mm});
            skPoint(sketch, "E18.14.12.2", {"position": v(284.5, 64.28) * mm});
            skPoint(sketch, "E18.14.12.3", {"position": v(275.5, 64.28) * mm});
            skLineSegment(sketch, "E18.14.12.4", {"start": v(275.5, 82.1) * mm, "end": v(284.5, 82.1) * mm});
            skArc(sketch, "E18.14.12.5", {"start": v(275.5, 66.28) * mm, "mid": v(276.09, 64.87) * mm, "end": v(277.5, 64.28) * mm});
            skLineSegment(sketch, "E18.14.12.6", {"start": v(277.5, 64.28) * mm, "end": v(282.5, 64.28) * mm});
            skArc(sketch, "E18.14.12.7", {"start": v(282.5, 64.28) * mm, "mid": v(283.91, 64.87) * mm, "end": v(284.5, 66.28) * mm});
            skLineSegment(sketch, "E18.14.13.0", {"start": v(275.5, 31.64) * mm, "end": v(275.5, 47.46) * mm});
            skLineSegment(sketch, "E18.14.13.1", {"start": v(284.5, 31.64) * mm, "end": v(284.5, 47.46) * mm});
            skPoint(sketch, "E18.14.13.2", {"position": v(284.5, 29.64) * mm});
            skPoint(sketch, "E18.14.13.3", {"position": v(275.5, 29.64) * mm});
            skLineSegment(sketch, "E18.14.13.4", {"start": v(275.5, 47.46) * mm, "end": v(284.5, 47.46) * mm});
            skArc(sketch, "E18.14.13.5", {"start": v(275.5, 31.64) * mm, "mid": v(276.09, 30.23) * mm, "end": v(277.5, 29.64) * mm});
            skLineSegment(sketch, "E18.14.13.6", {"start": v(277.5, 29.64) * mm, "end": v(282.5, 29.64) * mm});
            skArc(sketch, "E18.14.13.7", {"start": v(282.5, 29.64) * mm, "mid": v(283.91, 30.23) * mm, "end": v(284.5, 31.64) * mm});
            skLineSegment(sketch, "E18.14.14.0", {"start": v(275.5, -3) * mm, "end": v(275.5, 12.82) * mm});
            skLineSegment(sketch, "E18.14.14.1", {"start": v(284.5, -3) * mm, "end": v(284.5, 12.82) * mm});
            skPoint(sketch, "E18.14.14.2", {"position": v(284.5, -5) * mm});
            skPoint(sketch, "E18.14.14.3", {"position": v(275.5, -5) * mm});
            skLineSegment(sketch, "E18.14.14.4", {"start": v(275.5, 12.82) * mm, "end": v(284.5, 12.82) * mm});
            skArc(sketch, "E18.14.14.5", {"start": v(275.5, -3) * mm, "mid": v(276.09, -4.41) * mm, "end": v(277.5, -5) * mm});
            skLineSegment(sketch, "E18.14.14.6", {"start": v(277.5, -5) * mm, "end": v(282.5, -5) * mm});
            skArc(sketch, "E18.14.14.7", {"start": v(282.5, -5) * mm, "mid": v(283.91, -4.41) * mm, "end": v(284.5, -3) * mm});
            skLineSegment(sketch, "E18.15.0.0", {"start": v(295.5, 481.97) * mm, "end": v(295.5, 497.8) * mm});
            skLineSegment(sketch, "E18.15.0.1", {"start": v(304.5, 481.97) * mm, "end": v(304.5, 497.8) * mm});
            skPoint(sketch, "E18.15.0.2", {"position": v(304.5, 479.97) * mm});
            skPoint(sketch, "E18.15.0.3", {"position": v(295.5, 479.97) * mm});
            skLineSegment(sketch, "E18.15.0.4", {"start": v(295.5, 497.8) * mm, "end": v(304.5, 497.8) * mm});
            skArc(sketch, "E18.15.0.5", {"start": v(295.5, 481.97) * mm, "mid": v(296.09, 480.56) * mm, "end": v(297.5, 479.97) * mm});
            skLineSegment(sketch, "E18.15.0.6", {"start": v(297.5, 479.97) * mm, "end": v(302.5, 479.97) * mm});
            skArc(sketch, "E18.15.0.7", {"start": v(302.5, 479.97) * mm, "mid": v(303.91, 480.56) * mm, "end": v(304.5, 481.97) * mm});
            skLineSegment(sketch, "E18.15.1.0", {"start": v(295.5, 447.33) * mm, "end": v(295.5, 463.15) * mm});
            skLineSegment(sketch, "E18.15.1.1", {"start": v(304.5, 447.33) * mm, "end": v(304.5, 463.15) * mm});
            skPoint(sketch, "E18.15.1.2", {"position": v(304.5, 445.33) * mm});
            skPoint(sketch, "E18.15.1.3", {"position": v(295.5, 445.33) * mm});
            skLineSegment(sketch, "E18.15.1.4", {"start": v(295.5, 463.15) * mm, "end": v(304.5, 463.15) * mm});
            skArc(sketch, "E18.15.1.5", {"start": v(295.5, 447.33) * mm, "mid": v(296.09, 445.92) * mm, "end": v(297.5, 445.33) * mm});
            skLineSegment(sketch, "E18.15.1.6", {"start": v(297.5, 445.33) * mm, "end": v(302.5, 445.33) * mm});
            skArc(sketch, "E18.15.1.7", {"start": v(302.5, 445.33) * mm, "mid": v(303.91, 445.92) * mm, "end": v(304.5, 447.33) * mm});
            skLineSegment(sketch, "E18.15.2.0", {"start": v(295.5, 412.7) * mm, "end": v(295.5, 428.51) * mm});
            skLineSegment(sketch, "E18.15.2.1", {"start": v(304.5, 412.7) * mm, "end": v(304.5, 428.51) * mm});
            skPoint(sketch, "E18.15.2.2", {"position": v(304.5, 410.7) * mm});
            skPoint(sketch, "E18.15.2.3", {"position": v(295.5, 410.7) * mm});
            skLineSegment(sketch, "E18.15.2.4", {"start": v(295.5, 428.51) * mm, "end": v(304.5, 428.51) * mm});
            skArc(sketch, "E18.15.2.5", {"start": v(295.5, 412.7) * mm, "mid": v(296.09, 411.28) * mm, "end": v(297.5, 410.7) * mm});
            skLineSegment(sketch, "E18.15.2.6", {"start": v(297.5, 410.7) * mm, "end": v(302.5, 410.7) * mm});
            skArc(sketch, "E18.15.2.7", {"start": v(302.5, 410.7) * mm, "mid": v(303.91, 411.28) * mm, "end": v(304.5, 412.7) * mm});
            skLineSegment(sketch, "E18.15.3.0", {"start": v(295.5, 378.05) * mm, "end": v(295.5, 393.87) * mm});
            skLineSegment(sketch, "E18.15.3.1", {"start": v(304.5, 378.05) * mm, "end": v(304.5, 393.87) * mm});
            skPoint(sketch, "E18.15.3.2", {"position": v(304.5, 376.05) * mm});
            skPoint(sketch, "E18.15.3.3", {"position": v(295.5, 376.05) * mm});
            skLineSegment(sketch, "E18.15.3.4", {"start": v(295.5, 393.87) * mm, "end": v(304.5, 393.87) * mm});
            skArc(sketch, "E18.15.3.5", {"start": v(295.5, 378.05) * mm, "mid": v(296.09, 376.64) * mm, "end": v(297.5, 376.05) * mm});
            skLineSegment(sketch, "E18.15.3.6", {"start": v(297.5, 376.05) * mm, "end": v(302.5, 376.05) * mm});
            skArc(sketch, "E18.15.3.7", {"start": v(302.5, 376.05) * mm, "mid": v(303.91, 376.64) * mm, "end": v(304.5, 378.05) * mm});
            skLineSegment(sketch, "E18.15.4.0", {"start": v(295.5, 343.41) * mm, "end": v(295.5, 359.23) * mm});
            skLineSegment(sketch, "E18.15.4.1", {"start": v(304.5, 343.41) * mm, "end": v(304.5, 359.23) * mm});
            skPoint(sketch, "E18.15.4.2", {"position": v(304.5, 341.41) * mm});
            skPoint(sketch, "E18.15.4.3", {"position": v(295.5, 341.41) * mm});
            skLineSegment(sketch, "E18.15.4.4", {"start": v(295.5, 359.23) * mm, "end": v(304.5, 359.23) * mm});
            skArc(sketch, "E18.15.4.5", {"start": v(295.5, 343.41) * mm, "mid": v(296.09, 342) * mm, "end": v(297.5, 341.41) * mm});
            skLineSegment(sketch, "E18.15.4.6", {"start": v(297.5, 341.41) * mm, "end": v(302.5, 341.41) * mm});
            skArc(sketch, "E18.15.4.7", {"start": v(302.5, 341.41) * mm, "mid": v(303.91, 342) * mm, "end": v(304.5, 343.41) * mm});
            skLineSegment(sketch, "E18.15.5.0", {"start": v(295.5, 308.77) * mm, "end": v(295.5, 324.59) * mm});
            skLineSegment(sketch, "E18.15.5.1", {"start": v(304.5, 308.77) * mm, "end": v(304.5, 324.59) * mm});
            skPoint(sketch, "E18.15.5.2", {"position": v(304.5, 306.77) * mm});
            skPoint(sketch, "E18.15.5.3", {"position": v(295.5, 306.77) * mm});
            skLineSegment(sketch, "E18.15.5.4", {"start": v(295.5, 324.59) * mm, "end": v(304.5, 324.59) * mm});
            skArc(sketch, "E18.15.5.5", {"start": v(295.5, 308.77) * mm, "mid": v(296.09, 307.35) * mm, "end": v(297.5, 306.77) * mm});
            skLineSegment(sketch, "E18.15.5.6", {"start": v(297.5, 306.77) * mm, "end": v(302.5, 306.77) * mm});
            skArc(sketch, "E18.15.5.7", {"start": v(302.5, 306.77) * mm, "mid": v(303.91, 307.35) * mm, "end": v(304.5, 308.77) * mm});
            skLineSegment(sketch, "E18.15.6.0", {"start": v(295.5, 274.13) * mm, "end": v(295.5, 289.95) * mm});
            skLineSegment(sketch, "E18.15.6.1", {"start": v(304.5, 274.13) * mm, "end": v(304.5, 289.95) * mm});
            skPoint(sketch, "E18.15.6.2", {"position": v(304.5, 272.13) * mm});
            skPoint(sketch, "E18.15.6.3", {"position": v(295.5, 272.13) * mm});
            skLineSegment(sketch, "E18.15.6.4", {"start": v(295.5, 289.95) * mm, "end": v(304.5, 289.95) * mm});
            skArc(sketch, "E18.15.6.5", {"start": v(295.5, 274.13) * mm, "mid": v(296.09, 272.71) * mm, "end": v(297.5, 272.13) * mm});
            skLineSegment(sketch, "E18.15.6.6", {"start": v(297.5, 272.13) * mm, "end": v(302.5, 272.13) * mm});
            skArc(sketch, "E18.15.6.7", {"start": v(302.5, 272.13) * mm, "mid": v(303.91, 272.71) * mm, "end": v(304.5, 274.13) * mm});
            skLineSegment(sketch, "E18.15.7.0", {"start": v(295.5, 239.49) * mm, "end": v(295.5, 255.3) * mm});
            skLineSegment(sketch, "E18.15.7.1", {"start": v(304.5, 239.49) * mm, "end": v(304.5, 255.3) * mm});
            skPoint(sketch, "E18.15.7.2", {"position": v(304.5, 237.49) * mm});
            skPoint(sketch, "E18.15.7.3", {"position": v(295.5, 237.49) * mm});
            skLineSegment(sketch, "E18.15.7.4", {"start": v(295.5, 255.3) * mm, "end": v(304.5, 255.3) * mm});
            skArc(sketch, "E18.15.7.5", {"start": v(295.5, 239.49) * mm, "mid": v(296.09, 238.07) * mm, "end": v(297.5, 237.49) * mm});
            skLineSegment(sketch, "E18.15.7.6", {"start": v(297.5, 237.49) * mm, "end": v(302.5, 237.49) * mm});
            skArc(sketch, "E18.15.7.7", {"start": v(302.5, 237.49) * mm, "mid": v(303.91, 238.07) * mm, "end": v(304.5, 239.49) * mm});
            skLineSegment(sketch, "E18.15.8.0", {"start": v(295.5, 204.85) * mm, "end": v(295.5, 220.67) * mm});
            skLineSegment(sketch, "E18.15.8.1", {"start": v(304.5, 204.85) * mm, "end": v(304.5, 220.67) * mm});
            skPoint(sketch, "E18.15.8.2", {"position": v(304.5, 202.85) * mm});
            skPoint(sketch, "E18.15.8.3", {"position": v(295.5, 202.85) * mm});
            skLineSegment(sketch, "E18.15.8.4", {"start": v(295.5, 220.67) * mm, "end": v(304.5, 220.67) * mm});
            skArc(sketch, "E18.15.8.5", {"start": v(295.5, 204.85) * mm, "mid": v(296.09, 203.43) * mm, "end": v(297.5, 202.85) * mm});
            skLineSegment(sketch, "E18.15.8.6", {"start": v(297.5, 202.85) * mm, "end": v(302.5, 202.85) * mm});
            skArc(sketch, "E18.15.8.7", {"start": v(302.5, 202.85) * mm, "mid": v(303.91, 203.43) * mm, "end": v(304.5, 204.85) * mm});
            skLineSegment(sketch, "E18.15.9.0", {"start": v(295.5, 170.2) * mm, "end": v(295.5, 186.03) * mm});
            skLineSegment(sketch, "E18.15.9.1", {"start": v(304.5, 170.2) * mm, "end": v(304.5, 186.03) * mm});
            skPoint(sketch, "E18.15.9.2", {"position": v(304.5, 168.2) * mm});
            skPoint(sketch, "E18.15.9.3", {"position": v(295.5, 168.2) * mm});
            skLineSegment(sketch, "E18.15.9.4", {"start": v(295.5, 186.03) * mm, "end": v(304.5, 186.03) * mm});
            skArc(sketch, "E18.15.9.5", {"start": v(295.5, 170.2) * mm, "mid": v(296.09, 168.8) * mm, "end": v(297.5, 168.2) * mm});
            skLineSegment(sketch, "E18.15.9.6", {"start": v(297.5, 168.2) * mm, "end": v(302.5, 168.2) * mm});
            skArc(sketch, "E18.15.9.7", {"start": v(302.5, 168.2) * mm, "mid": v(303.91, 168.8) * mm, "end": v(304.5, 170.2) * mm});
            skLineSegment(sketch, "E18.15.10.0", {"start": v(295.5, 135.56) * mm, "end": v(295.5, 151.38) * mm});
            skLineSegment(sketch, "E18.15.10.1", {"start": v(304.5, 135.56) * mm, "end": v(304.5, 151.38) * mm});
            skPoint(sketch, "E18.15.10.2", {"position": v(304.5, 133.56) * mm});
            skPoint(sketch, "E18.15.10.3", {"position": v(295.5, 133.56) * mm});
            skLineSegment(sketch, "E18.15.10.4", {"start": v(295.5, 151.38) * mm, "end": v(304.5, 151.38) * mm});
            skArc(sketch, "E18.15.10.5", {"start": v(295.5, 135.56) * mm, "mid": v(296.09, 134.15) * mm, "end": v(297.5, 133.56) * mm});
            skLineSegment(sketch, "E18.15.10.6", {"start": v(297.5, 133.56) * mm, "end": v(302.5, 133.56) * mm});
            skArc(sketch, "E18.15.10.7", {"start": v(302.5, 133.56) * mm, "mid": v(303.91, 134.15) * mm, "end": v(304.5, 135.56) * mm});
            skLineSegment(sketch, "E18.15.11.0", {"start": v(295.5, 100.92) * mm, "end": v(295.5, 116.74) * mm});
            skLineSegment(sketch, "E18.15.11.1", {"start": v(304.5, 100.92) * mm, "end": v(304.5, 116.74) * mm});
            skPoint(sketch, "E18.15.11.2", {"position": v(304.5, 98.92) * mm});
            skPoint(sketch, "E18.15.11.3", {"position": v(295.5, 98.92) * mm});
            skLineSegment(sketch, "E18.15.11.4", {"start": v(295.5, 116.74) * mm, "end": v(304.5, 116.74) * mm});
            skArc(sketch, "E18.15.11.5", {"start": v(295.5, 100.92) * mm, "mid": v(296.09, 99.5) * mm, "end": v(297.5, 98.92) * mm});
            skLineSegment(sketch, "E18.15.11.6", {"start": v(297.5, 98.92) * mm, "end": v(302.5, 98.92) * mm});
            skArc(sketch, "E18.15.11.7", {"start": v(302.5, 98.92) * mm, "mid": v(303.91, 99.5) * mm, "end": v(304.5, 100.92) * mm});
            skLineSegment(sketch, "E18.15.12.0", {"start": v(295.5, 66.28) * mm, "end": v(295.5, 82.1) * mm});
            skLineSegment(sketch, "E18.15.12.1", {"start": v(304.5, 66.28) * mm, "end": v(304.5, 82.1) * mm});
            skPoint(sketch, "E18.15.12.2", {"position": v(304.5, 64.28) * mm});
            skPoint(sketch, "E18.15.12.3", {"position": v(295.5, 64.28) * mm});
            skLineSegment(sketch, "E18.15.12.4", {"start": v(295.5, 82.1) * mm, "end": v(304.5, 82.1) * mm});
            skArc(sketch, "E18.15.12.5", {"start": v(295.5, 66.28) * mm, "mid": v(296.09, 64.87) * mm, "end": v(297.5, 64.28) * mm});
            skLineSegment(sketch, "E18.15.12.6", {"start": v(297.5, 64.28) * mm, "end": v(302.5, 64.28) * mm});
            skArc(sketch, "E18.15.12.7", {"start": v(302.5, 64.28) * mm, "mid": v(303.91, 64.87) * mm, "end": v(304.5, 66.28) * mm});
            skLineSegment(sketch, "E18.15.13.0", {"start": v(295.5, 31.64) * mm, "end": v(295.5, 47.46) * mm});
            skLineSegment(sketch, "E18.15.13.1", {"start": v(304.5, 31.64) * mm, "end": v(304.5, 47.46) * mm});
            skPoint(sketch, "E18.15.13.2", {"position": v(304.5, 29.64) * mm});
            skPoint(sketch, "E18.15.13.3", {"position": v(295.5, 29.64) * mm});
            skLineSegment(sketch, "E18.15.13.4", {"start": v(295.5, 47.46) * mm, "end": v(304.5, 47.46) * mm});
            skArc(sketch, "E18.15.13.5", {"start": v(295.5, 31.64) * mm, "mid": v(296.09, 30.23) * mm, "end": v(297.5, 29.64) * mm});
            skLineSegment(sketch, "E18.15.13.6", {"start": v(297.5, 29.64) * mm, "end": v(302.5, 29.64) * mm});
            skArc(sketch, "E18.15.13.7", {"start": v(302.5, 29.64) * mm, "mid": v(303.91, 30.23) * mm, "end": v(304.5, 31.64) * mm});
            skLineSegment(sketch, "E18.15.14.0", {"start": v(295.5, -3) * mm, "end": v(295.5, 12.82) * mm});
            skLineSegment(sketch, "E18.15.14.1", {"start": v(304.5, -3) * mm, "end": v(304.5, 12.82) * mm});
            skPoint(sketch, "E18.15.14.2", {"position": v(304.5, -5) * mm});
            skPoint(sketch, "E18.15.14.3", {"position": v(295.5, -5) * mm});
            skLineSegment(sketch, "E18.15.14.4", {"start": v(295.5, 12.82) * mm, "end": v(304.5, 12.82) * mm});
            skArc(sketch, "E18.15.14.5", {"start": v(295.5, -3) * mm, "mid": v(296.09, -4.41) * mm, "end": v(297.5, -5) * mm});
            skLineSegment(sketch, "E18.15.14.6", {"start": v(297.5, -5) * mm, "end": v(302.5, -5) * mm});
            skArc(sketch, "E18.15.14.7", {"start": v(302.5, -5) * mm, "mid": v(303.91, -4.41) * mm, "end": v(304.5, -3) * mm});
            skLineSegment(sketch, "E18.16.0.0", {"start": v(315.5, 481.97) * mm, "end": v(315.5, 497.8) * mm});
            skLineSegment(sketch, "E18.16.0.1", {"start": v(324.5, 481.97) * mm, "end": v(324.5, 497.8) * mm});
            skPoint(sketch, "E18.16.0.2", {"position": v(324.5, 479.97) * mm});
            skPoint(sketch, "E18.16.0.3", {"position": v(315.5, 479.97) * mm});
            skLineSegment(sketch, "E18.16.0.4", {"start": v(315.5, 497.8) * mm, "end": v(324.5, 497.8) * mm});
            skArc(sketch, "E18.16.0.5", {"start": v(315.5, 481.97) * mm, "mid": v(316.09, 480.56) * mm, "end": v(317.5, 479.97) * mm});
            skLineSegment(sketch, "E18.16.0.6", {"start": v(317.5, 479.97) * mm, "end": v(322.5, 479.97) * mm});
            skArc(sketch, "E18.16.0.7", {"start": v(322.5, 479.97) * mm, "mid": v(323.91, 480.56) * mm, "end": v(324.5, 481.97) * mm});
            skLineSegment(sketch, "E18.16.1.0", {"start": v(315.5, 447.33) * mm, "end": v(315.5, 463.15) * mm});
            skLineSegment(sketch, "E18.16.1.1", {"start": v(324.5, 447.33) * mm, "end": v(324.5, 463.15) * mm});
            skPoint(sketch, "E18.16.1.2", {"position": v(324.5, 445.33) * mm});
            skPoint(sketch, "E18.16.1.3", {"position": v(315.5, 445.33) * mm});
            skLineSegment(sketch, "E18.16.1.4", {"start": v(315.5, 463.15) * mm, "end": v(324.5, 463.15) * mm});
            skArc(sketch, "E18.16.1.5", {"start": v(315.5, 447.33) * mm, "mid": v(316.09, 445.92) * mm, "end": v(317.5, 445.33) * mm});
            skLineSegment(sketch, "E18.16.1.6", {"start": v(317.5, 445.33) * mm, "end": v(322.5, 445.33) * mm});
            skArc(sketch, "E18.16.1.7", {"start": v(322.5, 445.33) * mm, "mid": v(323.91, 445.92) * mm, "end": v(324.5, 447.33) * mm});
            skLineSegment(sketch, "E18.16.2.0", {"start": v(315.5, 412.7) * mm, "end": v(315.5, 428.51) * mm});
            skLineSegment(sketch, "E18.16.2.1", {"start": v(324.5, 412.7) * mm, "end": v(324.5, 428.51) * mm});
            skPoint(sketch, "E18.16.2.2", {"position": v(324.5, 410.7) * mm});
            skPoint(sketch, "E18.16.2.3", {"position": v(315.5, 410.7) * mm});
            skLineSegment(sketch, "E18.16.2.4", {"start": v(315.5, 428.51) * mm, "end": v(324.5, 428.51) * mm});
            skArc(sketch, "E18.16.2.5", {"start": v(315.5, 412.7) * mm, "mid": v(316.09, 411.28) * mm, "end": v(317.5, 410.7) * mm});
            skLineSegment(sketch, "E18.16.2.6", {"start": v(317.5, 410.7) * mm, "end": v(322.5, 410.7) * mm});
            skArc(sketch, "E18.16.2.7", {"start": v(322.5, 410.7) * mm, "mid": v(323.91, 411.28) * mm, "end": v(324.5, 412.7) * mm});
            skLineSegment(sketch, "E18.16.3.0", {"start": v(315.5, 378.05) * mm, "end": v(315.5, 393.87) * mm});
            skLineSegment(sketch, "E18.16.3.1", {"start": v(324.5, 378.05) * mm, "end": v(324.5, 393.87) * mm});
            skPoint(sketch, "E18.16.3.2", {"position": v(324.5, 376.05) * mm});
            skPoint(sketch, "E18.16.3.3", {"position": v(315.5, 376.05) * mm});
            skLineSegment(sketch, "E18.16.3.4", {"start": v(315.5, 393.87) * mm, "end": v(324.5, 393.87) * mm});
            skArc(sketch, "E18.16.3.5", {"start": v(315.5, 378.05) * mm, "mid": v(316.09, 376.64) * mm, "end": v(317.5, 376.05) * mm});
            skLineSegment(sketch, "E18.16.3.6", {"start": v(317.5, 376.05) * mm, "end": v(322.5, 376.05) * mm});
            skArc(sketch, "E18.16.3.7", {"start": v(322.5, 376.05) * mm, "mid": v(323.91, 376.64) * mm, "end": v(324.5, 378.05) * mm});
            skLineSegment(sketch, "E18.16.4.0", {"start": v(315.5, 343.41) * mm, "end": v(315.5, 359.23) * mm});
            skLineSegment(sketch, "E18.16.4.1", {"start": v(324.5, 343.41) * mm, "end": v(324.5, 359.23) * mm});
            skPoint(sketch, "E18.16.4.2", {"position": v(324.5, 341.41) * mm});
            skPoint(sketch, "E18.16.4.3", {"position": v(315.5, 341.41) * mm});
            skLineSegment(sketch, "E18.16.4.4", {"start": v(315.5, 359.23) * mm, "end": v(324.5, 359.23) * mm});
            skArc(sketch, "E18.16.4.5", {"start": v(315.5, 343.41) * mm, "mid": v(316.09, 342) * mm, "end": v(317.5, 341.41) * mm});
            skLineSegment(sketch, "E18.16.4.6", {"start": v(317.5, 341.41) * mm, "end": v(322.5, 341.41) * mm});
            skArc(sketch, "E18.16.4.7", {"start": v(322.5, 341.41) * mm, "mid": v(323.91, 342) * mm, "end": v(324.5, 343.41) * mm});
            skLineSegment(sketch, "E18.16.5.0", {"start": v(315.5, 308.77) * mm, "end": v(315.5, 324.59) * mm});
            skLineSegment(sketch, "E18.16.5.1", {"start": v(324.5, 308.77) * mm, "end": v(324.5, 324.59) * mm});
            skPoint(sketch, "E18.16.5.2", {"position": v(324.5, 306.77) * mm});
            skPoint(sketch, "E18.16.5.3", {"position": v(315.5, 306.77) * mm});
            skLineSegment(sketch, "E18.16.5.4", {"start": v(315.5, 324.59) * mm, "end": v(324.5, 324.59) * mm});
            skArc(sketch, "E18.16.5.5", {"start": v(315.5, 308.77) * mm, "mid": v(316.09, 307.35) * mm, "end": v(317.5, 306.77) * mm});
            skLineSegment(sketch, "E18.16.5.6", {"start": v(317.5, 306.77) * mm, "end": v(322.5, 306.77) * mm});
            skArc(sketch, "E18.16.5.7", {"start": v(322.5, 306.77) * mm, "mid": v(323.91, 307.35) * mm, "end": v(324.5, 308.77) * mm});
            skLineSegment(sketch, "E18.16.6.0", {"start": v(315.5, 274.13) * mm, "end": v(315.5, 289.95) * mm});
            skLineSegment(sketch, "E18.16.6.1", {"start": v(324.5, 274.13) * mm, "end": v(324.5, 289.95) * mm});
            skPoint(sketch, "E18.16.6.2", {"position": v(324.5, 272.13) * mm});
            skPoint(sketch, "E18.16.6.3", {"position": v(315.5, 272.13) * mm});
            skLineSegment(sketch, "E18.16.6.4", {"start": v(315.5, 289.95) * mm, "end": v(324.5, 289.95) * mm});
            skArc(sketch, "E18.16.6.5", {"start": v(315.5, 274.13) * mm, "mid": v(316.09, 272.71) * mm, "end": v(317.5, 272.13) * mm});
            skLineSegment(sketch, "E18.16.6.6", {"start": v(317.5, 272.13) * mm, "end": v(322.5, 272.13) * mm});
            skArc(sketch, "E18.16.6.7", {"start": v(322.5, 272.13) * mm, "mid": v(323.91, 272.71) * mm, "end": v(324.5, 274.13) * mm});
            skLineSegment(sketch, "E18.16.7.0", {"start": v(315.5, 239.49) * mm, "end": v(315.5, 255.3) * mm});
            skLineSegment(sketch, "E18.16.7.1", {"start": v(324.5, 239.49) * mm, "end": v(324.5, 255.3) * mm});
            skPoint(sketch, "E18.16.7.2", {"position": v(324.5, 237.49) * mm});
            skPoint(sketch, "E18.16.7.3", {"position": v(315.5, 237.49) * mm});
            skLineSegment(sketch, "E18.16.7.4", {"start": v(315.5, 255.3) * mm, "end": v(324.5, 255.3) * mm});
            skArc(sketch, "E18.16.7.5", {"start": v(315.5, 239.49) * mm, "mid": v(316.09, 238.07) * mm, "end": v(317.5, 237.49) * mm});
            skLineSegment(sketch, "E18.16.7.6", {"start": v(317.5, 237.49) * mm, "end": v(322.5, 237.49) * mm});
            skArc(sketch, "E18.16.7.7", {"start": v(322.5, 237.49) * mm, "mid": v(323.91, 238.07) * mm, "end": v(324.5, 239.49) * mm});
            skLineSegment(sketch, "E18.16.8.0", {"start": v(315.5, 204.85) * mm, "end": v(315.5, 220.67) * mm});
            skLineSegment(sketch, "E18.16.8.1", {"start": v(324.5, 204.85) * mm, "end": v(324.5, 220.67) * mm});
            skPoint(sketch, "E18.16.8.2", {"position": v(324.5, 202.85) * mm});
            skPoint(sketch, "E18.16.8.3", {"position": v(315.5, 202.85) * mm});
            skLineSegment(sketch, "E18.16.8.4", {"start": v(315.5, 220.67) * mm, "end": v(324.5, 220.67) * mm});
            skArc(sketch, "E18.16.8.5", {"start": v(315.5, 204.85) * mm, "mid": v(316.09, 203.43) * mm, "end": v(317.5, 202.85) * mm});
            skLineSegment(sketch, "E18.16.8.6", {"start": v(317.5, 202.85) * mm, "end": v(322.5, 202.85) * mm});
            skArc(sketch, "E18.16.8.7", {"start": v(322.5, 202.85) * mm, "mid": v(323.91, 203.43) * mm, "end": v(324.5, 204.85) * mm});
            skLineSegment(sketch, "E18.16.9.0", {"start": v(315.5, 170.2) * mm, "end": v(315.5, 186.03) * mm});
            skLineSegment(sketch, "E18.16.9.1", {"start": v(324.5, 170.2) * mm, "end": v(324.5, 186.03) * mm});
            skPoint(sketch, "E18.16.9.2", {"position": v(324.5, 168.2) * mm});
            skPoint(sketch, "E18.16.9.3", {"position": v(315.5, 168.2) * mm});
            skLineSegment(sketch, "E18.16.9.4", {"start": v(315.5, 186.03) * mm, "end": v(324.5, 186.03) * mm});
            skArc(sketch, "E18.16.9.5", {"start": v(315.5, 170.2) * mm, "mid": v(316.09, 168.8) * mm, "end": v(317.5, 168.2) * mm});
            skLineSegment(sketch, "E18.16.9.6", {"start": v(317.5, 168.2) * mm, "end": v(322.5, 168.2) * mm});
            skArc(sketch, "E18.16.9.7", {"start": v(322.5, 168.2) * mm, "mid": v(323.91, 168.8) * mm, "end": v(324.5, 170.2) * mm});
            skLineSegment(sketch, "E18.16.10.0", {"start": v(315.5, 135.56) * mm, "end": v(315.5, 151.38) * mm});
            skLineSegment(sketch, "E18.16.10.1", {"start": v(324.5, 135.56) * mm, "end": v(324.5, 151.38) * mm});
            skPoint(sketch, "E18.16.10.2", {"position": v(324.5, 133.56) * mm});
            skPoint(sketch, "E18.16.10.3", {"position": v(315.5, 133.56) * mm});
            skLineSegment(sketch, "E18.16.10.4", {"start": v(315.5, 151.38) * mm, "end": v(324.5, 151.38) * mm});
            skArc(sketch, "E18.16.10.5", {"start": v(315.5, 135.56) * mm, "mid": v(316.09, 134.15) * mm, "end": v(317.5, 133.56) * mm});
            skLineSegment(sketch, "E18.16.10.6", {"start": v(317.5, 133.56) * mm, "end": v(322.5, 133.56) * mm});
            skArc(sketch, "E18.16.10.7", {"start": v(322.5, 133.56) * mm, "mid": v(323.91, 134.15) * mm, "end": v(324.5, 135.56) * mm});
            skLineSegment(sketch, "E18.16.11.0", {"start": v(315.5, 100.92) * mm, "end": v(315.5, 116.74) * mm});
            skLineSegment(sketch, "E18.16.11.1", {"start": v(324.5, 100.92) * mm, "end": v(324.5, 116.74) * mm});
            skPoint(sketch, "E18.16.11.2", {"position": v(324.5, 98.92) * mm});
            skPoint(sketch, "E18.16.11.3", {"position": v(315.5, 98.92) * mm});
            skLineSegment(sketch, "E18.16.11.4", {"start": v(315.5, 116.74) * mm, "end": v(324.5, 116.74) * mm});
            skArc(sketch, "E18.16.11.5", {"start": v(315.5, 100.92) * mm, "mid": v(316.09, 99.5) * mm, "end": v(317.5, 98.92) * mm});
            skLineSegment(sketch, "E18.16.11.6", {"start": v(317.5, 98.92) * mm, "end": v(322.5, 98.92) * mm});
            skArc(sketch, "E18.16.11.7", {"start": v(322.5, 98.92) * mm, "mid": v(323.91, 99.5) * mm, "end": v(324.5, 100.92) * mm});
            skLineSegment(sketch, "E18.16.12.0", {"start": v(315.5, 66.28) * mm, "end": v(315.5, 82.1) * mm});
            skLineSegment(sketch, "E18.16.12.1", {"start": v(324.5, 66.28) * mm, "end": v(324.5, 82.1) * mm});
            skPoint(sketch, "E18.16.12.2", {"position": v(324.5, 64.28) * mm});
            skPoint(sketch, "E18.16.12.3", {"position": v(315.5, 64.28) * mm});
            skLineSegment(sketch, "E18.16.12.4", {"start": v(315.5, 82.1) * mm, "end": v(324.5, 82.1) * mm});
            skArc(sketch, "E18.16.12.5", {"start": v(315.5, 66.28) * mm, "mid": v(316.09, 64.87) * mm, "end": v(317.5, 64.28) * mm});
            skLineSegment(sketch, "E18.16.12.6", {"start": v(317.5, 64.28) * mm, "end": v(322.5, 64.28) * mm});
            skArc(sketch, "E18.16.12.7", {"start": v(322.5, 64.28) * mm, "mid": v(323.91, 64.87) * mm, "end": v(324.5, 66.28) * mm});
            skLineSegment(sketch, "E18.16.13.0", {"start": v(315.5, 31.64) * mm, "end": v(315.5, 47.46) * mm});
            skLineSegment(sketch, "E18.16.13.1", {"start": v(324.5, 31.64) * mm, "end": v(324.5, 47.46) * mm});
            skPoint(sketch, "E18.16.13.2", {"position": v(324.5, 29.64) * mm});
            skPoint(sketch, "E18.16.13.3", {"position": v(315.5, 29.64) * mm});
            skLineSegment(sketch, "E18.16.13.4", {"start": v(315.5, 47.46) * mm, "end": v(324.5, 47.46) * mm});
            skArc(sketch, "E18.16.13.5", {"start": v(315.5, 31.64) * mm, "mid": v(316.09, 30.23) * mm, "end": v(317.5, 29.64) * mm});
            skLineSegment(sketch, "E18.16.13.6", {"start": v(317.5, 29.64) * mm, "end": v(322.5, 29.64) * mm});
            skArc(sketch, "E18.16.13.7", {"start": v(322.5, 29.64) * mm, "mid": v(323.91, 30.23) * mm, "end": v(324.5, 31.64) * mm});
            skLineSegment(sketch, "E18.16.14.0", {"start": v(315.5, -3) * mm, "end": v(315.5, 12.82) * mm});
            skLineSegment(sketch, "E18.16.14.1", {"start": v(324.5, -3) * mm, "end": v(324.5, 12.82) * mm});
            skPoint(sketch, "E18.16.14.2", {"position": v(324.5, -5) * mm});
            skPoint(sketch, "E18.16.14.3", {"position": v(315.5, -5) * mm});
            skLineSegment(sketch, "E18.16.14.4", {"start": v(315.5, 12.82) * mm, "end": v(324.5, 12.82) * mm});
            skArc(sketch, "E18.16.14.5", {"start": v(315.5, -3) * mm, "mid": v(316.09, -4.41) * mm, "end": v(317.5, -5) * mm});
            skLineSegment(sketch, "E18.16.14.6", {"start": v(317.5, -5) * mm, "end": v(322.5, -5) * mm});
            skArc(sketch, "E18.16.14.7", {"start": v(322.5, -5) * mm, "mid": v(323.91, -4.41) * mm, "end": v(324.5, -3) * mm});
            skLineSegment(sketch, "E18.17.0.0", {"start": v(335.5, 481.97) * mm, "end": v(335.5, 497.8) * mm});
            skLineSegment(sketch, "E18.17.0.1", {"start": v(344.5, 481.97) * mm, "end": v(344.5, 497.8) * mm});
            skPoint(sketch, "E18.17.0.2", {"position": v(344.5, 479.97) * mm});
            skPoint(sketch, "E18.17.0.3", {"position": v(335.5, 479.97) * mm});
            skLineSegment(sketch, "E18.17.0.4", {"start": v(335.5, 497.8) * mm, "end": v(344.5, 497.8) * mm});
            skArc(sketch, "E18.17.0.5", {"start": v(335.5, 481.97) * mm, "mid": v(336.09, 480.56) * mm, "end": v(337.5, 479.97) * mm});
            skLineSegment(sketch, "E18.17.0.6", {"start": v(337.5, 479.97) * mm, "end": v(342.5, 479.97) * mm});
            skArc(sketch, "E18.17.0.7", {"start": v(342.5, 479.97) * mm, "mid": v(343.91, 480.56) * mm, "end": v(344.5, 481.97) * mm});
            skLineSegment(sketch, "E18.17.1.0", {"start": v(335.5, 447.33) * mm, "end": v(335.5, 463.15) * mm});
            skLineSegment(sketch, "E18.17.1.1", {"start": v(344.5, 447.33) * mm, "end": v(344.5, 463.15) * mm});
            skPoint(sketch, "E18.17.1.2", {"position": v(344.5, 445.33) * mm});
            skPoint(sketch, "E18.17.1.3", {"position": v(335.5, 445.33) * mm});
            skLineSegment(sketch, "E18.17.1.4", {"start": v(335.5, 463.15) * mm, "end": v(344.5, 463.15) * mm});
            skArc(sketch, "E18.17.1.5", {"start": v(335.5, 447.33) * mm, "mid": v(336.09, 445.92) * mm, "end": v(337.5, 445.33) * mm});
            skLineSegment(sketch, "E18.17.1.6", {"start": v(337.5, 445.33) * mm, "end": v(342.5, 445.33) * mm});
            skArc(sketch, "E18.17.1.7", {"start": v(342.5, 445.33) * mm, "mid": v(343.91, 445.92) * mm, "end": v(344.5, 447.33) * mm});
            skLineSegment(sketch, "E18.17.2.0", {"start": v(335.5, 412.7) * mm, "end": v(335.5, 428.51) * mm});
            skLineSegment(sketch, "E18.17.2.1", {"start": v(344.5, 412.7) * mm, "end": v(344.5, 428.51) * mm});
            skPoint(sketch, "E18.17.2.2", {"position": v(344.5, 410.7) * mm});
            skPoint(sketch, "E18.17.2.3", {"position": v(335.5, 410.7) * mm});
            skLineSegment(sketch, "E18.17.2.4", {"start": v(335.5, 428.51) * mm, "end": v(344.5, 428.51) * mm});
            skArc(sketch, "E18.17.2.5", {"start": v(335.5, 412.7) * mm, "mid": v(336.09, 411.28) * mm, "end": v(337.5, 410.7) * mm});
            skLineSegment(sketch, "E18.17.2.6", {"start": v(337.5, 410.7) * mm, "end": v(342.5, 410.7) * mm});
            skArc(sketch, "E18.17.2.7", {"start": v(342.5, 410.7) * mm, "mid": v(343.91, 411.28) * mm, "end": v(344.5, 412.7) * mm});
            skLineSegment(sketch, "E18.17.3.0", {"start": v(335.5, 378.05) * mm, "end": v(335.5, 393.87) * mm});
            skLineSegment(sketch, "E18.17.3.1", {"start": v(344.5, 378.05) * mm, "end": v(344.5, 393.87) * mm});
            skPoint(sketch, "E18.17.3.2", {"position": v(344.5, 376.05) * mm});
            skPoint(sketch, "E18.17.3.3", {"position": v(335.5, 376.05) * mm});
            skLineSegment(sketch, "E18.17.3.4", {"start": v(335.5, 393.87) * mm, "end": v(344.5, 393.87) * mm});
            skArc(sketch, "E18.17.3.5", {"start": v(335.5, 378.05) * mm, "mid": v(336.09, 376.64) * mm, "end": v(337.5, 376.05) * mm});
            skLineSegment(sketch, "E18.17.3.6", {"start": v(337.5, 376.05) * mm, "end": v(342.5, 376.05) * mm});
            skArc(sketch, "E18.17.3.7", {"start": v(342.5, 376.05) * mm, "mid": v(343.91, 376.64) * mm, "end": v(344.5, 378.05) * mm});
            skLineSegment(sketch, "E18.17.4.0", {"start": v(335.5, 343.41) * mm, "end": v(335.5, 359.23) * mm});
            skLineSegment(sketch, "E18.17.4.1", {"start": v(344.5, 343.41) * mm, "end": v(344.5, 359.23) * mm});
            skPoint(sketch, "E18.17.4.2", {"position": v(344.5, 341.41) * mm});
            skPoint(sketch, "E18.17.4.3", {"position": v(335.5, 341.41) * mm});
            skLineSegment(sketch, "E18.17.4.4", {"start": v(335.5, 359.23) * mm, "end": v(344.5, 359.23) * mm});
            skArc(sketch, "E18.17.4.5", {"start": v(335.5, 343.41) * mm, "mid": v(336.09, 342) * mm, "end": v(337.5, 341.41) * mm});
            skLineSegment(sketch, "E18.17.4.6", {"start": v(337.5, 341.41) * mm, "end": v(342.5, 341.41) * mm});
            skArc(sketch, "E18.17.4.7", {"start": v(342.5, 341.41) * mm, "mid": v(343.91, 342) * mm, "end": v(344.5, 343.41) * mm});
            skLineSegment(sketch, "E18.17.5.0", {"start": v(335.5, 308.77) * mm, "end": v(335.5, 324.59) * mm});
            skLineSegment(sketch, "E18.17.5.1", {"start": v(344.5, 308.77) * mm, "end": v(344.5, 324.59) * mm});
            skPoint(sketch, "E18.17.5.2", {"position": v(344.5, 306.77) * mm});
            skPoint(sketch, "E18.17.5.3", {"position": v(335.5, 306.77) * mm});
            skLineSegment(sketch, "E18.17.5.4", {"start": v(335.5, 324.59) * mm, "end": v(344.5, 324.59) * mm});
            skArc(sketch, "E18.17.5.5", {"start": v(335.5, 308.77) * mm, "mid": v(336.09, 307.35) * mm, "end": v(337.5, 306.77) * mm});
            skLineSegment(sketch, "E18.17.5.6", {"start": v(337.5, 306.77) * mm, "end": v(342.5, 306.77) * mm});
            skArc(sketch, "E18.17.5.7", {"start": v(342.5, 306.77) * mm, "mid": v(343.91, 307.35) * mm, "end": v(344.5, 308.77) * mm});
            skLineSegment(sketch, "E18.17.6.0", {"start": v(335.5, 274.13) * mm, "end": v(335.5, 289.95) * mm});
            skLineSegment(sketch, "E18.17.6.1", {"start": v(344.5, 274.13) * mm, "end": v(344.5, 289.95) * mm});
            skPoint(sketch, "E18.17.6.2", {"position": v(344.5, 272.13) * mm});
            skPoint(sketch, "E18.17.6.3", {"position": v(335.5, 272.13) * mm});
            skLineSegment(sketch, "E18.17.6.4", {"start": v(335.5, 289.95) * mm, "end": v(344.5, 289.95) * mm});
            skArc(sketch, "E18.17.6.5", {"start": v(335.5, 274.13) * mm, "mid": v(336.09, 272.71) * mm, "end": v(337.5, 272.13) * mm});
            skLineSegment(sketch, "E18.17.6.6", {"start": v(337.5, 272.13) * mm, "end": v(342.5, 272.13) * mm});
            skArc(sketch, "E18.17.6.7", {"start": v(342.5, 272.13) * mm, "mid": v(343.91, 272.71) * mm, "end": v(344.5, 274.13) * mm});
            skLineSegment(sketch, "E18.17.7.0", {"start": v(335.5, 239.49) * mm, "end": v(335.5, 255.3) * mm});
            skLineSegment(sketch, "E18.17.7.1", {"start": v(344.5, 239.49) * mm, "end": v(344.5, 255.3) * mm});
            skPoint(sketch, "E18.17.7.2", {"position": v(344.5, 237.49) * mm});
            skPoint(sketch, "E18.17.7.3", {"position": v(335.5, 237.49) * mm});
            skLineSegment(sketch, "E18.17.7.4", {"start": v(335.5, 255.3) * mm, "end": v(344.5, 255.3) * mm});
            skArc(sketch, "E18.17.7.5", {"start": v(335.5, 239.49) * mm, "mid": v(336.09, 238.07) * mm, "end": v(337.5, 237.49) * mm});
            skLineSegment(sketch, "E18.17.7.6", {"start": v(337.5, 237.49) * mm, "end": v(342.5, 237.49) * mm});
            skArc(sketch, "E18.17.7.7", {"start": v(342.5, 237.49) * mm, "mid": v(343.91, 238.07) * mm, "end": v(344.5, 239.49) * mm});
            skLineSegment(sketch, "E18.17.8.0", {"start": v(335.5, 204.85) * mm, "end": v(335.5, 220.67) * mm});
            skLineSegment(sketch, "E18.17.8.1", {"start": v(344.5, 204.85) * mm, "end": v(344.5, 220.67) * mm});
            skPoint(sketch, "E18.17.8.2", {"position": v(344.5, 202.85) * mm});
            skPoint(sketch, "E18.17.8.3", {"position": v(335.5, 202.85) * mm});
            skLineSegment(sketch, "E18.17.8.4", {"start": v(335.5, 220.67) * mm, "end": v(344.5, 220.67) * mm});
            skArc(sketch, "E18.17.8.5", {"start": v(335.5, 204.85) * mm, "mid": v(336.09, 203.43) * mm, "end": v(337.5, 202.85) * mm});
            skLineSegment(sketch, "E18.17.8.6", {"start": v(337.5, 202.85) * mm, "end": v(342.5, 202.85) * mm});
            skArc(sketch, "E18.17.8.7", {"start": v(342.5, 202.85) * mm, "mid": v(343.91, 203.43) * mm, "end": v(344.5, 204.85) * mm});
            skLineSegment(sketch, "E18.17.9.0", {"start": v(335.5, 170.2) * mm, "end": v(335.5, 186.03) * mm});
            skLineSegment(sketch, "E18.17.9.1", {"start": v(344.5, 170.2) * mm, "end": v(344.5, 186.03) * mm});
            skPoint(sketch, "E18.17.9.2", {"position": v(344.5, 168.2) * mm});
            skPoint(sketch, "E18.17.9.3", {"position": v(335.5, 168.2) * mm});
            skLineSegment(sketch, "E18.17.9.4", {"start": v(335.5, 186.03) * mm, "end": v(344.5, 186.03) * mm});
            skArc(sketch, "E18.17.9.5", {"start": v(335.5, 170.2) * mm, "mid": v(336.09, 168.8) * mm, "end": v(337.5, 168.2) * mm});
            skLineSegment(sketch, "E18.17.9.6", {"start": v(337.5, 168.2) * mm, "end": v(342.5, 168.2) * mm});
            skArc(sketch, "E18.17.9.7", {"start": v(342.5, 168.2) * mm, "mid": v(343.91, 168.8) * mm, "end": v(344.5, 170.2) * mm});
            skLineSegment(sketch, "E18.17.10.0", {"start": v(335.5, 135.56) * mm, "end": v(335.5, 151.38) * mm});
            skLineSegment(sketch, "E18.17.10.1", {"start": v(344.5, 135.56) * mm, "end": v(344.5, 151.38) * mm});
            skPoint(sketch, "E18.17.10.2", {"position": v(344.5, 133.56) * mm});
            skPoint(sketch, "E18.17.10.3", {"position": v(335.5, 133.56) * mm});
            skLineSegment(sketch, "E18.17.10.4", {"start": v(335.5, 151.38) * mm, "end": v(344.5, 151.38) * mm});
            skArc(sketch, "E18.17.10.5", {"start": v(335.5, 135.56) * mm, "mid": v(336.09, 134.15) * mm, "end": v(337.5, 133.56) * mm});
            skLineSegment(sketch, "E18.17.10.6", {"start": v(337.5, 133.56) * mm, "end": v(342.5, 133.56) * mm});
            skArc(sketch, "E18.17.10.7", {"start": v(342.5, 133.56) * mm, "mid": v(343.91, 134.15) * mm, "end": v(344.5, 135.56) * mm});
            skLineSegment(sketch, "E18.17.11.0", {"start": v(335.5, 100.92) * mm, "end": v(335.5, 116.74) * mm});
            skLineSegment(sketch, "E18.17.11.1", {"start": v(344.5, 100.92) * mm, "end": v(344.5, 116.74) * mm});
            skPoint(sketch, "E18.17.11.2", {"position": v(344.5, 98.92) * mm});
            skPoint(sketch, "E18.17.11.3", {"position": v(335.5, 98.92) * mm});
            skLineSegment(sketch, "E18.17.11.4", {"start": v(335.5, 116.74) * mm, "end": v(344.5, 116.74) * mm});
            skArc(sketch, "E18.17.11.5", {"start": v(335.5, 100.92) * mm, "mid": v(336.09, 99.5) * mm, "end": v(337.5, 98.92) * mm});
            skLineSegment(sketch, "E18.17.11.6", {"start": v(337.5, 98.92) * mm, "end": v(342.5, 98.92) * mm});
            skArc(sketch, "E18.17.11.7", {"start": v(342.5, 98.92) * mm, "mid": v(343.91, 99.5) * mm, "end": v(344.5, 100.92) * mm});
            skLineSegment(sketch, "E18.17.12.0", {"start": v(335.5, 66.28) * mm, "end": v(335.5, 82.1) * mm});
            skLineSegment(sketch, "E18.17.12.1", {"start": v(344.5, 66.28) * mm, "end": v(344.5, 82.1) * mm});
            skPoint(sketch, "E18.17.12.2", {"position": v(344.5, 64.28) * mm});
            skPoint(sketch, "E18.17.12.3", {"position": v(335.5, 64.28) * mm});
            skLineSegment(sketch, "E18.17.12.4", {"start": v(335.5, 82.1) * mm, "end": v(344.5, 82.1) * mm});
            skArc(sketch, "E18.17.12.5", {"start": v(335.5, 66.28) * mm, "mid": v(336.09, 64.87) * mm, "end": v(337.5, 64.28) * mm});
            skLineSegment(sketch, "E18.17.12.6", {"start": v(337.5, 64.28) * mm, "end": v(342.5, 64.28) * mm});
            skArc(sketch, "E18.17.12.7", {"start": v(342.5, 64.28) * mm, "mid": v(343.91, 64.87) * mm, "end": v(344.5, 66.28) * mm});
            skLineSegment(sketch, "E18.17.13.0", {"start": v(335.5, 31.64) * mm, "end": v(335.5, 47.46) * mm});
            skLineSegment(sketch, "E18.17.13.1", {"start": v(344.5, 31.64) * mm, "end": v(344.5, 47.46) * mm});
            skPoint(sketch, "E18.17.13.2", {"position": v(344.5, 29.64) * mm});
            skPoint(sketch, "E18.17.13.3", {"position": v(335.5, 29.64) * mm});
            skLineSegment(sketch, "E18.17.13.4", {"start": v(335.5, 47.46) * mm, "end": v(344.5, 47.46) * mm});
            skArc(sketch, "E18.17.13.5", {"start": v(335.5, 31.64) * mm, "mid": v(336.09, 30.23) * mm, "end": v(337.5, 29.64) * mm});
            skLineSegment(sketch, "E18.17.13.6", {"start": v(337.5, 29.64) * mm, "end": v(342.5, 29.64) * mm});
            skArc(sketch, "E18.17.13.7", {"start": v(342.5, 29.64) * mm, "mid": v(343.91, 30.23) * mm, "end": v(344.5, 31.64) * mm});
            skLineSegment(sketch, "E18.17.14.0", {"start": v(335.5, -3) * mm, "end": v(335.5, 12.82) * mm});
            skLineSegment(sketch, "E18.17.14.1", {"start": v(344.5, -3) * mm, "end": v(344.5, 12.82) * mm});
            skPoint(sketch, "E18.17.14.2", {"position": v(344.5, -5) * mm});
            skPoint(sketch, "E18.17.14.3", {"position": v(335.5, -5) * mm});
            skLineSegment(sketch, "E18.17.14.4", {"start": v(335.5, 12.82) * mm, "end": v(344.5, 12.82) * mm});
            skArc(sketch, "E18.17.14.5", {"start": v(335.5, -3) * mm, "mid": v(336.09, -4.41) * mm, "end": v(337.5, -5) * mm});
            skLineSegment(sketch, "E18.17.14.6", {"start": v(337.5, -5) * mm, "end": v(342.5, -5) * mm});
            skArc(sketch, "E18.17.14.7", {"start": v(342.5, -5) * mm, "mid": v(343.91, -4.41) * mm, "end": v(344.5, -3) * mm});
            skLineSegment(sketch, "E18.18.0.0", {"start": v(355.5, 481.97) * mm, "end": v(355.5, 497.8) * mm});
            skLineSegment(sketch, "E18.18.0.1", {"start": v(364.5, 481.97) * mm, "end": v(364.5, 497.8) * mm});
            skPoint(sketch, "E18.18.0.2", {"position": v(364.5, 479.97) * mm});
            skPoint(sketch, "E18.18.0.3", {"position": v(355.5, 479.97) * mm});
            skLineSegment(sketch, "E18.18.0.4", {"start": v(355.5, 497.8) * mm, "end": v(364.5, 497.8) * mm});
            skArc(sketch, "E18.18.0.5", {"start": v(355.5, 481.97) * mm, "mid": v(356.09, 480.56) * mm, "end": v(357.5, 479.97) * mm});
            skLineSegment(sketch, "E18.18.0.6", {"start": v(357.5, 479.97) * mm, "end": v(362.5, 479.97) * mm});
            skArc(sketch, "E18.18.0.7", {"start": v(362.5, 479.97) * mm, "mid": v(363.91, 480.56) * mm, "end": v(364.5, 481.97) * mm});
            skLineSegment(sketch, "E18.18.1.0", {"start": v(355.5, 447.33) * mm, "end": v(355.5, 463.15) * mm});
            skLineSegment(sketch, "E18.18.1.1", {"start": v(364.5, 447.33) * mm, "end": v(364.5, 463.15) * mm});
            skPoint(sketch, "E18.18.1.2", {"position": v(364.5, 445.33) * mm});
            skPoint(sketch, "E18.18.1.3", {"position": v(355.5, 445.33) * mm});
            skLineSegment(sketch, "E18.18.1.4", {"start": v(355.5, 463.15) * mm, "end": v(364.5, 463.15) * mm});
            skArc(sketch, "E18.18.1.5", {"start": v(355.5, 447.33) * mm, "mid": v(356.09, 445.92) * mm, "end": v(357.5, 445.33) * mm});
            skLineSegment(sketch, "E18.18.1.6", {"start": v(357.5, 445.33) * mm, "end": v(362.5, 445.33) * mm});
            skArc(sketch, "E18.18.1.7", {"start": v(362.5, 445.33) * mm, "mid": v(363.91, 445.92) * mm, "end": v(364.5, 447.33) * mm});
            skLineSegment(sketch, "E18.18.2.0", {"start": v(355.5, 412.7) * mm, "end": v(355.5, 428.51) * mm});
            skLineSegment(sketch, "E18.18.2.1", {"start": v(364.5, 412.7) * mm, "end": v(364.5, 428.51) * mm});
            skPoint(sketch, "E18.18.2.2", {"position": v(364.5, 410.7) * mm});
            skPoint(sketch, "E18.18.2.3", {"position": v(355.5, 410.7) * mm});
            skLineSegment(sketch, "E18.18.2.4", {"start": v(355.5, 428.51) * mm, "end": v(364.5, 428.51) * mm});
            skArc(sketch, "E18.18.2.5", {"start": v(355.5, 412.7) * mm, "mid": v(356.09, 411.28) * mm, "end": v(357.5, 410.7) * mm});
            skLineSegment(sketch, "E18.18.2.6", {"start": v(357.5, 410.7) * mm, "end": v(362.5, 410.7) * mm});
            skArc(sketch, "E18.18.2.7", {"start": v(362.5, 410.7) * mm, "mid": v(363.91, 411.28) * mm, "end": v(364.5, 412.7) * mm});
            skLineSegment(sketch, "E18.18.3.0", {"start": v(355.5, 378.05) * mm, "end": v(355.5, 393.87) * mm});
            skLineSegment(sketch, "E18.18.3.1", {"start": v(364.5, 378.05) * mm, "end": v(364.5, 393.87) * mm});
            skPoint(sketch, "E18.18.3.2", {"position": v(364.5, 376.05) * mm});
            skPoint(sketch, "E18.18.3.3", {"position": v(355.5, 376.05) * mm});
            skLineSegment(sketch, "E18.18.3.4", {"start": v(355.5, 393.87) * mm, "end": v(364.5, 393.87) * mm});
            skArc(sketch, "E18.18.3.5", {"start": v(355.5, 378.05) * mm, "mid": v(356.09, 376.64) * mm, "end": v(357.5, 376.05) * mm});
            skLineSegment(sketch, "E18.18.3.6", {"start": v(357.5, 376.05) * mm, "end": v(362.5, 376.05) * mm});
            skArc(sketch, "E18.18.3.7", {"start": v(362.5, 376.05) * mm, "mid": v(363.91, 376.64) * mm, "end": v(364.5, 378.05) * mm});
            skLineSegment(sketch, "E18.18.4.0", {"start": v(355.5, 343.41) * mm, "end": v(355.5, 359.23) * mm});
            skLineSegment(sketch, "E18.18.4.1", {"start": v(364.5, 343.41) * mm, "end": v(364.5, 359.23) * mm});
            skPoint(sketch, "E18.18.4.2", {"position": v(364.5, 341.41) * mm});
            skPoint(sketch, "E18.18.4.3", {"position": v(355.5, 341.41) * mm});
            skLineSegment(sketch, "E18.18.4.4", {"start": v(355.5, 359.23) * mm, "end": v(364.5, 359.23) * mm});
            skArc(sketch, "E18.18.4.5", {"start": v(355.5, 343.41) * mm, "mid": v(356.09, 342) * mm, "end": v(357.5, 341.41) * mm});
            skLineSegment(sketch, "E18.18.4.6", {"start": v(357.5, 341.41) * mm, "end": v(362.5, 341.41) * mm});
            skArc(sketch, "E18.18.4.7", {"start": v(362.5, 341.41) * mm, "mid": v(363.91, 342) * mm, "end": v(364.5, 343.41) * mm});
            skLineSegment(sketch, "E18.18.5.0", {"start": v(355.5, 308.77) * mm, "end": v(355.5, 324.59) * mm});
            skLineSegment(sketch, "E18.18.5.1", {"start": v(364.5, 308.77) * mm, "end": v(364.5, 324.59) * mm});
            skPoint(sketch, "E18.18.5.2", {"position": v(364.5, 306.77) * mm});
            skPoint(sketch, "E18.18.5.3", {"position": v(355.5, 306.77) * mm});
            skLineSegment(sketch, "E18.18.5.4", {"start": v(355.5, 324.59) * mm, "end": v(364.5, 324.59) * mm});
            skArc(sketch, "E18.18.5.5", {"start": v(355.5, 308.77) * mm, "mid": v(356.09, 307.35) * mm, "end": v(357.5, 306.77) * mm});
            skLineSegment(sketch, "E18.18.5.6", {"start": v(357.5, 306.77) * mm, "end": v(362.5, 306.77) * mm});
            skArc(sketch, "E18.18.5.7", {"start": v(362.5, 306.77) * mm, "mid": v(363.91, 307.35) * mm, "end": v(364.5, 308.77) * mm});
            skLineSegment(sketch, "E18.18.6.0", {"start": v(355.5, 274.13) * mm, "end": v(355.5, 289.95) * mm});
            skLineSegment(sketch, "E18.18.6.1", {"start": v(364.5, 274.13) * mm, "end": v(364.5, 289.95) * mm});
            skPoint(sketch, "E18.18.6.2", {"position": v(364.5, 272.13) * mm});
            skPoint(sketch, "E18.18.6.3", {"position": v(355.5, 272.13) * mm});
            skLineSegment(sketch, "E18.18.6.4", {"start": v(355.5, 289.95) * mm, "end": v(364.5, 289.95) * mm});
            skArc(sketch, "E18.18.6.5", {"start": v(355.5, 274.13) * mm, "mid": v(356.09, 272.71) * mm, "end": v(357.5, 272.13) * mm});
            skLineSegment(sketch, "E18.18.6.6", {"start": v(357.5, 272.13) * mm, "end": v(362.5, 272.13) * mm});
            skArc(sketch, "E18.18.6.7", {"start": v(362.5, 272.13) * mm, "mid": v(363.91, 272.71) * mm, "end": v(364.5, 274.13) * mm});
            skLineSegment(sketch, "E18.18.7.0", {"start": v(355.5, 239.49) * mm, "end": v(355.5, 255.3) * mm});
            skLineSegment(sketch, "E18.18.7.1", {"start": v(364.5, 239.49) * mm, "end": v(364.5, 255.3) * mm});
            skPoint(sketch, "E18.18.7.2", {"position": v(364.5, 237.49) * mm});
            skPoint(sketch, "E18.18.7.3", {"position": v(355.5, 237.49) * mm});
            skLineSegment(sketch, "E18.18.7.4", {"start": v(355.5, 255.3) * mm, "end": v(364.5, 255.3) * mm});
            skArc(sketch, "E18.18.7.5", {"start": v(355.5, 239.49) * mm, "mid": v(356.09, 238.07) * mm, "end": v(357.5, 237.49) * mm});
            skLineSegment(sketch, "E18.18.7.6", {"start": v(357.5, 237.49) * mm, "end": v(362.5, 237.49) * mm});
            skArc(sketch, "E18.18.7.7", {"start": v(362.5, 237.49) * mm, "mid": v(363.91, 238.07) * mm, "end": v(364.5, 239.49) * mm});
            skLineSegment(sketch, "E18.18.8.0", {"start": v(355.5, 204.85) * mm, "end": v(355.5, 220.67) * mm});
            skLineSegment(sketch, "E18.18.8.1", {"start": v(364.5, 204.85) * mm, "end": v(364.5, 220.67) * mm});
            skPoint(sketch, "E18.18.8.2", {"position": v(364.5, 202.85) * mm});
            skPoint(sketch, "E18.18.8.3", {"position": v(355.5, 202.85) * mm});
            skLineSegment(sketch, "E18.18.8.4", {"start": v(355.5, 220.67) * mm, "end": v(364.5, 220.67) * mm});
            skArc(sketch, "E18.18.8.5", {"start": v(355.5, 204.85) * mm, "mid": v(356.09, 203.43) * mm, "end": v(357.5, 202.85) * mm});
            skLineSegment(sketch, "E18.18.8.6", {"start": v(357.5, 202.85) * mm, "end": v(362.5, 202.85) * mm});
            skArc(sketch, "E18.18.8.7", {"start": v(362.5, 202.85) * mm, "mid": v(363.91, 203.43) * mm, "end": v(364.5, 204.85) * mm});
            skLineSegment(sketch, "E18.18.9.0", {"start": v(355.5, 170.2) * mm, "end": v(355.5, 186.03) * mm});
            skLineSegment(sketch, "E18.18.9.1", {"start": v(364.5, 170.2) * mm, "end": v(364.5, 186.03) * mm});
            skPoint(sketch, "E18.18.9.2", {"position": v(364.5, 168.2) * mm});
            skPoint(sketch, "E18.18.9.3", {"position": v(355.5, 168.2) * mm});
            skLineSegment(sketch, "E18.18.9.4", {"start": v(355.5, 186.03) * mm, "end": v(364.5, 186.03) * mm});
            skArc(sketch, "E18.18.9.5", {"start": v(355.5, 170.2) * mm, "mid": v(356.09, 168.8) * mm, "end": v(357.5, 168.2) * mm});
            skLineSegment(sketch, "E18.18.9.6", {"start": v(357.5, 168.2) * mm, "end": v(362.5, 168.2) * mm});
            skArc(sketch, "E18.18.9.7", {"start": v(362.5, 168.2) * mm, "mid": v(363.91, 168.8) * mm, "end": v(364.5, 170.2) * mm});
            skLineSegment(sketch, "E18.18.10.0", {"start": v(355.5, 135.56) * mm, "end": v(355.5, 151.38) * mm});
            skLineSegment(sketch, "E18.18.10.1", {"start": v(364.5, 135.56) * mm, "end": v(364.5, 151.38) * mm});
            skPoint(sketch, "E18.18.10.2", {"position": v(364.5, 133.56) * mm});
            skPoint(sketch, "E18.18.10.3", {"position": v(355.5, 133.56) * mm});
            skLineSegment(sketch, "E18.18.10.4", {"start": v(355.5, 151.38) * mm, "end": v(364.5, 151.38) * mm});
            skArc(sketch, "E18.18.10.5", {"start": v(355.5, 135.56) * mm, "mid": v(356.09, 134.15) * mm, "end": v(357.5, 133.56) * mm});
            skLineSegment(sketch, "E18.18.10.6", {"start": v(357.5, 133.56) * mm, "end": v(362.5, 133.56) * mm});
            skArc(sketch, "E18.18.10.7", {"start": v(362.5, 133.56) * mm, "mid": v(363.91, 134.15) * mm, "end": v(364.5, 135.56) * mm});
            skLineSegment(sketch, "E18.18.11.0", {"start": v(355.5, 100.92) * mm, "end": v(355.5, 116.74) * mm});
            skLineSegment(sketch, "E18.18.11.1", {"start": v(364.5, 100.92) * mm, "end": v(364.5, 116.74) * mm});
            skPoint(sketch, "E18.18.11.2", {"position": v(364.5, 98.92) * mm});
            skPoint(sketch, "E18.18.11.3", {"position": v(355.5, 98.92) * mm});
            skLineSegment(sketch, "E18.18.11.4", {"start": v(355.5, 116.74) * mm, "end": v(364.5, 116.74) * mm});
            skArc(sketch, "E18.18.11.5", {"start": v(355.5, 100.92) * mm, "mid": v(356.09, 99.5) * mm, "end": v(357.5, 98.92) * mm});
            skLineSegment(sketch, "E18.18.11.6", {"start": v(357.5, 98.92) * mm, "end": v(362.5, 98.92) * mm});
            skArc(sketch, "E18.18.11.7", {"start": v(362.5, 98.92) * mm, "mid": v(363.91, 99.5) * mm, "end": v(364.5, 100.92) * mm});
            skLineSegment(sketch, "E18.18.12.0", {"start": v(355.5, 66.28) * mm, "end": v(355.5, 82.1) * mm});
            skLineSegment(sketch, "E18.18.12.1", {"start": v(364.5, 66.28) * mm, "end": v(364.5, 82.1) * mm});
            skPoint(sketch, "E18.18.12.2", {"position": v(364.5, 64.28) * mm});
            skPoint(sketch, "E18.18.12.3", {"position": v(355.5, 64.28) * mm});
            skLineSegment(sketch, "E18.18.12.4", {"start": v(355.5, 82.1) * mm, "end": v(364.5, 82.1) * mm});
            skArc(sketch, "E18.18.12.5", {"start": v(355.5, 66.28) * mm, "mid": v(356.09, 64.87) * mm, "end": v(357.5, 64.28) * mm});
            skLineSegment(sketch, "E18.18.12.6", {"start": v(357.5, 64.28) * mm, "end": v(362.5, 64.28) * mm});
            skArc(sketch, "E18.18.12.7", {"start": v(362.5, 64.28) * mm, "mid": v(363.91, 64.87) * mm, "end": v(364.5, 66.28) * mm});
            skLineSegment(sketch, "E18.18.13.0", {"start": v(355.5, 31.64) * mm, "end": v(355.5, 47.46) * mm});
            skLineSegment(sketch, "E18.18.13.1", {"start": v(364.5, 31.64) * mm, "end": v(364.5, 47.46) * mm});
            skPoint(sketch, "E18.18.13.2", {"position": v(364.5, 29.64) * mm});
            skPoint(sketch, "E18.18.13.3", {"position": v(355.5, 29.64) * mm});
            skLineSegment(sketch, "E18.18.13.4", {"start": v(355.5, 47.46) * mm, "end": v(364.5, 47.46) * mm});
            skArc(sketch, "E18.18.13.5", {"start": v(355.5, 31.64) * mm, "mid": v(356.09, 30.23) * mm, "end": v(357.5, 29.64) * mm});
            skLineSegment(sketch, "E18.18.13.6", {"start": v(357.5, 29.64) * mm, "end": v(362.5, 29.64) * mm});
            skArc(sketch, "E18.18.13.7", {"start": v(362.5, 29.64) * mm, "mid": v(363.91, 30.23) * mm, "end": v(364.5, 31.64) * mm});
            skLineSegment(sketch, "E18.18.14.0", {"start": v(355.5, -3) * mm, "end": v(355.5, 12.82) * mm});
            skLineSegment(sketch, "E18.18.14.1", {"start": v(364.5, -3) * mm, "end": v(364.5, 12.82) * mm});
            skPoint(sketch, "E18.18.14.2", {"position": v(364.5, -5) * mm});
            skPoint(sketch, "E18.18.14.3", {"position": v(355.5, -5) * mm});
            skLineSegment(sketch, "E18.18.14.4", {"start": v(355.5, 12.82) * mm, "end": v(364.5, 12.82) * mm});
            skArc(sketch, "E18.18.14.5", {"start": v(355.5, -3) * mm, "mid": v(356.09, -4.41) * mm, "end": v(357.5, -5) * mm});
            skLineSegment(sketch, "E18.18.14.6", {"start": v(357.5, -5) * mm, "end": v(362.5, -5) * mm});
            skArc(sketch, "E18.18.14.7", {"start": v(362.5, -5) * mm, "mid": v(363.91, -4.41) * mm, "end": v(364.5, -3) * mm});
            skLineSegment(sketch, "E18.19.0.0", {"start": v(375.5, 481.97) * mm, "end": v(375.5, 497.8) * mm});
            skLineSegment(sketch, "E18.19.0.1", {"start": v(384.5, 481.97) * mm, "end": v(384.5, 497.8) * mm});
            skPoint(sketch, "E18.19.0.2", {"position": v(384.5, 479.97) * mm});
            skPoint(sketch, "E18.19.0.3", {"position": v(375.5, 479.97) * mm});
            skLineSegment(sketch, "E18.19.0.4", {"start": v(375.5, 497.8) * mm, "end": v(384.5, 497.8) * mm});
            skArc(sketch, "E18.19.0.5", {"start": v(375.5, 481.97) * mm, "mid": v(376.09, 480.56) * mm, "end": v(377.5, 479.97) * mm});
            skLineSegment(sketch, "E18.19.0.6", {"start": v(377.5, 479.97) * mm, "end": v(382.5, 479.97) * mm});
            skArc(sketch, "E18.19.0.7", {"start": v(382.5, 479.97) * mm, "mid": v(383.91, 480.56) * mm, "end": v(384.5, 481.97) * mm});
            skLineSegment(sketch, "E18.19.1.0", {"start": v(375.5, 447.33) * mm, "end": v(375.5, 463.15) * mm});
            skLineSegment(sketch, "E18.19.1.1", {"start": v(384.5, 447.33) * mm, "end": v(384.5, 463.15) * mm});
            skPoint(sketch, "E18.19.1.2", {"position": v(384.5, 445.33) * mm});
            skPoint(sketch, "E18.19.1.3", {"position": v(375.5, 445.33) * mm});
            skLineSegment(sketch, "E18.19.1.4", {"start": v(375.5, 463.15) * mm, "end": v(384.5, 463.15) * mm});
            skArc(sketch, "E18.19.1.5", {"start": v(375.5, 447.33) * mm, "mid": v(376.09, 445.92) * mm, "end": v(377.5, 445.33) * mm});
            skLineSegment(sketch, "E18.19.1.6", {"start": v(377.5, 445.33) * mm, "end": v(382.5, 445.33) * mm});
            skArc(sketch, "E18.19.1.7", {"start": v(382.5, 445.33) * mm, "mid": v(383.91, 445.92) * mm, "end": v(384.5, 447.33) * mm});
            skLineSegment(sketch, "E18.19.2.0", {"start": v(375.5, 412.7) * mm, "end": v(375.5, 428.51) * mm});
            skLineSegment(sketch, "E18.19.2.1", {"start": v(384.5, 412.7) * mm, "end": v(384.5, 428.51) * mm});
            skPoint(sketch, "E18.19.2.2", {"position": v(384.5, 410.7) * mm});
            skPoint(sketch, "E18.19.2.3", {"position": v(375.5, 410.7) * mm});
            skLineSegment(sketch, "E18.19.2.4", {"start": v(375.5, 428.51) * mm, "end": v(384.5, 428.51) * mm});
            skArc(sketch, "E18.19.2.5", {"start": v(375.5, 412.7) * mm, "mid": v(376.09, 411.28) * mm, "end": v(377.5, 410.7) * mm});
            skLineSegment(sketch, "E18.19.2.6", {"start": v(377.5, 410.7) * mm, "end": v(382.5, 410.7) * mm});
            skArc(sketch, "E18.19.2.7", {"start": v(382.5, 410.7) * mm, "mid": v(383.91, 411.28) * mm, "end": v(384.5, 412.7) * mm});
            skLineSegment(sketch, "E18.19.3.0", {"start": v(375.5, 378.05) * mm, "end": v(375.5, 393.87) * mm});
            skLineSegment(sketch, "E18.19.3.1", {"start": v(384.5, 378.05) * mm, "end": v(384.5, 393.87) * mm});
            skPoint(sketch, "E18.19.3.2", {"position": v(384.5, 376.05) * mm});
            skPoint(sketch, "E18.19.3.3", {"position": v(375.5, 376.05) * mm});
            skLineSegment(sketch, "E18.19.3.4", {"start": v(375.5, 393.87) * mm, "end": v(384.5, 393.87) * mm});
            skArc(sketch, "E18.19.3.5", {"start": v(375.5, 378.05) * mm, "mid": v(376.09, 376.64) * mm, "end": v(377.5, 376.05) * mm});
            skLineSegment(sketch, "E18.19.3.6", {"start": v(377.5, 376.05) * mm, "end": v(382.5, 376.05) * mm});
            skArc(sketch, "E18.19.3.7", {"start": v(382.5, 376.05) * mm, "mid": v(383.91, 376.64) * mm, "end": v(384.5, 378.05) * mm});
            skLineSegment(sketch, "E18.19.4.0", {"start": v(375.5, 343.41) * mm, "end": v(375.5, 359.23) * mm});
            skLineSegment(sketch, "E18.19.4.1", {"start": v(384.5, 343.41) * mm, "end": v(384.5, 359.23) * mm});
            skPoint(sketch, "E18.19.4.2", {"position": v(384.5, 341.41) * mm});
            skPoint(sketch, "E18.19.4.3", {"position": v(375.5, 341.41) * mm});
            skLineSegment(sketch, "E18.19.4.4", {"start": v(375.5, 359.23) * mm, "end": v(384.5, 359.23) * mm});
            skArc(sketch, "E18.19.4.5", {"start": v(375.5, 343.41) * mm, "mid": v(376.09, 342) * mm, "end": v(377.5, 341.41) * mm});
            skLineSegment(sketch, "E18.19.4.6", {"start": v(377.5, 341.41) * mm, "end": v(382.5, 341.41) * mm});
            skArc(sketch, "E18.19.4.7", {"start": v(382.5, 341.41) * mm, "mid": v(383.91, 342) * mm, "end": v(384.5, 343.41) * mm});
            skLineSegment(sketch, "E18.19.5.0", {"start": v(375.5, 308.77) * mm, "end": v(375.5, 324.59) * mm});
            skLineSegment(sketch, "E18.19.5.1", {"start": v(384.5, 308.77) * mm, "end": v(384.5, 324.59) * mm});
            skPoint(sketch, "E18.19.5.2", {"position": v(384.5, 306.77) * mm});
            skPoint(sketch, "E18.19.5.3", {"position": v(375.5, 306.77) * mm});
            skLineSegment(sketch, "E18.19.5.4", {"start": v(375.5, 324.59) * mm, "end": v(384.5, 324.59) * mm});
            skArc(sketch, "E18.19.5.5", {"start": v(375.5, 308.77) * mm, "mid": v(376.09, 307.35) * mm, "end": v(377.5, 306.77) * mm});
            skLineSegment(sketch, "E18.19.5.6", {"start": v(377.5, 306.77) * mm, "end": v(382.5, 306.77) * mm});
            skArc(sketch, "E18.19.5.7", {"start": v(382.5, 306.77) * mm, "mid": v(383.91, 307.35) * mm, "end": v(384.5, 308.77) * mm});
            skLineSegment(sketch, "E18.19.6.0", {"start": v(375.5, 274.13) * mm, "end": v(375.5, 289.95) * mm});
            skLineSegment(sketch, "E18.19.6.1", {"start": v(384.5, 274.13) * mm, "end": v(384.5, 289.95) * mm});
            skPoint(sketch, "E18.19.6.2", {"position": v(384.5, 272.13) * mm});
            skPoint(sketch, "E18.19.6.3", {"position": v(375.5, 272.13) * mm});
            skLineSegment(sketch, "E18.19.6.4", {"start": v(375.5, 289.95) * mm, "end": v(384.5, 289.95) * mm});
            skArc(sketch, "E18.19.6.5", {"start": v(375.5, 274.13) * mm, "mid": v(376.09, 272.71) * mm, "end": v(377.5, 272.13) * mm});
            skLineSegment(sketch, "E18.19.6.6", {"start": v(377.5, 272.13) * mm, "end": v(382.5, 272.13) * mm});
            skArc(sketch, "E18.19.6.7", {"start": v(382.5, 272.13) * mm, "mid": v(383.91, 272.71) * mm, "end": v(384.5, 274.13) * mm});
            skLineSegment(sketch, "E18.19.7.0", {"start": v(375.5, 239.49) * mm, "end": v(375.5, 255.3) * mm});
            skLineSegment(sketch, "E18.19.7.1", {"start": v(384.5, 239.49) * mm, "end": v(384.5, 255.3) * mm});
            skPoint(sketch, "E18.19.7.2", {"position": v(384.5, 237.49) * mm});
            skPoint(sketch, "E18.19.7.3", {"position": v(375.5, 237.49) * mm});
            skLineSegment(sketch, "E18.19.7.4", {"start": v(375.5, 255.3) * mm, "end": v(384.5, 255.3) * mm});
            skArc(sketch, "E18.19.7.5", {"start": v(375.5, 239.49) * mm, "mid": v(376.09, 238.07) * mm, "end": v(377.5, 237.49) * mm});
            skLineSegment(sketch, "E18.19.7.6", {"start": v(377.5, 237.49) * mm, "end": v(382.5, 237.49) * mm});
            skArc(sketch, "E18.19.7.7", {"start": v(382.5, 237.49) * mm, "mid": v(383.91, 238.07) * mm, "end": v(384.5, 239.49) * mm});
            skLineSegment(sketch, "E18.19.8.0", {"start": v(375.5, 204.85) * mm, "end": v(375.5, 220.67) * mm});
            skLineSegment(sketch, "E18.19.8.1", {"start": v(384.5, 204.85) * mm, "end": v(384.5, 220.67) * mm});
            skPoint(sketch, "E18.19.8.2", {"position": v(384.5, 202.85) * mm});
            skPoint(sketch, "E18.19.8.3", {"position": v(375.5, 202.85) * mm});
            skLineSegment(sketch, "E18.19.8.4", {"start": v(375.5, 220.67) * mm, "end": v(384.5, 220.67) * mm});
            skArc(sketch, "E18.19.8.5", {"start": v(375.5, 204.85) * mm, "mid": v(376.09, 203.43) * mm, "end": v(377.5, 202.85) * mm});
            skLineSegment(sketch, "E18.19.8.6", {"start": v(377.5, 202.85) * mm, "end": v(382.5, 202.85) * mm});
            skArc(sketch, "E18.19.8.7", {"start": v(382.5, 202.85) * mm, "mid": v(383.91, 203.43) * mm, "end": v(384.5, 204.85) * mm});
            skLineSegment(sketch, "E18.19.9.0", {"start": v(375.5, 170.2) * mm, "end": v(375.5, 186.03) * mm});
            skLineSegment(sketch, "E18.19.9.1", {"start": v(384.5, 170.2) * mm, "end": v(384.5, 186.03) * mm});
            skPoint(sketch, "E18.19.9.2", {"position": v(384.5, 168.2) * mm});
            skPoint(sketch, "E18.19.9.3", {"position": v(375.5, 168.2) * mm});
            skLineSegment(sketch, "E18.19.9.4", {"start": v(375.5, 186.03) * mm, "end": v(384.5, 186.03) * mm});
            skArc(sketch, "E18.19.9.5", {"start": v(375.5, 170.2) * mm, "mid": v(376.09, 168.8) * mm, "end": v(377.5, 168.2) * mm});
            skLineSegment(sketch, "E18.19.9.6", {"start": v(377.5, 168.2) * mm, "end": v(382.5, 168.2) * mm});
            skArc(sketch, "E18.19.9.7", {"start": v(382.5, 168.2) * mm, "mid": v(383.91, 168.8) * mm, "end": v(384.5, 170.2) * mm});
            skLineSegment(sketch, "E18.19.10.0", {"start": v(375.5, 135.56) * mm, "end": v(375.5, 151.38) * mm});
            skLineSegment(sketch, "E18.19.10.1", {"start": v(384.5, 135.56) * mm, "end": v(384.5, 151.38) * mm});
            skPoint(sketch, "E18.19.10.2", {"position": v(384.5, 133.56) * mm});
            skPoint(sketch, "E18.19.10.3", {"position": v(375.5, 133.56) * mm});
            skLineSegment(sketch, "E18.19.10.4", {"start": v(375.5, 151.38) * mm, "end": v(384.5, 151.38) * mm});
            skArc(sketch, "E18.19.10.5", {"start": v(375.5, 135.56) * mm, "mid": v(376.09, 134.15) * mm, "end": v(377.5, 133.56) * mm});
            skLineSegment(sketch, "E18.19.10.6", {"start": v(377.5, 133.56) * mm, "end": v(382.5, 133.56) * mm});
            skArc(sketch, "E18.19.10.7", {"start": v(382.5, 133.56) * mm, "mid": v(383.91, 134.15) * mm, "end": v(384.5, 135.56) * mm});
            skLineSegment(sketch, "E18.19.11.0", {"start": v(375.5, 100.92) * mm, "end": v(375.5, 116.74) * mm});
            skLineSegment(sketch, "E18.19.11.1", {"start": v(384.5, 100.92) * mm, "end": v(384.5, 116.74) * mm});
            skPoint(sketch, "E18.19.11.2", {"position": v(384.5, 98.92) * mm});
            skPoint(sketch, "E18.19.11.3", {"position": v(375.5, 98.92) * mm});
            skLineSegment(sketch, "E18.19.11.4", {"start": v(375.5, 116.74) * mm, "end": v(384.5, 116.74) * mm});
            skArc(sketch, "E18.19.11.5", {"start": v(375.5, 100.92) * mm, "mid": v(376.09, 99.5) * mm, "end": v(377.5, 98.92) * mm});
            skLineSegment(sketch, "E18.19.11.6", {"start": v(377.5, 98.92) * mm, "end": v(382.5, 98.92) * mm});
            skArc(sketch, "E18.19.11.7", {"start": v(382.5, 98.92) * mm, "mid": v(383.91, 99.5) * mm, "end": v(384.5, 100.92) * mm});
            skLineSegment(sketch, "E18.19.12.0", {"start": v(375.5, 66.28) * mm, "end": v(375.5, 82.1) * mm});
            skLineSegment(sketch, "E18.19.12.1", {"start": v(384.5, 66.28) * mm, "end": v(384.5, 82.1) * mm});
            skPoint(sketch, "E18.19.12.2", {"position": v(384.5, 64.28) * mm});
            skPoint(sketch, "E18.19.12.3", {"position": v(375.5, 64.28) * mm});
            skLineSegment(sketch, "E18.19.12.4", {"start": v(375.5, 82.1) * mm, "end": v(384.5, 82.1) * mm});
            skArc(sketch, "E18.19.12.5", {"start": v(375.5, 66.28) * mm, "mid": v(376.09, 64.87) * mm, "end": v(377.5, 64.28) * mm});
            skLineSegment(sketch, "E18.19.12.6", {"start": v(377.5, 64.28) * mm, "end": v(382.5, 64.28) * mm});
            skArc(sketch, "E18.19.12.7", {"start": v(382.5, 64.28) * mm, "mid": v(383.91, 64.87) * mm, "end": v(384.5, 66.28) * mm});
            skLineSegment(sketch, "E18.19.13.0", {"start": v(375.5, 31.64) * mm, "end": v(375.5, 47.46) * mm});
            skLineSegment(sketch, "E18.19.13.1", {"start": v(384.5, 31.64) * mm, "end": v(384.5, 47.46) * mm});
            skPoint(sketch, "E18.19.13.2", {"position": v(384.5, 29.64) * mm});
            skPoint(sketch, "E18.19.13.3", {"position": v(375.5, 29.64) * mm});
            skLineSegment(sketch, "E18.19.13.4", {"start": v(375.5, 47.46) * mm, "end": v(384.5, 47.46) * mm});
            skArc(sketch, "E18.19.13.5", {"start": v(375.5, 31.64) * mm, "mid": v(376.09, 30.23) * mm, "end": v(377.5, 29.64) * mm});
            skLineSegment(sketch, "E18.19.13.6", {"start": v(377.5, 29.64) * mm, "end": v(382.5, 29.64) * mm});
            skArc(sketch, "E18.19.13.7", {"start": v(382.5, 29.64) * mm, "mid": v(383.91, 30.23) * mm, "end": v(384.5, 31.64) * mm});
            skLineSegment(sketch, "E18.19.14.0", {"start": v(375.5, -3) * mm, "end": v(375.5, 12.82) * mm});
            skLineSegment(sketch, "E18.19.14.1", {"start": v(384.5, -3) * mm, "end": v(384.5, 12.82) * mm});
            skPoint(sketch, "E18.19.14.2", {"position": v(384.5, -5) * mm});
            skPoint(sketch, "E18.19.14.3", {"position": v(375.5, -5) * mm});
            skLineSegment(sketch, "E18.19.14.4", {"start": v(375.5, 12.82) * mm, "end": v(384.5, 12.82) * mm});
            skArc(sketch, "E18.19.14.5", {"start": v(375.5, -3) * mm, "mid": v(376.09, -4.41) * mm, "end": v(377.5, -5) * mm});
            skLineSegment(sketch, "E18.19.14.6", {"start": v(377.5, -5) * mm, "end": v(382.5, -5) * mm});
            skArc(sketch, "E18.19.14.7", {"start": v(382.5, -5) * mm, "mid": v(383.91, -4.41) * mm, "end": v(384.5, -3) * mm});
            skLineSegment(sketch, "E18.20.0.0", {"start": v(395.5, 481.97) * mm, "end": v(395.5, 497.8) * mm});
            skLineSegment(sketch, "E18.20.0.1", {"start": v(404.5, 481.97) * mm, "end": v(404.5, 497.8) * mm});
            skPoint(sketch, "E18.20.0.2", {"position": v(404.5, 479.97) * mm});
            skPoint(sketch, "E18.20.0.3", {"position": v(395.5, 479.97) * mm});
            skLineSegment(sketch, "E18.20.0.4", {"start": v(395.5, 497.8) * mm, "end": v(404.5, 497.8) * mm});
            skArc(sketch, "E18.20.0.5", {"start": v(395.5, 481.97) * mm, "mid": v(396.09, 480.56) * mm, "end": v(397.5, 479.97) * mm});
            skLineSegment(sketch, "E18.20.0.6", {"start": v(397.5, 479.97) * mm, "end": v(402.5, 479.97) * mm});
            skArc(sketch, "E18.20.0.7", {"start": v(402.5, 479.97) * mm, "mid": v(403.91, 480.56) * mm, "end": v(404.5, 481.97) * mm});
            skLineSegment(sketch, "E18.20.1.0", {"start": v(395.5, 447.33) * mm, "end": v(395.5, 463.15) * mm});
            skLineSegment(sketch, "E18.20.1.1", {"start": v(404.5, 447.33) * mm, "end": v(404.5, 463.15) * mm});
            skPoint(sketch, "E18.20.1.2", {"position": v(404.5, 445.33) * mm});
            skPoint(sketch, "E18.20.1.3", {"position": v(395.5, 445.33) * mm});
            skLineSegment(sketch, "E18.20.1.4", {"start": v(395.5, 463.15) * mm, "end": v(404.5, 463.15) * mm});
            skArc(sketch, "E18.20.1.5", {"start": v(395.5, 447.33) * mm, "mid": v(396.09, 445.92) * mm, "end": v(397.5, 445.33) * mm});
            skLineSegment(sketch, "E18.20.1.6", {"start": v(397.5, 445.33) * mm, "end": v(402.5, 445.33) * mm});
            skArc(sketch, "E18.20.1.7", {"start": v(402.5, 445.33) * mm, "mid": v(403.91, 445.92) * mm, "end": v(404.5, 447.33) * mm});
            skLineSegment(sketch, "E18.20.2.0", {"start": v(395.5, 412.7) * mm, "end": v(395.5, 428.51) * mm});
            skLineSegment(sketch, "E18.20.2.1", {"start": v(404.5, 412.7) * mm, "end": v(404.5, 428.51) * mm});
            skPoint(sketch, "E18.20.2.2", {"position": v(404.5, 410.7) * mm});
            skPoint(sketch, "E18.20.2.3", {"position": v(395.5, 410.7) * mm});
            skLineSegment(sketch, "E18.20.2.4", {"start": v(395.5, 428.51) * mm, "end": v(404.5, 428.51) * mm});
            skArc(sketch, "E18.20.2.5", {"start": v(395.5, 412.7) * mm, "mid": v(396.09, 411.28) * mm, "end": v(397.5, 410.7) * mm});
            skLineSegment(sketch, "E18.20.2.6", {"start": v(397.5, 410.7) * mm, "end": v(402.5, 410.7) * mm});
            skArc(sketch, "E18.20.2.7", {"start": v(402.5, 410.7) * mm, "mid": v(403.91, 411.28) * mm, "end": v(404.5, 412.7) * mm});
            skLineSegment(sketch, "E18.20.3.0", {"start": v(395.5, 378.05) * mm, "end": v(395.5, 393.87) * mm});
            skLineSegment(sketch, "E18.20.3.1", {"start": v(404.5, 378.05) * mm, "end": v(404.5, 393.87) * mm});
            skPoint(sketch, "E18.20.3.2", {"position": v(404.5, 376.05) * mm});
            skPoint(sketch, "E18.20.3.3", {"position": v(395.5, 376.05) * mm});
            skLineSegment(sketch, "E18.20.3.4", {"start": v(395.5, 393.87) * mm, "end": v(404.5, 393.87) * mm});
            skArc(sketch, "E18.20.3.5", {"start": v(395.5, 378.05) * mm, "mid": v(396.09, 376.64) * mm, "end": v(397.5, 376.05) * mm});
            skLineSegment(sketch, "E18.20.3.6", {"start": v(397.5, 376.05) * mm, "end": v(402.5, 376.05) * mm});
            skArc(sketch, "E18.20.3.7", {"start": v(402.5, 376.05) * mm, "mid": v(403.91, 376.64) * mm, "end": v(404.5, 378.05) * mm});
            skLineSegment(sketch, "E18.20.4.0", {"start": v(395.5, 343.41) * mm, "end": v(395.5, 359.23) * mm});
            skLineSegment(sketch, "E18.20.4.1", {"start": v(404.5, 343.41) * mm, "end": v(404.5, 359.23) * mm});
            skPoint(sketch, "E18.20.4.2", {"position": v(404.5, 341.41) * mm});
            skPoint(sketch, "E18.20.4.3", {"position": v(395.5, 341.41) * mm});
            skLineSegment(sketch, "E18.20.4.4", {"start": v(395.5, 359.23) * mm, "end": v(404.5, 359.23) * mm});
            skArc(sketch, "E18.20.4.5", {"start": v(395.5, 343.41) * mm, "mid": v(396.09, 342) * mm, "end": v(397.5, 341.41) * mm});
            skLineSegment(sketch, "E18.20.4.6", {"start": v(397.5, 341.41) * mm, "end": v(402.5, 341.41) * mm});
            skArc(sketch, "E18.20.4.7", {"start": v(402.5, 341.41) * mm, "mid": v(403.91, 342) * mm, "end": v(404.5, 343.41) * mm});
            skLineSegment(sketch, "E18.20.5.0", {"start": v(395.5, 308.77) * mm, "end": v(395.5, 324.59) * mm});
            skLineSegment(sketch, "E18.20.5.1", {"start": v(404.5, 308.77) * mm, "end": v(404.5, 324.59) * mm});
            skPoint(sketch, "E18.20.5.2", {"position": v(404.5, 306.77) * mm});
            skPoint(sketch, "E18.20.5.3", {"position": v(395.5, 306.77) * mm});
            skLineSegment(sketch, "E18.20.5.4", {"start": v(395.5, 324.59) * mm, "end": v(404.5, 324.59) * mm});
            skArc(sketch, "E18.20.5.5", {"start": v(395.5, 308.77) * mm, "mid": v(396.09, 307.35) * mm, "end": v(397.5, 306.77) * mm});
            skLineSegment(sketch, "E18.20.5.6", {"start": v(397.5, 306.77) * mm, "end": v(402.5, 306.77) * mm});
            skArc(sketch, "E18.20.5.7", {"start": v(402.5, 306.77) * mm, "mid": v(403.91, 307.35) * mm, "end": v(404.5, 308.77) * mm});
            skLineSegment(sketch, "E18.20.6.0", {"start": v(395.5, 274.13) * mm, "end": v(395.5, 289.95) * mm});
            skLineSegment(sketch, "E18.20.6.1", {"start": v(404.5, 274.13) * mm, "end": v(404.5, 289.95) * mm});
            skPoint(sketch, "E18.20.6.2", {"position": v(404.5, 272.13) * mm});
            skPoint(sketch, "E18.20.6.3", {"position": v(395.5, 272.13) * mm});
            skLineSegment(sketch, "E18.20.6.4", {"start": v(395.5, 289.95) * mm, "end": v(404.5, 289.95) * mm});
            skArc(sketch, "E18.20.6.5", {"start": v(395.5, 274.13) * mm, "mid": v(396.09, 272.71) * mm, "end": v(397.5, 272.13) * mm});
            skLineSegment(sketch, "E18.20.6.6", {"start": v(397.5, 272.13) * mm, "end": v(402.5, 272.13) * mm});
            skArc(sketch, "E18.20.6.7", {"start": v(402.5, 272.13) * mm, "mid": v(403.91, 272.71) * mm, "end": v(404.5, 274.13) * mm});
            skLineSegment(sketch, "E18.20.7.0", {"start": v(395.5, 239.49) * mm, "end": v(395.5, 255.3) * mm});
            skLineSegment(sketch, "E18.20.7.1", {"start": v(404.5, 239.49) * mm, "end": v(404.5, 255.3) * mm});
            skPoint(sketch, "E18.20.7.2", {"position": v(404.5, 237.49) * mm});
            skPoint(sketch, "E18.20.7.3", {"position": v(395.5, 237.49) * mm});
            skLineSegment(sketch, "E18.20.7.4", {"start": v(395.5, 255.3) * mm, "end": v(404.5, 255.3) * mm});
            skArc(sketch, "E18.20.7.5", {"start": v(395.5, 239.49) * mm, "mid": v(396.09, 238.07) * mm, "end": v(397.5, 237.49) * mm});
            skLineSegment(sketch, "E18.20.7.6", {"start": v(397.5, 237.49) * mm, "end": v(402.5, 237.49) * mm});
            skArc(sketch, "E18.20.7.7", {"start": v(402.5, 237.49) * mm, "mid": v(403.91, 238.07) * mm, "end": v(404.5, 239.49) * mm});
            skLineSegment(sketch, "E18.20.8.0", {"start": v(395.5, 204.85) * mm, "end": v(395.5, 220.67) * mm});
            skLineSegment(sketch, "E18.20.8.1", {"start": v(404.5, 204.85) * mm, "end": v(404.5, 220.67) * mm});
            skPoint(sketch, "E18.20.8.2", {"position": v(404.5, 202.85) * mm});
            skPoint(sketch, "E18.20.8.3", {"position": v(395.5, 202.85) * mm});
            skLineSegment(sketch, "E18.20.8.4", {"start": v(395.5, 220.67) * mm, "end": v(404.5, 220.67) * mm});
            skArc(sketch, "E18.20.8.5", {"start": v(395.5, 204.85) * mm, "mid": v(396.09, 203.43) * mm, "end": v(397.5, 202.85) * mm});
            skLineSegment(sketch, "E18.20.8.6", {"start": v(397.5, 202.85) * mm, "end": v(402.5, 202.85) * mm});
            skArc(sketch, "E18.20.8.7", {"start": v(402.5, 202.85) * mm, "mid": v(403.91, 203.43) * mm, "end": v(404.5, 204.85) * mm});
            skLineSegment(sketch, "E18.20.9.0", {"start": v(395.5, 170.2) * mm, "end": v(395.5, 186.03) * mm});
            skLineSegment(sketch, "E18.20.9.1", {"start": v(404.5, 170.2) * mm, "end": v(404.5, 186.03) * mm});
            skPoint(sketch, "E18.20.9.2", {"position": v(404.5, 168.2) * mm});
            skPoint(sketch, "E18.20.9.3", {"position": v(395.5, 168.2) * mm});
            skLineSegment(sketch, "E18.20.9.4", {"start": v(395.5, 186.03) * mm, "end": v(404.5, 186.03) * mm});
            skArc(sketch, "E18.20.9.5", {"start": v(395.5, 170.2) * mm, "mid": v(396.09, 168.8) * mm, "end": v(397.5, 168.2) * mm});
            skLineSegment(sketch, "E18.20.9.6", {"start": v(397.5, 168.2) * mm, "end": v(402.5, 168.2) * mm});
            skArc(sketch, "E18.20.9.7", {"start": v(402.5, 168.2) * mm, "mid": v(403.91, 168.8) * mm, "end": v(404.5, 170.2) * mm});
            skLineSegment(sketch, "E18.20.10.0", {"start": v(395.5, 135.56) * mm, "end": v(395.5, 151.38) * mm});
            skLineSegment(sketch, "E18.20.10.1", {"start": v(404.5, 135.56) * mm, "end": v(404.5, 151.38) * mm});
            skPoint(sketch, "E18.20.10.2", {"position": v(404.5, 133.56) * mm});
            skPoint(sketch, "E18.20.10.3", {"position": v(395.5, 133.56) * mm});
            skLineSegment(sketch, "E18.20.10.4", {"start": v(395.5, 151.38) * mm, "end": v(404.5, 151.38) * mm});
            skArc(sketch, "E18.20.10.5", {"start": v(395.5, 135.56) * mm, "mid": v(396.09, 134.15) * mm, "end": v(397.5, 133.56) * mm});
            skLineSegment(sketch, "E18.20.10.6", {"start": v(397.5, 133.56) * mm, "end": v(402.5, 133.56) * mm});
            skArc(sketch, "E18.20.10.7", {"start": v(402.5, 133.56) * mm, "mid": v(403.91, 134.15) * mm, "end": v(404.5, 135.56) * mm});
            skLineSegment(sketch, "E18.20.11.0", {"start": v(395.5, 100.92) * mm, "end": v(395.5, 116.74) * mm});
            skLineSegment(sketch, "E18.20.11.1", {"start": v(404.5, 100.92) * mm, "end": v(404.5, 116.74) * mm});
            skPoint(sketch, "E18.20.11.2", {"position": v(404.5, 98.92) * mm});
            skPoint(sketch, "E18.20.11.3", {"position": v(395.5, 98.92) * mm});
            skLineSegment(sketch, "E18.20.11.4", {"start": v(395.5, 116.74) * mm, "end": v(404.5, 116.74) * mm});
            skArc(sketch, "E18.20.11.5", {"start": v(395.5, 100.92) * mm, "mid": v(396.09, 99.5) * mm, "end": v(397.5, 98.92) * mm});
            skLineSegment(sketch, "E18.20.11.6", {"start": v(397.5, 98.92) * mm, "end": v(402.5, 98.92) * mm});
            skArc(sketch, "E18.20.11.7", {"start": v(402.5, 98.92) * mm, "mid": v(403.91, 99.5) * mm, "end": v(404.5, 100.92) * mm});
            skLineSegment(sketch, "E18.20.12.0", {"start": v(395.5, 66.28) * mm, "end": v(395.5, 82.1) * mm});
            skLineSegment(sketch, "E18.20.12.1", {"start": v(404.5, 66.28) * mm, "end": v(404.5, 82.1) * mm});
            skPoint(sketch, "E18.20.12.2", {"position": v(404.5, 64.28) * mm});
            skPoint(sketch, "E18.20.12.3", {"position": v(395.5, 64.28) * mm});
            skLineSegment(sketch, "E18.20.12.4", {"start": v(395.5, 82.1) * mm, "end": v(404.5, 82.1) * mm});
            skArc(sketch, "E18.20.12.5", {"start": v(395.5, 66.28) * mm, "mid": v(396.09, 64.87) * mm, "end": v(397.5, 64.28) * mm});
            skLineSegment(sketch, "E18.20.12.6", {"start": v(397.5, 64.28) * mm, "end": v(402.5, 64.28) * mm});
            skArc(sketch, "E18.20.12.7", {"start": v(402.5, 64.28) * mm, "mid": v(403.91, 64.87) * mm, "end": v(404.5, 66.28) * mm});
            skLineSegment(sketch, "E18.20.13.0", {"start": v(395.5, 31.64) * mm, "end": v(395.5, 47.46) * mm});
            skLineSegment(sketch, "E18.20.13.1", {"start": v(404.5, 31.64) * mm, "end": v(404.5, 47.46) * mm});
            skPoint(sketch, "E18.20.13.2", {"position": v(404.5, 29.64) * mm});
            skPoint(sketch, "E18.20.13.3", {"position": v(395.5, 29.64) * mm});
            skLineSegment(sketch, "E18.20.13.4", {"start": v(395.5, 47.46) * mm, "end": v(404.5, 47.46) * mm});
            skArc(sketch, "E18.20.13.5", {"start": v(395.5, 31.64) * mm, "mid": v(396.09, 30.23) * mm, "end": v(397.5, 29.64) * mm});
            skLineSegment(sketch, "E18.20.13.6", {"start": v(397.5, 29.64) * mm, "end": v(402.5, 29.64) * mm});
            skArc(sketch, "E18.20.13.7", {"start": v(402.5, 29.64) * mm, "mid": v(403.91, 30.23) * mm, "end": v(404.5, 31.64) * mm});
            skLineSegment(sketch, "E18.20.14.0", {"start": v(395.5, -3) * mm, "end": v(395.5, 12.82) * mm});
            skLineSegment(sketch, "E18.20.14.1", {"start": v(404.5, -3) * mm, "end": v(404.5, 12.82) * mm});
            skPoint(sketch, "E18.20.14.2", {"position": v(404.5, -5) * mm});
            skPoint(sketch, "E18.20.14.3", {"position": v(395.5, -5) * mm});
            skLineSegment(sketch, "E18.20.14.4", {"start": v(395.5, 12.82) * mm, "end": v(404.5, 12.82) * mm});
            skArc(sketch, "E18.20.14.5", {"start": v(395.5, -3) * mm, "mid": v(396.09, -4.41) * mm, "end": v(397.5, -5) * mm});
            skLineSegment(sketch, "E18.20.14.6", {"start": v(397.5, -5) * mm, "end": v(402.5, -5) * mm});
            skArc(sketch, "E18.20.14.7", {"start": v(402.5, -5) * mm, "mid": v(403.91, -4.41) * mm, "end": v(404.5, -3) * mm});
            skLineSegment(sketch, "E18.21.0.0", {"start": v(415.5, 481.97) * mm, "end": v(415.5, 497.8) * mm});
            skLineSegment(sketch, "E18.21.0.1", {"start": v(424.5, 481.97) * mm, "end": v(424.5, 497.8) * mm});
            skPoint(sketch, "E18.21.0.2", {"position": v(424.5, 479.97) * mm});
            skPoint(sketch, "E18.21.0.3", {"position": v(415.5, 479.97) * mm});
            skLineSegment(sketch, "E18.21.0.4", {"start": v(415.5, 497.8) * mm, "end": v(424.5, 497.8) * mm});
            skArc(sketch, "E18.21.0.5", {"start": v(415.5, 481.97) * mm, "mid": v(416.09, 480.56) * mm, "end": v(417.5, 479.97) * mm});
            skLineSegment(sketch, "E18.21.0.6", {"start": v(417.5, 479.97) * mm, "end": v(422.5, 479.97) * mm});
            skArc(sketch, "E18.21.0.7", {"start": v(422.5, 479.97) * mm, "mid": v(423.91, 480.56) * mm, "end": v(424.5, 481.97) * mm});
            skLineSegment(sketch, "E18.21.1.0", {"start": v(415.5, 447.33) * mm, "end": v(415.5, 463.15) * mm});
            skLineSegment(sketch, "E18.21.1.1", {"start": v(424.5, 447.33) * mm, "end": v(424.5, 463.15) * mm});
            skPoint(sketch, "E18.21.1.2", {"position": v(424.5, 445.33) * mm});
            skPoint(sketch, "E18.21.1.3", {"position": v(415.5, 445.33) * mm});
            skLineSegment(sketch, "E18.21.1.4", {"start": v(415.5, 463.15) * mm, "end": v(424.5, 463.15) * mm});
            skArc(sketch, "E18.21.1.5", {"start": v(415.5, 447.33) * mm, "mid": v(416.09, 445.92) * mm, "end": v(417.5, 445.33) * mm});
            skLineSegment(sketch, "E18.21.1.6", {"start": v(417.5, 445.33) * mm, "end": v(422.5, 445.33) * mm});
            skArc(sketch, "E18.21.1.7", {"start": v(422.5, 445.33) * mm, "mid": v(423.91, 445.92) * mm, "end": v(424.5, 447.33) * mm});
            skLineSegment(sketch, "E18.21.2.0", {"start": v(415.5, 412.7) * mm, "end": v(415.5, 428.51) * mm});
            skLineSegment(sketch, "E18.21.2.1", {"start": v(424.5, 412.7) * mm, "end": v(424.5, 428.51) * mm});
            skPoint(sketch, "E18.21.2.2", {"position": v(424.5, 410.7) * mm});
            skPoint(sketch, "E18.21.2.3", {"position": v(415.5, 410.7) * mm});
            skLineSegment(sketch, "E18.21.2.4", {"start": v(415.5, 428.51) * mm, "end": v(424.5, 428.51) * mm});
            skArc(sketch, "E18.21.2.5", {"start": v(415.5, 412.7) * mm, "mid": v(416.09, 411.28) * mm, "end": v(417.5, 410.7) * mm});
            skLineSegment(sketch, "E18.21.2.6", {"start": v(417.5, 410.7) * mm, "end": v(422.5, 410.7) * mm});
            skArc(sketch, "E18.21.2.7", {"start": v(422.5, 410.7) * mm, "mid": v(423.91, 411.28) * mm, "end": v(424.5, 412.7) * mm});
            skLineSegment(sketch, "E18.21.3.0", {"start": v(415.5, 378.05) * mm, "end": v(415.5, 393.87) * mm});
            skLineSegment(sketch, "E18.21.3.1", {"start": v(424.5, 378.05) * mm, "end": v(424.5, 393.87) * mm});
            skPoint(sketch, "E18.21.3.2", {"position": v(424.5, 376.05) * mm});
            skPoint(sketch, "E18.21.3.3", {"position": v(415.5, 376.05) * mm});
            skLineSegment(sketch, "E18.21.3.4", {"start": v(415.5, 393.87) * mm, "end": v(424.5, 393.87) * mm});
            skArc(sketch, "E18.21.3.5", {"start": v(415.5, 378.05) * mm, "mid": v(416.09, 376.64) * mm, "end": v(417.5, 376.05) * mm});
            skLineSegment(sketch, "E18.21.3.6", {"start": v(417.5, 376.05) * mm, "end": v(422.5, 376.05) * mm});
            skArc(sketch, "E18.21.3.7", {"start": v(422.5, 376.05) * mm, "mid": v(423.91, 376.64) * mm, "end": v(424.5, 378.05) * mm});
            skLineSegment(sketch, "E18.21.4.0", {"start": v(415.5, 343.41) * mm, "end": v(415.5, 359.23) * mm});
            skLineSegment(sketch, "E18.21.4.1", {"start": v(424.5, 343.41) * mm, "end": v(424.5, 359.23) * mm});
            skPoint(sketch, "E18.21.4.2", {"position": v(424.5, 341.41) * mm});
            skPoint(sketch, "E18.21.4.3", {"position": v(415.5, 341.41) * mm});
            skLineSegment(sketch, "E18.21.4.4", {"start": v(415.5, 359.23) * mm, "end": v(424.5, 359.23) * mm});
            skArc(sketch, "E18.21.4.5", {"start": v(415.5, 343.41) * mm, "mid": v(416.09, 342) * mm, "end": v(417.5, 341.41) * mm});
            skLineSegment(sketch, "E18.21.4.6", {"start": v(417.5, 341.41) * mm, "end": v(422.5, 341.41) * mm});
            skArc(sketch, "E18.21.4.7", {"start": v(422.5, 341.41) * mm, "mid": v(423.91, 342) * mm, "end": v(424.5, 343.41) * mm});
            skLineSegment(sketch, "E18.21.5.0", {"start": v(415.5, 308.77) * mm, "end": v(415.5, 324.59) * mm});
            skLineSegment(sketch, "E18.21.5.1", {"start": v(424.5, 308.77) * mm, "end": v(424.5, 324.59) * mm});
            skPoint(sketch, "E18.21.5.2", {"position": v(424.5, 306.77) * mm});
            skPoint(sketch, "E18.21.5.3", {"position": v(415.5, 306.77) * mm});
            skLineSegment(sketch, "E18.21.5.4", {"start": v(415.5, 324.59) * mm, "end": v(424.5, 324.59) * mm});
            skArc(sketch, "E18.21.5.5", {"start": v(415.5, 308.77) * mm, "mid": v(416.09, 307.35) * mm, "end": v(417.5, 306.77) * mm});
            skLineSegment(sketch, "E18.21.5.6", {"start": v(417.5, 306.77) * mm, "end": v(422.5, 306.77) * mm});
            skArc(sketch, "E18.21.5.7", {"start": v(422.5, 306.77) * mm, "mid": v(423.91, 307.35) * mm, "end": v(424.5, 308.77) * mm});
            skLineSegment(sketch, "E18.21.6.0", {"start": v(415.5, 274.13) * mm, "end": v(415.5, 289.95) * mm});
            skLineSegment(sketch, "E18.21.6.1", {"start": v(424.5, 274.13) * mm, "end": v(424.5, 289.95) * mm});
            skPoint(sketch, "E18.21.6.2", {"position": v(424.5, 272.13) * mm});
            skPoint(sketch, "E18.21.6.3", {"position": v(415.5, 272.13) * mm});
            skLineSegment(sketch, "E18.21.6.4", {"start": v(415.5, 289.95) * mm, "end": v(424.5, 289.95) * mm});
            skArc(sketch, "E18.21.6.5", {"start": v(415.5, 274.13) * mm, "mid": v(416.09, 272.71) * mm, "end": v(417.5, 272.13) * mm});
            skLineSegment(sketch, "E18.21.6.6", {"start": v(417.5, 272.13) * mm, "end": v(422.5, 272.13) * mm});
            skArc(sketch, "E18.21.6.7", {"start": v(422.5, 272.13) * mm, "mid": v(423.91, 272.71) * mm, "end": v(424.5, 274.13) * mm});
            skLineSegment(sketch, "E18.21.7.0", {"start": v(415.5, 239.49) * mm, "end": v(415.5, 255.3) * mm});
            skLineSegment(sketch, "E18.21.7.1", {"start": v(424.5, 239.49) * mm, "end": v(424.5, 255.3) * mm});
            skPoint(sketch, "E18.21.7.2", {"position": v(424.5, 237.49) * mm});
            skPoint(sketch, "E18.21.7.3", {"position": v(415.5, 237.49) * mm});
            skLineSegment(sketch, "E18.21.7.4", {"start": v(415.5, 255.3) * mm, "end": v(424.5, 255.3) * mm});
            skArc(sketch, "E18.21.7.5", {"start": v(415.5, 239.49) * mm, "mid": v(416.09, 238.07) * mm, "end": v(417.5, 237.49) * mm});
            skLineSegment(sketch, "E18.21.7.6", {"start": v(417.5, 237.49) * mm, "end": v(422.5, 237.49) * mm});
            skArc(sketch, "E18.21.7.7", {"start": v(422.5, 237.49) * mm, "mid": v(423.91, 238.07) * mm, "end": v(424.5, 239.49) * mm});
            skLineSegment(sketch, "E18.21.8.0", {"start": v(415.5, 204.85) * mm, "end": v(415.5, 220.67) * mm});
            skLineSegment(sketch, "E18.21.8.1", {"start": v(424.5, 204.85) * mm, "end": v(424.5, 220.67) * mm});
            skPoint(sketch, "E18.21.8.2", {"position": v(424.5, 202.85) * mm});
            skPoint(sketch, "E18.21.8.3", {"position": v(415.5, 202.85) * mm});
            skLineSegment(sketch, "E18.21.8.4", {"start": v(415.5, 220.67) * mm, "end": v(424.5, 220.67) * mm});
            skArc(sketch, "E18.21.8.5", {"start": v(415.5, 204.85) * mm, "mid": v(416.09, 203.43) * mm, "end": v(417.5, 202.85) * mm});
            skLineSegment(sketch, "E18.21.8.6", {"start": v(417.5, 202.85) * mm, "end": v(422.5, 202.85) * mm});
            skArc(sketch, "E18.21.8.7", {"start": v(422.5, 202.85) * mm, "mid": v(423.91, 203.43) * mm, "end": v(424.5, 204.85) * mm});
            skLineSegment(sketch, "E18.21.9.0", {"start": v(415.5, 170.2) * mm, "end": v(415.5, 186.03) * mm});
            skLineSegment(sketch, "E18.21.9.1", {"start": v(424.5, 170.2) * mm, "end": v(424.5, 186.03) * mm});
            skPoint(sketch, "E18.21.9.2", {"position": v(424.5, 168.2) * mm});
            skPoint(sketch, "E18.21.9.3", {"position": v(415.5, 168.2) * mm});
            skLineSegment(sketch, "E18.21.9.4", {"start": v(415.5, 186.03) * mm, "end": v(424.5, 186.03) * mm});
            skArc(sketch, "E18.21.9.5", {"start": v(415.5, 170.2) * mm, "mid": v(416.09, 168.8) * mm, "end": v(417.5, 168.2) * mm});
            skLineSegment(sketch, "E18.21.9.6", {"start": v(417.5, 168.2) * mm, "end": v(422.5, 168.2) * mm});
            skArc(sketch, "E18.21.9.7", {"start": v(422.5, 168.2) * mm, "mid": v(423.91, 168.8) * mm, "end": v(424.5, 170.2) * mm});
            skLineSegment(sketch, "E18.21.10.0", {"start": v(415.5, 135.56) * mm, "end": v(415.5, 151.38) * mm});
            skLineSegment(sketch, "E18.21.10.1", {"start": v(424.5, 135.56) * mm, "end": v(424.5, 151.38) * mm});
            skPoint(sketch, "E18.21.10.2", {"position": v(424.5, 133.56) * mm});
            skPoint(sketch, "E18.21.10.3", {"position": v(415.5, 133.56) * mm});
            skLineSegment(sketch, "E18.21.10.4", {"start": v(415.5, 151.38) * mm, "end": v(424.5, 151.38) * mm});
            skArc(sketch, "E18.21.10.5", {"start": v(415.5, 135.56) * mm, "mid": v(416.09, 134.15) * mm, "end": v(417.5, 133.56) * mm});
            skLineSegment(sketch, "E18.21.10.6", {"start": v(417.5, 133.56) * mm, "end": v(422.5, 133.56) * mm});
            skArc(sketch, "E18.21.10.7", {"start": v(422.5, 133.56) * mm, "mid": v(423.91, 134.15) * mm, "end": v(424.5, 135.56) * mm});
            skLineSegment(sketch, "E18.21.11.0", {"start": v(415.5, 100.92) * mm, "end": v(415.5, 116.74) * mm});
            skLineSegment(sketch, "E18.21.11.1", {"start": v(424.5, 100.92) * mm, "end": v(424.5, 116.74) * mm});
            skPoint(sketch, "E18.21.11.2", {"position": v(424.5, 98.92) * mm});
            skPoint(sketch, "E18.21.11.3", {"position": v(415.5, 98.92) * mm});
            skLineSegment(sketch, "E18.21.11.4", {"start": v(415.5, 116.74) * mm, "end": v(424.5, 116.74) * mm});
            skArc(sketch, "E18.21.11.5", {"start": v(415.5, 100.92) * mm, "mid": v(416.09, 99.5) * mm, "end": v(417.5, 98.92) * mm});
            skLineSegment(sketch, "E18.21.11.6", {"start": v(417.5, 98.92) * mm, "end": v(422.5, 98.92) * mm});
            skArc(sketch, "E18.21.11.7", {"start": v(422.5, 98.92) * mm, "mid": v(423.91, 99.5) * mm, "end": v(424.5, 100.92) * mm});
            skLineSegment(sketch, "E18.21.12.0", {"start": v(415.5, 66.28) * mm, "end": v(415.5, 82.1) * mm});
            skLineSegment(sketch, "E18.21.12.1", {"start": v(424.5, 66.28) * mm, "end": v(424.5, 82.1) * mm});
            skPoint(sketch, "E18.21.12.2", {"position": v(424.5, 64.28) * mm});
            skPoint(sketch, "E18.21.12.3", {"position": v(415.5, 64.28) * mm});
            skLineSegment(sketch, "E18.21.12.4", {"start": v(415.5, 82.1) * mm, "end": v(424.5, 82.1) * mm});
            skArc(sketch, "E18.21.12.5", {"start": v(415.5, 66.28) * mm, "mid": v(416.09, 64.87) * mm, "end": v(417.5, 64.28) * mm});
            skLineSegment(sketch, "E18.21.12.6", {"start": v(417.5, 64.28) * mm, "end": v(422.5, 64.28) * mm});
            skArc(sketch, "E18.21.12.7", {"start": v(422.5, 64.28) * mm, "mid": v(423.91, 64.87) * mm, "end": v(424.5, 66.28) * mm});
            skLineSegment(sketch, "E18.21.13.0", {"start": v(415.5, 31.64) * mm, "end": v(415.5, 47.46) * mm});
            skLineSegment(sketch, "E18.21.13.1", {"start": v(424.5, 31.64) * mm, "end": v(424.5, 47.46) * mm});
            skPoint(sketch, "E18.21.13.2", {"position": v(424.5, 29.64) * mm});
            skPoint(sketch, "E18.21.13.3", {"position": v(415.5, 29.64) * mm});
            skLineSegment(sketch, "E18.21.13.4", {"start": v(415.5, 47.46) * mm, "end": v(424.5, 47.46) * mm});
            skArc(sketch, "E18.21.13.5", {"start": v(415.5, 31.64) * mm, "mid": v(416.09, 30.23) * mm, "end": v(417.5, 29.64) * mm});
            skLineSegment(sketch, "E18.21.13.6", {"start": v(417.5, 29.64) * mm, "end": v(422.5, 29.64) * mm});
            skArc(sketch, "E18.21.13.7", {"start": v(422.5, 29.64) * mm, "mid": v(423.91, 30.23) * mm, "end": v(424.5, 31.64) * mm});
            skLineSegment(sketch, "E18.21.14.0", {"start": v(415.5, -3) * mm, "end": v(415.5, 12.82) * mm});
            skLineSegment(sketch, "E18.21.14.1", {"start": v(424.5, -3) * mm, "end": v(424.5, 12.82) * mm});
            skPoint(sketch, "E18.21.14.2", {"position": v(424.5, -5) * mm});
            skPoint(sketch, "E18.21.14.3", {"position": v(415.5, -5) * mm});
            skLineSegment(sketch, "E18.21.14.4", {"start": v(415.5, 12.82) * mm, "end": v(424.5, 12.82) * mm});
            skArc(sketch, "E18.21.14.5", {"start": v(415.5, -3) * mm, "mid": v(416.09, -4.41) * mm, "end": v(417.5, -5) * mm});
            skLineSegment(sketch, "E18.21.14.6", {"start": v(417.5, -5) * mm, "end": v(422.5, -5) * mm});
            skArc(sketch, "E18.21.14.7", {"start": v(422.5, -5) * mm, "mid": v(423.91, -4.41) * mm, "end": v(424.5, -3) * mm});
            skLineSegment(sketch, "E18.22.0.0", {"start": v(435.5, 481.97) * mm, "end": v(435.5, 497.8) * mm});
            skLineSegment(sketch, "E18.22.0.1", {"start": v(444.5, 481.97) * mm, "end": v(444.5, 497.8) * mm});
            skPoint(sketch, "E18.22.0.2", {"position": v(444.5, 479.97) * mm});
            skPoint(sketch, "E18.22.0.3", {"position": v(435.5, 479.97) * mm});
            skLineSegment(sketch, "E18.22.0.4", {"start": v(435.5, 497.8) * mm, "end": v(444.5, 497.8) * mm});
            skArc(sketch, "E18.22.0.5", {"start": v(435.5, 481.97) * mm, "mid": v(436.09, 480.56) * mm, "end": v(437.5, 479.97) * mm});
            skLineSegment(sketch, "E18.22.0.6", {"start": v(437.5, 479.97) * mm, "end": v(442.5, 479.97) * mm});
            skArc(sketch, "E18.22.0.7", {"start": v(442.5, 479.97) * mm, "mid": v(443.91, 480.56) * mm, "end": v(444.5, 481.97) * mm});
            skLineSegment(sketch, "E18.22.1.0", {"start": v(435.5, 447.33) * mm, "end": v(435.5, 463.15) * mm});
            skLineSegment(sketch, "E18.22.1.1", {"start": v(444.5, 447.33) * mm, "end": v(444.5, 463.15) * mm});
            skPoint(sketch, "E18.22.1.2", {"position": v(444.5, 445.33) * mm});
            skPoint(sketch, "E18.22.1.3", {"position": v(435.5, 445.33) * mm});
            skLineSegment(sketch, "E18.22.1.4", {"start": v(435.5, 463.15) * mm, "end": v(444.5, 463.15) * mm});
            skArc(sketch, "E18.22.1.5", {"start": v(435.5, 447.33) * mm, "mid": v(436.09, 445.92) * mm, "end": v(437.5, 445.33) * mm});
            skLineSegment(sketch, "E18.22.1.6", {"start": v(437.5, 445.33) * mm, "end": v(442.5, 445.33) * mm});
            skArc(sketch, "E18.22.1.7", {"start": v(442.5, 445.33) * mm, "mid": v(443.91, 445.92) * mm, "end": v(444.5, 447.33) * mm});
            skLineSegment(sketch, "E18.22.2.0", {"start": v(435.5, 412.7) * mm, "end": v(435.5, 428.51) * mm});
            skLineSegment(sketch, "E18.22.2.1", {"start": v(444.5, 412.7) * mm, "end": v(444.5, 428.51) * mm});
            skPoint(sketch, "E18.22.2.2", {"position": v(444.5, 410.7) * mm});
            skPoint(sketch, "E18.22.2.3", {"position": v(435.5, 410.7) * mm});
            skLineSegment(sketch, "E18.22.2.4", {"start": v(435.5, 428.51) * mm, "end": v(444.5, 428.51) * mm});
            skArc(sketch, "E18.22.2.5", {"start": v(435.5, 412.7) * mm, "mid": v(436.09, 411.28) * mm, "end": v(437.5, 410.7) * mm});
            skLineSegment(sketch, "E18.22.2.6", {"start": v(437.5, 410.7) * mm, "end": v(442.5, 410.7) * mm});
            skArc(sketch, "E18.22.2.7", {"start": v(442.5, 410.7) * mm, "mid": v(443.91, 411.28) * mm, "end": v(444.5, 412.7) * mm});
            skLineSegment(sketch, "E18.22.3.0", {"start": v(435.5, 378.05) * mm, "end": v(435.5, 393.87) * mm});
            skLineSegment(sketch, "E18.22.3.1", {"start": v(444.5, 378.05) * mm, "end": v(444.5, 393.87) * mm});
            skPoint(sketch, "E18.22.3.2", {"position": v(444.5, 376.05) * mm});
            skPoint(sketch, "E18.22.3.3", {"position": v(435.5, 376.05) * mm});
            skLineSegment(sketch, "E18.22.3.4", {"start": v(435.5, 393.87) * mm, "end": v(444.5, 393.87) * mm});
            skArc(sketch, "E18.22.3.5", {"start": v(435.5, 378.05) * mm, "mid": v(436.09, 376.64) * mm, "end": v(437.5, 376.05) * mm});
            skLineSegment(sketch, "E18.22.3.6", {"start": v(437.5, 376.05) * mm, "end": v(442.5, 376.05) * mm});
            skArc(sketch, "E18.22.3.7", {"start": v(442.5, 376.05) * mm, "mid": v(443.91, 376.64) * mm, "end": v(444.5, 378.05) * mm});
            skLineSegment(sketch, "E18.22.4.0", {"start": v(435.5, 343.41) * mm, "end": v(435.5, 359.23) * mm});
            skLineSegment(sketch, "E18.22.4.1", {"start": v(444.5, 343.41) * mm, "end": v(444.5, 359.23) * mm});
            skPoint(sketch, "E18.22.4.2", {"position": v(444.5, 341.41) * mm});
            skPoint(sketch, "E18.22.4.3", {"position": v(435.5, 341.41) * mm});
            skLineSegment(sketch, "E18.22.4.4", {"start": v(435.5, 359.23) * mm, "end": v(444.5, 359.23) * mm});
            skArc(sketch, "E18.22.4.5", {"start": v(435.5, 343.41) * mm, "mid": v(436.09, 342) * mm, "end": v(437.5, 341.41) * mm});
            skLineSegment(sketch, "E18.22.4.6", {"start": v(437.5, 341.41) * mm, "end": v(442.5, 341.41) * mm});
            skArc(sketch, "E18.22.4.7", {"start": v(442.5, 341.41) * mm, "mid": v(443.91, 342) * mm, "end": v(444.5, 343.41) * mm});
            skLineSegment(sketch, "E18.22.5.0", {"start": v(435.5, 308.77) * mm, "end": v(435.5, 324.59) * mm});
            skLineSegment(sketch, "E18.22.5.1", {"start": v(444.5, 308.77) * mm, "end": v(444.5, 324.59) * mm});
            skPoint(sketch, "E18.22.5.2", {"position": v(444.5, 306.77) * mm});
            skPoint(sketch, "E18.22.5.3", {"position": v(435.5, 306.77) * mm});
            skLineSegment(sketch, "E18.22.5.4", {"start": v(435.5, 324.59) * mm, "end": v(444.5, 324.59) * mm});
            skArc(sketch, "E18.22.5.5", {"start": v(435.5, 308.77) * mm, "mid": v(436.09, 307.35) * mm, "end": v(437.5, 306.77) * mm});
            skLineSegment(sketch, "E18.22.5.6", {"start": v(437.5, 306.77) * mm, "end": v(442.5, 306.77) * mm});
            skArc(sketch, "E18.22.5.7", {"start": v(442.5, 306.77) * mm, "mid": v(443.91, 307.35) * mm, "end": v(444.5, 308.77) * mm});
            skLineSegment(sketch, "E18.22.6.0", {"start": v(435.5, 274.13) * mm, "end": v(435.5, 289.95) * mm});
            skLineSegment(sketch, "E18.22.6.1", {"start": v(444.5, 274.13) * mm, "end": v(444.5, 289.95) * mm});
            skPoint(sketch, "E18.22.6.2", {"position": v(444.5, 272.13) * mm});
            skPoint(sketch, "E18.22.6.3", {"position": v(435.5, 272.13) * mm});
            skLineSegment(sketch, "E18.22.6.4", {"start": v(435.5, 289.95) * mm, "end": v(444.5, 289.95) * mm});
            skArc(sketch, "E18.22.6.5", {"start": v(435.5, 274.13) * mm, "mid": v(436.09, 272.71) * mm, "end": v(437.5, 272.13) * mm});
            skLineSegment(sketch, "E18.22.6.6", {"start": v(437.5, 272.13) * mm, "end": v(442.5, 272.13) * mm});
            skArc(sketch, "E18.22.6.7", {"start": v(442.5, 272.13) * mm, "mid": v(443.91, 272.71) * mm, "end": v(444.5, 274.13) * mm});
            skLineSegment(sketch, "E18.22.7.0", {"start": v(435.5, 239.49) * mm, "end": v(435.5, 255.3) * mm});
            skLineSegment(sketch, "E18.22.7.1", {"start": v(444.5, 239.49) * mm, "end": v(444.5, 255.3) * mm});
            skPoint(sketch, "E18.22.7.2", {"position": v(444.5, 237.49) * mm});
            skPoint(sketch, "E18.22.7.3", {"position": v(435.5, 237.49) * mm});
            skLineSegment(sketch, "E18.22.7.4", {"start": v(435.5, 255.3) * mm, "end": v(444.5, 255.3) * mm});
            skArc(sketch, "E18.22.7.5", {"start": v(435.5, 239.49) * mm, "mid": v(436.09, 238.07) * mm, "end": v(437.5, 237.49) * mm});
            skLineSegment(sketch, "E18.22.7.6", {"start": v(437.5, 237.49) * mm, "end": v(442.5, 237.49) * mm});
            skArc(sketch, "E18.22.7.7", {"start": v(442.5, 237.49) * mm, "mid": v(443.91, 238.07) * mm, "end": v(444.5, 239.49) * mm});
            skLineSegment(sketch, "E18.22.8.0", {"start": v(435.5, 204.85) * mm, "end": v(435.5, 220.67) * mm});
            skLineSegment(sketch, "E18.22.8.1", {"start": v(444.5, 204.85) * mm, "end": v(444.5, 220.67) * mm});
            skPoint(sketch, "E18.22.8.2", {"position": v(444.5, 202.85) * mm});
            skPoint(sketch, "E18.22.8.3", {"position": v(435.5, 202.85) * mm});
            skLineSegment(sketch, "E18.22.8.4", {"start": v(435.5, 220.67) * mm, "end": v(444.5, 220.67) * mm});
            skArc(sketch, "E18.22.8.5", {"start": v(435.5, 204.85) * mm, "mid": v(436.09, 203.43) * mm, "end": v(437.5, 202.85) * mm});
            skLineSegment(sketch, "E18.22.8.6", {"start": v(437.5, 202.85) * mm, "end": v(442.5, 202.85) * mm});
            skArc(sketch, "E18.22.8.7", {"start": v(442.5, 202.85) * mm, "mid": v(443.91, 203.43) * mm, "end": v(444.5, 204.85) * mm});
            skLineSegment(sketch, "E18.22.9.0", {"start": v(435.5, 170.2) * mm, "end": v(435.5, 186.03) * mm});
            skLineSegment(sketch, "E18.22.9.1", {"start": v(444.5, 170.2) * mm, "end": v(444.5, 186.03) * mm});
            skPoint(sketch, "E18.22.9.2", {"position": v(444.5, 168.2) * mm});
            skPoint(sketch, "E18.22.9.3", {"position": v(435.5, 168.2) * mm});
            skLineSegment(sketch, "E18.22.9.4", {"start": v(435.5, 186.03) * mm, "end": v(444.5, 186.03) * mm});
            skArc(sketch, "E18.22.9.5", {"start": v(435.5, 170.2) * mm, "mid": v(436.09, 168.8) * mm, "end": v(437.5, 168.2) * mm});
            skLineSegment(sketch, "E18.22.9.6", {"start": v(437.5, 168.2) * mm, "end": v(442.5, 168.2) * mm});
            skArc(sketch, "E18.22.9.7", {"start": v(442.5, 168.2) * mm, "mid": v(443.91, 168.8) * mm, "end": v(444.5, 170.2) * mm});
            skLineSegment(sketch, "E18.22.10.0", {"start": v(435.5, 135.56) * mm, "end": v(435.5, 151.38) * mm});
            skLineSegment(sketch, "E18.22.10.1", {"start": v(444.5, 135.56) * mm, "end": v(444.5, 151.38) * mm});
            skPoint(sketch, "E18.22.10.2", {"position": v(444.5, 133.56) * mm});
            skPoint(sketch, "E18.22.10.3", {"position": v(435.5, 133.56) * mm});
            skLineSegment(sketch, "E18.22.10.4", {"start": v(435.5, 151.38) * mm, "end": v(444.5, 151.38) * mm});
            skArc(sketch, "E18.22.10.5", {"start": v(435.5, 135.56) * mm, "mid": v(436.09, 134.15) * mm, "end": v(437.5, 133.56) * mm});
            skLineSegment(sketch, "E18.22.10.6", {"start": v(437.5, 133.56) * mm, "end": v(442.5, 133.56) * mm});
            skArc(sketch, "E18.22.10.7", {"start": v(442.5, 133.56) * mm, "mid": v(443.91, 134.15) * mm, "end": v(444.5, 135.56) * mm});
            skLineSegment(sketch, "E18.22.11.0", {"start": v(435.5, 100.92) * mm, "end": v(435.5, 116.74) * mm});
            skLineSegment(sketch, "E18.22.11.1", {"start": v(444.5, 100.92) * mm, "end": v(444.5, 116.74) * mm});
            skPoint(sketch, "E18.22.11.2", {"position": v(444.5, 98.92) * mm});
            skPoint(sketch, "E18.22.11.3", {"position": v(435.5, 98.92) * mm});
            skLineSegment(sketch, "E18.22.11.4", {"start": v(435.5, 116.74) * mm, "end": v(444.5, 116.74) * mm});
            skArc(sketch, "E18.22.11.5", {"start": v(435.5, 100.92) * mm, "mid": v(436.09, 99.5) * mm, "end": v(437.5, 98.92) * mm});
            skLineSegment(sketch, "E18.22.11.6", {"start": v(437.5, 98.92) * mm, "end": v(442.5, 98.92) * mm});
            skArc(sketch, "E18.22.11.7", {"start": v(442.5, 98.92) * mm, "mid": v(443.91, 99.5) * mm, "end": v(444.5, 100.92) * mm});
            skLineSegment(sketch, "E18.22.12.0", {"start": v(435.5, 66.28) * mm, "end": v(435.5, 82.1) * mm});
            skLineSegment(sketch, "E18.22.12.1", {"start": v(444.5, 66.28) * mm, "end": v(444.5, 82.1) * mm});
            skPoint(sketch, "E18.22.12.2", {"position": v(444.5, 64.28) * mm});
            skPoint(sketch, "E18.22.12.3", {"position": v(435.5, 64.28) * mm});
            skLineSegment(sketch, "E18.22.12.4", {"start": v(435.5, 82.1) * mm, "end": v(444.5, 82.1) * mm});
            skArc(sketch, "E18.22.12.5", {"start": v(435.5, 66.28) * mm, "mid": v(436.09, 64.87) * mm, "end": v(437.5, 64.28) * mm});
            skLineSegment(sketch, "E18.22.12.6", {"start": v(437.5, 64.28) * mm, "end": v(442.5, 64.28) * mm});
            skArc(sketch, "E18.22.12.7", {"start": v(442.5, 64.28) * mm, "mid": v(443.91, 64.87) * mm, "end": v(444.5, 66.28) * mm});
            skLineSegment(sketch, "E18.22.13.0", {"start": v(435.5, 31.64) * mm, "end": v(435.5, 47.46) * mm});
            skLineSegment(sketch, "E18.22.13.1", {"start": v(444.5, 31.64) * mm, "end": v(444.5, 47.46) * mm});
            skPoint(sketch, "E18.22.13.2", {"position": v(444.5, 29.64) * mm});
            skPoint(sketch, "E18.22.13.3", {"position": v(435.5, 29.64) * mm});
            skLineSegment(sketch, "E18.22.13.4", {"start": v(435.5, 47.46) * mm, "end": v(444.5, 47.46) * mm});
            skArc(sketch, "E18.22.13.5", {"start": v(435.5, 31.64) * mm, "mid": v(436.09, 30.23) * mm, "end": v(437.5, 29.64) * mm});
            skLineSegment(sketch, "E18.22.13.6", {"start": v(437.5, 29.64) * mm, "end": v(442.5, 29.64) * mm});
            skArc(sketch, "E18.22.13.7", {"start": v(442.5, 29.64) * mm, "mid": v(443.91, 30.23) * mm, "end": v(444.5, 31.64) * mm});
            skLineSegment(sketch, "E18.22.14.0", {"start": v(435.5, -3) * mm, "end": v(435.5, 12.82) * mm});
            skLineSegment(sketch, "E18.22.14.1", {"start": v(444.5, -3) * mm, "end": v(444.5, 12.82) * mm});
            skPoint(sketch, "E18.22.14.2", {"position": v(444.5, -5) * mm});
            skPoint(sketch, "E18.22.14.3", {"position": v(435.5, -5) * mm});
            skLineSegment(sketch, "E18.22.14.4", {"start": v(435.5, 12.82) * mm, "end": v(444.5, 12.82) * mm});
            skArc(sketch, "E18.22.14.5", {"start": v(435.5, -3) * mm, "mid": v(436.09, -4.41) * mm, "end": v(437.5, -5) * mm});
            skLineSegment(sketch, "E18.22.14.6", {"start": v(437.5, -5) * mm, "end": v(442.5, -5) * mm});
            skArc(sketch, "E18.22.14.7", {"start": v(442.5, -5) * mm, "mid": v(443.91, -4.41) * mm, "end": v(444.5, -3) * mm});
            skLineSegment(sketch, "E18.23.0.0", {"start": v(455.5, 481.97) * mm, "end": v(455.5, 497.8) * mm});
            skLineSegment(sketch, "E18.23.0.1", {"start": v(464.5, 481.97) * mm, "end": v(464.5, 497.8) * mm});
            skPoint(sketch, "E18.23.0.2", {"position": v(464.5, 479.97) * mm});
            skPoint(sketch, "E18.23.0.3", {"position": v(455.5, 479.97) * mm});
            skLineSegment(sketch, "E18.23.0.4", {"start": v(455.5, 497.8) * mm, "end": v(464.5, 497.8) * mm});
            skArc(sketch, "E18.23.0.5", {"start": v(455.5, 481.97) * mm, "mid": v(456.09, 480.56) * mm, "end": v(457.5, 479.97) * mm});
            skLineSegment(sketch, "E18.23.0.6", {"start": v(457.5, 479.97) * mm, "end": v(462.5, 479.97) * mm});
            skArc(sketch, "E18.23.0.7", {"start": v(462.5, 479.97) * mm, "mid": v(463.91, 480.56) * mm, "end": v(464.5, 481.97) * mm});
            skLineSegment(sketch, "E18.23.1.0", {"start": v(455.5, 447.33) * mm, "end": v(455.5, 463.15) * mm});
            skLineSegment(sketch, "E18.23.1.1", {"start": v(464.5, 447.33) * mm, "end": v(464.5, 463.15) * mm});
            skPoint(sketch, "E18.23.1.2", {"position": v(464.5, 445.33) * mm});
            skPoint(sketch, "E18.23.1.3", {"position": v(455.5, 445.33) * mm});
            skLineSegment(sketch, "E18.23.1.4", {"start": v(455.5, 463.15) * mm, "end": v(464.5, 463.15) * mm});
            skArc(sketch, "E18.23.1.5", {"start": v(455.5, 447.33) * mm, "mid": v(456.09, 445.92) * mm, "end": v(457.5, 445.33) * mm});
            skLineSegment(sketch, "E18.23.1.6", {"start": v(457.5, 445.33) * mm, "end": v(462.5, 445.33) * mm});
            skArc(sketch, "E18.23.1.7", {"start": v(462.5, 445.33) * mm, "mid": v(463.91, 445.92) * mm, "end": v(464.5, 447.33) * mm});
            skLineSegment(sketch, "E18.23.2.0", {"start": v(455.5, 412.7) * mm, "end": v(455.5, 428.51) * mm});
            skLineSegment(sketch, "E18.23.2.1", {"start": v(464.5, 412.7) * mm, "end": v(464.5, 428.51) * mm});
            skPoint(sketch, "E18.23.2.2", {"position": v(464.5, 410.7) * mm});
            skPoint(sketch, "E18.23.2.3", {"position": v(455.5, 410.7) * mm});
            skLineSegment(sketch, "E18.23.2.4", {"start": v(455.5, 428.51) * mm, "end": v(464.5, 428.51) * mm});
            skArc(sketch, "E18.23.2.5", {"start": v(455.5, 412.7) * mm, "mid": v(456.09, 411.28) * mm, "end": v(457.5, 410.7) * mm});
            skLineSegment(sketch, "E18.23.2.6", {"start": v(457.5, 410.7) * mm, "end": v(462.5, 410.7) * mm});
            skArc(sketch, "E18.23.2.7", {"start": v(462.5, 410.7) * mm, "mid": v(463.91, 411.28) * mm, "end": v(464.5, 412.7) * mm});
            skLineSegment(sketch, "E18.23.3.0", {"start": v(455.5, 378.05) * mm, "end": v(455.5, 393.87) * mm});
            skLineSegment(sketch, "E18.23.3.1", {"start": v(464.5, 378.05) * mm, "end": v(464.5, 393.87) * mm});
            skPoint(sketch, "E18.23.3.2", {"position": v(464.5, 376.05) * mm});
            skPoint(sketch, "E18.23.3.3", {"position": v(455.5, 376.05) * mm});
            skLineSegment(sketch, "E18.23.3.4", {"start": v(455.5, 393.87) * mm, "end": v(464.5, 393.87) * mm});
            skArc(sketch, "E18.23.3.5", {"start": v(455.5, 378.05) * mm, "mid": v(456.09, 376.64) * mm, "end": v(457.5, 376.05) * mm});
            skLineSegment(sketch, "E18.23.3.6", {"start": v(457.5, 376.05) * mm, "end": v(462.5, 376.05) * mm});
            skArc(sketch, "E18.23.3.7", {"start": v(462.5, 376.05) * mm, "mid": v(463.91, 376.64) * mm, "end": v(464.5, 378.05) * mm});
            skLineSegment(sketch, "E18.23.4.0", {"start": v(455.5, 343.41) * mm, "end": v(455.5, 359.23) * mm});
            skLineSegment(sketch, "E18.23.4.1", {"start": v(464.5, 343.41) * mm, "end": v(464.5, 359.23) * mm});
            skPoint(sketch, "E18.23.4.2", {"position": v(464.5, 341.41) * mm});
            skPoint(sketch, "E18.23.4.3", {"position": v(455.5, 341.41) * mm});
            skLineSegment(sketch, "E18.23.4.4", {"start": v(455.5, 359.23) * mm, "end": v(464.5, 359.23) * mm});
            skArc(sketch, "E18.23.4.5", {"start": v(455.5, 343.41) * mm, "mid": v(456.09, 342) * mm, "end": v(457.5, 341.41) * mm});
            skLineSegment(sketch, "E18.23.4.6", {"start": v(457.5, 341.41) * mm, "end": v(462.5, 341.41) * mm});
            skArc(sketch, "E18.23.4.7", {"start": v(462.5, 341.41) * mm, "mid": v(463.91, 342) * mm, "end": v(464.5, 343.41) * mm});
            skLineSegment(sketch, "E18.23.5.0", {"start": v(455.5, 308.77) * mm, "end": v(455.5, 324.59) * mm});
            skLineSegment(sketch, "E18.23.5.1", {"start": v(464.5, 308.77) * mm, "end": v(464.5, 324.59) * mm});
            skPoint(sketch, "E18.23.5.2", {"position": v(464.5, 306.77) * mm});
            skPoint(sketch, "E18.23.5.3", {"position": v(455.5, 306.77) * mm});
            skLineSegment(sketch, "E18.23.5.4", {"start": v(455.5, 324.59) * mm, "end": v(464.5, 324.59) * mm});
            skArc(sketch, "E18.23.5.5", {"start": v(455.5, 308.77) * mm, "mid": v(456.09, 307.35) * mm, "end": v(457.5, 306.77) * mm});
            skLineSegment(sketch, "E18.23.5.6", {"start": v(457.5, 306.77) * mm, "end": v(462.5, 306.77) * mm});
            skArc(sketch, "E18.23.5.7", {"start": v(462.5, 306.77) * mm, "mid": v(463.91, 307.35) * mm, "end": v(464.5, 308.77) * mm});
            skLineSegment(sketch, "E18.23.6.0", {"start": v(455.5, 274.13) * mm, "end": v(455.5, 289.95) * mm});
            skLineSegment(sketch, "E18.23.6.1", {"start": v(464.5, 274.13) * mm, "end": v(464.5, 289.95) * mm});
            skPoint(sketch, "E18.23.6.2", {"position": v(464.5, 272.13) * mm});
            skPoint(sketch, "E18.23.6.3", {"position": v(455.5, 272.13) * mm});
            skLineSegment(sketch, "E18.23.6.4", {"start": v(455.5, 289.95) * mm, "end": v(464.5, 289.95) * mm});
            skArc(sketch, "E18.23.6.5", {"start": v(455.5, 274.13) * mm, "mid": v(456.09, 272.71) * mm, "end": v(457.5, 272.13) * mm});
            skLineSegment(sketch, "E18.23.6.6", {"start": v(457.5, 272.13) * mm, "end": v(462.5, 272.13) * mm});
            skArc(sketch, "E18.23.6.7", {"start": v(462.5, 272.13) * mm, "mid": v(463.91, 272.71) * mm, "end": v(464.5, 274.13) * mm});
            skLineSegment(sketch, "E18.23.7.0", {"start": v(455.5, 239.49) * mm, "end": v(455.5, 255.3) * mm});
            skLineSegment(sketch, "E18.23.7.1", {"start": v(464.5, 239.49) * mm, "end": v(464.5, 255.3) * mm});
            skPoint(sketch, "E18.23.7.2", {"position": v(464.5, 237.49) * mm});
            skPoint(sketch, "E18.23.7.3", {"position": v(455.5, 237.49) * mm});
            skLineSegment(sketch, "E18.23.7.4", {"start": v(455.5, 255.3) * mm, "end": v(464.5, 255.3) * mm});
            skArc(sketch, "E18.23.7.5", {"start": v(455.5, 239.49) * mm, "mid": v(456.09, 238.07) * mm, "end": v(457.5, 237.49) * mm});
            skLineSegment(sketch, "E18.23.7.6", {"start": v(457.5, 237.49) * mm, "end": v(462.5, 237.49) * mm});
            skArc(sketch, "E18.23.7.7", {"start": v(462.5, 237.49) * mm, "mid": v(463.91, 238.07) * mm, "end": v(464.5, 239.49) * mm});
            skLineSegment(sketch, "E18.23.8.0", {"start": v(455.5, 204.85) * mm, "end": v(455.5, 220.67) * mm});
            skLineSegment(sketch, "E18.23.8.1", {"start": v(464.5, 204.85) * mm, "end": v(464.5, 220.67) * mm});
            skPoint(sketch, "E18.23.8.2", {"position": v(464.5, 202.85) * mm});
            skPoint(sketch, "E18.23.8.3", {"position": v(455.5, 202.85) * mm});
            skLineSegment(sketch, "E18.23.8.4", {"start": v(455.5, 220.67) * mm, "end": v(464.5, 220.67) * mm});
            skArc(sketch, "E18.23.8.5", {"start": v(455.5, 204.85) * mm, "mid": v(456.09, 203.43) * mm, "end": v(457.5, 202.85) * mm});
            skLineSegment(sketch, "E18.23.8.6", {"start": v(457.5, 202.85) * mm, "end": v(462.5, 202.85) * mm});
            skArc(sketch, "E18.23.8.7", {"start": v(462.5, 202.85) * mm, "mid": v(463.91, 203.43) * mm, "end": v(464.5, 204.85) * mm});
            skLineSegment(sketch, "E18.23.9.0", {"start": v(455.5, 170.2) * mm, "end": v(455.5, 186.03) * mm});
            skLineSegment(sketch, "E18.23.9.1", {"start": v(464.5, 170.2) * mm, "end": v(464.5, 186.03) * mm});
            skPoint(sketch, "E18.23.9.2", {"position": v(464.5, 168.2) * mm});
            skPoint(sketch, "E18.23.9.3", {"position": v(455.5, 168.2) * mm});
            skLineSegment(sketch, "E18.23.9.4", {"start": v(455.5, 186.03) * mm, "end": v(464.5, 186.03) * mm});
            skArc(sketch, "E18.23.9.5", {"start": v(455.5, 170.2) * mm, "mid": v(456.09, 168.8) * mm, "end": v(457.5, 168.2) * mm});
            skLineSegment(sketch, "E18.23.9.6", {"start": v(457.5, 168.2) * mm, "end": v(462.5, 168.2) * mm});
            skArc(sketch, "E18.23.9.7", {"start": v(462.5, 168.2) * mm, "mid": v(463.91, 168.8) * mm, "end": v(464.5, 170.2) * mm});
            skLineSegment(sketch, "E18.23.10.0", {"start": v(455.5, 135.56) * mm, "end": v(455.5, 151.38) * mm});
            skLineSegment(sketch, "E18.23.10.1", {"start": v(464.5, 135.56) * mm, "end": v(464.5, 151.38) * mm});
            skPoint(sketch, "E18.23.10.2", {"position": v(464.5, 133.56) * mm});
            skPoint(sketch, "E18.23.10.3", {"position": v(455.5, 133.56) * mm});
            skLineSegment(sketch, "E18.23.10.4", {"start": v(455.5, 151.38) * mm, "end": v(464.5, 151.38) * mm});
            skArc(sketch, "E18.23.10.5", {"start": v(455.5, 135.56) * mm, "mid": v(456.09, 134.15) * mm, "end": v(457.5, 133.56) * mm});
            skLineSegment(sketch, "E18.23.10.6", {"start": v(457.5, 133.56) * mm, "end": v(462.5, 133.56) * mm});
            skArc(sketch, "E18.23.10.7", {"start": v(462.5, 133.56) * mm, "mid": v(463.91, 134.15) * mm, "end": v(464.5, 135.56) * mm});
            skLineSegment(sketch, "E18.23.11.0", {"start": v(455.5, 100.92) * mm, "end": v(455.5, 116.74) * mm});
            skLineSegment(sketch, "E18.23.11.1", {"start": v(464.5, 100.92) * mm, "end": v(464.5, 116.74) * mm});
            skPoint(sketch, "E18.23.11.2", {"position": v(464.5, 98.92) * mm});
            skPoint(sketch, "E18.23.11.3", {"position": v(455.5, 98.92) * mm});
            skLineSegment(sketch, "E18.23.11.4", {"start": v(455.5, 116.74) * mm, "end": v(464.5, 116.74) * mm});
            skArc(sketch, "E18.23.11.5", {"start": v(455.5, 100.92) * mm, "mid": v(456.09, 99.5) * mm, "end": v(457.5, 98.92) * mm});
            skLineSegment(sketch, "E18.23.11.6", {"start": v(457.5, 98.92) * mm, "end": v(462.5, 98.92) * mm});
            skArc(sketch, "E18.23.11.7", {"start": v(462.5, 98.92) * mm, "mid": v(463.91, 99.5) * mm, "end": v(464.5, 100.92) * mm});
            skLineSegment(sketch, "E18.23.12.0", {"start": v(455.5, 66.28) * mm, "end": v(455.5, 82.1) * mm});
            skLineSegment(sketch, "E18.23.12.1", {"start": v(464.5, 66.28) * mm, "end": v(464.5, 82.1) * mm});
            skPoint(sketch, "E18.23.12.2", {"position": v(464.5, 64.28) * mm});
            skPoint(sketch, "E18.23.12.3", {"position": v(455.5, 64.28) * mm});
            skLineSegment(sketch, "E18.23.12.4", {"start": v(455.5, 82.1) * mm, "end": v(464.5, 82.1) * mm});
            skArc(sketch, "E18.23.12.5", {"start": v(455.5, 66.28) * mm, "mid": v(456.09, 64.87) * mm, "end": v(457.5, 64.28) * mm});
            skLineSegment(sketch, "E18.23.12.6", {"start": v(457.5, 64.28) * mm, "end": v(462.5, 64.28) * mm});
            skArc(sketch, "E18.23.12.7", {"start": v(462.5, 64.28) * mm, "mid": v(463.91, 64.87) * mm, "end": v(464.5, 66.28) * mm});
            skLineSegment(sketch, "E18.23.13.0", {"start": v(455.5, 31.64) * mm, "end": v(455.5, 47.46) * mm});
            skLineSegment(sketch, "E18.23.13.1", {"start": v(464.5, 31.64) * mm, "end": v(464.5, 47.46) * mm});
            skPoint(sketch, "E18.23.13.2", {"position": v(464.5, 29.64) * mm});
            skPoint(sketch, "E18.23.13.3", {"position": v(455.5, 29.64) * mm});
            skLineSegment(sketch, "E18.23.13.4", {"start": v(455.5, 47.46) * mm, "end": v(464.5, 47.46) * mm});
            skArc(sketch, "E18.23.13.5", {"start": v(455.5, 31.64) * mm, "mid": v(456.09, 30.23) * mm, "end": v(457.5, 29.64) * mm});
            skLineSegment(sketch, "E18.23.13.6", {"start": v(457.5, 29.64) * mm, "end": v(462.5, 29.64) * mm});
            skArc(sketch, "E18.23.13.7", {"start": v(462.5, 29.64) * mm, "mid": v(463.91, 30.23) * mm, "end": v(464.5, 31.64) * mm});
            skLineSegment(sketch, "E18.23.14.0", {"start": v(455.5, -3) * mm, "end": v(455.5, 12.82) * mm});
            skLineSegment(sketch, "E18.23.14.1", {"start": v(464.5, -3) * mm, "end": v(464.5, 12.82) * mm});
            skPoint(sketch, "E18.23.14.2", {"position": v(464.5, -5) * mm});
            skPoint(sketch, "E18.23.14.3", {"position": v(455.5, -5) * mm});
            skLineSegment(sketch, "E18.23.14.4", {"start": v(455.5, 12.82) * mm, "end": v(464.5, 12.82) * mm});
            skArc(sketch, "E18.23.14.5", {"start": v(455.5, -3) * mm, "mid": v(456.09, -4.41) * mm, "end": v(457.5, -5) * mm});
            skLineSegment(sketch, "E18.23.14.6", {"start": v(457.5, -5) * mm, "end": v(462.5, -5) * mm});
            skArc(sketch, "E18.23.14.7", {"start": v(462.5, -5) * mm, "mid": v(463.91, -4.41) * mm, "end": v(464.5, -3) * mm});
            skLineSegment(sketch, "E18.direction1", {"start": v(-4.5, 479.97) * mm, "end": v(15.5, 479.97) * mm, "construction": true});
            skLineSegment(sketch, "E18.direction2", {"start": v(-4.5, 479.97) * mm, "end": v(-4.5, 445.33) * mm, "construction": true});
            skSolve(sketch);
        }
        {
            var Q0;
            Q0 = qSketchRegion(id + "F6", true);
            extrude(context, id + "F7", {"entities" : qUnion([Q0]), "operationType" : NewBodyOperationType.REMOVE, "oppositeDirection" : true, "depth" : 2 * mm});
        }
    });
